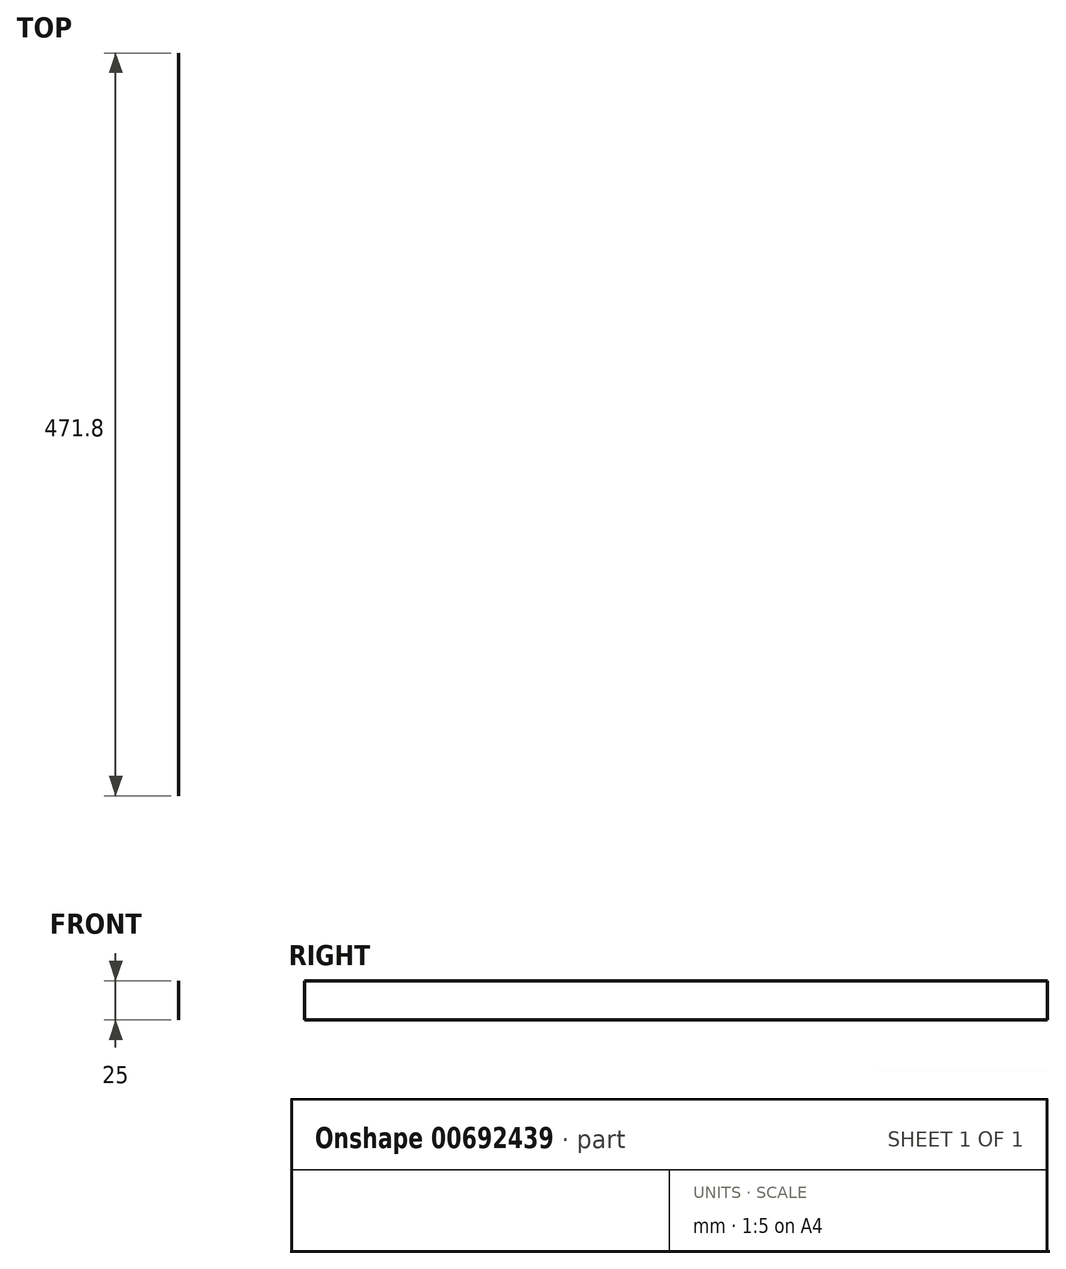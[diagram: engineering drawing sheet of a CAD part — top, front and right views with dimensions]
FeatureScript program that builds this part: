
annotation { "Feature Type Name" : "Feature", "Feature Type Description" : "" }
export const myFeature = defineFeature(function(context is Context, id is Id, definition is map)
    precondition{}
    {
        {
            var Q0;
            Q0=qCreatedBy(makeId("Top.planeOp"),FACE);
            var sketch = newSketch(context, id + "F0", { "sketchPlane" : qUnion([Q0])});
            skArc(sketch, "E0", {"start": v(533.57, 74.78) * mm, "mid": v(533.2, 75.41) * mm, "end": v(532.52, 75.66) * mm});
            skArc(sketch, "E1", {"start": v(533.22, 63.96) * mm, "mid": v(533.99, 69.35) * mm, "end": v(533.57, 74.78) * mm});
            skArc(sketch, "E2", {"start": v(528.74, 75.66) * mm, "mid": v(528, 75.36) * mm, "end": v(527.67, 74.63) * mm});
            skArc(sketch, "E3", {"start": v(532.18, 63.16) * mm, "mid": v(532.84, 63.38) * mm, "end": v(533.22, 63.96) * mm});
            skArc(sketch, "E4", {"start": v(527.25, 64.27) * mm, "mid": v(527.54, 63.49) * mm, "end": v(528.31, 63.16) * mm});
            skArc(sketch, "E5", {"start": v(670.33, -65.37) * mm, "mid": v(670, -64.64) * mm, "end": v(669.26, -64.34) * mm});
            skArc(sketch, "E6", {"start": v(669.69, -76.84) * mm, "mid": v(670.46, -76.51) * mm, "end": v(670.75, -75.73) * mm});
            skArc(sketch, "E7", {"start": v(665.48, -64.34) * mm, "mid": v(664.8, -64.59) * mm, "end": v(664.43, -65.22) * mm});
            skArc(sketch, "E8", {"start": v(664.43, -65.22) * mm, "mid": v(664.01, -70.65) * mm, "end": v(664.78, -76.04) * mm});
            skArc(sketch, "E9", {"start": v(664.78, -76.04) * mm, "mid": v(665.16, -76.62) * mm, "end": v(665.82, -76.84) * mm});
            skArc(sketch, "E10", {"start": v(704.93, -60.77) * mm, "mid": v(705.69, -60.46) * mm, "end": v(706, -59.7) * mm});
            skArc(sketch, "E11", {"start": v(672, -59.7) * mm, "mid": v(672.31, -60.46) * mm, "end": v(673.07, -60.77) * mm});
            skArc(sketch, "E12", {"start": v(706, -51.99) * mm, "mid": v(705.9, -51.55) * mm, "end": v(705.64, -51.19) * mm});
            skArc(sketch, "E13", {"start": v(672.36, -51.19) * mm, "mid": v(672.1, -51.55) * mm, "end": v(672, -51.99) * mm});
            skCircle(sketch, "E14", {"center": v(641.5, 233.4) * mm, "radius": 1.6 * mm});
            skCircle(sketch, "E15", {"center": v(614.5, 218.4) * mm, "radius": 1.6 * mm});
            skCircle(sketch, "E16", {"center": v(645.5, 187.4) * mm, "radius": 1.6 * mm});
            skCircle(sketch, "E17", {"center": v(614.5, 187.4) * mm, "radius": 1.6 * mm});
            skCircle(sketch, "E18", {"center": v(570.5, -185.55) * mm, "radius": 1.6 * mm});
            skCircle(sketch, "E19", {"center": v(570.5, -210.55) * mm, "radius": 1.6 * mm});
            skCircle(sketch, "E20", {"center": v(557.4, -171.86) * mm, "radius": 1.6 * mm});
            skCircle(sketch, "E21", {"center": v(640.6, -171.86) * mm, "radius": 1.6 * mm});
            skCircle(sketch, "E22", {"center": v(640, -195.9) * mm, "radius": 19 * mm});
            skCircle(sketch, "E23", {"center": v(723.7, -171.86) * mm, "radius": 1.6 * mm});
            skCircle(sketch, "E24", {"center": v(746.5, -171.86) * mm, "radius": 1.6 * mm});
            skCircle(sketch, "E25", {"center": v(746.5, -56.79) * mm, "radius": 1.6 * mm});
            skCircle(sketch, "E26", {"center": v(746.5, 58.28) * mm, "radius": 1.6 * mm});
            skCircle(sketch, "E27", {"center": v(746.5, 173.35) * mm, "radius": 1.6 * mm});
            skCircle(sketch, "E28", {"center": v(706.5, 233.4) * mm, "radius": 1.6 * mm});
            skCircle(sketch, "E29", {"center": v(645.5, 218.4) * mm, "radius": 1.6 * mm});
            skCircle(sketch, "E30", {"center": v(630, 202.9) * mm, "radius": 11 * mm});
            skCircle(sketch, "E31", {"center": v(568, 202.9) * mm, "radius": 11 * mm});
            skCircle(sketch, "E32", {"center": v(583.5, 218.4) * mm, "radius": 1.6 * mm});
            skCircle(sketch, "E33", {"center": v(583.5, 187.4) * mm, "radius": 1.6 * mm});
            skCircle(sketch, "E34", {"center": v(552.5, 187.4) * mm, "radius": 1.6 * mm});
            skCircle(sketch, "E35", {"center": v(552.5, 218.4) * mm, "radius": 1.6 * mm});
            skCircle(sketch, "E36", {"center": v(556.5, 233.4) * mm, "radius": 1.6 * mm});
            skCircle(sketch, "E37", {"center": v(491.5, 233.4) * mm, "radius": 1.6 * mm});
            skCircle(sketch, "E38", {"center": v(451.5, 173.35) * mm, "radius": 1.6 * mm});
            skCircle(sketch, "E39", {"center": v(451.5, 58.28) * mm, "radius": 1.6 * mm});
            skCircle(sketch, "E40", {"center": v(451.5, -171.86) * mm, "radius": 1.6 * mm});
            skCircle(sketch, "E41", {"center": v(474.3, -171.86) * mm, "radius": 1.6 * mm});
            skCircle(sketch, "E42", {"center": v(451.5, -56.79) * mm, "radius": 1.6 * mm});
            skCircle(sketch, "E43", {"center": v(704.86, -209.99) * mm, "radius": 1.6 * mm});
            skCircle(sketch, "E44", {"center": v(698.86, -217.99) * mm, "radius": 1.6 * mm});
            skCircle(sketch, "E45", {"center": v(692.86, -209.99) * mm, "radius": 1.6 * mm});
            skCircle(sketch, "E46", {"center": v(504.86, -209.99) * mm, "radius": 1.6 * mm});
            skCircle(sketch, "E47", {"center": v(498.86, -217.99) * mm, "radius": 1.6 * mm});
            skCircle(sketch, "E48", {"center": v(492.86, -209.99) * mm, "radius": 1.6 * mm});
            skCircle(sketch, "E49", {"center": v(690.74, 170.86) * mm, "radius": 1.6 * mm});
            skCircle(sketch, "E50", {"center": v(716, 217.9) * mm, "radius": 1.6 * mm});
            skCircle(sketch, "E51", {"center": v(507.26, 170.86) * mm, "radius": 1.6 * mm});
            skCircle(sketch, "E52", {"center": v(482, 217.9) * mm, "radius": 1.6 * mm});
            skCircle(sketch, "E53", {"center": v(623.6, -161.7) * mm, "radius": 1.6 * mm});
            skCircle(sketch, "E54", {"center": v(623.6, -140.1) * mm, "radius": 1.6 * mm});
            skCircle(sketch, "E55", {"center": v(618.3, -131.9) * mm, "radius": 1.6 * mm});
            skCircle(sketch, "E56", {"center": v(579.7, -131.9) * mm, "radius": 1.6 * mm});
            skCircle(sketch, "E57", {"center": v(574.4, -140.1) * mm, "radius": 1.6 * mm});
            skCircle(sketch, "E58", {"center": v(574.4, -161.7) * mm, "radius": 1.6 * mm});
            skArc(sketch, "E59", {"start": v(574.43, 4.56) * mm, "mid": v(574.01, -0.87) * mm, "end": v(574.78, -6.27) * mm});
            skArc(sketch, "E60", {"start": v(623.22, -6.27) * mm, "mid": v(623.99, -0.87) * mm, "end": v(623.57, 4.56) * mm});
            skArc(sketch, "E61", {"start": v(617.25, -5.96) * mm, "mid": v(617.54, -6.74) * mm, "end": v(618.31, -7.07) * mm});
            skArc(sketch, "E62", {"start": v(574.78, -6.27) * mm, "mid": v(575.16, -6.85) * mm, "end": v(575.82, -7.07) * mm});
            skArc(sketch, "E63", {"start": v(623.57, 4.56) * mm, "mid": v(623.2, 5.18) * mm, "end": v(622.52, 5.43) * mm});
            skArc(sketch, "E64", {"start": v(580.33, 4.4) * mm, "mid": v(580, 5.13) * mm, "end": v(579.26, 5.43) * mm});
            skArc(sketch, "E65", {"start": v(579.69, -7.07) * mm, "mid": v(580.46, -6.74) * mm, "end": v(580.75, -5.96) * mm});
            skArc(sketch, "E66", {"start": v(622.18, -7.07) * mm, "mid": v(622.84, -6.85) * mm, "end": v(623.22, -6.27) * mm});
            skArc(sketch, "E67", {"start": v(618.74, 5.43) * mm, "mid": v(618, 5.13) * mm, "end": v(617.67, 4.4) * mm});
            skArc(sketch, "E68", {"start": v(575.48, 5.43) * mm, "mid": v(574.8, 5.18) * mm, "end": v(574.43, 4.56) * mm});
            skArc(sketch, "E69", {"start": v(582.36, 18.59) * mm, "mid": v(582.1, 18.22) * mm, "end": v(582, 17.79) * mm});
            skArc(sketch, "E70", {"start": v(582, 10.07) * mm, "mid": v(582.31, 9.31) * mm, "end": v(583.07, 9) * mm});
            skArc(sketch, "E71", {"start": v(616, 17.79) * mm, "mid": v(615.9, 18.22) * mm, "end": v(615.64, 18.59) * mm});
            skArc(sketch, "E72", {"start": v(614.93, 9) * mm, "mid": v(615.69, 9.31) * mm, "end": v(616, 10.07) * mm});
            skArc(sketch, "E73", {"start": v(707.25, -75.73) * mm, "mid": v(707.54, -76.51) * mm, "end": v(708.31, -76.84) * mm});
            skArc(sketch, "E74", {"start": v(712.18, -76.84) * mm, "mid": v(712.84, -76.62) * mm, "end": v(713.22, -76.04) * mm});
            skArc(sketch, "E75", {"start": v(708.74, -64.34) * mm, "mid": v(708, -64.64) * mm, "end": v(707.67, -65.37) * mm});
            skArc(sketch, "E76", {"start": v(713.22, -76.04) * mm, "mid": v(713.99, -70.65) * mm, "end": v(713.57, -65.22) * mm});
            skArc(sketch, "E77", {"start": v(713.57, -65.22) * mm, "mid": v(713.2, -64.59) * mm, "end": v(712.52, -64.34) * mm});
            skArc(sketch, "E78", {"start": v(484.78, 63.96) * mm, "mid": v(485.16, 63.38) * mm, "end": v(485.82, 63.16) * mm});
            skArc(sketch, "E79", {"start": v(484.43, 74.78) * mm, "mid": v(484.01, 69.35) * mm, "end": v(484.78, 63.96) * mm});
            skArc(sketch, "E80", {"start": v(485.48, 75.66) * mm, "mid": v(484.8, 75.41) * mm, "end": v(484.43, 74.78) * mm});
            skArc(sketch, "E81", {"start": v(489.69, 63.16) * mm, "mid": v(490.46, 63.49) * mm, "end": v(490.75, 64.27) * mm});
            skArc(sketch, "E82", {"start": v(490.33, 74.63) * mm, "mid": v(490, 75.36) * mm, "end": v(489.26, 75.66) * mm});
            skArc(sketch, "E83", {"start": v(492.36, 88.81) * mm, "mid": v(492.1, 88.45) * mm, "end": v(492, 88.01) * mm});
            skArc(sketch, "E84", {"start": v(526, 88.01) * mm, "mid": v(525.9, 88.45) * mm, "end": v(525.64, 88.81) * mm});
            skArc(sketch, "E85", {"start": v(492, 80.3) * mm, "mid": v(492.31, 79.54) * mm, "end": v(493.07, 79.23) * mm});
            skArc(sketch, "E86", {"start": v(524.93, 79.23) * mm, "mid": v(525.69, 79.54) * mm, "end": v(526, 80.3) * mm});
            skCircle(sketch, "E87", {"center": v(595, -178.9) * mm, "radius": 1.8 * mm});
            skCircle(sketch, "E88", {"center": v(656, -179.9) * mm, "radius": 1.8 * mm});
            skCircle(sketch, "E89", {"center": v(656, -211.9) * mm, "radius": 1.8 * mm});
            skLineSegment(sketch, "E90", {"start": v(526, 88.01) * mm, "end": v(526, 80.3) * mm});
            skLineSegment(sketch, "E91", {"start": v(492, 80.3) * mm, "end": v(492, 88.01) * mm});
            skArc(sketch, "E92", {"start": v(525.64, 88.81) * mm, "mid": v(509, 95.16) * mm, "end": v(492.36, 88.81) * mm});
            skLineSegment(sketch, "E93", {"start": v(490.33, 74.63) * mm, "end": v(490.75, 64.27) * mm});
            skLineSegment(sketch, "E94", {"start": v(485.48, 75.66) * mm, "end": v(489.26, 75.66) * mm});
            skLineSegment(sketch, "E95", {"start": v(489.69, 63.16) * mm, "end": v(485.82, 63.16) * mm});
            skLineSegment(sketch, "E96", {"start": v(708.74, -64.34) * mm, "end": v(712.52, -64.34) * mm});
            skLineSegment(sketch, "E97", {"start": v(707.25, -75.73) * mm, "end": v(707.67, -65.37) * mm});
            skLineSegment(sketch, "E98", {"start": v(712.18, -76.84) * mm, "end": v(708.31, -76.84) * mm});
            skLineSegment(sketch, "E99", {"start": v(616, 17.79) * mm, "end": v(616, 10.07) * mm});
            skArc(sketch, "E100", {"start": v(615.64, 18.59) * mm, "mid": v(599, 24.93) * mm, "end": v(582.36, 18.59) * mm});
            skLineSegment(sketch, "E101", {"start": v(580.33, 4.4) * mm, "end": v(580.75, -5.96) * mm});
            skLineSegment(sketch, "E102", {"start": v(617.25, -5.96) * mm, "end": v(617.67, 4.4) * mm});
            skLineSegment(sketch, "E103", {"start": v(575.48, 5.43) * mm, "end": v(579.26, 5.43) * mm});
            skLineSegment(sketch, "E104", {"start": v(579.69, -7.07) * mm, "end": v(575.82, -7.07) * mm});
            skLineSegment(sketch, "E105", {"start": v(618.74, 5.43) * mm, "end": v(622.52, 5.43) * mm});
            skLineSegment(sketch, "E106", {"start": v(622.18, -7.07) * mm, "end": v(618.31, -7.07) * mm});
            skLineSegment(sketch, "E107", {"start": v(614.93, 9) * mm, "end": v(583.07, 9) * mm});
            skLineSegment(sketch, "E108", {"start": v(582, 10.07) * mm, "end": v(582, 17.79) * mm});
            skLineSegment(sketch, "E109", {"start": v(591.07, 177.78) * mm, "end": v(588.25, 174.96) * mm});
            skLineSegment(sketch, "E110", {"start": v(592.49, 176.37) * mm, "end": v(591.07, 177.78) * mm});
            skLineSegment(sketch, "E111", {"start": v(589.66, 173.54) * mm, "end": v(592.49, 176.37) * mm});
            skLineSegment(sketch, "E112", {"start": v(588.25, 174.96) * mm, "end": v(589.66, 173.54) * mm});
            skLineSegment(sketch, "E113", {"start": v(599.56, 169.3) * mm, "end": v(596.73, 166.47) * mm});
            skLineSegment(sketch, "E114", {"start": v(600.97, 167.88) * mm, "end": v(599.56, 169.3) * mm});
            skLineSegment(sketch, "E115", {"start": v(598.15, 165.06) * mm, "end": v(600.97, 167.88) * mm});
            skLineSegment(sketch, "E116", {"start": v(596.73, 166.47) * mm, "end": v(598.15, 165.06) * mm});
            skLineSegment(sketch, "E117", {"start": v(548.15, 165.06) * mm, "end": v(550.97, 167.88) * mm});
            skLineSegment(sketch, "E118", {"start": v(550.97, 167.88) * mm, "end": v(549.56, 169.3) * mm});
            skLineSegment(sketch, "E119", {"start": v(542.49, 176.37) * mm, "end": v(541.07, 177.78) * mm});
            skLineSegment(sketch, "E120", {"start": v(539.66, 173.54) * mm, "end": v(542.49, 176.37) * mm});
            skLineSegment(sketch, "E121", {"start": v(538.25, 174.96) * mm, "end": v(539.66, 173.54) * mm});
            skLineSegment(sketch, "E122", {"start": v(541.07, 177.78) * mm, "end": v(538.25, 174.96) * mm});
            skLineSegment(sketch, "E123", {"start": v(549.56, 169.3) * mm, "end": v(546.73, 166.47) * mm});
            skLineSegment(sketch, "E124", {"start": v(546.73, 166.47) * mm, "end": v(548.15, 165.06) * mm});
            skLineSegment(sketch, "E125", {"start": v(549.05, -13.73) * mm, "end": v(549.05, -9.73) * mm});
            skLineSegment(sketch, "E126", {"start": v(547.05, -13.73) * mm, "end": v(549.05, -13.73) * mm});
            skLineSegment(sketch, "E127", {"start": v(547.05, -9.73) * mm, "end": v(547.05, -13.73) * mm});
            skLineSegment(sketch, "E128", {"start": v(549.05, -9.73) * mm, "end": v(547.05, -9.73) * mm});
            skLineSegment(sketch, "E129", {"start": v(537.05, -13.73) * mm, "end": v(537.05, -9.73) * mm});
            skLineSegment(sketch, "E130", {"start": v(535.05, -13.73) * mm, "end": v(537.05, -13.73) * mm});
            skLineSegment(sketch, "E131", {"start": v(535.05, -9.73) * mm, "end": v(535.05, -13.73) * mm});
            skLineSegment(sketch, "E132", {"start": v(537.05, -9.73) * mm, "end": v(535.05, -9.73) * mm});
            skLineSegment(sketch, "E133", {"start": v(549.05, -113.73) * mm, "end": v(549.05, -109.73) * mm});
            skLineSegment(sketch, "E134", {"start": v(547.05, -113.73) * mm, "end": v(549.05, -113.73) * mm});
            skLineSegment(sketch, "E135", {"start": v(547.05, -109.73) * mm, "end": v(547.05, -113.73) * mm});
            skLineSegment(sketch, "E136", {"start": v(549.05, -109.73) * mm, "end": v(547.05, -109.73) * mm});
            skLineSegment(sketch, "E137", {"start": v(537.05, -113.73) * mm, "end": v(537.05, -109.73) * mm});
            skLineSegment(sketch, "E138", {"start": v(535.05, -113.73) * mm, "end": v(537.05, -113.73) * mm});
            skLineSegment(sketch, "E139", {"start": v(535.05, -109.73) * mm, "end": v(535.05, -113.73) * mm});
            skLineSegment(sketch, "E140", {"start": v(537.05, -109.73) * mm, "end": v(535.05, -109.73) * mm});
            skLineSegment(sketch, "E141", {"start": v(549.05, 86.27) * mm, "end": v(549.05, 90.27) * mm});
            skLineSegment(sketch, "E142", {"start": v(547.05, 86.27) * mm, "end": v(549.05, 86.27) * mm});
            skLineSegment(sketch, "E143", {"start": v(547.05, 90.27) * mm, "end": v(547.05, 86.27) * mm});
            skLineSegment(sketch, "E144", {"start": v(549.05, 90.27) * mm, "end": v(547.05, 90.27) * mm});
            skLineSegment(sketch, "E145", {"start": v(537.05, 86.27) * mm, "end": v(537.05, 90.27) * mm});
            skLineSegment(sketch, "E146", {"start": v(535.05, 86.27) * mm, "end": v(537.05, 86.27) * mm});
            skLineSegment(sketch, "E147", {"start": v(535.05, 90.27) * mm, "end": v(535.05, 86.27) * mm});
            skLineSegment(sketch, "E148", {"start": v(537.05, 90.27) * mm, "end": v(535.05, 90.27) * mm});
            skLineSegment(sketch, "E149", {"start": v(576.9, -146.4) * mm, "end": v(576.9, -155.4) * mm});
            skLineSegment(sketch, "E150", {"start": v(576.9, -155.4) * mm, "end": v(571.9, -155.4) * mm});
            skLineSegment(sketch, "E151", {"start": v(571.9, -155.4) * mm, "end": v(571.9, -146.4) * mm});
            skLineSegment(sketch, "E152", {"start": v(571.9, -146.4) * mm, "end": v(576.9, -146.4) * mm});
            skLineSegment(sketch, "E153", {"start": v(611.5, -129.4) * mm, "end": v(611.5, -134.4) * mm});
            skLineSegment(sketch, "E154", {"start": v(611.5, -134.4) * mm, "end": v(586.5, -134.4) * mm});
            skLineSegment(sketch, "E155", {"start": v(586.5, -134.4) * mm, "end": v(586.5, -129.4) * mm});
            skLineSegment(sketch, "E156", {"start": v(586.5, -129.4) * mm, "end": v(611.5, -129.4) * mm});
            skLineSegment(sketch, "E157", {"start": v(626.1, -146.4) * mm, "end": v(626.1, -155.4) * mm});
            skLineSegment(sketch, "E158", {"start": v(626.1, -155.4) * mm, "end": v(621.1, -155.4) * mm});
            skLineSegment(sketch, "E159", {"start": v(621.1, -155.4) * mm, "end": v(621.1, -146.4) * mm});
            skLineSegment(sketch, "E160", {"start": v(621.1, -146.4) * mm, "end": v(626.1, -146.4) * mm});
            skLineSegment(sketch, "E161", {"start": v(557.77, -204.9) * mm, "end": v(549.27, -204.9) * mm});
            skLineSegment(sketch, "E162", {"start": v(549.27, -204.9) * mm, "end": v(549.27, -191.5) * mm});
            skLineSegment(sketch, "E163", {"start": v(557.77, -191.5) * mm, "end": v(557.77, -204.9) * mm});
            skLineSegment(sketch, "E164", {"start": v(606.6, 224.42) * mm, "end": v(606.6, 228.42) * mm});
            skLineSegment(sketch, "E165", {"start": v(604.6, 224.42) * mm, "end": v(606.6, 224.42) * mm});
            skLineSegment(sketch, "E166", {"start": v(604.6, 228.42) * mm, "end": v(604.6, 224.42) * mm});
            skLineSegment(sketch, "E167", {"start": v(606.6, 228.42) * mm, "end": v(604.6, 228.42) * mm});
            skLineSegment(sketch, "E168", {"start": v(594.6, 224.42) * mm, "end": v(594.6, 228.42) * mm});
            skLineSegment(sketch, "E169", {"start": v(592.61, 224.42) * mm, "end": v(594.6, 224.42) * mm});
            skLineSegment(sketch, "E170", {"start": v(592.61, 228.42) * mm, "end": v(592.61, 224.42) * mm});
            skLineSegment(sketch, "E171", {"start": v(594.6, 228.42) * mm, "end": v(592.61, 228.42) * mm});
            skArc(sketch, "E172", {"start": v(590.35, 204.2) * mm, "mid": v(591.23, 202.07) * mm, "end": v(593.35, 201.2) * mm});
            skLineSegment(sketch, "E173", {"start": v(593.35, 201.2) * mm, "end": v(604.65, 201.2) * mm});
            skArc(sketch, "E174", {"start": v(604.65, 201.2) * mm, "mid": v(606.77, 202.07) * mm, "end": v(607.65, 204.2) * mm});
            skLineSegment(sketch, "E175", {"start": v(590.35, 217.7) * mm, "end": v(590.35, 204.2) * mm});
            skLineSegment(sketch, "E176", {"start": v(607.65, 204.2) * mm, "end": v(607.65, 217.7) * mm});
            skArc(sketch, "E177", {"start": v(607.65, 217.7) * mm, "mid": v(606.77, 219.81) * mm, "end": v(604.65, 220.7) * mm});
            skLineSegment(sketch, "E178", {"start": v(604.65, 220.7) * mm, "end": v(593.35, 220.7) * mm});
            skArc(sketch, "E179", {"start": v(593.35, 220.7) * mm, "mid": v(591.23, 219.81) * mm, "end": v(590.35, 217.7) * mm});
            skLineSegment(sketch, "E180", {"start": v(549.05, -183.73) * mm, "end": v(547.05, -183.73) * mm});
            skLineSegment(sketch, "E181", {"start": v(547.05, -183.73) * mm, "end": v(547.05, -179.73) * mm});
            skLineSegment(sketch, "E182", {"start": v(549.05, -179.73) * mm, "end": v(549.05, -183.73) * mm});
            skLineSegment(sketch, "E183", {"start": v(547.05, -179.73) * mm, "end": v(549.05, -179.73) * mm});
            skLineSegment(sketch, "E184", {"start": v(749, -235.9) * mm, "end": v(749, 235.9) * mm});
            skLineSegment(sketch, "E185", {"start": v(749, 235.9) * mm, "end": v(449, 235.9) * mm});
            skLineSegment(sketch, "E186", {"start": v(449, 235.9) * mm, "end": v(449, -235.9) * mm});
            skLineSegment(sketch, "E187", {"start": v(524.93, 79.23) * mm, "end": v(493.07, 79.23) * mm});
            skLineSegment(sketch, "E188", {"start": v(607, -214.4) * mm, "end": v(583, -214.4) * mm});
            skLineSegment(sketch, "E189", {"start": v(583, -214.4) * mm, "end": v(583, -183.4) * mm});
            skLineSegment(sketch, "E190", {"start": v(583, -183.4) * mm, "end": v(607, -183.4) * mm});
            skLineSegment(sketch, "E191", {"start": v(607, -183.4) * mm, "end": v(607, -214.4) * mm});
            skLineSegment(sketch, "E192", {"start": v(577, -205.55) * mm, "end": v(564, -205.55) * mm});
            skLineSegment(sketch, "E193", {"start": v(564, -205.55) * mm, "end": v(564, -190.55) * mm});
            skLineSegment(sketch, "E194", {"start": v(564, -190.55) * mm, "end": v(577, -190.55) * mm});
            skLineSegment(sketch, "E195", {"start": v(577, -190.55) * mm, "end": v(577, -205.55) * mm});
            skLineSegment(sketch, "E196", {"start": v(535.05, -179.73) * mm, "end": v(537.05, -179.73) * mm});
            skLineSegment(sketch, "E197", {"start": v(535.05, -183.73) * mm, "end": v(535.05, -179.73) * mm});
            skLineSegment(sketch, "E198", {"start": v(537.05, -179.73) * mm, "end": v(537.05, -183.73) * mm});
            skLineSegment(sketch, "E199", {"start": v(537.05, -183.73) * mm, "end": v(535.05, -183.73) * mm});
            skLineSegment(sketch, "E200", {"start": v(549.27, -191.5) * mm, "end": v(557.77, -191.5) * mm});
            skArc(sketch, "E201", {"start": v(719, -235.9) * mm, "mid": v(599, -227.33) * mm, "end": v(479, -235.9) * mm});
            skLineSegment(sketch, "E202", {"start": v(479, -235.9) * mm, "end": v(449, -235.9) * mm});
            skLineSegment(sketch, "E203", {"start": v(749, -235.9) * mm, "end": v(719, -235.9) * mm});
            skArc(sketch, "E204", {"start": v(705.64, -51.19) * mm, "mid": v(689, -44.84) * mm, "end": v(672.36, -51.19) * mm});
            skLineSegment(sketch, "E205", {"start": v(672, -59.7) * mm, "end": v(672, -51.99) * mm});
            skLineSegment(sketch, "E206", {"start": v(706, -51.99) * mm, "end": v(706, -59.7) * mm});
            skLineSegment(sketch, "E207", {"start": v(704.93, -60.77) * mm, "end": v(673.07, -60.77) * mm});
            skLineSegment(sketch, "E208", {"start": v(669.69, -76.84) * mm, "end": v(665.82, -76.84) * mm});
            skLineSegment(sketch, "E209", {"start": v(665.48, -64.34) * mm, "end": v(669.26, -64.34) * mm});
            skLineSegment(sketch, "E210", {"start": v(670.33, -65.37) * mm, "end": v(670.75, -75.73) * mm});
            skLineSegment(sketch, "E211", {"start": v(532.18, 63.16) * mm, "end": v(528.31, 63.16) * mm});
            skLineSegment(sketch, "E212", {"start": v(527.25, 64.27) * mm, "end": v(527.67, 74.63) * mm});
            skLineSegment(sketch, "E213", {"start": v(528.74, 75.66) * mm, "end": v(532.52, 75.66) * mm});
            skLineSegment(sketch, "E214", {"start": v(897.44, -172.86) * mm, "end": v(915.64, -172.86) * mm});
            skLineSegment(sketch, "E215", {"start": v(885.88, -182.05) * mm, "end": v(884.93, -182.6) * mm});
            skLineSegment(sketch, "E216", {"start": v(881.98, -184.3) * mm, "end": v(881.03, -184.85) * mm});
            skLineSegment(sketch, "E217", {"start": v(880.03, -183.12) * mm, "end": v(880.98, -182.57) * mm});
            skLineSegment(sketch, "E218", {"start": v(883.93, -180.87) * mm, "end": v(884.88, -180.32) * mm});
            skLineSegment(sketch, "E219", {"start": v(883.43, -180) * mm, "end": v(880.48, -181.7) * mm});
            skLineSegment(sketch, "E220", {"start": v(883.93, -180.87) * mm, "end": v(883.43, -180) * mm});
            skLineSegment(sketch, "E221", {"start": v(885.88, -182.05) * mm, "end": v(884.88, -180.32) * mm});
            skLineSegment(sketch, "E222", {"start": v(887.43, -186.93) * mm, "end": v(884.93, -182.6) * mm});
            skLineSegment(sketch, "E223", {"start": v(893.75, -183.28) * mm, "end": v(887.43, -186.93) * mm});
            skLineSegment(sketch, "E224", {"start": v(896.25, -187.61) * mm, "end": v(893.75, -183.28) * mm});
            skLineSegment(sketch, "E225", {"start": v(915.64, -176.42) * mm, "end": v(896.25, -187.61) * mm});
            skLineSegment(sketch, "E226", {"start": v(915.64, -172.86) * mm, "end": v(915.64, -176.42) * mm});
            skLineSegment(sketch, "E227", {"start": v(897.44, -177.86) * mm, "end": v(897.44, -172.86) * mm});
            skLineSegment(sketch, "E228", {"start": v(897.44, -177.86) * mm, "end": v(898.54, -177.86) * mm});
            skLineSegment(sketch, "E229", {"start": v(898.54, -177.86) * mm, "end": v(898.54, -179.86) * mm});
            skLineSegment(sketch, "E230", {"start": v(898.54, -179.86) * mm, "end": v(897.44, -179.86) * mm});
            skLineSegment(sketch, "E231", {"start": v(897.44, -180.86) * mm, "end": v(897.44, -179.86) * mm});
            skLineSegment(sketch, "E232", {"start": v(894.04, -180.86) * mm, "end": v(897.44, -180.86) * mm});
            skLineSegment(sketch, "E233", {"start": v(894.04, -179.86) * mm, "end": v(894.04, -180.86) * mm});
            skLineSegment(sketch, "E234", {"start": v(894.04, -179.86) * mm, "end": v(892.94, -179.86) * mm});
            skLineSegment(sketch, "E235", {"start": v(892.94, -179.86) * mm, "end": v(892.94, -177.86) * mm});
            skLineSegment(sketch, "E236", {"start": v(892.94, -177.86) * mm, "end": v(894.04, -177.86) * mm});
            skLineSegment(sketch, "E237", {"start": v(894.04, -172.86) * mm, "end": v(894.04, -177.86) * mm});
            skLineSegment(sketch, "E238", {"start": v(865.64, -172.86) * mm, "end": v(894.04, -172.86) * mm});
            skLineSegment(sketch, "E239", {"start": v(865.64, -185.06) * mm, "end": v(865.64, -172.86) * mm});
            skLineSegment(sketch, "E240", {"start": v(870.64, -185.06) * mm, "end": v(865.64, -185.06) * mm});
            skLineSegment(sketch, "E241", {"start": v(870.64, -185.06) * mm, "end": v(870.64, -183.96) * mm});
            skLineSegment(sketch, "E242", {"start": v(870.64, -183.96) * mm, "end": v(872.64, -183.96) * mm});
            skLineSegment(sketch, "E243", {"start": v(872.64, -183.96) * mm, "end": v(872.64, -185.06) * mm});
            skLineSegment(sketch, "E244", {"start": v(873.64, -185.06) * mm, "end": v(872.64, -185.06) * mm});
            skLineSegment(sketch, "E245", {"start": v(873.64, -188.46) * mm, "end": v(873.64, -185.06) * mm});
            skLineSegment(sketch, "E246", {"start": v(872.64, -188.46) * mm, "end": v(873.64, -188.46) * mm});
            skLineSegment(sketch, "E247", {"start": v(872.64, -188.46) * mm, "end": v(872.64, -189.56) * mm});
            skLineSegment(sketch, "E248", {"start": v(872.64, -189.56) * mm, "end": v(870.64, -189.56) * mm});
            skLineSegment(sketch, "E249", {"start": v(870.64, -189.56) * mm, "end": v(870.64, -188.46) * mm});
            skLineSegment(sketch, "E250", {"start": v(865.64, -188.46) * mm, "end": v(870.64, -188.46) * mm});
            skLineSegment(sketch, "E251", {"start": v(865.64, -202.86) * mm, "end": v(865.64, -188.46) * mm});
            skLineSegment(sketch, "E252", {"start": v(869.84, -202.86) * mm, "end": v(865.64, -202.86) * mm});
            skLineSegment(sketch, "E253", {"start": v(879.8, -197.11) * mm, "end": v(869.84, -202.86) * mm});
            skLineSegment(sketch, "E254", {"start": v(877.3, -192.78) * mm, "end": v(879.8, -197.11) * mm});
            skLineSegment(sketch, "E255", {"start": v(884.48, -188.63) * mm, "end": v(877.3, -192.78) * mm});
            skLineSegment(sketch, "E256", {"start": v(881.98, -184.3) * mm, "end": v(884.48, -188.63) * mm});
            skLineSegment(sketch, "E257", {"start": v(880.03, -183.12) * mm, "end": v(881.03, -184.85) * mm});
            skLineSegment(sketch, "E258", {"start": v(880.48, -181.7) * mm, "end": v(880.98, -182.57) * mm});
            skCircle(sketch, "E259", {"center": v(-352.5, 101.86) * mm, "radius": 1.6 * mm});
            skCircle(sketch, "E260", {"center": v(-346.5, 88.18) * mm, "radius": 1.6 * mm});
            skCircle(sketch, "E261", {"center": v(-346.5, 138.18) * mm, "radius": 1.6 * mm});
            skCircle(sketch, "E262", {"center": v(-211.5, 110.68) * mm, "radius": 3.5 * mm});
            skCircle(sketch, "E263", {"center": v(-201.5, 88.18) * mm, "radius": 1.6 * mm});
            skCircle(sketch, "E264", {"center": v(-188.3, 101.86) * mm, "radius": 1.6 * mm});
            skCircle(sketch, "E265", {"center": v(-201.5, 138.18) * mm, "radius": 1.6 * mm});
            skLineSegment(sketch, "E266", {"start": v(-190.8, 110.86) * mm, "end": v(-185.8, 110.86) * mm});
            skLineSegment(sketch, "E267", {"start": v(-190.8, 91.86) * mm, "end": v(-185.8, 91.86) * mm});
            skLineSegment(sketch, "E268", {"start": v(-185.8, 91.86) * mm, "end": v(-185.8, 110.86) * mm});
            skLineSegment(sketch, "E269", {"start": v(-190.8, 141.68) * mm, "end": v(-190.8, 110.86) * mm});
            skLineSegment(sketch, "E270", {"start": v(-350, 141.68) * mm, "end": v(-190.8, 141.68) * mm});
            skLineSegment(sketch, "E271", {"start": v(-350, 110.86) * mm, "end": v(-350, 141.68) * mm});
            skLineSegment(sketch, "E272", {"start": v(-350, 110.86) * mm, "end": v(-355, 110.86) * mm});
            skLineSegment(sketch, "E273", {"start": v(-355, 91.86) * mm, "end": v(-355, 110.86) * mm});
            skLineSegment(sketch, "E274", {"start": v(-355, 91.86) * mm, "end": v(-350, 91.86) * mm});
            skLineSegment(sketch, "E275", {"start": v(-350, 69.68) * mm, "end": v(-350, 91.86) * mm});
            skLineSegment(sketch, "E276", {"start": v(-190.8, 69.68) * mm, "end": v(-350, 69.68) * mm});
            skLineSegment(sketch, "E277", {"start": v(-190.8, 91.86) * mm, "end": v(-190.8, 69.68) * mm});
            skLineSegment(sketch, "E278", {"start": v(-237, 128.18) * mm, "end": v(-237, 86.68) * mm});
            skLineSegment(sketch, "E279", {"start": v(-237, 86.68) * mm, "end": v(-335, 86.68) * mm});
            skLineSegment(sketch, "E280", {"start": v(-335, 86.68) * mm, "end": v(-335, 128.18) * mm});
            skLineSegment(sketch, "E281", {"start": v(-335, 128.18) * mm, "end": v(-237, 128.18) * mm});
            skLineSegment(sketch, "E282", {"start": v(-1051, -170.45) * mm, "end": v(-1051, -87.6) * mm});
            skLineSegment(sketch, "E283", {"start": v(-1051, 64.1) * mm, "end": v(-761, 64.1) * mm});
            skLineSegment(sketch, "E284", {"start": v(-1046, -173.85) * mm, "end": v(-1051, -173.85) * mm});
            skLineSegment(sketch, "E285", {"start": v(-1044, -174.95) * mm, "end": v(-1046, -174.95) * mm});
            skLineSegment(sketch, "E286", {"start": v(-1043, -173.85) * mm, "end": v(-1044, -173.85) * mm});
            skLineSegment(sketch, "E287", {"start": v(-1046, -169.35) * mm, "end": v(-1044, -169.35) * mm});
            skLineSegment(sketch, "E288", {"start": v(-1051, -170.45) * mm, "end": v(-1046, -170.45) * mm});
            skLineSegment(sketch, "E289", {"start": v(-1044, -169.35) * mm, "end": v(-1044, -170.45) * mm});
            skLineSegment(sketch, "E290", {"start": v(-1044, -170.45) * mm, "end": v(-1043, -170.45) * mm});
            skLineSegment(sketch, "E291", {"start": v(-1046, -174.95) * mm, "end": v(-1046, -173.85) * mm});
            skLineSegment(sketch, "E292", {"start": v(-1044, -173.85) * mm, "end": v(-1044, -174.95) * mm});
            skLineSegment(sketch, "E293", {"start": v(-1043, -170.45) * mm, "end": v(-1043, -173.85) * mm});
            skLineSegment(sketch, "E294", {"start": v(-1046, -170.45) * mm, "end": v(-1046, -169.35) * mm});
            skLineSegment(sketch, "E295", {"start": v(-761, 64.1) * mm, "end": v(-761, 22.05) * mm});
            skLineSegment(sketch, "E296", {"start": v(-1051, 22.05) * mm, "end": v(-1051, 64.1) * mm});
            skLineSegment(sketch, "E297", {"start": v(-1051, 22.05) * mm, "end": v(-1046, 22.05) * mm});
            skLineSegment(sketch, "E298", {"start": v(-1046, 22.05) * mm, "end": v(-1046, 23.15) * mm});
            skLineSegment(sketch, "E299", {"start": v(-1046, 23.15) * mm, "end": v(-1044, 23.15) * mm});
            skLineSegment(sketch, "E300", {"start": v(-1044, 23.15) * mm, "end": v(-1044, 22.05) * mm});
            skLineSegment(sketch, "E301", {"start": v(-1044, 22.05) * mm, "end": v(-1043, 22.05) * mm});
            skLineSegment(sketch, "E302", {"start": v(-1043, 22.05) * mm, "end": v(-1043, 18.65) * mm});
            skLineSegment(sketch, "E303", {"start": v(-1043, 18.65) * mm, "end": v(-1044, 18.65) * mm});
            skLineSegment(sketch, "E304", {"start": v(-1044, 18.65) * mm, "end": v(-1044, 17.55) * mm});
            skLineSegment(sketch, "E305", {"start": v(-1044, 17.55) * mm, "end": v(-1046, 17.55) * mm});
            skLineSegment(sketch, "E306", {"start": v(-1046, 17.55) * mm, "end": v(-1046, 18.65) * mm});
            skLineSegment(sketch, "E307", {"start": v(-1046, 18.65) * mm, "end": v(-1051, 18.65) * mm});
            skLineSegment(sketch, "E308", {"start": v(-1051, -84.2) * mm, "end": v(-1051, 18.65) * mm});
            skLineSegment(sketch, "E309", {"start": v(-1051, -84.2) * mm, "end": v(-1046, -84.2) * mm});
            skLineSegment(sketch, "E310", {"start": v(-1046, -84.2) * mm, "end": v(-1046, -83.1) * mm});
            skLineSegment(sketch, "E311", {"start": v(-1046, -83.1) * mm, "end": v(-1044, -83.1) * mm});
            skLineSegment(sketch, "E312", {"start": v(-1044, -83.1) * mm, "end": v(-1044, -84.2) * mm});
            skLineSegment(sketch, "E313", {"start": v(-1044, -84.2) * mm, "end": v(-1043, -84.2) * mm});
            skLineSegment(sketch, "E314", {"start": v(-1043, -84.2) * mm, "end": v(-1043, -87.6) * mm});
            skLineSegment(sketch, "E315", {"start": v(-1043, -87.6) * mm, "end": v(-1044, -87.6) * mm});
            skLineSegment(sketch, "E316", {"start": v(-1044, -87.6) * mm, "end": v(-1044, -88.7) * mm});
            skLineSegment(sketch, "E317", {"start": v(-1044, -88.7) * mm, "end": v(-1046, -88.7) * mm});
            skLineSegment(sketch, "E318", {"start": v(-1046, -88.7) * mm, "end": v(-1046, -87.6) * mm});
            skLineSegment(sketch, "E319", {"start": v(-1046, -87.6) * mm, "end": v(-1051, -87.6) * mm});
            skLineSegment(sketch, "E320", {"start": v(-1051, -235.9) * mm, "end": v(-1051, -173.85) * mm});
            skLineSegment(sketch, "E321", {"start": v(-761, -235.9) * mm, "end": v(-1051, -235.9) * mm});
            skLineSegment(sketch, "E322", {"start": v(-761, -193.85) * mm, "end": v(-761, -235.9) * mm});
            skLineSegment(sketch, "E323", {"start": v(-761, -193.85) * mm, "end": v(-766, -193.85) * mm});
            skLineSegment(sketch, "E324", {"start": v(-766, -193.85) * mm, "end": v(-766, -194.9) * mm});
            skLineSegment(sketch, "E325", {"start": v(-766, -194.9) * mm, "end": v(-768, -194.9) * mm});
            skLineSegment(sketch, "E326", {"start": v(-768, -194.9) * mm, "end": v(-768, -193.85) * mm});
            skLineSegment(sketch, "E327", {"start": v(-768, -193.85) * mm, "end": v(-769, -193.85) * mm});
            skLineSegment(sketch, "E328", {"start": v(-769, -193.85) * mm, "end": v(-769, -190.45) * mm});
            skLineSegment(sketch, "E329", {"start": v(-769, -190.45) * mm, "end": v(-768, -190.45) * mm});
            skLineSegment(sketch, "E330", {"start": v(-768, -190.45) * mm, "end": v(-768, -189.35) * mm});
            skLineSegment(sketch, "E331", {"start": v(-768, -189.35) * mm, "end": v(-766, -189.35) * mm});
            skLineSegment(sketch, "E332", {"start": v(-766, -189.35) * mm, "end": v(-766, -190.45) * mm});
            skLineSegment(sketch, "E333", {"start": v(-766, -190.45) * mm, "end": v(-761, -190.45) * mm});
            skLineSegment(sketch, "E334", {"start": v(-761, -87.6) * mm, "end": v(-761, -190.45) * mm});
            skLineSegment(sketch, "E335", {"start": v(-761, -87.6) * mm, "end": v(-766, -87.6) * mm});
            skLineSegment(sketch, "E336", {"start": v(-766, -87.6) * mm, "end": v(-766, -88.7) * mm});
            skLineSegment(sketch, "E337", {"start": v(-766, -88.7) * mm, "end": v(-768, -88.7) * mm});
            skLineSegment(sketch, "E338", {"start": v(-768, -88.7) * mm, "end": v(-768, -87.6) * mm});
            skLineSegment(sketch, "E339", {"start": v(-768, -87.6) * mm, "end": v(-769, -87.6) * mm});
            skLineSegment(sketch, "E340", {"start": v(-769, -87.6) * mm, "end": v(-769, -84.2) * mm});
            skLineSegment(sketch, "E341", {"start": v(-769, -84.2) * mm, "end": v(-768, -84.2) * mm});
            skLineSegment(sketch, "E342", {"start": v(-768, -84.2) * mm, "end": v(-768, -83.1) * mm});
            skLineSegment(sketch, "E343", {"start": v(-768, -83.1) * mm, "end": v(-766, -83.1) * mm});
            skLineSegment(sketch, "E344", {"start": v(-766, -83.1) * mm, "end": v(-766, -84.2) * mm});
            skLineSegment(sketch, "E345", {"start": v(-766, -84.2) * mm, "end": v(-761, -84.2) * mm});
            skLineSegment(sketch, "E346", {"start": v(-761, 18.65) * mm, "end": v(-761, -84.2) * mm});
            skLineSegment(sketch, "E347", {"start": v(-761, 18.65) * mm, "end": v(-766, 18.65) * mm});
            skLineSegment(sketch, "E348", {"start": v(-766, 18.65) * mm, "end": v(-766, 17.55) * mm});
            skLineSegment(sketch, "E349", {"start": v(-766, 17.55) * mm, "end": v(-768, 17.55) * mm});
            skLineSegment(sketch, "E350", {"start": v(-768, 17.55) * mm, "end": v(-768, 18.65) * mm});
            skLineSegment(sketch, "E351", {"start": v(-768, 18.65) * mm, "end": v(-769, 18.65) * mm});
            skLineSegment(sketch, "E352", {"start": v(-769, 18.65) * mm, "end": v(-769, 22.05) * mm});
            skLineSegment(sketch, "E353", {"start": v(-769, 22.05) * mm, "end": v(-768, 22.05) * mm});
            skLineSegment(sketch, "E354", {"start": v(-768, 22.05) * mm, "end": v(-768, 23.15) * mm});
            skLineSegment(sketch, "E355", {"start": v(-768, 23.15) * mm, "end": v(-766, 23.15) * mm});
            skLineSegment(sketch, "E356", {"start": v(-766, 23.15) * mm, "end": v(-766, 22.05) * mm});
            skLineSegment(sketch, "E357", {"start": v(-766, 22.05) * mm, "end": v(-761, 22.05) * mm});
            skLineSegment(sketch, "E358", {"start": v(-875, -165.9) * mm, "end": v(-875, -107.9) * mm});
            skArc(sketch, "E359", {"start": v(-873, -107.9) * mm, "mid": v(-874, -106.9) * mm, "end": v(-875, -107.9) * mm});
            skLineSegment(sketch, "E360", {"start": v(-873, -107.9) * mm, "end": v(-873, -165.9) * mm});
            skArc(sketch, "E361", {"start": v(-875, -165.9) * mm, "mid": v(-874, -166.9) * mm, "end": v(-873, -165.9) * mm});
            skLineSegment(sketch, "E362", {"start": v(-881, -165.9) * mm, "end": v(-881, -107.9) * mm});
            skArc(sketch, "E363", {"start": v(-879, -107.9) * mm, "mid": v(-880, -106.9) * mm, "end": v(-881, -107.9) * mm});
            skLineSegment(sketch, "E364", {"start": v(-879, -107.9) * mm, "end": v(-879, -165.9) * mm});
            skArc(sketch, "E365", {"start": v(-881, -165.9) * mm, "mid": v(-880, -166.9) * mm, "end": v(-879, -165.9) * mm});
            skLineSegment(sketch, "E366", {"start": v(-893, -165.9) * mm, "end": v(-893, -107.9) * mm});
            skArc(sketch, "E367", {"start": v(-891, -107.9) * mm, "mid": v(-892, -106.9) * mm, "end": v(-893, -107.9) * mm});
            skLineSegment(sketch, "E368", {"start": v(-891, -107.9) * mm, "end": v(-891, -165.9) * mm});
            skArc(sketch, "E369", {"start": v(-893, -165.9) * mm, "mid": v(-892, -166.9) * mm, "end": v(-891, -165.9) * mm});
            skLineSegment(sketch, "E370", {"start": v(-887, -165.9) * mm, "end": v(-887, -107.9) * mm});
            skArc(sketch, "E371", {"start": v(-885, -107.9) * mm, "mid": v(-886, -106.9) * mm, "end": v(-887, -107.9) * mm});
            skLineSegment(sketch, "E372", {"start": v(-885, -107.9) * mm, "end": v(-885, -165.9) * mm});
            skArc(sketch, "E373", {"start": v(-887, -165.9) * mm, "mid": v(-886, -166.9) * mm, "end": v(-885, -165.9) * mm});
            skLineSegment(sketch, "E374", {"start": v(-899, -165.9) * mm, "end": v(-899, -107.9) * mm});
            skArc(sketch, "E375", {"start": v(-897, -107.9) * mm, "mid": v(-898, -106.9) * mm, "end": v(-899, -107.9) * mm});
            skLineSegment(sketch, "E376", {"start": v(-897, -107.9) * mm, "end": v(-897, -165.9) * mm});
            skArc(sketch, "E377", {"start": v(-899, -165.9) * mm, "mid": v(-898, -166.9) * mm, "end": v(-897, -165.9) * mm});
            skLineSegment(sketch, "E378", {"start": v(-905, -165.9) * mm, "end": v(-905, -107.9) * mm});
            skArc(sketch, "E379", {"start": v(-903, -107.9) * mm, "mid": v(-904, -106.9) * mm, "end": v(-905, -107.9) * mm});
            skLineSegment(sketch, "E380", {"start": v(-903, -107.9) * mm, "end": v(-903, -165.9) * mm});
            skArc(sketch, "E381", {"start": v(-905, -165.9) * mm, "mid": v(-904, -166.9) * mm, "end": v(-903, -165.9) * mm});
            skLineSegment(sketch, "E382", {"start": v(-917, -165.9) * mm, "end": v(-917, -107.9) * mm});
            skArc(sketch, "E383", {"start": v(-915, -107.9) * mm, "mid": v(-916, -106.9) * mm, "end": v(-917, -107.9) * mm});
            skLineSegment(sketch, "E384", {"start": v(-915, -107.9) * mm, "end": v(-915, -165.9) * mm});
            skArc(sketch, "E385", {"start": v(-917, -165.9) * mm, "mid": v(-916, -166.9) * mm, "end": v(-915, -165.9) * mm});
            skLineSegment(sketch, "E386", {"start": v(-911, -165.9) * mm, "end": v(-911, -107.9) * mm});
            skArc(sketch, "E387", {"start": v(-909, -107.9) * mm, "mid": v(-910, -106.9) * mm, "end": v(-911, -107.9) * mm});
            skLineSegment(sketch, "E388", {"start": v(-909, -107.9) * mm, "end": v(-909, -165.9) * mm});
            skArc(sketch, "E389", {"start": v(-911, -165.9) * mm, "mid": v(-910, -166.9) * mm, "end": v(-909, -165.9) * mm});
            skLineSegment(sketch, "E390", {"start": v(-923, -165.9) * mm, "end": v(-923, -107.9) * mm});
            skArc(sketch, "E391", {"start": v(-921, -107.9) * mm, "mid": v(-922, -106.9) * mm, "end": v(-923, -107.9) * mm});
            skLineSegment(sketch, "E392", {"start": v(-921, -107.9) * mm, "end": v(-921, -165.9) * mm});
            skArc(sketch, "E393", {"start": v(-923, -165.9) * mm, "mid": v(-922, -166.9) * mm, "end": v(-921, -165.9) * mm});
            skLineSegment(sketch, "E394", {"start": v(-929, -165.9) * mm, "end": v(-929, -107.9) * mm});
            skArc(sketch, "E395", {"start": v(-927, -107.9) * mm, "mid": v(-928, -106.9) * mm, "end": v(-929, -107.9) * mm});
            skLineSegment(sketch, "E396", {"start": v(-927, -107.9) * mm, "end": v(-927, -165.9) * mm});
            skArc(sketch, "E397", {"start": v(-929, -165.9) * mm, "mid": v(-928, -166.9) * mm, "end": v(-927, -165.9) * mm});
            skLineSegment(sketch, "E398", {"start": v(-941, -165.9) * mm, "end": v(-941, -107.9) * mm});
            skArc(sketch, "E399", {"start": v(-939, -107.9) * mm, "mid": v(-940, -106.9) * mm, "end": v(-941, -107.9) * mm});
            skLineSegment(sketch, "E400", {"start": v(-939, -107.9) * mm, "end": v(-939, -165.9) * mm});
            skArc(sketch, "E401", {"start": v(-941, -165.9) * mm, "mid": v(-940, -166.9) * mm, "end": v(-939, -165.9) * mm});
            skLineSegment(sketch, "E402", {"start": v(-935, -165.9) * mm, "end": v(-935, -107.9) * mm});
            skArc(sketch, "E403", {"start": v(-933, -107.9) * mm, "mid": v(-934, -106.9) * mm, "end": v(-935, -107.9) * mm});
            skLineSegment(sketch, "E404", {"start": v(-933, -107.9) * mm, "end": v(-933, -165.9) * mm});
            skArc(sketch, "E405", {"start": v(-935, -165.9) * mm, "mid": v(-934, -166.9) * mm, "end": v(-933, -165.9) * mm});
            skLineSegment(sketch, "E406", {"start": v(-953, -165.9) * mm, "end": v(-953, -107.9) * mm});
            skArc(sketch, "E407", {"start": v(-951, -107.9) * mm, "mid": v(-952, -106.9) * mm, "end": v(-953, -107.9) * mm});
            skLineSegment(sketch, "E408", {"start": v(-951, -107.9) * mm, "end": v(-951, -165.9) * mm});
            skArc(sketch, "E409", {"start": v(-953, -165.9) * mm, "mid": v(-952, -166.9) * mm, "end": v(-951, -165.9) * mm});
            skLineSegment(sketch, "E410", {"start": v(-947, -165.9) * mm, "end": v(-947, -107.9) * mm});
            skArc(sketch, "E411", {"start": v(-945, -107.9) * mm, "mid": v(-946, -106.9) * mm, "end": v(-947, -107.9) * mm});
            skLineSegment(sketch, "E412", {"start": v(-945, -107.9) * mm, "end": v(-945, -165.9) * mm});
            skArc(sketch, "E413", {"start": v(-947, -165.9) * mm, "mid": v(-946, -166.9) * mm, "end": v(-945, -165.9) * mm});
            skLineSegment(sketch, "E414", {"start": v(-959, -165.9) * mm, "end": v(-959, -107.9) * mm});
            skArc(sketch, "E415", {"start": v(-957, -107.9) * mm, "mid": v(-958, -106.9) * mm, "end": v(-959, -107.9) * mm});
            skLineSegment(sketch, "E416", {"start": v(-957, -107.9) * mm, "end": v(-957, -165.9) * mm});
            skArc(sketch, "E417", {"start": v(-959, -165.9) * mm, "mid": v(-958, -166.9) * mm, "end": v(-957, -165.9) * mm});
            skLineSegment(sketch, "E418", {"start": v(-965, -165.9) * mm, "end": v(-965, -107.9) * mm});
            skArc(sketch, "E419", {"start": v(-963, -107.9) * mm, "mid": v(-964, -106.9) * mm, "end": v(-965, -107.9) * mm});
            skLineSegment(sketch, "E420", {"start": v(-963, -107.9) * mm, "end": v(-963, -165.9) * mm});
            skArc(sketch, "E421", {"start": v(-965, -165.9) * mm, "mid": v(-964, -166.9) * mm, "end": v(-963, -165.9) * mm});
            skLineSegment(sketch, "E422", {"start": v(-869, -165.9) * mm, "end": v(-869, -107.9) * mm});
            skArc(sketch, "E423", {"start": v(-867, -107.9) * mm, "mid": v(-868, -106.9) * mm, "end": v(-869, -107.9) * mm});
            skLineSegment(sketch, "E424", {"start": v(-867, -107.9) * mm, "end": v(-867, -165.9) * mm});
            skArc(sketch, "E425", {"start": v(-869, -165.9) * mm, "mid": v(-868, -166.9) * mm, "end": v(-867, -165.9) * mm});
            skCircle(sketch, "E426", {"center": v(753.5, 173.4) * mm, "radius": 1.6 * mm});
            skCircle(sketch, "E427", {"center": v(753.5, 58.33) * mm, "radius": 1.6 * mm});
            skCircle(sketch, "E428", {"center": v(753.5, -56.74) * mm, "radius": 1.6 * mm});
            skCircle(sketch, "E429", {"center": v(753.5, -171.81) * mm, "radius": 1.6 * mm});
            skCircle(sketch, "E430", {"center": v(758.5, 217.4) * mm, "radius": 1.5 * mm});
            skCircle(sketch, "E431", {"center": v(793.5, 233.4) * mm, "radius": 1.6 * mm});
            skCircle(sketch, "E432", {"center": v(793.5, -171.81) * mm, "radius": 1.6 * mm});
            skCircle(sketch, "E433", {"center": v(853.5, -171.81) * mm, "radius": 1.6 * mm});
            skCircle(sketch, "E434", {"center": v(858.5, 233.4) * mm, "radius": 1.6 * mm});
            skCircle(sketch, "E435", {"center": v(859.3, -188.3) * mm, "radius": 1.6 * mm});
            skCircle(sketch, "E436", {"center": v(943.5, 233.4) * mm, "radius": 1.6 * mm});
            skCircle(sketch, "E437", {"center": v(1008.5, 233.4) * mm, "radius": 1.6 * mm});
            skCircle(sketch, "E438", {"center": v(1023.5, -188.3) * mm, "radius": 1.6 * mm});
            skCircle(sketch, "E439", {"center": v(1043.5, 217.4) * mm, "radius": 1.6 * mm});
            skCircle(sketch, "E440", {"center": v(1048.5, -56.74) * mm, "radius": 1.6 * mm});
            skCircle(sketch, "E441", {"center": v(1048.5, 58.33) * mm, "radius": 1.6 * mm});
            skCircle(sketch, "E442", {"center": v(1048.5, 173.4) * mm, "radius": 1.6 * mm});
            skCircle(sketch, "E443", {"center": v(1048.5, -171.81) * mm, "radius": 1.6 * mm});
            skLineSegment(sketch, "E444", {"start": v(1051, -235.9) * mm, "end": v(1021, -235.9) * mm});
            skArc(sketch, "E445", {"start": v(1021, -235.9) * mm, "mid": v(901, -227.33) * mm, "end": v(781, -235.9) * mm});
            skLineSegment(sketch, "E446", {"start": v(781, -235.9) * mm, "end": v(751, -235.9) * mm});
            skLineSegment(sketch, "E447", {"start": v(751, -235.9) * mm, "end": v(751, 235.9) * mm});
            skLineSegment(sketch, "E448", {"start": v(751, 235.9) * mm, "end": v(1051, 235.9) * mm});
            skLineSegment(sketch, "E449", {"start": v(1051, 235.9) * mm, "end": v(1051, -235.9) * mm});
            skLineSegment(sketch, "E450", {"start": v(1021, -209.7) * mm, "end": v(1021, 188.9) * mm});
            skArc(sketch, "E451", {"start": v(1021, 188.9) * mm, "mid": v(901, 197.47) * mm, "end": v(781, 188.9) * mm});
            skLineSegment(sketch, "E452", {"start": v(781, 188.9) * mm, "end": v(781, -169.4) * mm});
            skLineSegment(sketch, "E453", {"start": v(781, -169.4) * mm, "end": v(861.8, -169.4) * mm});
            skLineSegment(sketch, "E454", {"start": v(861.8, -169.4) * mm, "end": v(861.8, -209.7) * mm});
            skLineSegment(sketch, "E455", {"start": v(861.8, -209.7) * mm, "end": v(1021, -209.7) * mm});
            skArc(sketch, "E456", {"start": v(-25.63, 86.33) * mm, "mid": v(-30.47, 101.25) * mm, "end": v(-44.8, 107.62) * mm});
            skArc(sketch, "E457", {"start": v(-97.72, 99.4) * mm, "mid": v(-97.17, 97.72) * mm, "end": v(-95.56, 97) * mm});
            skArc(sketch, "E458", {"start": v(-54.23, 28.5) * mm, "mid": v(-37.5, 34.91) * mm, "end": v(-29.37, 50.87) * mm});
            skArc(sketch, "E459", {"start": v(-36.64, 85.84) * mm, "mid": v(-39.18, 93.66) * mm, "end": v(-46.68, 97) * mm});
            skArc(sketch, "E460", {"start": v(-102.12, 39.12) * mm, "mid": v(-103.58, 38.57) * mm, "end": v(-104.28, 37.18) * mm});
            skArc(sketch, "E461", {"start": v(-53.2, 39.12) * mm, "mid": v(-44.56, 42.44) * mm, "end": v(-40.35, 50.7) * mm});
            skEllipticalArc(sketch, "E462", {});
            skEllipticalArc(sketch, "E463", {});
            skEllipticalArc(sketch, "E464", {});
            skEllipticalArc(sketch, "E465", {});
            skEllipticalArc(sketch, "E466", {});
            skArc(sketch, "E467", {"start": v(35.2, 11.3) * mm, "mid": v(34.89, 11.47) * mm, "end": v(34.53, 11.51) * mm});
            skFitSpline(sketch, "E468", {"points": [v(67.13, 28.95) * mm, v(66.64, 29.35) * mm, v(66.36, 30.02) * mm, v(66.45, 30.83) * mm]});
            skFitSpline(sketch, "E469", {"points": [v(68.33, 28.55) * mm, v(67.87, 28.55) * mm, v(67.45, 28.7) * mm, v(67.13, 28.95) * mm]});
            skFitSpline(sketch, "E470", {"points": [v(75.4, 67.94) * mm, v(75.87, 67.94) * mm, v(76.28, 67.8) * mm, v(76.6, 67.53) * mm]});
            skFitSpline(sketch, "E471", {"points": [v(76.6, 67.53) * mm, v(77.1, 67.13) * mm, v(77.38, 66.47) * mm, v(77.3, 65.65) * mm]});
            skArc(sketch, "E472", {"start": v(-4.58, 9.19) * mm, "mid": v(-4.1, 9.28) * mm, "end": v(-3.69, 9.56) * mm});
            skEllipticalArc(sketch, "E473", {});
            skEllipticalArc(sketch, "E474", {});
            skArc(sketch, "E475", {"start": v(-4.84, 13.59) * mm, "mid": v(-4.68, 13.57) * mm, "end": v(-4.51, 13.55) * mm});
            skEllipticalArc(sketch, "E476", {});
            skEllipticalArc(sketch, "E477", {});
            skEllipticalArc(sketch, "E478", {});
            skEllipticalArc(sketch, "E479", {});
            skFitSpline(sketch, "E480", {"points": [v(-5.26, 28.95) * mm, v(-5.75, 29.35) * mm, v(-6.03, 30.02) * mm, v(-5.95, 30.83) * mm]});
            skFitSpline(sketch, "E481", {"points": [v(-4.06, 28.55) * mm, v(-4.52, 28.55) * mm, v(-4.94, 28.7) * mm, v(-5.26, 28.95) * mm]});
            skArc(sketch, "E482", {"start": v(-2.12, 175.46) * mm, "mid": v(-17.12, 160.46) * mm, "end": v(-2.12, 145.46) * mm});
            skCircle(sketch, "E483", {"center": v(101.25, -171.86) * mm, "radius": 1.6 * mm});
            skCircle(sketch, "E484", {"center": v(-5, -171.86) * mm, "radius": 1.6 * mm});
            skCircle(sketch, "E485", {"center": v(-111.25, -171.86) * mm, "radius": 1.6 * mm});
            skCircle(sketch, "E486", {"center": v(112.25, 226.15) * mm, "radius": 1.6 * mm});
            skCircle(sketch, "E487", {"center": v(132.25, 226.15) * mm, "radius": 1.6 * mm});
            skArc(sketch, "E488", {"start": v(57.88, 145.46) * mm, "mid": v(72.88, 160.46) * mm, "end": v(57.88, 175.46) * mm});
            skArc(sketch, "E489", {"start": v(9.4, 8.76) * mm, "mid": v(10, 9.4) * mm, "end": v(10.47, 10.13) * mm});
            skEllipticalArc(sketch, "E490", {});
            skEllipticalArc(sketch, "E491", {});
            skEllipticalArc(sketch, "E492", {});
            skArc(sketch, "E493", {"start": v(25.35, 14.84) * mm, "mid": v(24.98, 14.98) * mm, "end": v(24.6, 15.01) * mm});
            skEllipticalArc(sketch, "E494", {});
            skArc(sketch, "E495", {"start": v(89.92, 11.3) * mm, "mid": v(89.6, 11.47) * mm, "end": v(89.25, 11.51) * mm});
            skArc(sketch, "E496", {"start": v(-92.56, 64.71) * mm, "mid": v(-92.01, 63.03) * mm, "end": v(-90.4, 62.31) * mm});
            skArc(sketch, "E497", {"start": v(-89.76, 72.66) * mm, "mid": v(-91.2, 72.1) * mm, "end": v(-91.91, 70.72) * mm});
            skCircle(sketch, "E498", {"center": v(-5, -225.9) * mm, "radius": 1.6 * mm});
            skCircle(sketch, "E499", {"center": v(101.25, -225.9) * mm, "radius": 1.6 * mm});
            skCircle(sketch, "E500", {"center": v(-111.25, -225.9) * mm, "radius": 1.6 * mm});
            skCircle(sketch, "E501", {"center": v(-149, 201.4) * mm, "radius": 1.6 * mm});
            skArc(sketch, "E502", {"start": v(105, -235.9) * mm, "mid": v(-5, -228.39) * mm, "end": v(-115, -235.9) * mm});
            skLineSegment(sketch, "E503", {"start": v(105, -235.9) * mm, "end": v(145, -235.9) * mm});
            skLineSegment(sketch, "E504", {"start": v(-155, -235.9) * mm, "end": v(-115, -235.9) * mm});
            skLineSegment(sketch, "E505", {"start": v(-89.76, 72.66) * mm, "end": v(-64.65, 72.66) * mm});
            skLineSegment(sketch, "E506", {"start": v(-64.65, 72.66) * mm, "end": v(-65.75, 62.32) * mm});
            skLineSegment(sketch, "E507", {"start": v(-92.56, 64.71) * mm, "end": v(-91.91, 70.72) * mm});
            skLineSegment(sketch, "E508", {"start": v(-65.75, 62.32) * mm, "end": v(-90.4, 62.31) * mm});
            skFitSpline(sketch, "E509", {"points": [v(94.48, 15.93) * mm, v(94.72, 15.52) * mm, v(94.81, 15.02) * mm, v(94.75, 14.43) * mm]});
            skFitSpline(sketch, "E510", {"points": [v(94.75, 14.43) * mm, v(94.7, 13.92) * mm, v(94.54, 13.48) * mm, v(94.29, 13.11) * mm]});
            skFitSpline(sketch, "E511", {"points": [v(93.45, 16.76) * mm, v(93.9, 16.61) * mm, v(94.24, 16.33) * mm, v(94.48, 15.93) * mm]});
            skFitSpline(sketch, "E512", {"points": [v(94.29, 13.11) * mm, v(94.03, 12.74) * mm, v(93.7, 12.44) * mm, v(93.3, 12.21) * mm]});
            skEllipticalArc(sketch, "E513", {});
            skEllipticalArc(sketch, "E514", {});
            skLineSegment(sketch, "E515", {"start": v(86.71, 17) * mm, "end": v(91.45, 17) * mm});
            skEllipticalArc(sketch, "E516", {});
            skLineSegment(sketch, "E517", {"start": v(85.74, 7.78) * mm, "end": v(86.71, 17) * mm});
            skFitSpline(sketch, "E518", {"points": [v(92.96, 11.5) * mm, v(93.06, 11.43) * mm, v(93.2, 11.27) * mm, v(93.37, 11.02) * mm]});
            skLineSegment(sketch, "E519", {"start": v(88.6, 7.78) * mm, "end": v(85.74, 7.78) * mm});
            skEllipticalArc(sketch, "E520", {});
            skLineSegment(sketch, "E521", {"start": v(89, 11.52) * mm, "end": v(88.6, 7.78) * mm});
            skLineSegment(sketch, "E522", {"start": v(93.7, 10.45) * mm, "end": v(94.8, 7.78) * mm});
            skLineSegment(sketch, "E523", {"start": v(89.25, 11.52) * mm, "end": v(89, 11.52) * mm});
            skLineSegment(sketch, "E524", {"start": v(94.8, 7.78) * mm, "end": v(91.59, 7.78) * mm});
            skLineSegment(sketch, "E525", {"start": v(91.59, 7.78) * mm, "end": v(90.36, 10.6) * mm});
            skEllipticalArc(sketch, "E526", {});
            skEllipticalArc(sketch, "E527", {});
            skFitSpline(sketch, "E528", {"points": [v(90.38, 13.26) * mm, v(90.5, 13.26) * mm, v(90.76, 13.3) * mm, v(91.14, 13.39) * mm]});
            skEllipticalArc(sketch, "E529", {});
            skLineSegment(sketch, "E530", {"start": v(89.18, 13.26) * mm, "end": v(90.38, 13.26) * mm});
            skFitSpline(sketch, "E531", {"points": [v(91.87, 14.2) * mm, v(91.9, 14.5) * mm, v(91.83, 14.73) * mm, v(91.66, 14.9) * mm]});
            skLineSegment(sketch, "E532", {"start": v(89.37, 15.13) * mm, "end": v(89.18, 13.26) * mm});
            skFitSpline(sketch, "E533", {"points": [v(91.66, 14.9) * mm, v(91.49, 15.05) * mm, v(91.14, 15.13) * mm, v(90.62, 15.13) * mm]});
            skLineSegment(sketch, "E534", {"start": v(90.62, 15.13) * mm, "end": v(89.37, 15.13) * mm});
            skFitSpline(sketch, "E535", {"points": [v(77.06, 12.37) * mm, v(76.96, 11.44) * mm, v(77.06, 10.77) * mm, v(77.36, 10.36) * mm]});
            skFitSpline(sketch, "E536", {"points": [v(78.71, 9.76) * mm, v(79.32, 9.76) * mm, v(79.82, 9.95) * mm, v(80.2, 10.35) * mm]});
            skFitSpline(sketch, "E537", {"points": [v(80.2, 10.35) * mm, v(80.57, 10.75) * mm, v(80.81, 11.46) * mm, v(80.92, 12.5) * mm]});
            skEllipticalArc(sketch, "E538", {});
            skFitSpline(sketch, "E539", {"points": [v(77.8, 14.38) * mm, v(77.4, 13.98) * mm, v(77.16, 13.3) * mm, v(77.06, 12.37) * mm]});
            skLineSegment(sketch, "E540", {"start": v(68.87, 7.78) * mm, "end": v(66.02, 7.78) * mm});
            skLineSegment(sketch, "E541", {"start": v(69.6, 14.72) * mm, "end": v(68.87, 7.78) * mm});
            skLineSegment(sketch, "E542", {"start": v(66.02, 7.78) * mm, "end": v(66.75, 14.72) * mm});
            skLineSegment(sketch, "E543", {"start": v(72.5, 14.72) * mm, "end": v(69.6, 14.72) * mm});
            skLineSegment(sketch, "E544", {"start": v(66.75, 14.72) * mm, "end": v(63.85, 14.72) * mm});
            skLineSegment(sketch, "E545", {"start": v(72.74, 17) * mm, "end": v(72.5, 14.72) * mm});
            skLineSegment(sketch, "E546", {"start": v(63.85, 14.72) * mm, "end": v(64.09, 17) * mm});
            skLineSegment(sketch, "E547", {"start": v(64.09, 17) * mm, "end": v(72.74, 17) * mm});
            skLineSegment(sketch, "E548", {"start": v(58.82, 11.3) * mm, "end": v(58.15, 14.6) * mm});
            skLineSegment(sketch, "E549", {"start": v(58.15, 14.6) * mm, "end": v(56.8, 11.3) * mm});
            skLineSegment(sketch, "E550", {"start": v(56.8, 11.3) * mm, "end": v(58.82, 11.3) * mm});
            skLineSegment(sketch, "E551", {"start": v(50.23, 11.68) * mm, "end": v(45.8, 11.68) * mm});
            skLineSegment(sketch, "E552", {"start": v(50.42, 13.56) * mm, "end": v(50.23, 11.68) * mm});
            skLineSegment(sketch, "E553", {"start": v(45.8, 11.68) * mm, "end": v(45.6, 9.87) * mm});
            skLineSegment(sketch, "E554", {"start": v(46, 13.56) * mm, "end": v(50.42, 13.56) * mm});
            skLineSegment(sketch, "E555", {"start": v(45.6, 9.87) * mm, "end": v(50.52, 9.87) * mm});
            skLineSegment(sketch, "E556", {"start": v(46.15, 15.03) * mm, "end": v(46, 13.56) * mm});
            skLineSegment(sketch, "E557", {"start": v(50.52, 9.87) * mm, "end": v(50.3, 7.78) * mm});
            skLineSegment(sketch, "E558", {"start": v(50.92, 15.03) * mm, "end": v(46.15, 15.03) * mm});
            skLineSegment(sketch, "E559", {"start": v(50.3, 7.78) * mm, "end": v(42.53, 7.78) * mm});
            skLineSegment(sketch, "E560", {"start": v(51.13, 17) * mm, "end": v(50.92, 15.03) * mm});
            skLineSegment(sketch, "E561", {"start": v(42.53, 7.78) * mm, "end": v(43.5, 17) * mm});
            skLineSegment(sketch, "E562", {"start": v(43.5, 17) * mm, "end": v(51.13, 17) * mm});
            skFitSpline(sketch, "E563", {"points": [v(37.16, 14.2) * mm, v(37.19, 14.5) * mm, v(37.12, 14.73) * mm, v(36.95, 14.9) * mm]});
            skFitSpline(sketch, "E564", {"points": [v(36.95, 14.9) * mm, v(36.77, 15.05) * mm, v(36.43, 15.13) * mm, v(35.9, 15.13) * mm]});
            skLineSegment(sketch, "E565", {"start": v(35.9, 15.13) * mm, "end": v(34.66, 15.13) * mm});
            skLineSegment(sketch, "E566", {"start": v(34.66, 15.13) * mm, "end": v(34.46, 13.26) * mm});
            skLineSegment(sketch, "E567", {"start": v(34.46, 13.26) * mm, "end": v(35.66, 13.26) * mm});
            skFitSpline(sketch, "E568", {"points": [v(35.66, 13.26) * mm, v(35.8, 13.26) * mm, v(36.05, 13.3) * mm, v(36.43, 13.39) * mm]});
            skEllipticalArc(sketch, "E569", {});
            skArc(sketch, "E570", {"start": v(36.92, 13.67) * mm, "mid": v(37.08, 13.92) * mm, "end": v(37.16, 14.2) * mm});
            skFitSpline(sketch, "E571", {"points": [v(23.94, 9.76) * mm, v(24.48, 9.76) * mm, v(24.9, 9.91) * mm, v(25.22, 10.22) * mm]});
            skEllipticalArc(sketch, "E572", {});
            skFitSpline(sketch, "E573", {"points": [v(22.7, 10.33) * mm, v(22.96, 9.95) * mm, v(23.38, 9.76) * mm, v(23.94, 9.76) * mm]});
            skLineSegment(sketch, "E574", {"start": v(25.97, 11.55) * mm, "end": v(28.38, 10.8) * mm});
            skFitSpline(sketch, "E575", {"points": [v(22.45, 12.43) * mm, v(22.34, 11.4) * mm, v(22.42, 10.7) * mm, v(22.7, 10.33) * mm]});
            skEllipticalArc(sketch, "E576", {});
            skEllipticalArc(sketch, "E577", {});
            skEllipticalArc(sketch, "E578", {});
            skFitSpline(sketch, "E579", {"points": [v(25.95, 7.98) * mm, v(25.4, 7.74) * mm, v(24.7, 7.63) * mm, v(23.88, 7.63) * mm]});
            skFitSpline(sketch, "E580", {"points": [v(23.88, 7.63) * mm, v(22.88, 7.63) * mm, v(22.07, 7.77) * mm, v(21.47, 8.06) * mm]});
            skEllipticalArc(sketch, "E581", {});
            skEllipticalArc(sketch, "E582", {});
            skFitSpline(sketch, "E583", {"points": [v(26.09, 13.72) * mm, v(26.03, 14) * mm, v(25.96, 14.21) * mm, v(25.88, 14.34) * mm]});
            skEllipticalArc(sketch, "E584", {});
            skLineSegment(sketch, "E585", {"start": v(28.66, 14.28) * mm, "end": v(26.09, 13.72) * mm});
            skFitSpline(sketch, "E586", {"points": [v(19.6, 12.4) * mm, v(19.75, 13.93) * mm, v(20.28, 15.1) * mm, v(21.18, 15.92) * mm]});
            skEllipticalArc(sketch, "E587", {});
            skFitSpline(sketch, "E588", {"points": [v(24.75, 17.15) * mm, v(25.9, 17.15) * mm, v(26.8, 16.91) * mm, v(27.4, 16.44) * mm]});
            skLineSegment(sketch, "E589", {"start": v(45.04, 28) * mm, "end": v(44.88, 28) * mm});
            skLineSegment(sketch, "E590", {"start": v(33.22, 42.1) * mm, "end": v(34.46, 53.92) * mm});
            skLineSegment(sketch, "E591", {"start": v(60.93, 53.92) * mm, "end": v(59.69, 42.1) * mm});
            skEllipticalArc(sketch, "E592", {});
            skEllipticalArc(sketch, "E593", {});
            skFitSpline(sketch, "E594", {"points": [v(53.76, 53.92) * mm, v(54.22, 58.25) * mm, v(53.42, 61.87) * mm, v(48.54, 61.87) * mm]});
            skLineSegment(sketch, "E595", {"start": v(52.52, 42.1) * mm, "end": v(53.76, 53.92) * mm});
            skFitSpline(sketch, "E596", {"points": [v(48.54, 61.87) * mm, v(43.65, 61.87) * mm, v(42.09, 58.25) * mm, v(41.63, 53.92) * mm]});
            skFitSpline(sketch, "E597", {"points": [v(45.58, 34.61) * mm, v(50.63, 34.61) * mm, v(52.12, 38.32) * mm, v(52.52, 42.1) * mm]});
            skLineSegment(sketch, "E598", {"start": v(41.63, 53.92) * mm, "end": v(40.38, 42.1) * mm});
            skFitSpline(sketch, "E599", {"points": [v(40.38, 42.1) * mm, v(39.99, 38.32) * mm, v(40.7, 34.61) * mm, v(45.58, 34.61) * mm]});
            skEllipticalArc(sketch, "E600", {});
            skEllipticalArc(sketch, "E601", {});
            skEllipticalArc(sketch, "E602", {});
            skEllipticalArc(sketch, "E603", {});
            skEllipticalArc(sketch, "E604", {});
            skFitSpline(sketch, "E605", {"points": [v(8.04, 8.03) * mm, v(7.4, 7.87) * mm, v(6.83, 7.78) * mm, v(6.32, 7.78) * mm]});
            skEllipticalArc(sketch, "E606", {});
            skLineSegment(sketch, "E607", {"start": v(6.32, 7.78) * mm, "end": v(2.1, 7.78) * mm});
            skEllipticalArc(sketch, "E608", {});
            skLineSegment(sketch, "E609", {"start": v(2.1, 7.78) * mm, "end": v(3.06, 17) * mm});
            skLineSegment(sketch, "E610", {"start": v(3.06, 17) * mm, "end": v(7.29, 17) * mm});
            skEllipticalArc(sketch, "E611", {});
            skEllipticalArc(sketch, "E612", {});
            skEllipticalArc(sketch, "E613", {});
            skFitSpline(sketch, "E614", {"points": [v(7.14, 10.07) * mm, v(7.4, 10.2) * mm, v(7.63, 10.43) * mm, v(7.8, 10.76) * mm]});
            skLineSegment(sketch, "E615", {"start": v(6.4, 14.9) * mm, "end": v(5.69, 14.9) * mm});
            skEllipticalArc(sketch, "E616", {});
            skLineSegment(sketch, "E617", {"start": v(5.69, 14.9) * mm, "end": v(5.16, 9.87) * mm});
            skLineSegment(sketch, "E618", {"start": v(5.16, 9.87) * mm, "end": v(5.86, 9.87) * mm});
            skLineSegment(sketch, "E619", {"start": v(-38.33, 14.72) * mm, "end": v(-41.23, 14.72) * mm});
            skLineSegment(sketch, "E620", {"start": v(-38.1, 17) * mm, "end": v(-38.33, 14.72) * mm});
            skLineSegment(sketch, "E621", {"start": v(-41.23, 14.72) * mm, "end": v(-41.96, 7.78) * mm});
            skLineSegment(sketch, "E622", {"start": v(-46.74, 17) * mm, "end": v(-38.1, 17) * mm});
            skLineSegment(sketch, "E623", {"start": v(-41.96, 7.78) * mm, "end": v(-44.8, 7.78) * mm});
            skLineSegment(sketch, "E624", {"start": v(-46.98, 14.72) * mm, "end": v(-46.74, 17) * mm});
            skLineSegment(sketch, "E625", {"start": v(-44.8, 7.78) * mm, "end": v(-44.08, 14.72) * mm});
            skLineSegment(sketch, "E626", {"start": v(-44.08, 14.72) * mm, "end": v(-46.98, 14.72) * mm});
            skLineSegment(sketch, "E627", {"start": v(-17.05, 11.68) * mm, "end": v(-21.48, 11.68) * mm});
            skLineSegment(sketch, "E628", {"start": v(-16.86, 13.56) * mm, "end": v(-17.05, 11.68) * mm});
            skLineSegment(sketch, "E629", {"start": v(-21.48, 11.68) * mm, "end": v(-21.67, 9.87) * mm});
            skLineSegment(sketch, "E630", {"start": v(-21.29, 13.56) * mm, "end": v(-16.86, 13.56) * mm});
            skLineSegment(sketch, "E631", {"start": v(-21.67, 9.87) * mm, "end": v(-16.76, 9.87) * mm});
            skLineSegment(sketch, "E632", {"start": v(-21.13, 15.03) * mm, "end": v(-21.29, 13.56) * mm});
            skLineSegment(sketch, "E633", {"start": v(-16.76, 9.87) * mm, "end": v(-16.98, 7.78) * mm});
            skLineSegment(sketch, "E634", {"start": v(-16.36, 15.03) * mm, "end": v(-21.13, 15.03) * mm});
            skLineSegment(sketch, "E635", {"start": v(-16.98, 7.78) * mm, "end": v(-24.75, 7.78) * mm});
            skLineSegment(sketch, "E636", {"start": v(-16.15, 17) * mm, "end": v(-16.36, 15.03) * mm});
            skLineSegment(sketch, "E637", {"start": v(-24.75, 7.78) * mm, "end": v(-23.78, 17) * mm});
            skLineSegment(sketch, "E638", {"start": v(-23.78, 17) * mm, "end": v(-16.15, 17) * mm});
            skFitSpline(sketch, "E639", {"points": [v(-12.64, 34.61) * mm, v(-8.54, 34.61) * mm, v(-5.3, 38.47) * mm, v(-4.92, 42.1) * mm]});
            skLineSegment(sketch, "E640", {"start": v(-4.92, 42.1) * mm, "end": v(-4.5, 46.04) * mm});
            skLineSegment(sketch, "E641", {"start": v(-4.5, 46.04) * mm, "end": v(-12.98, 44.07) * mm});
            skFitSpline(sketch, "E642", {"points": [v(-12.98, 44.07) * mm, v(-16.2, 43.36) * mm, v(-17, 41.07) * mm, v(-17.15, 39.66) * mm]});
            skFitSpline(sketch, "E643", {"points": [v(-17.15, 39.66) * mm, v(-17.41, 37.13) * mm, v(-15.63, 34.61) * mm, v(-12.64, 34.61) * mm]});
            skLineSegment(sketch, "E644", {"start": v(73.12, -169.4) * mm, "end": v(73.12, -174.4) * mm});
            skLineSegment(sketch, "E645", {"start": v(23.12, -169.4) * mm, "end": v(73.12, -169.4) * mm});
            skLineSegment(sketch, "E646", {"start": v(73.12, -174.4) * mm, "end": v(23.12, -174.4) * mm});
            skLineSegment(sketch, "E647", {"start": v(23.12, -174.4) * mm, "end": v(23.12, -169.4) * mm});
            skLineSegment(sketch, "E648", {"start": v(-33.12, -174.4) * mm, "end": v(-83.12, -174.4) * mm});
            skLineSegment(sketch, "E649", {"start": v(-33.12, -169.4) * mm, "end": v(-33.12, -174.4) * mm});
            skLineSegment(sketch, "E650", {"start": v(-83.12, -174.4) * mm, "end": v(-83.12, -169.4) * mm});
            skLineSegment(sketch, "E651", {"start": v(-83.12, -169.4) * mm, "end": v(-33.12, -169.4) * mm});
            skLineSegment(sketch, "E652", {"start": v(57.88, 175.46) * mm, "end": v(-2.12, 175.46) * mm});
            skLineSegment(sketch, "E653", {"start": v(103.1, 225.9) * mm, "end": v(104.2, 225.9) * mm});
            skLineSegment(sketch, "E654", {"start": v(104.2, 225.9) * mm, "end": v(104.2, 223.9) * mm});
            skLineSegment(sketch, "E655", {"start": v(104.2, 223.9) * mm, "end": v(103.1, 223.9) * mm});
            skLineSegment(sketch, "E656", {"start": v(99.5, 223.9) * mm, "end": v(98.4, 223.9) * mm});
            skLineSegment(sketch, "E657", {"start": v(98.4, 223.9) * mm, "end": v(98.4, 225.9) * mm});
            skLineSegment(sketch, "E658", {"start": v(98.4, 225.9) * mm, "end": v(99.5, 225.9) * mm});
            skLineSegment(sketch, "E659", {"start": v(-3.2, 225.9) * mm, "end": v(-2.1, 225.9) * mm});
            skLineSegment(sketch, "E660", {"start": v(-2.1, 225.9) * mm, "end": v(-2.1, 223.9) * mm});
            skLineSegment(sketch, "E661", {"start": v(-2.1, 223.9) * mm, "end": v(-3.2, 223.9) * mm});
            skLineSegment(sketch, "E662", {"start": v(-6.8, 223.9) * mm, "end": v(-7.9, 223.9) * mm});
            skLineSegment(sketch, "E663", {"start": v(-7.9, 223.9) * mm, "end": v(-7.9, 225.9) * mm});
            skLineSegment(sketch, "E664", {"start": v(-7.9, 225.9) * mm, "end": v(-6.8, 225.9) * mm});
            skLineSegment(sketch, "E665", {"start": v(-109.5, 225.9) * mm, "end": v(-108.4, 225.9) * mm});
            skLineSegment(sketch, "E666", {"start": v(-108.4, 225.9) * mm, "end": v(-108.4, 223.9) * mm});
            skLineSegment(sketch, "E667", {"start": v(-108.4, 223.9) * mm, "end": v(-109.5, 223.9) * mm});
            skLineSegment(sketch, "E668", {"start": v(-113.1, 223.9) * mm, "end": v(-114.2, 223.9) * mm});
            skLineSegment(sketch, "E669", {"start": v(-114.2, 223.9) * mm, "end": v(-114.2, 225.9) * mm});
            skLineSegment(sketch, "E670", {"start": v(-114.2, 225.9) * mm, "end": v(-113.1, 225.9) * mm});
            skLineSegment(sketch, "E671", {"start": v(-148, -58.59) * mm, "end": v(-148, -59.69) * mm});
            skLineSegment(sketch, "E672", {"start": v(-148, -59.69) * mm, "end": v(-150, -59.69) * mm});
            skLineSegment(sketch, "E673", {"start": v(-150, -59.69) * mm, "end": v(-150, -58.59) * mm});
            skLineSegment(sketch, "E674", {"start": v(-150, 175.15) * mm, "end": v(-150, 176.25) * mm});
            skLineSegment(sketch, "E675", {"start": v(-150, 176.25) * mm, "end": v(-148, 176.25) * mm});
            skLineSegment(sketch, "E676", {"start": v(-148, 176.25) * mm, "end": v(-148, 175.15) * mm});
            skLineSegment(sketch, "E677", {"start": v(-148, 171.55) * mm, "end": v(-148, 170.45) * mm});
            skLineSegment(sketch, "E678", {"start": v(-148, 170.45) * mm, "end": v(-150, 170.45) * mm});
            skLineSegment(sketch, "E679", {"start": v(-150, 170.45) * mm, "end": v(-150, 171.55) * mm});
            skLineSegment(sketch, "E680", {"start": v(-150, 60.08) * mm, "end": v(-150, 61.18) * mm});
            skLineSegment(sketch, "E681", {"start": v(-150, 61.18) * mm, "end": v(-148, 61.18) * mm});
            skLineSegment(sketch, "E682", {"start": v(-148, 61.18) * mm, "end": v(-148, 60.08) * mm});
            skLineSegment(sketch, "E683", {"start": v(-148, 56.48) * mm, "end": v(-148, 55.38) * mm});
            skLineSegment(sketch, "E684", {"start": v(-148, 55.38) * mm, "end": v(-150, 55.38) * mm});
            skLineSegment(sketch, "E685", {"start": v(-150, 55.38) * mm, "end": v(-150, 56.48) * mm});
            skLineSegment(sketch, "E686", {"start": v(-150, -54.99) * mm, "end": v(-150, -53.89) * mm});
            skLineSegment(sketch, "E687", {"start": v(-150, -53.89) * mm, "end": v(-148, -53.89) * mm});
            skLineSegment(sketch, "E688", {"start": v(-148, -53.89) * mm, "end": v(-148, -54.99) * mm});
            skLineSegment(sketch, "E689", {"start": v(-150, -170.06) * mm, "end": v(-150, -168.96) * mm});
            skLineSegment(sketch, "E690", {"start": v(-150, -168.96) * mm, "end": v(-148, -168.96) * mm});
            skLineSegment(sketch, "E691", {"start": v(-148, -168.96) * mm, "end": v(-148, -170.06) * mm});
            skLineSegment(sketch, "E692", {"start": v(-148, -173.66) * mm, "end": v(-148, -174.76) * mm});
            skLineSegment(sketch, "E693", {"start": v(-148, -174.76) * mm, "end": v(-150, -174.76) * mm});
            skLineSegment(sketch, "E694", {"start": v(-150, -174.76) * mm, "end": v(-150, -173.66) * mm});
            skLineSegment(sketch, "E695", {"start": v(140, -173.66) * mm, "end": v(140, -174.76) * mm});
            skLineSegment(sketch, "E696", {"start": v(140, -174.76) * mm, "end": v(138, -174.76) * mm});
            skLineSegment(sketch, "E697", {"start": v(138, -174.76) * mm, "end": v(138, -173.66) * mm});
            skLineSegment(sketch, "E698", {"start": v(138, -170.06) * mm, "end": v(138, -168.96) * mm});
            skLineSegment(sketch, "E699", {"start": v(138, -168.96) * mm, "end": v(140, -168.96) * mm});
            skLineSegment(sketch, "E700", {"start": v(140, -168.96) * mm, "end": v(140, -170.06) * mm});
            skLineSegment(sketch, "E701", {"start": v(140, -58.59) * mm, "end": v(140, -59.69) * mm});
            skLineSegment(sketch, "E702", {"start": v(140, -59.69) * mm, "end": v(138, -59.69) * mm});
            skLineSegment(sketch, "E703", {"start": v(138, -59.69) * mm, "end": v(138, -58.59) * mm});
            skLineSegment(sketch, "E704", {"start": v(138, -54.99) * mm, "end": v(138, -53.89) * mm});
            skLineSegment(sketch, "E705", {"start": v(138, -53.89) * mm, "end": v(140, -53.89) * mm});
            skLineSegment(sketch, "E706", {"start": v(140, -53.89) * mm, "end": v(140, -54.99) * mm});
            skLineSegment(sketch, "E707", {"start": v(140, 56.48) * mm, "end": v(140, 55.38) * mm});
            skLineSegment(sketch, "E708", {"start": v(140, 55.38) * mm, "end": v(138, 55.38) * mm});
            skLineSegment(sketch, "E709", {"start": v(138, 55.38) * mm, "end": v(138, 56.48) * mm});
            skLineSegment(sketch, "E710", {"start": v(138, 60.08) * mm, "end": v(138, 61.18) * mm});
            skLineSegment(sketch, "E711", {"start": v(138, 61.18) * mm, "end": v(140, 61.18) * mm});
            skLineSegment(sketch, "E712", {"start": v(140, 61.18) * mm, "end": v(140, 60.08) * mm});
            skLineSegment(sketch, "E713", {"start": v(140, 171.55) * mm, "end": v(140, 170.45) * mm});
            skLineSegment(sketch, "E714", {"start": v(140, 170.45) * mm, "end": v(138, 170.45) * mm});
            skLineSegment(sketch, "E715", {"start": v(138, 170.45) * mm, "end": v(138, 171.55) * mm});
            skLineSegment(sketch, "E716", {"start": v(138, 175.15) * mm, "end": v(138, 176.25) * mm});
            skLineSegment(sketch, "E717", {"start": v(138, 176.25) * mm, "end": v(140, 176.25) * mm});
            skLineSegment(sketch, "E718", {"start": v(140, 176.25) * mm, "end": v(140, 175.15) * mm});
            skLineSegment(sketch, "E719", {"start": v(-150, -54.99) * mm, "end": v(-155, -54.99) * mm});
            skLineSegment(sketch, "E720", {"start": v(-155, -54.99) * mm, "end": v(-155, 56.48) * mm});
            skLineSegment(sketch, "E721", {"start": v(-155, 56.48) * mm, "end": v(-150, 56.48) * mm});
            skLineSegment(sketch, "E722", {"start": v(-148, 56.48) * mm, "end": v(-147, 56.48) * mm});
            skLineSegment(sketch, "E723", {"start": v(-147, 56.48) * mm, "end": v(-147, 60.08) * mm});
            skLineSegment(sketch, "E724", {"start": v(-147, 60.08) * mm, "end": v(-148, 60.08) * mm});
            skLineSegment(sketch, "E725", {"start": v(-150, 60.08) * mm, "end": v(-155, 60.08) * mm});
            skLineSegment(sketch, "E726", {"start": v(-155, 60.08) * mm, "end": v(-155, 171.55) * mm});
            skLineSegment(sketch, "E727", {"start": v(-155, 171.55) * mm, "end": v(-150, 171.55) * mm});
            skLineSegment(sketch, "E728", {"start": v(-148, 171.55) * mm, "end": v(-147, 171.55) * mm});
            skLineSegment(sketch, "E729", {"start": v(-147, 171.55) * mm, "end": v(-147, 175.15) * mm});
            skLineSegment(sketch, "E730", {"start": v(-147, 175.15) * mm, "end": v(-148, 175.15) * mm});
            skLineSegment(sketch, "E731", {"start": v(-150, 175.15) * mm, "end": v(-155, 175.15) * mm});
            skLineSegment(sketch, "E732", {"start": v(-155, 175.15) * mm, "end": v(-155, 230.9) * mm});
            skLineSegment(sketch, "E733", {"start": v(-155, 230.9) * mm, "end": v(-113.1, 230.9) * mm});
            skLineSegment(sketch, "E734", {"start": v(-113.1, 230.9) * mm, "end": v(-113.1, 225.9) * mm});
            skLineSegment(sketch, "E735", {"start": v(-113.1, 223.9) * mm, "end": v(-113.1, 222.9) * mm});
            skLineSegment(sketch, "E736", {"start": v(-113.1, 222.9) * mm, "end": v(-109.5, 222.9) * mm});
            skLineSegment(sketch, "E737", {"start": v(-109.5, 222.9) * mm, "end": v(-109.5, 223.9) * mm});
            skLineSegment(sketch, "E738", {"start": v(-109.5, 225.9) * mm, "end": v(-109.5, 230.9) * mm});
            skLineSegment(sketch, "E739", {"start": v(-109.5, 230.9) * mm, "end": v(-6.8, 230.9) * mm});
            skLineSegment(sketch, "E740", {"start": v(-6.8, 230.9) * mm, "end": v(-6.8, 225.9) * mm});
            skLineSegment(sketch, "E741", {"start": v(-6.8, 223.9) * mm, "end": v(-6.8, 222.9) * mm});
            skLineSegment(sketch, "E742", {"start": v(-6.8, 222.9) * mm, "end": v(-3.2, 222.9) * mm});
            skLineSegment(sketch, "E743", {"start": v(-3.2, 222.9) * mm, "end": v(-3.2, 223.9) * mm});
            skLineSegment(sketch, "E744", {"start": v(-3.2, 225.9) * mm, "end": v(-3.2, 230.9) * mm});
            skLineSegment(sketch, "E745", {"start": v(-3.2, 230.9) * mm, "end": v(99.5, 230.9) * mm});
            skLineSegment(sketch, "E746", {"start": v(99.5, 230.9) * mm, "end": v(99.5, 225.9) * mm});
            skLineSegment(sketch, "E747", {"start": v(99.5, 223.9) * mm, "end": v(99.5, 222.9) * mm});
            skLineSegment(sketch, "E748", {"start": v(99.5, 222.9) * mm, "end": v(103.1, 222.9) * mm});
            skLineSegment(sketch, "E749", {"start": v(103.1, 222.9) * mm, "end": v(103.1, 223.9) * mm});
            skLineSegment(sketch, "E750", {"start": v(103.1, 225.9) * mm, "end": v(103.1, 230.9) * mm});
            skLineSegment(sketch, "E751", {"start": v(103.1, 230.9) * mm, "end": v(145, 230.9) * mm});
            skLineSegment(sketch, "E752", {"start": v(145, 230.9) * mm, "end": v(145, 175.15) * mm});
            skLineSegment(sketch, "E753", {"start": v(145, 175.15) * mm, "end": v(140, 175.15) * mm});
            skLineSegment(sketch, "E754", {"start": v(138, 175.15) * mm, "end": v(137, 175.15) * mm});
            skLineSegment(sketch, "E755", {"start": v(137, 175.15) * mm, "end": v(137, 171.55) * mm});
            skLineSegment(sketch, "E756", {"start": v(137, 171.55) * mm, "end": v(138, 171.55) * mm});
            skLineSegment(sketch, "E757", {"start": v(140, 171.55) * mm, "end": v(145, 171.55) * mm});
            skLineSegment(sketch, "E758", {"start": v(145, 171.55) * mm, "end": v(145, 60.08) * mm});
            skLineSegment(sketch, "E759", {"start": v(145, 60.08) * mm, "end": v(140, 60.08) * mm});
            skLineSegment(sketch, "E760", {"start": v(138, 60.08) * mm, "end": v(137, 60.08) * mm});
            skLineSegment(sketch, "E761", {"start": v(137, 60.08) * mm, "end": v(137, 56.48) * mm});
            skLineSegment(sketch, "E762", {"start": v(137, 56.48) * mm, "end": v(138, 56.48) * mm});
            skLineSegment(sketch, "E763", {"start": v(140, 56.48) * mm, "end": v(145, 56.48) * mm});
            skLineSegment(sketch, "E764", {"start": v(145, 56.48) * mm, "end": v(145, -54.99) * mm});
            skLineSegment(sketch, "E765", {"start": v(145, -54.99) * mm, "end": v(140, -54.99) * mm});
            skLineSegment(sketch, "E766", {"start": v(138, -54.99) * mm, "end": v(137, -54.99) * mm});
            skLineSegment(sketch, "E767", {"start": v(137, -54.99) * mm, "end": v(137, -58.59) * mm});
            skLineSegment(sketch, "E768", {"start": v(137, -58.59) * mm, "end": v(138, -58.59) * mm});
            skLineSegment(sketch, "E769", {"start": v(140, -58.59) * mm, "end": v(145, -58.59) * mm});
            skLineSegment(sketch, "E770", {"start": v(145, -58.59) * mm, "end": v(145, -170.06) * mm});
            skLineSegment(sketch, "E771", {"start": v(145, -170.06) * mm, "end": v(140, -170.06) * mm});
            skLineSegment(sketch, "E772", {"start": v(138, -170.06) * mm, "end": v(137, -170.06) * mm});
            skLineSegment(sketch, "E773", {"start": v(137, -170.06) * mm, "end": v(137, -173.66) * mm});
            skLineSegment(sketch, "E774", {"start": v(137, -173.66) * mm, "end": v(138, -173.66) * mm});
            skLineSegment(sketch, "E775", {"start": v(140, -173.66) * mm, "end": v(145, -173.66) * mm});
            skLineSegment(sketch, "E776", {"start": v(145, -173.66) * mm, "end": v(145, -235.9) * mm});
            skLineSegment(sketch, "E777", {"start": v(-155, -235.9) * mm, "end": v(-155, -173.66) * mm});
            skLineSegment(sketch, "E778", {"start": v(-155, -173.66) * mm, "end": v(-150, -173.66) * mm});
            skLineSegment(sketch, "E779", {"start": v(-148, -173.66) * mm, "end": v(-147, -173.66) * mm});
            skLineSegment(sketch, "E780", {"start": v(-147, -173.66) * mm, "end": v(-147, -170.06) * mm});
            skLineSegment(sketch, "E781", {"start": v(-147, -170.06) * mm, "end": v(-148, -170.06) * mm});
            skLineSegment(sketch, "E782", {"start": v(-150, -170.06) * mm, "end": v(-155, -170.06) * mm});
            skLineSegment(sketch, "E783", {"start": v(-155, -170.06) * mm, "end": v(-155, -58.59) * mm});
            skLineSegment(sketch, "E784", {"start": v(-155, -58.59) * mm, "end": v(-150, -58.59) * mm});
            skLineSegment(sketch, "E785", {"start": v(-148, -58.59) * mm, "end": v(-147, -58.59) * mm});
            skLineSegment(sketch, "E786", {"start": v(-147, -58.59) * mm, "end": v(-147, -54.99) * mm});
            skLineSegment(sketch, "E787", {"start": v(-147, -54.99) * mm, "end": v(-148, -54.99) * mm});
            skLineSegment(sketch, "E788", {"start": v(-2.12, 145.46) * mm, "end": v(57.88, 145.46) * mm});
            skLineSegment(sketch, "E789", {"start": v(-102.12, 39.12) * mm, "end": v(-53.2, 39.12) * mm});
            skLineSegment(sketch, "E790", {"start": v(-40.35, 50.7) * mm, "end": v(-40, 54.04) * mm});
            skLineSegment(sketch, "E791", {"start": v(-40, 54.04) * mm, "end": v(-36.64, 85.84) * mm});
            skLineSegment(sketch, "E792", {"start": v(-46.68, 97) * mm, "end": v(-95.56, 97) * mm});
            skLineSegment(sketch, "E793", {"start": v(-97.72, 99.4) * mm, "end": v(-96.85, 107.62) * mm});
            skLineSegment(sketch, "E794", {"start": v(-96.85, 107.62) * mm, "end": v(-44.8, 107.62) * mm});
            skLineSegment(sketch, "E795", {"start": v(-25.63, 86.33) * mm, "end": v(-27.56, 68.06) * mm});
            skLineSegment(sketch, "E796", {"start": v(-27.56, 68.06) * mm, "end": v(-29.37, 50.87) * mm});
            skLineSegment(sketch, "E797", {"start": v(-54.23, 28.5) * mm, "end": v(-105.2, 28.5) * mm});
            skLineSegment(sketch, "E798", {"start": v(-105.2, 28.5) * mm, "end": v(-104.28, 37.18) * mm});
            skFitSpline(sketch, "E799", {"points": [v(74.21, 12.38) * mm, v(74.37, 13.88) * mm, v(74.91, 15.05) * mm, v(75.84, 15.9) * mm]});
            skEllipticalArc(sketch, "E800", {});
            skEllipticalArc(sketch, "E801", {});
            skEllipticalArc(sketch, "E802", {});
            skFitSpline(sketch, "E803", {"points": [v(82.94, 9.8) * mm, v(82.5, 9.12) * mm, v(81.93, 8.58) * mm, v(81.2, 8.2) * mm]});
            skFitSpline(sketch, "E804", {"points": [v(81.2, 8.2) * mm, v(80.48, 7.82) * mm, v(79.6, 7.63) * mm, v(78.58, 7.63) * mm]});
            skFitSpline(sketch, "E805", {"points": [v(78.58, 7.63) * mm, v(77.54, 7.63) * mm, v(76.7, 7.8) * mm, v(76.06, 8.12) * mm]});
            skFitSpline(sketch, "E806", {"points": [v(76.06, 8.12) * mm, v(75.4, 8.45) * mm, v(74.91, 8.98) * mm, v(74.57, 9.7) * mm]});
            skFitSpline(sketch, "E807", {"points": [v(74.57, 9.7) * mm, v(74.22, 10.4) * mm, v(74.1, 11.3) * mm, v(74.21, 12.38) * mm]});
            skLineSegment(sketch, "E808", {"start": v(52.45, 7.78) * mm, "end": v(56.88, 17) * mm});
            skLineSegment(sketch, "E809", {"start": v(56.88, 17) * mm, "end": v(59.99, 17) * mm});
            skLineSegment(sketch, "E810", {"start": v(59.99, 17) * mm, "end": v(62.48, 7.78) * mm});
            skLineSegment(sketch, "E811", {"start": v(62.48, 7.78) * mm, "end": v(59.5, 7.78) * mm});
            skLineSegment(sketch, "E812", {"start": v(59.5, 7.78) * mm, "end": v(59.2, 9.3) * mm});
            skLineSegment(sketch, "E813", {"start": v(59.2, 9.3) * mm, "end": v(55.97, 9.3) * mm});
            skLineSegment(sketch, "E814", {"start": v(55.97, 9.3) * mm, "end": v(55.36, 7.78) * mm});
            skLineSegment(sketch, "E815", {"start": v(55.36, 7.78) * mm, "end": v(52.45, 7.78) * mm});
            skLineSegment(sketch, "E816", {"start": v(33.89, 7.78) * mm, "end": v(31.03, 7.78) * mm});
            skLineSegment(sketch, "E817", {"start": v(31.03, 7.78) * mm, "end": v(32, 17) * mm});
            skLineSegment(sketch, "E818", {"start": v(32, 17) * mm, "end": v(36.74, 17) * mm});
            skEllipticalArc(sketch, "E819", {});
            skEllipticalArc(sketch, "E820", {});
            skFitSpline(sketch, "E821", {"points": [v(40.04, 14.43) * mm, v(39.98, 13.92) * mm, v(39.83, 13.48) * mm, v(39.57, 13.11) * mm]});
            skFitSpline(sketch, "E822", {"points": [v(39.57, 13.11) * mm, v(39.32, 12.74) * mm, v(38.98, 12.44) * mm, v(38.58, 12.21) * mm]});
            skEllipticalArc(sketch, "E823", {});
            skEllipticalArc(sketch, "E824", {});
            skFitSpline(sketch, "E825", {"points": [v(38.25, 11.5) * mm, v(38.34, 11.43) * mm, v(38.48, 11.27) * mm, v(38.65, 11.02) * mm]});
            skFitSpline(sketch, "E826", {"points": [v(38.65, 11.02) * mm, v(38.82, 10.78) * mm, v(38.94, 10.58) * mm, v(38.99, 10.45) * mm]});
            skLineSegment(sketch, "E827", {"start": v(38.99, 10.45) * mm, "end": v(40.09, 7.78) * mm});
            skLineSegment(sketch, "E828", {"start": v(40.09, 7.78) * mm, "end": v(36.87, 7.78) * mm});
            skLineSegment(sketch, "E829", {"start": v(36.87, 7.78) * mm, "end": v(35.65, 10.6) * mm});
            skEllipticalArc(sketch, "E830", {});
            skLineSegment(sketch, "E831", {"start": v(34.53, 11.52) * mm, "end": v(34.28, 11.52) * mm});
            skLineSegment(sketch, "E832", {"start": v(34.28, 11.52) * mm, "end": v(33.89, 7.78) * mm});
            skFitSpline(sketch, "E833", {"points": [v(77.24, 65.18) * mm, v(79.94, 67.62) * mm, v(81.3, 68.5) * mm, v(85.94, 68.5) * mm]});
            skFitSpline(sketch, "E834", {"points": [v(85.94, 68.5) * mm, v(87.28, 68.5) * mm, v(88.12, 67.54) * mm, v(88, 66.36) * mm]});
            skLineSegment(sketch, "E835", {"start": v(88, 66.36) * mm, "end": v(87.76, 64.08) * mm});
            skFitSpline(sketch, "E836", {"points": [v(87.76, 64.08) * mm, v(87.63, 62.9) * mm, v(86.58, 61.87) * mm, v(85.24, 61.87) * mm]});
            skFitSpline(sketch, "E837", {"points": [v(85.24, 61.87) * mm, v(78.15, 61.87) * mm, v(76.53, 58.4) * mm, v(76.2, 55.26) * mm]});
            skLineSegment(sketch, "E838", {"start": v(76.2, 55.26) * mm, "end": v(73.62, 30.83) * mm});
            skFitSpline(sketch, "E839", {"points": [v(73.62, 30.83) * mm, v(73.47, 29.5) * mm, v(72.43, 28.55) * mm, v(71.25, 28.55) * mm]});
            skLineSegment(sketch, "E840", {"start": v(71.25, 28.55) * mm, "end": v(68.33, 28.55) * mm});
            skLineSegment(sketch, "E841", {"start": v(66.45, 30.83) * mm, "end": v(70.12, 65.65) * mm});
            skFitSpline(sketch, "E842", {"points": [v(70.12, 65.65) * mm, v(70.26, 67) * mm, v(71.3, 67.94) * mm, v(72.49, 67.94) * mm]});
            skLineSegment(sketch, "E843", {"start": v(72.49, 67.94) * mm, "end": v(75.4, 67.94) * mm});
            skLineSegment(sketch, "E844", {"start": v(77.3, 65.65) * mm, "end": v(77.24, 65.18) * mm});
            skLineSegment(sketch, "E845", {"start": v(24.22, 28.55) * mm, "end": v(22.96, 28.55) * mm});
            skFitSpline(sketch, "E846", {"points": [v(22.96, 28.55) * mm, v(14.77, 28.55) * mm, v(10.7, 31.86) * mm, v(11.69, 41.15) * mm]});
            skLineSegment(sketch, "E847", {"start": v(11.69, 41.15) * mm, "end": v(13.74, 60.61) * mm});
            skLineSegment(sketch, "E848", {"start": v(13.74, 60.61) * mm, "end": v(12, 60.61) * mm});
            skLineSegment(sketch, "E849", {"start": v(10.03, 62.82) * mm, "end": v(10.26, 64.95) * mm});
            skLineSegment(sketch, "E850", {"start": v(12.7, 67.23) * mm, "end": v(14.44, 67.23) * mm});
            skLineSegment(sketch, "E851", {"start": v(14.44, 67.23) * mm, "end": v(15.78, 79.91) * mm});
            skLineSegment(sketch, "E852", {"start": v(18.22, 82.12) * mm, "end": v(20.9, 82.12) * mm});
            skLineSegment(sketch, "E853", {"start": v(22.95, 79.91) * mm, "end": v(21.6, 67.23) * mm});
            skLineSegment(sketch, "E854", {"start": v(21.6, 67.23) * mm, "end": v(27.68, 67.23) * mm});
            skLineSegment(sketch, "E855", {"start": v(29.73, 65.02) * mm, "end": v(29.5, 62.9) * mm});
            skLineSegment(sketch, "E856", {"start": v(26.98, 60.61) * mm, "end": v(20.91, 60.61) * mm});
            skLineSegment(sketch, "E857", {"start": v(20.91, 60.61) * mm, "end": v(18.86, 41.15) * mm});
            skFitSpline(sketch, "E858", {"points": [v(18.86, 41.15) * mm, v(18.38, 36.58) * mm, v(20.43, 35.16) * mm, v(23.66, 35.16) * mm]});
            skLineSegment(sketch, "E859", {"start": v(23.66, 35.16) * mm, "end": v(24.92, 35.16) * mm});
            skLineSegment(sketch, "E860", {"start": v(26.9, 33.04) * mm, "end": v(26.67, 30.83) * mm});
            skEllipticalArc(sketch, "E861", {});
            skEllipticalArc(sketch, "E862", {});
            skFitSpline(sketch, "E863", {"points": [v(-1.31, 16.48) * mm, v(-0.82, 16.03) * mm, v(-0.62, 15.46) * mm, v(-0.69, 14.79) * mm]});
            skEllipticalArc(sketch, "E864", {});
            skFitSpline(sketch, "E865", {"points": [v(-1.13, 13.7) * mm, v(-1.38, 13.38) * mm, v(-1.74, 13.1) * mm, v(-2.2, 12.86) * mm]});
            skFitSpline(sketch, "E866", {"points": [v(-2.2, 12.86) * mm, v(-1.86, 12.77) * mm, v(-1.6, 12.67) * mm, v(-1.42, 12.55) * mm]});
            skEllipticalArc(sketch, "E867", {});
            skFitSpline(sketch, "E868", {"points": [v(-0.78, 11.8) * mm, v(-0.65, 11.5) * mm, v(-0.6, 11.13) * mm, v(-0.65, 10.7) * mm]});
            skFitSpline(sketch, "E869", {"points": [v(-0.65, 10.7) * mm, v(-0.7, 10.17) * mm, v(-0.9, 9.65) * mm, v(-1.23, 9.16) * mm]});
            skEllipticalArc(sketch, "E870", {});
            skFitSpline(sketch, "E871", {"points": [v(-4.68, 7.62) * mm, v(-5.52, 7.62) * mm, v(-6.17, 7.72) * mm, v(-6.63, 7.92) * mm]});
            skFitSpline(sketch, "E872", {"points": [v(-6.63, 7.92) * mm, v(-7.1, 8.12) * mm, v(-7.46, 8.4) * mm, v(-7.74, 8.78) * mm]});
            skFitSpline(sketch, "E873", {"points": [v(-7.74, 8.78) * mm, v(-8, 9.16) * mm, v(-8.2, 9.64) * mm, v(-8.3, 10.21) * mm]});
            skLineSegment(sketch, "E874", {"start": v(-8.3, 10.21) * mm, "end": v(-5.71, 10.55) * mm});
            skFitSpline(sketch, "E875", {"points": [v(-5.71, 10.55) * mm, v(-5.67, 10.04) * mm, v(-5.55, 9.68) * mm, v(-5.36, 9.48) * mm]});
            skEllipticalArc(sketch, "E876", {});
            skFitSpline(sketch, "E877", {"points": [v(-3.24, 10.56) * mm, v(-3.2, 11) * mm, v(-3.27, 11.32) * mm, v(-3.46, 11.56) * mm]});
            skFitSpline(sketch, "E878", {"points": [v(-4.32, 11.9) * mm, v(-4.52, 11.9) * mm, v(-4.8, 11.86) * mm, v(-5.16, 11.76) * mm]});
            skLineSegment(sketch, "E879", {"start": v(-5.16, 11.76) * mm, "end": v(-4.84, 13.59) * mm});
            skEllipticalArc(sketch, "E880", {});
            skFitSpline(sketch, "E881", {"points": [v(-3.64, 13.88) * mm, v(-3.4, 14.09) * mm, v(-3.25, 14.34) * mm, v(-3.22, 14.64) * mm]});
            skFitSpline(sketch, "E882", {"points": [v(-3.22, 14.64) * mm, v(-3.2, 14.92) * mm, v(-3.25, 15.14) * mm, v(-3.4, 15.3) * mm]});
            skFitSpline(sketch, "E883", {"points": [v(-4.83, 15.29) * mm, v(-5.04, 15.1) * mm, v(-5.2, 14.78) * mm, v(-5.31, 14.33) * mm]});
            skLineSegment(sketch, "E884", {"start": v(-5.31, 14.33) * mm, "end": v(-7.69, 14.76) * mm});
            skLineSegment(sketch, "E885", {"start": v(-26.95, 17) * mm, "end": v(-27.92, 7.78) * mm});
            skLineSegment(sketch, "E886", {"start": v(-27.92, 7.78) * mm, "end": v(-30.77, 7.78) * mm});
            skLineSegment(sketch, "E887", {"start": v(-30.77, 7.78) * mm, "end": v(-30.38, 11.5) * mm});
            skLineSegment(sketch, "E888", {"start": v(-30.38, 11.5) * mm, "end": v(-33.5, 11.5) * mm});
            skLineSegment(sketch, "E889", {"start": v(-33.5, 11.5) * mm, "end": v(-33.88, 7.78) * mm});
            skLineSegment(sketch, "E890", {"start": v(-33.88, 7.78) * mm, "end": v(-36.73, 7.78) * mm});
            skLineSegment(sketch, "E891", {"start": v(-36.73, 7.78) * mm, "end": v(-35.76, 17) * mm});
            skLineSegment(sketch, "E892", {"start": v(-35.76, 17) * mm, "end": v(-32.92, 17) * mm});
            skLineSegment(sketch, "E893", {"start": v(-32.92, 17) * mm, "end": v(-33.25, 13.77) * mm});
            skLineSegment(sketch, "E894", {"start": v(-33.25, 13.77) * mm, "end": v(-30.14, 13.77) * mm});
            skLineSegment(sketch, "E895", {"start": v(-30.14, 13.77) * mm, "end": v(-29.8, 17) * mm});
            skLineSegment(sketch, "E896", {"start": v(-29.8, 17) * mm, "end": v(-26.95, 17) * mm});
            skLineSegment(sketch, "E897", {"start": v(-16.58, 55.5) * mm, "end": v(-19.5, 55.5) * mm});
            skFitSpline(sketch, "E898", {"points": [v(-19.5, 55.5) * mm, v(-20.68, 55.5) * mm, v(-21.53, 56.36) * mm, v(-21.38, 57.78) * mm]});
            skFitSpline(sketch, "E899", {"points": [v(-21.38, 57.78) * mm, v(-20.7, 64.31) * mm, v(-14.97, 68.5) * mm, v(-7.8, 68.5) * mm]});
            skFitSpline(sketch, "E900", {"points": [v(-7.8, 68.5) * mm, v(-1.03, 68.5) * mm, v(4.57, 64) * mm, v(3.57, 54.55) * mm]});
            skLineSegment(sketch, "E901", {"start": v(3.57, 54.55) * mm, "end": v(1.07, 30.83) * mm});
            skFitSpline(sketch, "E902", {"points": [v(1.07, 30.83) * mm, v(0.92, 29.5) * mm, v(-0.12, 28.55) * mm, v(-1.3, 28.55) * mm]});
            skLineSegment(sketch, "E903", {"start": v(-1.3, 28.55) * mm, "end": v(-4.06, 28.55) * mm});
            skLineSegment(sketch, "E904", {"start": v(-5.95, 30.83) * mm, "end": v(-5.87, 31.54) * mm});
            skFitSpline(sketch, "E905", {"points": [v(-5.87, 31.54) * mm, v(-7.51, 29.41) * mm, v(-11.05, 28) * mm, v(-14.12, 28) * mm]});
            skFitSpline(sketch, "E906", {"points": [v(-14.12, 28) * mm, v(-20.35, 28) * mm, v(-25.02, 32.96) * mm, v(-24.35, 39.34) * mm]});
            skFitSpline(sketch, "E907", {"points": [v(-24.35, 39.34) * mm, v(-23.7, 45.49) * mm, v(-20.98, 48.87) * mm, v(-13.38, 50.69) * mm]});
            skLineSegment(sketch, "E908", {"start": v(-13.38, 50.69) * mm, "end": v(-3.77, 52.97) * mm});
            skLineSegment(sketch, "E909", {"start": v(-3.77, 52.97) * mm, "end": v(-3.42, 56.28) * mm});
            skFitSpline(sketch, "E910", {"points": [v(-3.42, 56.28) * mm, v(-3.07, 59.59) * mm, v(-5.27, 61.87) * mm, v(-8.5, 61.87) * mm]});
            skFitSpline(sketch, "E911", {"points": [v(-8.5, 61.87) * mm, v(-12.12, 61.87) * mm, v(-13.97, 60.06) * mm, v(-14.21, 57.78) * mm]});
            skFitSpline(sketch, "E912", {"points": [v(-14.21, 57.78) * mm, v(-14.36, 56.36) * mm, v(-15.4, 55.5) * mm, v(-16.58, 55.5) * mm]});
            skCircle(sketch, "E913", {"center": v(-593.39, 77.69) * mm, "radius": 1.5 * mm});
            skCircle(sketch, "E914", {"center": v(-506.57, 91.08) * mm, "radius": 1.6 * mm});
            skCircle(sketch, "E915", {"center": v(-660.57, 91.08) * mm, "radius": 1.6 * mm});
            skArc(sketch, "E916", {"start": v(-552.38, 120.2) * mm, "mid": v(-554.5, 118.35) * mm, "end": v(-555.29, 115.66) * mm});
            skArc(sketch, "E917", {"start": v(-611.49, 115.53) * mm, "mid": v(-612.27, 118.23) * mm, "end": v(-614.39, 120.07) * mm});
            skCircle(sketch, "E918", {"center": v(-697.52, 167.08) * mm, "radius": 2.5 * mm});
            skCircle(sketch, "E919", {"center": v(-669.52, 167.08) * mm, "radius": 2.5 * mm});
            skCircle(sketch, "E920", {"center": v(-669.52, 146.08) * mm, "radius": 2.5 * mm});
            skCircle(sketch, "E921", {"center": v(-697.52, 146.08) * mm, "radius": 2.5 * mm});
            skCircle(sketch, "E922", {"center": v(-697.52, 105.08) * mm, "radius": 2.5 * mm});
            skCircle(sketch, "E923", {"center": v(-669.52, 105.08) * mm, "radius": 2.5 * mm});
            skCircle(sketch, "E924", {"center": v(-669.52, 84.08) * mm, "radius": 2.5 * mm});
            skCircle(sketch, "E925", {"center": v(-697.52, 84.08) * mm, "radius": 2.5 * mm});
            skCircle(sketch, "E926", {"center": v(-506.62, 137.28) * mm, "radius": 1.6 * mm});
            skCircle(sketch, "E927", {"center": v(-506.62, 162.88) * mm, "radius": 1.6 * mm});
            skCircle(sketch, "E928", {"center": v(-497.52, 167.08) * mm, "radius": 2.5 * mm});
            skCircle(sketch, "E929", {"center": v(-469.52, 167.08) * mm, "radius": 2.5 * mm});
            skCircle(sketch, "E930", {"center": v(-469.52, 146.08) * mm, "radius": 2.5 * mm});
            skCircle(sketch, "E931", {"center": v(-497.52, 146.08) * mm, "radius": 2.5 * mm});
            skCircle(sketch, "E932", {"center": v(-469.52, 105.08) * mm, "radius": 2.5 * mm});
            skCircle(sketch, "E933", {"center": v(-469.52, 84.08) * mm, "radius": 2.5 * mm});
            skCircle(sketch, "E934", {"center": v(-497.52, 84.08) * mm, "radius": 2.5 * mm});
            skCircle(sketch, "E935", {"center": v(-497.52, 105.08) * mm, "radius": 2.5 * mm});
            skCircle(sketch, "E936", {"center": v(-544.22, 108.58) * mm, "radius": 1.6 * mm});
            skCircle(sketch, "E937", {"center": v(-622.82, 108.58) * mm, "radius": 1.6 * mm});
            skCircle(sketch, "E938", {"center": v(-660.42, 162.88) * mm, "radius": 1.6 * mm});
            skCircle(sketch, "E939", {"center": v(-660.42, 137.28) * mm, "radius": 1.6 * mm});
            skCircle(sketch, "E940", {"center": v(-643.52, 123.58) * mm, "radius": 4 * mm});
            skCircle(sketch, "E941", {"center": v(-593.39, 86.99) * mm, "radius": 1.5 * mm});
            skCircle(sketch, "E942", {"center": v(-573.36, 77.69) * mm, "radius": 1.5 * mm});
            skCircle(sketch, "E943", {"center": v(-573.36, 86.99) * mm, "radius": 1.5 * mm});
            skLineSegment(sketch, "E944", {"start": v(-648.4, 113.72) * mm, "end": v(-648.4, 118.72) * mm});
            skLineSegment(sketch, "E945", {"start": v(-648.4, 118.72) * mm, "end": v(-646.4, 118.72) * mm});
            skLineSegment(sketch, "E946", {"start": v(-646.4, 118.72) * mm, "end": v(-646.4, 113.72) * mm});
            skLineSegment(sketch, "E947", {"start": v(-646.4, 113.72) * mm, "end": v(-648.4, 113.72) * mm});
            skLineSegment(sketch, "E948", {"start": v(-640.4, 113.72) * mm, "end": v(-640.4, 118.72) * mm});
            skLineSegment(sketch, "E949", {"start": v(-640.4, 118.72) * mm, "end": v(-638.4, 118.72) * mm});
            skLineSegment(sketch, "E950", {"start": v(-638.4, 118.72) * mm, "end": v(-638.4, 113.72) * mm});
            skLineSegment(sketch, "E951", {"start": v(-638.4, 113.72) * mm, "end": v(-640.4, 113.72) * mm});
            skLineSegment(sketch, "E952", {"start": v(-658.07, 133.48) * mm, "end": v(-658.07, 105.08) * mm});
            skLineSegment(sketch, "E953", {"start": v(-504.07, 133.48) * mm, "end": v(-504.07, 105.08) * mm});
            skLineSegment(sketch, "E954", {"start": v(-703.52, 72.08) * mm, "end": v(-463.52, 72.08) * mm});
            skLineSegment(sketch, "E955", {"start": v(-703.52, 174.08) * mm, "end": v(-657.92, 174.08) * mm});
            skLineSegment(sketch, "E956", {"start": v(-703.52, 72.08) * mm, "end": v(-703.52, 174.08) * mm});
            skLineSegment(sketch, "E957", {"start": v(-463.52, 174.08) * mm, "end": v(-463.52, 72.08) * mm});
            skLineSegment(sketch, "E958", {"start": v(-509.12, 174.08) * mm, "end": v(-463.52, 174.08) * mm});
            skArc(sketch, "E959", {"start": v(-509.12, 174.08) * mm, "mid": v(-512.66, 172.61) * mm, "end": v(-514.12, 169.08) * mm});
            skLineSegment(sketch, "E960", {"start": v(-514.12, 141.07) * mm, "end": v(-514.12, 169.08) * mm});
            skArc(sketch, "E961", {"start": v(-517.03, 136.54) * mm, "mid": v(-514.91, 138.38) * mm, "end": v(-514.12, 141.07) * mm});
            skLineSegment(sketch, "E962", {"start": v(-552.38, 120.2) * mm, "end": v(-517.03, 136.54) * mm});
            skLineSegment(sketch, "E963", {"start": v(-555.29, 115.66) * mm, "end": v(-555.29, 95.08) * mm});
            skLineSegment(sketch, "E964", {"start": v(-555.29, 95.08) * mm, "end": v(-611.49, 95.08) * mm});
            skLineSegment(sketch, "E965", {"start": v(-611.49, 95.08) * mm, "end": v(-611.49, 115.53) * mm});
            skLineSegment(sketch, "E966", {"start": v(-650.02, 136.54) * mm, "end": v(-614.39, 120.07) * mm});
            skArc(sketch, "E967", {"start": v(-652.92, 141.07) * mm, "mid": v(-652.13, 138.38) * mm, "end": v(-650.02, 136.54) * mm});
            skLineSegment(sketch, "E968", {"start": v(-652.92, 169.08) * mm, "end": v(-652.92, 141.07) * mm});
            skArc(sketch, "E969", {"start": v(-652.92, 169.08) * mm, "mid": v(-654.39, 172.61) * mm, "end": v(-657.92, 174.08) * mm});
            skLineSegment(sketch, "E970", {"start": v(-663.07, 105.08) * mm, "end": v(-658.07, 105.08) * mm});
            skLineSegment(sketch, "E971", {"start": v(-663.07, 133.48) * mm, "end": v(-663.07, 105.08) * mm});
            skLineSegment(sketch, "E972", {"start": v(-658.07, 133.48) * mm, "end": v(-663.07, 133.48) * mm});
            skLineSegment(sketch, "E973", {"start": v(-509.07, 105.08) * mm, "end": v(-504.07, 105.08) * mm});
            skLineSegment(sketch, "E974", {"start": v(-509.07, 133.48) * mm, "end": v(-509.07, 105.08) * mm});
            skLineSegment(sketch, "E975", {"start": v(-504.07, 133.48) * mm, "end": v(-509.07, 133.48) * mm});
            skLineSegment(sketch, "E976", {"start": v(-161.88, 142.3) * mm, "end": v(-161.88, 131.8) * mm});
            skArc(sketch, "E977", {"start": v(-176.88, 116.8) * mm, "mid": v(-166.28, 121.19) * mm, "end": v(-161.88, 131.8) * mm});
            skCircle(sketch, "E978", {"center": v(-217.2, 161.14) * mm, "radius": 5 * mm});
            skLineSegment(sketch, "E979", {"start": v(-370.98, 144.8) * mm, "end": v(-370.98, 149.8) * mm});
            skLineSegment(sketch, "E980", {"start": v(-330.98, 149.8) * mm, "end": v(-330.98, 144.8) * mm});
            skLineSegment(sketch, "E981", {"start": v(-330.98, 144.8) * mm, "end": v(-370.98, 144.8) * mm});
            skLineSegment(sketch, "E982", {"start": v(-381.48, 149.8) * mm, "end": v(-370.98, 149.8) * mm});
            skLineSegment(sketch, "E983", {"start": v(-330.98, 149.8) * mm, "end": v(-320.48, 149.8) * mm});
            skLineSegment(sketch, "E984", {"start": v(-251.98, 149.8) * mm, "end": v(-251.98, 144.8) * mm});
            skLineSegment(sketch, "E985", {"start": v(-251.98, 144.8) * mm, "end": v(-301.98, 144.8) * mm});
            skLineSegment(sketch, "E986", {"start": v(-301.98, 144.8) * mm, "end": v(-301.98, 149.8) * mm});
            skLineSegment(sketch, "E987", {"start": v(-317.08, 149.8) * mm, "end": v(-301.98, 149.8) * mm});
            skLineSegment(sketch, "E988", {"start": v(-251.98, 149.8) * mm, "end": v(-236.88, 149.8) * mm});
            skLineSegment(sketch, "E989", {"start": v(-181.88, 128) * mm, "end": v(-181.88, 129.1) * mm});
            skLineSegment(sketch, "E990", {"start": v(-179.88, 128) * mm, "end": v(-181.88, 128) * mm});
            skLineSegment(sketch, "E991", {"start": v(-179.88, 129.1) * mm, "end": v(-179.88, 128) * mm});
            skLineSegment(sketch, "E992", {"start": v(-179.88, 133.6) * mm, "end": v(-179.88, 132.5) * mm});
            skLineSegment(sketch, "E993", {"start": v(-181.88, 133.6) * mm, "end": v(-179.88, 133.6) * mm});
            skLineSegment(sketch, "E994", {"start": v(-181.88, 132.5) * mm, "end": v(-181.88, 133.6) * mm});
            skLineSegment(sketch, "E995", {"start": v(-196.88, 204.3) * mm, "end": v(-196.88, 205.4) * mm});
            skLineSegment(sketch, "E996", {"start": v(-196.88, 205.4) * mm, "end": v(-198.88, 205.4) * mm});
            skLineSegment(sketch, "E997", {"start": v(-198.88, 205.4) * mm, "end": v(-198.88, 204.3) * mm});
            skLineSegment(sketch, "E998", {"start": v(-198.88, 200.9) * mm, "end": v(-198.88, 199.8) * mm});
            skLineSegment(sketch, "E999", {"start": v(-198.88, 199.8) * mm, "end": v(-196.88, 199.8) * mm});
            skLineSegment(sketch, "E1000", {"start": v(-196.88, 199.8) * mm, "end": v(-196.88, 200.9) * mm});
            skLineSegment(sketch, "E1001", {"start": v(-196.88, 178.7) * mm, "end": v(-196.88, 179.8) * mm});
            skLineSegment(sketch, "E1002", {"start": v(-196.88, 179.8) * mm, "end": v(-198.88, 179.8) * mm});
            skLineSegment(sketch, "E1003", {"start": v(-198.88, 179.8) * mm, "end": v(-198.88, 178.7) * mm});
            skLineSegment(sketch, "E1004", {"start": v(-198.88, 175.3) * mm, "end": v(-198.88, 174.2) * mm});
            skLineSegment(sketch, "E1005", {"start": v(-198.88, 174.2) * mm, "end": v(-196.88, 174.2) * mm});
            skLineSegment(sketch, "E1006", {"start": v(-196.88, 174.2) * mm, "end": v(-196.88, 175.3) * mm});
            skLineSegment(sketch, "E1007", {"start": v(-233.48, 154.8) * mm, "end": v(-232.38, 154.8) * mm});
            skLineSegment(sketch, "E1008", {"start": v(-232.38, 154.8) * mm, "end": v(-232.38, 156.8) * mm});
            skLineSegment(sketch, "E1009", {"start": v(-232.38, 156.8) * mm, "end": v(-233.48, 156.8) * mm});
            skLineSegment(sketch, "E1010", {"start": v(-236.88, 156.8) * mm, "end": v(-237.98, 156.8) * mm});
            skLineSegment(sketch, "E1011", {"start": v(-237.98, 156.8) * mm, "end": v(-237.98, 154.8) * mm});
            skLineSegment(sketch, "E1012", {"start": v(-237.98, 154.8) * mm, "end": v(-236.88, 154.8) * mm});
            skLineSegment(sketch, "E1013", {"start": v(-317.08, 154.8) * mm, "end": v(-315.98, 154.8) * mm});
            skLineSegment(sketch, "E1014", {"start": v(-315.98, 154.8) * mm, "end": v(-315.98, 156.8) * mm});
            skLineSegment(sketch, "E1015", {"start": v(-315.98, 156.8) * mm, "end": v(-317.08, 156.8) * mm});
            skLineSegment(sketch, "E1016", {"start": v(-320.48, 156.8) * mm, "end": v(-321.58, 156.8) * mm});
            skLineSegment(sketch, "E1017", {"start": v(-321.58, 156.8) * mm, "end": v(-321.58, 154.8) * mm});
            skLineSegment(sketch, "E1018", {"start": v(-321.58, 154.8) * mm, "end": v(-320.48, 154.8) * mm});
            skLineSegment(sketch, "E1019", {"start": v(-381.48, 154.8) * mm, "end": v(-380.38, 154.8) * mm});
            skLineSegment(sketch, "E1020", {"start": v(-380.38, 154.8) * mm, "end": v(-380.38, 156.8) * mm});
            skLineSegment(sketch, "E1021", {"start": v(-380.38, 156.8) * mm, "end": v(-381.48, 156.8) * mm});
            skLineSegment(sketch, "E1022", {"start": v(-384.88, 156.8) * mm, "end": v(-385.98, 156.8) * mm});
            skLineSegment(sketch, "E1023", {"start": v(-385.98, 156.8) * mm, "end": v(-385.98, 154.8) * mm});
            skLineSegment(sketch, "E1024", {"start": v(-385.98, 154.8) * mm, "end": v(-384.88, 154.8) * mm});
            skLineSegment(sketch, "E1025", {"start": v(-178.88, 132.5) * mm, "end": v(-178.88, 129.1) * mm});
            skLineSegment(sketch, "E1026", {"start": v(-178.88, 129.1) * mm, "end": v(-179.88, 129.1) * mm});
            skLineSegment(sketch, "E1027", {"start": v(-181.88, 129.1) * mm, "end": v(-186.88, 129.1) * mm});
            skLineSegment(sketch, "E1028", {"start": v(-186.88, 132.5) * mm, "end": v(-181.88, 132.5) * mm});
            skLineSegment(sketch, "E1029", {"start": v(-179.88, 132.5) * mm, "end": v(-178.88, 132.5) * mm});
            skLineSegment(sketch, "E1030", {"start": v(-320.48, 149.8) * mm, "end": v(-320.48, 154.8) * mm});
            skLineSegment(sketch, "E1031", {"start": v(-320.48, 156.8) * mm, "end": v(-320.48, 157.8) * mm});
            skLineSegment(sketch, "E1032", {"start": v(-320.48, 157.8) * mm, "end": v(-317.08, 157.8) * mm});
            skLineSegment(sketch, "E1033", {"start": v(-317.08, 157.8) * mm, "end": v(-317.08, 156.8) * mm});
            skLineSegment(sketch, "E1034", {"start": v(-317.08, 154.8) * mm, "end": v(-317.08, 149.8) * mm});
            skLineSegment(sketch, "E1035", {"start": v(-236.88, 149.8) * mm, "end": v(-236.88, 154.8) * mm});
            skLineSegment(sketch, "E1036", {"start": v(-236.88, 156.8) * mm, "end": v(-236.88, 157.8) * mm});
            skLineSegment(sketch, "E1037", {"start": v(-236.88, 157.8) * mm, "end": v(-233.48, 157.8) * mm});
            skLineSegment(sketch, "E1038", {"start": v(-233.48, 157.8) * mm, "end": v(-233.48, 156.8) * mm});
            skLineSegment(sketch, "E1039", {"start": v(-233.48, 154.8) * mm, "end": v(-233.48, 149.8) * mm});
            skLineSegment(sketch, "E1040", {"start": v(-233.48, 149.8) * mm, "end": v(-228.58, 149.8) * mm});
            skLineSegment(sketch, "E1041", {"start": v(-228.58, 144.8) * mm, "end": v(-228.58, 149.8) * mm});
            skLineSegment(sketch, "E1042", {"start": v(-186.88, 144.8) * mm, "end": v(-228.58, 144.8) * mm});
            skLineSegment(sketch, "E1043", {"start": v(-186.88, 132.5) * mm, "end": v(-186.88, 144.8) * mm});
            skLineSegment(sketch, "E1044", {"start": v(-186.88, 116.8) * mm, "end": v(-186.88, 129.1) * mm});
            skLineSegment(sketch, "E1045", {"start": v(-176.88, 116.8) * mm, "end": v(-186.88, 116.8) * mm});
            skArc(sketch, "E1046", {"start": v(-161.88, 142.3) * mm, "mid": v(-166.77, 157.94) * mm, "end": v(-179.68, 168.03) * mm});
            skLineSegment(sketch, "E1047", {"start": v(-179.68, 168.03) * mm, "end": v(-186.88, 170.8) * mm});
            skLineSegment(sketch, "E1048", {"start": v(-186.88, 170.8) * mm, "end": v(-186.88, 173.2) * mm});
            skLineSegment(sketch, "E1049", {"start": v(-186.88, 173.2) * mm, "end": v(-191.88, 173.2) * mm});
            skLineSegment(sketch, "E1050", {"start": v(-191.88, 173.2) * mm, "end": v(-191.88, 175.3) * mm});
            skLineSegment(sketch, "E1051", {"start": v(-191.88, 175.3) * mm, "end": v(-196.88, 175.3) * mm});
            skLineSegment(sketch, "E1052", {"start": v(-198.88, 175.3) * mm, "end": v(-199.88, 175.3) * mm});
            skLineSegment(sketch, "E1053", {"start": v(-199.88, 175.3) * mm, "end": v(-199.88, 178.7) * mm});
            skLineSegment(sketch, "E1054", {"start": v(-199.88, 178.7) * mm, "end": v(-198.88, 178.7) * mm});
            skLineSegment(sketch, "E1055", {"start": v(-196.88, 178.7) * mm, "end": v(-191.88, 178.7) * mm});
            skLineSegment(sketch, "E1056", {"start": v(-191.88, 178.7) * mm, "end": v(-191.88, 200.9) * mm});
            skLineSegment(sketch, "E1057", {"start": v(-191.88, 200.9) * mm, "end": v(-196.88, 200.9) * mm});
            skLineSegment(sketch, "E1058", {"start": v(-198.88, 200.9) * mm, "end": v(-199.88, 200.9) * mm});
            skLineSegment(sketch, "E1059", {"start": v(-199.88, 200.9) * mm, "end": v(-199.88, 204.3) * mm});
            skLineSegment(sketch, "E1060", {"start": v(-199.88, 204.3) * mm, "end": v(-198.88, 204.3) * mm});
            skLineSegment(sketch, "E1061", {"start": v(-196.88, 204.3) * mm, "end": v(-191.88, 204.3) * mm});
            skLineSegment(sketch, "E1062", {"start": v(-191.88, 204.3) * mm, "end": v(-191.88, 213.8) * mm});
            skLineSegment(sketch, "E1063", {"start": v(-191.88, 213.8) * mm, "end": v(-362.73, 180.28) * mm});
            skArc(sketch, "E1064", {"start": v(-362.73, 180.28) * mm, "mid": v(-376.79, 175.2) * mm, "end": v(-388.68, 166.15) * mm});
            skArc(sketch, "E1065", {"start": v(-388.68, 166.15) * mm, "mid": v(-392.27, 161.3) * mm, "end": v(-394.5, 155.71) * mm});
            skArc(sketch, "E1066", {"start": v(-394.5, 155.71) * mm, "mid": v(-395.12, 152.77) * mm, "end": v(-395.48, 149.8) * mm});
            skLineSegment(sketch, "E1067", {"start": v(-395.48, 149.8) * mm, "end": v(-384.88, 149.8) * mm});
            skLineSegment(sketch, "E1068", {"start": v(-384.88, 149.8) * mm, "end": v(-384.88, 154.8) * mm});
            skLineSegment(sketch, "E1069", {"start": v(-384.88, 156.8) * mm, "end": v(-384.88, 157.8) * mm});
            skLineSegment(sketch, "E1070", {"start": v(-384.88, 157.8) * mm, "end": v(-381.48, 157.8) * mm});
            skLineSegment(sketch, "E1071", {"start": v(-381.48, 157.8) * mm, "end": v(-381.48, 156.8) * mm});
            skLineSegment(sketch, "E1072", {"start": v(-381.48, 154.8) * mm, "end": v(-381.48, 149.8) * mm});
            skLineSegment(sketch, "E1073", {"start": v(962.66, 138.68) * mm, "end": v(999.36, 138.68) * mm});
            skLineSegment(sketch, "E1074", {"start": v(962.66, 143.78) * mm, "end": v(962.66, 138.68) * mm});
            skLineSegment(sketch, "E1075", {"start": v(962.66, 143.78) * mm, "end": v(994.36, 143.78) * mm});
            skLineSegment(sketch, "E1076", {"start": v(994.36, 183.84) * mm, "end": v(994.36, 143.78) * mm});
            skLineSegment(sketch, "E1077", {"start": v(799.87, 176.49) * mm, "end": v(994.36, 183.84) * mm});
            skArc(sketch, "E1078", {"start": v(799.87, 176.49) * mm, "mid": v(791.38, 172.97) * mm, "end": v(787.86, 164.48) * mm});
            skLineSegment(sketch, "E1079", {"start": v(787.86, -36.01) * mm, "end": v(787.86, 164.48) * mm});
            skArc(sketch, "E1080", {"start": v(787.86, -36.01) * mm, "mid": v(791.38, -44.5) * mm, "end": v(799.87, -48.02) * mm});
            skLineSegment(sketch, "E1081", {"start": v(994.36, -55.38) * mm, "end": v(799.87, -48.02) * mm});
            skLineSegment(sketch, "E1082", {"start": v(994.36, -15.22) * mm, "end": v(994.36, -55.38) * mm});
            skLineSegment(sketch, "E1083", {"start": v(962.66, -15.22) * mm, "end": v(994.36, -15.22) * mm});
            skLineSegment(sketch, "E1084", {"start": v(962.66, -10.22) * mm, "end": v(962.66, -15.22) * mm});
            skLineSegment(sketch, "E1085", {"start": v(999.36, -10.22) * mm, "end": v(962.66, -10.22) * mm});
            skLineSegment(sketch, "E1086", {"start": v(999.36, 23.23) * mm, "end": v(999.36, -10.22) * mm});
            skLineSegment(sketch, "E1087", {"start": v(994.36, 23.23) * mm, "end": v(999.36, 23.23) * mm});
            skLineSegment(sketch, "E1088", {"start": v(994.36, 23.23) * mm, "end": v(994.36, 22.13) * mm});
            skLineSegment(sketch, "E1089", {"start": v(994.36, 22.13) * mm, "end": v(992.36, 22.13) * mm});
            skLineSegment(sketch, "E1090", {"start": v(992.36, 22.13) * mm, "end": v(992.36, 23.23) * mm});
            skLineSegment(sketch, "E1091", {"start": v(991.36, 23.23) * mm, "end": v(992.36, 23.23) * mm});
            skLineSegment(sketch, "E1092", {"start": v(991.36, 26.63) * mm, "end": v(991.36, 23.23) * mm});
            skLineSegment(sketch, "E1093", {"start": v(992.36, 26.63) * mm, "end": v(991.36, 26.63) * mm});
            skLineSegment(sketch, "E1094", {"start": v(992.36, 26.63) * mm, "end": v(992.36, 27.73) * mm});
            skLineSegment(sketch, "E1095", {"start": v(992.36, 27.73) * mm, "end": v(994.36, 27.73) * mm});
            skLineSegment(sketch, "E1096", {"start": v(994.36, 27.73) * mm, "end": v(994.36, 26.63) * mm});
            skLineSegment(sketch, "E1097", {"start": v(999.36, 26.63) * mm, "end": v(994.36, 26.63) * mm});
            skLineSegment(sketch, "E1098", {"start": v(999.36, 36) * mm, "end": v(999.36, 26.63) * mm});
            skLineSegment(sketch, "E1099", {"start": v(999.36, 36) * mm, "end": v(996.36, 36) * mm});
            skArc(sketch, "E1100", {"start": v(993.36, 39) * mm, "mid": v(994.24, 36.88) * mm, "end": v(996.36, 36) * mm});
            skLineSegment(sketch, "E1101", {"start": v(993.36, 39) * mm, "end": v(993.36, 89.2) * mm});
            skArc(sketch, "E1102", {"start": v(996.36, 92.2) * mm, "mid": v(994.24, 91.32) * mm, "end": v(993.36, 89.2) * mm});
            skLineSegment(sketch, "E1103", {"start": v(996.36, 92.2) * mm, "end": v(999.36, 92.2) * mm});
            skLineSegment(sketch, "E1104", {"start": v(999.36, 101.83) * mm, "end": v(999.36, 92.2) * mm});
            skLineSegment(sketch, "E1105", {"start": v(994.36, 101.83) * mm, "end": v(999.36, 101.83) * mm});
            skLineSegment(sketch, "E1106", {"start": v(994.36, 101.83) * mm, "end": v(994.36, 100.73) * mm});
            skLineSegment(sketch, "E1107", {"start": v(994.36, 100.73) * mm, "end": v(992.36, 100.73) * mm});
            skLineSegment(sketch, "E1108", {"start": v(992.36, 100.73) * mm, "end": v(992.36, 101.83) * mm});
            skLineSegment(sketch, "E1109", {"start": v(991.36, 101.83) * mm, "end": v(992.36, 101.83) * mm});
            skLineSegment(sketch, "E1110", {"start": v(991.36, 105.23) * mm, "end": v(991.36, 101.83) * mm});
            skLineSegment(sketch, "E1111", {"start": v(992.36, 105.23) * mm, "end": v(991.36, 105.23) * mm});
            skLineSegment(sketch, "E1112", {"start": v(992.36, 105.23) * mm, "end": v(992.36, 106.33) * mm});
            skLineSegment(sketch, "E1113", {"start": v(992.36, 106.33) * mm, "end": v(994.36, 106.33) * mm});
            skLineSegment(sketch, "E1114", {"start": v(994.36, 106.33) * mm, "end": v(994.36, 105.23) * mm});
            skLineSegment(sketch, "E1115", {"start": v(999.36, 105.23) * mm, "end": v(994.36, 105.23) * mm});
            skLineSegment(sketch, "E1116", {"start": v(999.36, 138.68) * mm, "end": v(999.36, 105.23) * mm});
            skLineSegment(sketch, "E1117", {"start": v(820.26, 138.78) * mm, "end": v(820.26, 143.78) * mm});
            skLineSegment(sketch, "E1118", {"start": v(820.26, 143.78) * mm, "end": v(860.26, 143.78) * mm});
            skLineSegment(sketch, "E1119", {"start": v(860.26, 143.78) * mm, "end": v(860.26, 138.78) * mm});
            skLineSegment(sketch, "E1120", {"start": v(860.26, 138.78) * mm, "end": v(820.26, 138.78) * mm});
            skLineSegment(sketch, "E1121", {"start": v(834.05, 60.34) * mm, "end": v(834.05, 24.56) * mm});
            skLineSegment(sketch, "E1122", {"start": v(834.05, 74.75) * mm, "end": v(834.05, 60.34) * mm});
            skLineSegment(sketch, "E1123", {"start": v(834.18, 77.8) * mm, "end": v(834.05, 74.75) * mm});
            skLineSegment(sketch, "E1124", {"start": v(834.56, 80.65) * mm, "end": v(834.18, 77.8) * mm});
            skLineSegment(sketch, "E1125", {"start": v(835.17, 83.24) * mm, "end": v(834.56, 80.65) * mm});
            skLineSegment(sketch, "E1126", {"start": v(836.11, 85.88) * mm, "end": v(835.17, 83.24) * mm});
            skLineSegment(sketch, "E1127", {"start": v(837.3, 88.3) * mm, "end": v(836.11, 85.88) * mm});
            skLineSegment(sketch, "E1128", {"start": v(838.75, 90.5) * mm, "end": v(837.3, 88.3) * mm});
            skLineSegment(sketch, "E1129", {"start": v(840.46, 92.5) * mm, "end": v(838.75, 90.5) * mm});
            skLineSegment(sketch, "E1130", {"start": v(842.42, 94.3) * mm, "end": v(840.46, 92.5) * mm});
            skLineSegment(sketch, "E1131", {"start": v(844.65, 95.91) * mm, "end": v(842.42, 94.3) * mm});
            skLineSegment(sketch, "E1132", {"start": v(847.17, 97.33) * mm, "end": v(844.65, 95.91) * mm});
            skLineSegment(sketch, "E1133", {"start": v(850, 98.55) * mm, "end": v(847.17, 97.33) * mm});
            skLineSegment(sketch, "E1134", {"start": v(853.12, 99.54) * mm, "end": v(850, 98.55) * mm});
            skLineSegment(sketch, "E1135", {"start": v(856.3, 100.25) * mm, "end": v(853.12, 99.54) * mm});
            skLineSegment(sketch, "E1136", {"start": v(859.6, 100.72) * mm, "end": v(856.3, 100.25) * mm});
            skLineSegment(sketch, "E1137", {"start": v(887.63, 103.68) * mm, "end": v(859.6, 100.72) * mm});
            skLineSegment(sketch, "E1138", {"start": v(891.11, 103.9) * mm, "end": v(887.63, 103.68) * mm});
            skLineSegment(sketch, "E1139", {"start": v(894.45, 103.85) * mm, "end": v(891.11, 103.9) * mm});
            skLineSegment(sketch, "E1140", {"start": v(897.32, 103.52) * mm, "end": v(894.45, 103.85) * mm});
            skLineSegment(sketch, "E1141", {"start": v(899.89, 102.95) * mm, "end": v(897.32, 103.52) * mm});
            skLineSegment(sketch, "E1142", {"start": v(902.19, 102.18) * mm, "end": v(899.89, 102.95) * mm});
            skLineSegment(sketch, "E1143", {"start": v(904.23, 101.2) * mm, "end": v(902.19, 102.18) * mm});
            skLineSegment(sketch, "E1144", {"start": v(906.04, 100.05) * mm, "end": v(904.23, 101.2) * mm});
            skLineSegment(sketch, "E1145", {"start": v(907.62, 98.72) * mm, "end": v(906.04, 100.05) * mm});
            skLineSegment(sketch, "E1146", {"start": v(909, 97.2) * mm, "end": v(907.62, 98.72) * mm});
            skLineSegment(sketch, "E1147", {"start": v(910.2, 95.5) * mm, "end": v(909, 97.2) * mm});
            skLineSegment(sketch, "E1148", {"start": v(911.2, 93.6) * mm, "end": v(910.2, 95.5) * mm});
            skLineSegment(sketch, "E1149", {"start": v(912.08, 91.22) * mm, "end": v(911.2, 93.6) * mm});
            skLineSegment(sketch, "E1150", {"start": v(912.72, 88.54) * mm, "end": v(912.08, 91.22) * mm});
            skLineSegment(sketch, "E1151", {"start": v(913.06, 85.94) * mm, "end": v(912.72, 88.54) * mm});
            skLineSegment(sketch, "E1152", {"start": v(913.17, 83.1) * mm, "end": v(913.06, 85.94) * mm});
            skLineSegment(sketch, "E1153", {"start": v(913.17, 32.9) * mm, "end": v(913.17, 83.1) * mm});
            skLineSegment(sketch, "E1154", {"start": v(905.57, 32.1) * mm, "end": v(913.17, 32.9) * mm});
            skLineSegment(sketch, "E1155", {"start": v(904.82, 32.07) * mm, "end": v(905.57, 32.1) * mm});
            skLineSegment(sketch, "E1156", {"start": v(904.2, 32.14) * mm, "end": v(904.82, 32.07) * mm});
            skLineSegment(sketch, "E1157", {"start": v(903.66, 32.31) * mm, "end": v(904.2, 32.14) * mm});
            skLineSegment(sketch, "E1158", {"start": v(903.24, 32.56) * mm, "end": v(903.66, 32.31) * mm});
            skLineSegment(sketch, "E1159", {"start": v(902.94, 32.85) * mm, "end": v(903.24, 32.56) * mm});
            skLineSegment(sketch, "E1160", {"start": v(902.75, 33.16) * mm, "end": v(902.94, 32.85) * mm});
            skLineSegment(sketch, "E1161", {"start": v(902.63, 33.44) * mm, "end": v(902.75, 33.16) * mm});
            skLineSegment(sketch, "E1162", {"start": v(902.56, 33.76) * mm, "end": v(902.63, 33.44) * mm});
            skLineSegment(sketch, "E1163", {"start": v(902.55, 33.89) * mm, "end": v(902.56, 33.76) * mm});
            skLineSegment(sketch, "E1164", {"start": v(902.55, 67.67) * mm, "end": v(902.55, 33.89) * mm});
            skLineSegment(sketch, "E1165", {"start": v(902.55, 81.98) * mm, "end": v(902.55, 67.67) * mm});
            skLineSegment(sketch, "E1166", {"start": v(902.41, 84.13) * mm, "end": v(902.55, 81.98) * mm});
            skLineSegment(sketch, "E1167", {"start": v(902, 86.07) * mm, "end": v(902.41, 84.13) * mm});
            skLineSegment(sketch, "E1168", {"start": v(901.4, 87.62) * mm, "end": v(902, 86.07) * mm});
            skLineSegment(sketch, "E1169", {"start": v(900.61, 88.94) * mm, "end": v(901.4, 87.62) * mm});
            skLineSegment(sketch, "E1170", {"start": v(899.63, 90.06) * mm, "end": v(900.61, 88.94) * mm});
            skLineSegment(sketch, "E1171", {"start": v(898.3, 91.08) * mm, "end": v(899.63, 90.06) * mm});
            skLineSegment(sketch, "E1172", {"start": v(896.72, 91.89) * mm, "end": v(898.3, 91.08) * mm});
            skLineSegment(sketch, "E1173", {"start": v(894.82, 92.47) * mm, "end": v(896.72, 91.89) * mm});
            skLineSegment(sketch, "E1174", {"start": v(892.55, 92.82) * mm, "end": v(894.82, 92.47) * mm});
            skLineSegment(sketch, "E1175", {"start": v(890.22, 92.89) * mm, "end": v(892.55, 92.82) * mm});
            skLineSegment(sketch, "E1176", {"start": v(887.63, 92.72) * mm, "end": v(890.22, 92.89) * mm});
            skLineSegment(sketch, "E1177", {"start": v(859.6, 89.76) * mm, "end": v(887.63, 92.72) * mm});
            skLineSegment(sketch, "E1178", {"start": v(856.73, 89.33) * mm, "end": v(859.6, 89.76) * mm});
            skLineSegment(sketch, "E1179", {"start": v(854.18, 88.67) * mm, "end": v(856.73, 89.33) * mm});
            skLineSegment(sketch, "E1180", {"start": v(852.08, 87.85) * mm, "end": v(854.18, 88.67) * mm});
            skLineSegment(sketch, "E1181", {"start": v(850.3, 86.89) * mm, "end": v(852.08, 87.85) * mm});
            skLineSegment(sketch, "E1182", {"start": v(848.8, 85.77) * mm, "end": v(850.3, 86.89) * mm});
            skLineSegment(sketch, "E1183", {"start": v(847.55, 84.53) * mm, "end": v(848.8, 85.77) * mm});
            skLineSegment(sketch, "E1184", {"start": v(846.44, 82.98) * mm, "end": v(847.55, 84.53) * mm});
            skLineSegment(sketch, "E1185", {"start": v(845.6, 81.24) * mm, "end": v(846.44, 82.98) * mm});
            skLineSegment(sketch, "E1186", {"start": v(845.02, 79.3) * mm, "end": v(845.6, 81.24) * mm});
            skLineSegment(sketch, "E1187", {"start": v(844.76, 77.64) * mm, "end": v(845.02, 79.3) * mm});
            skLineSegment(sketch, "E1188", {"start": v(844.67, 75.88) * mm, "end": v(844.76, 77.64) * mm});
            skLineSegment(sketch, "E1189", {"start": v(844.67, 27.78) * mm, "end": v(844.67, 75.88) * mm});
            skLineSegment(sketch, "E1190", {"start": v(844.61, 27.4) * mm, "end": v(844.67, 27.78) * mm});
            skLineSegment(sketch, "E1191", {"start": v(844.47, 27) * mm, "end": v(844.61, 27.4) * mm});
            skLineSegment(sketch, "E1192", {"start": v(844.28, 26.67) * mm, "end": v(844.47, 27) * mm});
            skLineSegment(sketch, "E1193", {"start": v(844, 26.32) * mm, "end": v(844.28, 26.67) * mm});
            skLineSegment(sketch, "E1194", {"start": v(843.54, 25.96) * mm, "end": v(844, 26.32) * mm});
            skLineSegment(sketch, "E1195", {"start": v(843, 25.68) * mm, "end": v(843.54, 25.96) * mm});
            skLineSegment(sketch, "E1196", {"start": v(842.4, 25.49) * mm, "end": v(843, 25.68) * mm});
            skLineSegment(sketch, "E1197", {"start": v(841.65, 25.36) * mm, "end": v(842.4, 25.49) * mm});
            skLineSegment(sketch, "E1198", {"start": v(834.05, 24.56) * mm, "end": v(841.65, 25.36) * mm});
            skLineSegment(sketch, "E1199", {"start": v(796.16, 161.88) * mm, "end": v(796.16, 167.08) * mm});
            skLineSegment(sketch, "E1200", {"start": v(795.16, 161.88) * mm, "end": v(796.16, 161.88) * mm});
            skLineSegment(sketch, "E1201", {"start": v(795.16, 167.08) * mm, "end": v(795.16, 161.88) * mm});
            skLineSegment(sketch, "E1202", {"start": v(796.16, 167.08) * mm, "end": v(795.16, 167.08) * mm});
            skLineSegment(sketch, "E1203", {"start": v(795.16, -33.41) * mm, "end": v(795.16, -38.61) * mm});
            skLineSegment(sketch, "E1204", {"start": v(796.16, -33.41) * mm, "end": v(795.16, -33.41) * mm});
            skLineSegment(sketch, "E1205", {"start": v(796.16, -38.61) * mm, "end": v(796.16, -33.41) * mm});
            skLineSegment(sketch, "E1206", {"start": v(795.16, -38.61) * mm, "end": v(796.16, -38.61) * mm});
            skLineSegment(sketch, "E1207", {"start": v(804.06, 167.08) * mm, "end": v(804.06, 161.88) * mm});
            skLineSegment(sketch, "E1208", {"start": v(805.06, 167.08) * mm, "end": v(804.06, 167.08) * mm});
            skLineSegment(sketch, "E1209", {"start": v(805.06, 161.88) * mm, "end": v(805.06, 167.08) * mm});
            skLineSegment(sketch, "E1210", {"start": v(804.06, 161.88) * mm, "end": v(805.06, 161.88) * mm});
            skLineSegment(sketch, "E1211", {"start": v(805.06, -38.61) * mm, "end": v(805.06, -33.41) * mm});
            skLineSegment(sketch, "E1212", {"start": v(804.06, -38.61) * mm, "end": v(805.06, -38.61) * mm});
            skLineSegment(sketch, "E1213", {"start": v(804.06, -33.41) * mm, "end": v(804.06, -38.61) * mm});
            skLineSegment(sketch, "E1214", {"start": v(805.06, -33.41) * mm, "end": v(804.06, -33.41) * mm});
            skCircle(sketch, "E1215", {"center": v(808, 141.18) * mm, "radius": 1.6 * mm});
            skCircle(sketch, "E1216", {"center": v(808, -12.72) * mm, "radius": 1.6 * mm});
            skCircle(sketch, "E1217", {"center": v(872.4, 141.18) * mm, "radius": 1.6 * mm});
            skCircle(sketch, "E1218", {"center": v(872.4, -12.72) * mm, "radius": 1.6 * mm});
            skLineSegment(sketch, "E1219", {"start": v(956.76, 161.93) * mm, "end": v(956.76, 167.13) * mm});
            skLineSegment(sketch, "E1220", {"start": v(955.76, 161.93) * mm, "end": v(956.76, 161.93) * mm});
            skLineSegment(sketch, "E1221", {"start": v(955.76, 167.13) * mm, "end": v(955.76, 161.93) * mm});
            skLineSegment(sketch, "E1222", {"start": v(956.76, 167.13) * mm, "end": v(955.76, 167.13) * mm});
            skLineSegment(sketch, "E1223", {"start": v(956.76, -38.67) * mm, "end": v(956.76, -33.47) * mm});
            skLineSegment(sketch, "E1224", {"start": v(955.76, -38.67) * mm, "end": v(956.76, -38.67) * mm});
            skLineSegment(sketch, "E1225", {"start": v(955.76, -33.47) * mm, "end": v(955.76, -38.67) * mm});
            skLineSegment(sketch, "E1226", {"start": v(956.76, -33.47) * mm, "end": v(955.76, -33.47) * mm});
            skCircle(sketch, "E1227", {"center": v(956.06, 141.18) * mm, "radius": 1.6 * mm});
            skCircle(sketch, "E1228", {"center": v(960.46, -36.07) * mm, "radius": 2 * mm});
            skLineSegment(sketch, "E1229", {"start": v(964.66, -33.47) * mm, "end": v(964.66, -38.67) * mm});
            skLineSegment(sketch, "E1230", {"start": v(965.66, -33.47) * mm, "end": v(964.66, -33.47) * mm});
            skLineSegment(sketch, "E1231", {"start": v(965.66, -38.67) * mm, "end": v(965.66, -33.47) * mm});
            skLineSegment(sketch, "E1232", {"start": v(964.66, -38.67) * mm, "end": v(965.66, -38.67) * mm});
            skLineSegment(sketch, "E1233", {"start": v(964.66, 167.13) * mm, "end": v(964.66, 161.93) * mm});
            skLineSegment(sketch, "E1234", {"start": v(965.66, 167.13) * mm, "end": v(964.66, 167.13) * mm});
            skLineSegment(sketch, "E1235", {"start": v(965.66, 161.93) * mm, "end": v(965.66, 167.13) * mm});
            skLineSegment(sketch, "E1236", {"start": v(964.66, 161.93) * mm, "end": v(965.66, 161.93) * mm});
            skCircle(sketch, "E1237", {"center": v(799.86, 164.48) * mm, "radius": 2 * mm});
            skCircle(sketch, "E1238", {"center": v(956.06, -12.72) * mm, "radius": 1.6 * mm});
            skCircle(sketch, "E1239", {"center": v(799.86, -36.01) * mm, "radius": 2 * mm});
            skCircle(sketch, "E1240", {"center": v(960.46, 164.53) * mm, "radius": 2 * mm});
            skLineSegment(sketch, "E1241", {"start": v(867.5, -41.01) * mm, "end": v(871.5, -41.01) * mm});
            skLineSegment(sketch, "E1242", {"start": v(867.5, -39.01) * mm, "end": v(867.5, -41.01) * mm});
            skLineSegment(sketch, "E1243", {"start": v(871.5, -39.01) * mm, "end": v(867.5, -39.01) * mm});
            skLineSegment(sketch, "E1244", {"start": v(871.5, -41.01) * mm, "end": v(871.5, -39.01) * mm});
            skLineSegment(sketch, "E1245", {"start": v(867.5, -33.01) * mm, "end": v(871.5, -33.01) * mm});
            skLineSegment(sketch, "E1246", {"start": v(867.5, -31.01) * mm, "end": v(867.5, -33.01) * mm});
            skLineSegment(sketch, "E1247", {"start": v(871.5, -31.01) * mm, "end": v(867.5, -31.01) * mm});
            skLineSegment(sketch, "E1248", {"start": v(871.5, -33.01) * mm, "end": v(871.5, -31.01) * mm});
            skLineSegment(sketch, "E1249", {"start": v(867.5, 159.48) * mm, "end": v(871.5, 159.48) * mm});
            skLineSegment(sketch, "E1250", {"start": v(867.5, 161.48) * mm, "end": v(867.5, 159.48) * mm});
            skLineSegment(sketch, "E1251", {"start": v(871.5, 161.48) * mm, "end": v(867.5, 161.48) * mm});
            skLineSegment(sketch, "E1252", {"start": v(871.5, 159.48) * mm, "end": v(871.5, 161.48) * mm});
            skLineSegment(sketch, "E1253", {"start": v(934.7, -39.01) * mm, "end": v(938.7, -39.01) * mm});
            skLineSegment(sketch, "E1254", {"start": v(938.7, -39.01) * mm, "end": v(938.7, -41.01) * mm});
            skLineSegment(sketch, "E1255", {"start": v(938.7, -41.01) * mm, "end": v(934.7, -41.01) * mm});
            skLineSegment(sketch, "E1256", {"start": v(934.7, -41.01) * mm, "end": v(934.7, -39.01) * mm});
            skLineSegment(sketch, "E1257", {"start": v(934.7, -31.01) * mm, "end": v(938.7, -31.01) * mm});
            skLineSegment(sketch, "E1258", {"start": v(938.7, -31.01) * mm, "end": v(938.7, -33.01) * mm});
            skLineSegment(sketch, "E1259", {"start": v(938.7, -33.01) * mm, "end": v(934.7, -33.01) * mm});
            skLineSegment(sketch, "E1260", {"start": v(934.7, -33.01) * mm, "end": v(934.7, -31.01) * mm});
            skLineSegment(sketch, "E1261", {"start": v(867.5, 167.48) * mm, "end": v(871.5, 167.48) * mm});
            skLineSegment(sketch, "E1262", {"start": v(867.5, 169.48) * mm, "end": v(867.5, 167.48) * mm});
            skLineSegment(sketch, "E1263", {"start": v(871.5, 169.48) * mm, "end": v(867.5, 169.48) * mm});
            skLineSegment(sketch, "E1264", {"start": v(871.5, 167.48) * mm, "end": v(871.5, 169.48) * mm});
            skLineSegment(sketch, "E1265", {"start": v(934.7, 161.48) * mm, "end": v(938.7, 161.48) * mm});
            skLineSegment(sketch, "E1266", {"start": v(938.7, 161.48) * mm, "end": v(938.7, 159.48) * mm});
            skLineSegment(sketch, "E1267", {"start": v(938.7, 159.48) * mm, "end": v(934.7, 159.48) * mm});
            skLineSegment(sketch, "E1268", {"start": v(934.7, 159.48) * mm, "end": v(934.7, 161.48) * mm});
            skLineSegment(sketch, "E1269", {"start": v(934.7, 169.48) * mm, "end": v(938.7, 169.48) * mm});
            skLineSegment(sketch, "E1270", {"start": v(938.7, 169.48) * mm, "end": v(938.7, 167.48) * mm});
            skLineSegment(sketch, "E1271", {"start": v(938.7, 167.48) * mm, "end": v(934.7, 167.48) * mm});
            skLineSegment(sketch, "E1272", {"start": v(934.7, 167.48) * mm, "end": v(934.7, 169.48) * mm});
            skLineSegment(sketch, "E1273", {"start": v(976.34, 66.23) * mm, "end": v(976.34, 62.23) * mm});
            skLineSegment(sketch, "E1274", {"start": v(976.34, 62.23) * mm, "end": v(974.34, 62.23) * mm});
            skLineSegment(sketch, "E1275", {"start": v(974.34, 62.23) * mm, "end": v(974.34, 66.23) * mm});
            skLineSegment(sketch, "E1276", {"start": v(974.34, 66.23) * mm, "end": v(976.34, 66.23) * mm});
            skLineSegment(sketch, "E1277", {"start": v(982.34, 62.23) * mm, "end": v(982.34, 66.23) * mm});
            skLineSegment(sketch, "E1278", {"start": v(982.34, 66.23) * mm, "end": v(984.34, 66.23) * mm});
            skLineSegment(sketch, "E1279", {"start": v(984.34, 66.23) * mm, "end": v(984.34, 62.23) * mm});
            skLineSegment(sketch, "E1280", {"start": v(984.34, 62.23) * mm, "end": v(982.34, 62.23) * mm});
            skLineSegment(sketch, "E1281", {"start": v(867.86, 64.01) * mm, "end": v(878.21, 65.1) * mm});
            skLineSegment(sketch, "E1282", {"start": v(878.21, 65.1) * mm, "end": v(878.21, 39.4) * mm});
            skArc(sketch, "E1283", {"start": v(876.86, 37.9) * mm, "mid": v(877.82, 38.4) * mm, "end": v(878.21, 39.4) * mm});
            skLineSegment(sketch, "E1284", {"start": v(876.86, 37.9) * mm, "end": v(869.53, 37.13) * mm});
            skArc(sketch, "E1285", {"start": v(867.86, 38.63) * mm, "mid": v(868.36, 37.5) * mm, "end": v(869.53, 37.13) * mm});
            skLineSegment(sketch, "E1286", {"start": v(867.86, 38.63) * mm, "end": v(867.86, 64.01) * mm});
            skLineSegment(sketch, "E1287", {"start": v(820.26, -15.22) * mm, "end": v(820.26, -10.22) * mm});
            skLineSegment(sketch, "E1288", {"start": v(820.26, -10.22) * mm, "end": v(860.26, -10.22) * mm});
            skLineSegment(sketch, "E1289", {"start": v(860.26, -10.22) * mm, "end": v(860.26, -15.22) * mm});
            skLineSegment(sketch, "E1290", {"start": v(860.26, -15.22) * mm, "end": v(820.26, -15.22) * mm});
            skLineSegment(sketch, "E1291", {"start": v(939.26, -15.22) * mm, "end": v(889.26, -15.22) * mm});
            skLineSegment(sketch, "E1292", {"start": v(889.26, -15.22) * mm, "end": v(889.26, -10.22) * mm});
            skLineSegment(sketch, "E1293", {"start": v(889.26, -10.22) * mm, "end": v(939.26, -10.22) * mm});
            skLineSegment(sketch, "E1294", {"start": v(939.26, -10.22) * mm, "end": v(939.26, -15.22) * mm});
            skLineSegment(sketch, "E1295", {"start": v(889.26, 143.78) * mm, "end": v(939.26, 143.78) * mm});
            skLineSegment(sketch, "E1296", {"start": v(939.26, 143.78) * mm, "end": v(939.26, 138.78) * mm});
            skLineSegment(sketch, "E1297", {"start": v(939.26, 138.78) * mm, "end": v(889.26, 138.78) * mm});
            skLineSegment(sketch, "E1298", {"start": v(889.26, 138.78) * mm, "end": v(889.26, 143.78) * mm});
            skCircle(sketch, "E1299", {"center": v(-531.87, -155.93) * mm, "radius": 3.5 * mm});
            skCircle(sketch, "E1300", {"center": v(-531.87, -155.93) * mm, "radius": 1.65 * mm});
            skLineSegment(sketch, "E1301", {"start": v(-626.32, -210.15) * mm, "end": v(-626.32, -205.15) * mm});
            skCircle(sketch, "E1302", {"center": v(-577.36, -207.65) * mm, "radius": 1.6 * mm});
            skCircle(sketch, "E1303", {"center": v(-607.36, -207.65) * mm, "radius": 1.6 * mm});
            skArc(sketch, "E1304", {"start": v(-635.7, -200.51) * mm, "mid": v(-636.96, -201.08) * mm, "end": v(-637.48, -202.37) * mm});
            skArc(sketch, "E1305", {"start": v(-637.48, -212.93) * mm, "mid": v(-636.96, -214.22) * mm, "end": v(-635.7, -214.79) * mm});
            skArc(sketch, "E1306", {"start": v(-607.88, -200.61) * mm, "mid": v(-606.64, -199.91) * mm, "end": v(-607.36, -198.68) * mm});
            skArc(sketch, "E1307", {"start": v(-607.36, -216.62) * mm, "mid": v(-606.64, -215.39) * mm, "end": v(-607.88, -214.69) * mm});
            skArc(sketch, "E1308", {"start": v(-632.95, -232.1) * mm, "mid": v(-631.4, -231.03) * mm, "end": v(-630.8, -229.23) * mm});
            skArc(sketch, "E1309", {"start": v(-638.17, -228.47) * mm, "mid": v(-637.68, -228.27) * mm, "end": v(-637.48, -227.78) * mm});
            skArc(sketch, "E1310", {"start": v(-630.8, -186.07) * mm, "mid": v(-631.4, -184.27) * mm, "end": v(-632.95, -183.19) * mm});
            skArc(sketch, "E1311", {"start": v(-637.48, -187.51) * mm, "mid": v(-637.68, -187.03) * mm, "end": v(-638.17, -186.82) * mm});
            skArc(sketch, "E1312", {"start": v(-630.8, -191.24) * mm, "mid": v(-630.67, -191.53) * mm, "end": v(-630.38, -191.65) * mm});
            skArc(sketch, "E1313", {"start": v(-630.38, -223.65) * mm, "mid": v(-630.67, -223.77) * mm, "end": v(-630.8, -224.06) * mm});
            skArc(sketch, "E1314", {"start": v(-637.48, -193.14) * mm, "mid": v(-635.77, -197.12) * mm, "end": v(-631.7, -198.63) * mm});
            skArc(sketch, "E1315", {"start": v(-631.7, -216.67) * mm, "mid": v(-635.77, -218.17) * mm, "end": v(-637.48, -222.16) * mm});
            skLineSegment(sketch, "E1316", {"start": v(-637.48, -227.78) * mm, "end": v(-637.48, -222.16) * mm});
            skLineSegment(sketch, "E1317", {"start": v(-638.17, -228.47) * mm, "end": v(-645.98, -228.47) * mm});
            skLineSegment(sketch, "E1318", {"start": v(-645.98, -228.47) * mm, "end": v(-645.98, -233.1) * mm});
            skLineSegment(sketch, "E1319", {"start": v(-645.98, -233.1) * mm, "end": v(-642.48, -234.27) * mm});
            skLineSegment(sketch, "E1320", {"start": v(-642.48, -234.27) * mm, "end": v(-642.48, -233.27) * mm});
            skLineSegment(sketch, "E1321", {"start": v(-642.48, -233.27) * mm, "end": v(-636.89, -233.27) * mm});
            skLineSegment(sketch, "E1322", {"start": v(-636.89, -233.27) * mm, "end": v(-632.95, -232.1) * mm});
            skLineSegment(sketch, "E1323", {"start": v(-630.8, -229.23) * mm, "end": v(-630.8, -224.06) * mm});
            skLineSegment(sketch, "E1324", {"start": v(-630.38, -223.65) * mm, "end": v(-619.48, -223.65) * mm});
            skLineSegment(sketch, "E1325", {"start": v(-603.42, -221.9) * mm, "end": v(-619.48, -223.65) * mm});
            skLineSegment(sketch, "E1326", {"start": v(-603.42, -221.9) * mm, "end": v(-561.23, -211.71) * mm});
            skLineSegment(sketch, "E1327", {"start": v(-561.23, -211.71) * mm, "end": v(-561.23, -210.15) * mm});
            skLineSegment(sketch, "E1328", {"start": v(-561.23, -210.15) * mm, "end": v(-565.23, -210.15) * mm});
            skLineSegment(sketch, "E1329", {"start": v(-565.23, -210.15) * mm, "end": v(-565.23, -205.15) * mm});
            skLineSegment(sketch, "E1330", {"start": v(-565.23, -205.15) * mm, "end": v(-561.23, -205.15) * mm});
            skLineSegment(sketch, "E1331", {"start": v(-561.23, -205.15) * mm, "end": v(-561.23, -203.58) * mm});
            skLineSegment(sketch, "E1332", {"start": v(-561.23, -203.58) * mm, "end": v(-603.42, -193.4) * mm});
            skLineSegment(sketch, "E1333", {"start": v(-619.46, -191.65) * mm, "end": v(-603.42, -193.4) * mm});
            skLineSegment(sketch, "E1334", {"start": v(-630.38, -191.65) * mm, "end": v(-619.46, -191.65) * mm});
            skLineSegment(sketch, "E1335", {"start": v(-630.8, -191.24) * mm, "end": v(-630.8, -186.07) * mm});
            skLineSegment(sketch, "E1336", {"start": v(-632.95, -183.19) * mm, "end": v(-636.89, -182.02) * mm});
            skLineSegment(sketch, "E1337", {"start": v(-636.89, -182.02) * mm, "end": v(-642.48, -182.02) * mm});
            skLineSegment(sketch, "E1338", {"start": v(-642.48, -182.02) * mm, "end": v(-642.48, -181.02) * mm});
            skLineSegment(sketch, "E1339", {"start": v(-642.48, -181.02) * mm, "end": v(-645.98, -182.2) * mm});
            skLineSegment(sketch, "E1340", {"start": v(-645.98, -182.2) * mm, "end": v(-645.98, -186.82) * mm});
            skLineSegment(sketch, "E1341", {"start": v(-645.98, -186.82) * mm, "end": v(-638.17, -186.82) * mm});
            skLineSegment(sketch, "E1342", {"start": v(-637.48, -193.14) * mm, "end": v(-637.48, -187.51) * mm});
            skLineSegment(sketch, "E1343", {"start": v(-611.56, -197.6) * mm, "end": v(-631.7, -198.63) * mm});
            skArc(sketch, "E1344", {"start": v(-611.31, -197.65) * mm, "mid": v(-611.43, -197.62) * mm, "end": v(-611.56, -197.6) * mm});
            skLineSegment(sketch, "E1345", {"start": v(-611.31, -197.65) * mm, "end": v(-607.36, -198.68) * mm});
            skLineSegment(sketch, "E1346", {"start": v(-611.49, -199.6) * mm, "end": v(-607.88, -200.61) * mm});
            skLineSegment(sketch, "E1347", {"start": v(-635.7, -200.51) * mm, "end": v(-611.49, -199.6) * mm});
            skLineSegment(sketch, "E1348", {"start": v(-637.48, -202.37) * mm, "end": v(-637.48, -212.93) * mm});
            skLineSegment(sketch, "E1349", {"start": v(-611.49, -215.7) * mm, "end": v(-635.7, -214.79) * mm});
            skLineSegment(sketch, "E1350", {"start": v(-611.49, -215.7) * mm, "end": v(-607.88, -214.69) * mm});
            skLineSegment(sketch, "E1351", {"start": v(-611.31, -217.65) * mm, "end": v(-607.36, -216.62) * mm});
            skArc(sketch, "E1352", {"start": v(-611.56, -217.7) * mm, "mid": v(-611.43, -217.68) * mm, "end": v(-611.31, -217.65) * mm});
            skLineSegment(sketch, "E1353", {"start": v(-631.7, -216.67) * mm, "end": v(-611.56, -217.7) * mm});
            skLineSegment(sketch, "E1354", {"start": v(-616.32, -210.15) * mm, "end": v(-626.32, -210.15) * mm});
            skLineSegment(sketch, "E1355", {"start": v(-626.32, -205.15) * mm, "end": v(-616.32, -205.15) * mm});
            skLineSegment(sketch, "E1356", {"start": v(-616.32, -205.15) * mm, "end": v(-616.32, -210.15) * mm});
            skLineSegment(sketch, "E1357", {"start": v(-598.98, -210.15) * mm, "end": v(-598.98, -205.15) * mm});
            skLineSegment(sketch, "E1358", {"start": v(-583.3, -205.15) * mm, "end": v(-598.98, -205.15) * mm});
            skLineSegment(sketch, "E1359", {"start": v(-583.3, -205.15) * mm, "end": v(-583.3, -210.15) * mm});
            skLineSegment(sketch, "E1360", {"start": v(-598.98, -210.15) * mm, "end": v(-583.3, -210.15) * mm});
            skLineSegment(sketch, "E1361", {"start": v(-516.5, 24.42) * mm, "end": v(-516.5, 23.32) * mm});
            skLineSegment(sketch, "E1362", {"start": v(-516.5, 24.42) * mm, "end": v(-521.5, 24.42) * mm});
            skLineSegment(sketch, "E1363", {"start": v(-521.5, 24.42) * mm, "end": v(-521.5, 18.12) * mm});
            skLineSegment(sketch, "E1364", {"start": v(-521.5, 18.12) * mm, "end": v(-491.5, 18.12) * mm});
            skLineSegment(sketch, "E1365", {"start": v(-491.5, 18.12) * mm, "end": v(-491.5, 48.12) * mm});
            skLineSegment(sketch, "E1366", {"start": v(-491.5, 48.12) * mm, "end": v(-521.5, 48.12) * mm});
            skLineSegment(sketch, "E1367", {"start": v(-521.5, 48.12) * mm, "end": v(-521.5, 41.82) * mm});
            skLineSegment(sketch, "E1368", {"start": v(-521.5, 41.82) * mm, "end": v(-516.5, 41.82) * mm});
            skLineSegment(sketch, "E1369", {"start": v(-516.5, 42.92) * mm, "end": v(-516.5, 41.82) * mm});
            skLineSegment(sketch, "E1370", {"start": v(-514.5, 42.92) * mm, "end": v(-516.5, 42.92) * mm});
            skLineSegment(sketch, "E1371", {"start": v(-514.5, 41.82) * mm, "end": v(-514.5, 42.92) * mm});
            skLineSegment(sketch, "E1372", {"start": v(-514.5, 41.82) * mm, "end": v(-513.5, 41.82) * mm});
            skLineSegment(sketch, "E1373", {"start": v(-513.5, 41.82) * mm, "end": v(-513.5, 38.42) * mm});
            skLineSegment(sketch, "E1374", {"start": v(-513.5, 38.42) * mm, "end": v(-514.5, 38.42) * mm});
            skLineSegment(sketch, "E1375", {"start": v(-514.5, 37.32) * mm, "end": v(-514.5, 38.42) * mm});
            skLineSegment(sketch, "E1376", {"start": v(-516.5, 37.32) * mm, "end": v(-514.5, 37.32) * mm});
            skLineSegment(sketch, "E1377", {"start": v(-516.5, 38.42) * mm, "end": v(-516.5, 37.32) * mm});
            skLineSegment(sketch, "E1378", {"start": v(-516.5, 38.42) * mm, "end": v(-521.5, 38.42) * mm});
            skLineSegment(sketch, "E1379", {"start": v(-521.5, 38.42) * mm, "end": v(-521.5, 27.82) * mm});
            skLineSegment(sketch, "E1380", {"start": v(-521.5, 27.82) * mm, "end": v(-516.5, 27.82) * mm});
            skLineSegment(sketch, "E1381", {"start": v(-516.5, 28.92) * mm, "end": v(-516.5, 27.82) * mm});
            skLineSegment(sketch, "E1382", {"start": v(-514.5, 28.92) * mm, "end": v(-516.5, 28.92) * mm});
            skLineSegment(sketch, "E1383", {"start": v(-514.5, 27.82) * mm, "end": v(-514.5, 28.92) * mm});
            skLineSegment(sketch, "E1384", {"start": v(-514.5, 27.82) * mm, "end": v(-513.5, 27.82) * mm});
            skLineSegment(sketch, "E1385", {"start": v(-513.5, 27.82) * mm, "end": v(-513.5, 24.42) * mm});
            skLineSegment(sketch, "E1386", {"start": v(-513.5, 24.42) * mm, "end": v(-514.5, 24.42) * mm});
            skLineSegment(sketch, "E1387", {"start": v(-514.5, 23.32) * mm, "end": v(-514.5, 24.42) * mm});
            skLineSegment(sketch, "E1388", {"start": v(-516.5, 23.32) * mm, "end": v(-514.5, 23.32) * mm});
            skCircle(sketch, "E1389", {"center": v(-494, 26.12) * mm, "radius": 1.6 * mm});
            skCircle(sketch, "E1390", {"center": v(-494, 40.12) * mm, "radius": 1.6 * mm});
            skLineSegment(sketch, "E1391", {"start": v(925.28, -60.18) * mm, "end": v(925.28, -61.28) * mm});
            skLineSegment(sketch, "E1392", {"start": v(925.28, -61.28) * mm, "end": v(930.28, -61.28) * mm});
            skLineSegment(sketch, "E1393", {"start": v(930.28, -55.98) * mm, "end": v(930.28, -61.28) * mm});
            skLineSegment(sketch, "E1394", {"start": v(895.28, -55.98) * mm, "end": v(930.28, -55.98) * mm});
            skLineSegment(sketch, "E1395", {"start": v(895.28, -61.28) * mm, "end": v(895.28, -55.98) * mm});
            skLineSegment(sketch, "E1396", {"start": v(900.28, -61.28) * mm, "end": v(895.28, -61.28) * mm});
            skLineSegment(sketch, "E1397", {"start": v(900.28, -60.18) * mm, "end": v(900.28, -61.28) * mm});
            skLineSegment(sketch, "E1398", {"start": v(902.28, -60.18) * mm, "end": v(900.28, -60.18) * mm});
            skLineSegment(sketch, "E1399", {"start": v(902.28, -61.28) * mm, "end": v(902.28, -60.18) * mm});
            skLineSegment(sketch, "E1400", {"start": v(903.28, -61.28) * mm, "end": v(902.28, -61.28) * mm});
            skLineSegment(sketch, "E1401", {"start": v(903.28, -64.68) * mm, "end": v(903.28, -61.28) * mm});
            skLineSegment(sketch, "E1402", {"start": v(902.28, -64.68) * mm, "end": v(903.28, -64.68) * mm});
            skLineSegment(sketch, "E1403", {"start": v(902.28, -65.78) * mm, "end": v(902.28, -64.68) * mm});
            skLineSegment(sketch, "E1404", {"start": v(900.28, -65.78) * mm, "end": v(902.28, -65.78) * mm});
            skLineSegment(sketch, "E1405", {"start": v(900.28, -64.68) * mm, "end": v(900.28, -65.78) * mm});
            skLineSegment(sketch, "E1406", {"start": v(895.28, -64.68) * mm, "end": v(900.28, -64.68) * mm});
            skLineSegment(sketch, "E1407", {"start": v(895.28, -68.98) * mm, "end": v(895.28, -64.68) * mm});
            skLineSegment(sketch, "E1408", {"start": v(890.28, -68.98) * mm, "end": v(895.28, -68.98) * mm});
            skLineSegment(sketch, "E1409", {"start": v(890.28, -78.98) * mm, "end": v(890.28, -68.98) * mm});
            skLineSegment(sketch, "E1410", {"start": v(895.28, -78.98) * mm, "end": v(890.28, -78.98) * mm});
            skLineSegment(sketch, "E1411", {"start": v(895.28, -81.98) * mm, "end": v(895.28, -78.98) * mm});
            skLineSegment(sketch, "E1412", {"start": v(895.28, -81.98) * mm, "end": v(900.28, -81.98) * mm});
            skLineSegment(sketch, "E1413", {"start": v(900.28, -81.98) * mm, "end": v(900.28, -80.88) * mm});
            skLineSegment(sketch, "E1414", {"start": v(900.28, -80.88) * mm, "end": v(902.28, -80.88) * mm});
            skLineSegment(sketch, "E1415", {"start": v(902.28, -80.88) * mm, "end": v(902.28, -81.98) * mm});
            skLineSegment(sketch, "E1416", {"start": v(902.28, -81.98) * mm, "end": v(903.28, -81.98) * mm});
            skLineSegment(sketch, "E1417", {"start": v(903.28, -81.98) * mm, "end": v(903.28, -85.38) * mm});
            skLineSegment(sketch, "E1418", {"start": v(903.28, -85.38) * mm, "end": v(902.28, -85.38) * mm});
            skLineSegment(sketch, "E1419", {"start": v(902.28, -85.38) * mm, "end": v(902.28, -86.48) * mm});
            skLineSegment(sketch, "E1420", {"start": v(902.28, -86.48) * mm, "end": v(900.28, -86.48) * mm});
            skLineSegment(sketch, "E1421", {"start": v(900.28, -86.48) * mm, "end": v(900.28, -85.38) * mm});
            skLineSegment(sketch, "E1422", {"start": v(900.28, -85.38) * mm, "end": v(895.28, -85.38) * mm});
            skLineSegment(sketch, "E1423", {"start": v(895.28, -100.98) * mm, "end": v(895.28, -85.38) * mm});
            skLineSegment(sketch, "E1424", {"start": v(899.28, -100.98) * mm, "end": v(895.28, -100.98) * mm});
            skLineSegment(sketch, "E1425", {"start": v(899.28, -95.98) * mm, "end": v(899.28, -100.98) * mm});
            skLineSegment(sketch, "E1426", {"start": v(898.18, -95.98) * mm, "end": v(899.28, -95.98) * mm});
            skLineSegment(sketch, "E1427", {"start": v(898.18, -93.98) * mm, "end": v(898.18, -95.98) * mm});
            skLineSegment(sketch, "E1428", {"start": v(899.28, -93.98) * mm, "end": v(898.18, -93.98) * mm});
            skLineSegment(sketch, "E1429", {"start": v(899.28, -92.98) * mm, "end": v(899.28, -93.98) * mm});
            skLineSegment(sketch, "E1430", {"start": v(902.68, -92.98) * mm, "end": v(899.28, -92.98) * mm});
            skLineSegment(sketch, "E1431", {"start": v(902.68, -93.98) * mm, "end": v(902.68, -92.98) * mm});
            skLineSegment(sketch, "E1432", {"start": v(903.78, -93.98) * mm, "end": v(902.68, -93.98) * mm});
            skLineSegment(sketch, "E1433", {"start": v(903.78, -95.98) * mm, "end": v(903.78, -93.98) * mm});
            skLineSegment(sketch, "E1434", {"start": v(902.68, -95.98) * mm, "end": v(903.78, -95.98) * mm});
            skLineSegment(sketch, "E1435", {"start": v(902.68, -100.98) * mm, "end": v(902.68, -95.98) * mm});
            skLineSegment(sketch, "E1436", {"start": v(907.28, -100.98) * mm, "end": v(902.68, -100.98) * mm});
            skLineSegment(sketch, "E1437", {"start": v(907.28, -105.98) * mm, "end": v(907.28, -100.98) * mm});
            skLineSegment(sketch, "E1438", {"start": v(916.28, -105.98) * mm, "end": v(907.28, -105.98) * mm});
            skLineSegment(sketch, "E1439", {"start": v(916.28, -100.98) * mm, "end": v(916.28, -105.98) * mm});
            skLineSegment(sketch, "E1440", {"start": v(920.88, -100.98) * mm, "end": v(916.28, -100.98) * mm});
            skLineSegment(sketch, "E1441", {"start": v(920.88, -95.98) * mm, "end": v(920.88, -100.98) * mm});
            skLineSegment(sketch, "E1442", {"start": v(919.78, -95.98) * mm, "end": v(920.88, -95.98) * mm});
            skLineSegment(sketch, "E1443", {"start": v(919.78, -93.98) * mm, "end": v(919.78, -95.98) * mm});
            skLineSegment(sketch, "E1444", {"start": v(920.88, -93.98) * mm, "end": v(919.78, -93.98) * mm});
            skLineSegment(sketch, "E1445", {"start": v(920.88, -92.98) * mm, "end": v(920.88, -93.98) * mm});
            skLineSegment(sketch, "E1446", {"start": v(924.28, -92.98) * mm, "end": v(920.88, -92.98) * mm});
            skLineSegment(sketch, "E1447", {"start": v(924.28, -93.98) * mm, "end": v(924.28, -92.98) * mm});
            skLineSegment(sketch, "E1448", {"start": v(925.38, -93.98) * mm, "end": v(924.28, -93.98) * mm});
            skLineSegment(sketch, "E1449", {"start": v(925.38, -95.98) * mm, "end": v(925.38, -93.98) * mm});
            skLineSegment(sketch, "E1450", {"start": v(924.28, -95.98) * mm, "end": v(925.38, -95.98) * mm});
            skLineSegment(sketch, "E1451", {"start": v(924.28, -100.98) * mm, "end": v(924.28, -95.98) * mm});
            skLineSegment(sketch, "E1452", {"start": v(930.28, -100.98) * mm, "end": v(924.28, -100.98) * mm});
            skLineSegment(sketch, "E1453", {"start": v(930.28, -87.48) * mm, "end": v(930.28, -100.98) * mm});
            skLineSegment(sketch, "E1454", {"start": v(930.28, -87.48) * mm, "end": v(935.28, -87.48) * mm});
            skLineSegment(sketch, "E1455", {"start": v(935.28, -87.48) * mm, "end": v(935.28, -69.48) * mm});
            skLineSegment(sketch, "E1456", {"start": v(930.28, -69.48) * mm, "end": v(935.28, -69.48) * mm});
            skLineSegment(sketch, "E1457", {"start": v(930.28, -64.68) * mm, "end": v(930.28, -69.48) * mm});
            skLineSegment(sketch, "E1458", {"start": v(930.28, -64.68) * mm, "end": v(925.28, -64.68) * mm});
            skLineSegment(sketch, "E1459", {"start": v(925.28, -64.68) * mm, "end": v(925.28, -65.78) * mm});
            skLineSegment(sketch, "E1460", {"start": v(925.28, -65.78) * mm, "end": v(923.28, -65.78) * mm});
            skLineSegment(sketch, "E1461", {"start": v(923.28, -65.78) * mm, "end": v(923.28, -64.68) * mm});
            skLineSegment(sketch, "E1462", {"start": v(923.28, -64.68) * mm, "end": v(922.28, -64.68) * mm});
            skLineSegment(sketch, "E1463", {"start": v(922.28, -64.68) * mm, "end": v(922.28, -61.28) * mm});
            skLineSegment(sketch, "E1464", {"start": v(922.28, -61.28) * mm, "end": v(923.28, -61.28) * mm});
            skLineSegment(sketch, "E1465", {"start": v(923.28, -61.28) * mm, "end": v(923.28, -60.18) * mm});
            skLineSegment(sketch, "E1466", {"start": v(923.28, -60.18) * mm, "end": v(925.28, -60.18) * mm});
            skLineSegment(sketch, "E1467", {"start": v(795.21, -53.7) * mm, "end": v(830.66, -53.7) * mm});
            skCircle(sketch, "E1468", {"center": v(836.54, -65.1) * mm, "radius": 1.6 * mm});
            skCircle(sketch, "E1469", {"center": v(828.44, -91.1) * mm, "radius": 1.6 * mm});
            skCircle(sketch, "E1470", {"center": v(828.44, -60.1) * mm, "radius": 1.6 * mm});
            skCircle(sketch, "E1471", {"center": v(797.44, -60.1) * mm, "radius": 1.6 * mm});
            skCircle(sketch, "E1472", {"center": v(812.94, -75.6) * mm, "radius": 12.5 * mm});
            skCircle(sketch, "E1473", {"center": v(789.34, -65.1) * mm, "radius": 1.6 * mm});
            skCircle(sketch, "E1474", {"center": v(797.44, -91.1) * mm, "radius": 1.6 * mm});
            skCircle(sketch, "E1475", {"center": v(837.54, -85.8) * mm, "radius": 1.6 * mm});
            skCircle(sketch, "E1476", {"center": v(788.34, -85.8) * mm, "radius": 1.6 * mm});
            skLineSegment(sketch, "E1477", {"start": v(790.8, -58.1) * mm, "end": v(795.21, -53.7) * mm});
            skLineSegment(sketch, "E1478", {"start": v(830.66, -53.7) * mm, "end": v(835.07, -58.1) * mm});
            skLineSegment(sketch, "E1479", {"start": v(835.07, -58.1) * mm, "end": v(840.04, -58.1) * mm});
            skLineSegment(sketch, "E1480", {"start": v(785.84, -58.1) * mm, "end": v(790.8, -58.1) * mm});
            skLineSegment(sketch, "E1481", {"start": v(785.84, -71.1) * mm, "end": v(785.84, -58.1) * mm});
            skLineSegment(sketch, "E1482", {"start": v(790.84, -71.1) * mm, "end": v(785.84, -71.1) * mm});
            skLineSegment(sketch, "E1483", {"start": v(790.84, -81.1) * mm, "end": v(790.84, -71.1) * mm});
            skLineSegment(sketch, "E1484", {"start": v(785.84, -81.1) * mm, "end": v(790.84, -81.1) * mm});
            skLineSegment(sketch, "E1485", {"start": v(785.84, -103.1) * mm, "end": v(785.84, -81.1) * mm});
            skLineSegment(sketch, "E1486", {"start": v(791.84, -103.1) * mm, "end": v(785.84, -103.1) * mm});
            skLineSegment(sketch, "E1487", {"start": v(791.84, -103.1) * mm, "end": v(791.84, -99.1) * mm});
            skLineSegment(sketch, "E1488", {"start": v(791.84, -99.1) * mm, "end": v(790.74, -99.1) * mm});
            skLineSegment(sketch, "E1489", {"start": v(790.74, -99.1) * mm, "end": v(790.74, -97.1) * mm});
            skLineSegment(sketch, "E1490", {"start": v(790.74, -97.1) * mm, "end": v(791.84, -97.1) * mm});
            skLineSegment(sketch, "E1491", {"start": v(791.84, -97.1) * mm, "end": v(791.84, -95.1) * mm});
            skLineSegment(sketch, "E1492", {"start": v(791.84, -95.1) * mm, "end": v(795.44, -95.1) * mm});
            skLineSegment(sketch, "E1493", {"start": v(795.44, -95.1) * mm, "end": v(795.44, -97.1) * mm});
            skLineSegment(sketch, "E1494", {"start": v(795.44, -97.1) * mm, "end": v(796.54, -97.1) * mm});
            skLineSegment(sketch, "E1495", {"start": v(796.54, -97.1) * mm, "end": v(796.54, -99.1) * mm});
            skLineSegment(sketch, "E1496", {"start": v(796.54, -99.1) * mm, "end": v(795.44, -99.1) * mm});
            skLineSegment(sketch, "E1497", {"start": v(795.44, -99.1) * mm, "end": v(795.44, -103.1) * mm});
            skLineSegment(sketch, "E1498", {"start": v(800.44, -103.1) * mm, "end": v(795.44, -103.1) * mm});
            skLineSegment(sketch, "E1499", {"start": v(800.44, -103.1) * mm, "end": v(800.44, -108.1) * mm});
            skLineSegment(sketch, "E1500", {"start": v(800.44, -108.1) * mm, "end": v(825.44, -108.1) * mm});
            skLineSegment(sketch, "E1501", {"start": v(825.44, -108.1) * mm, "end": v(825.44, -103.1) * mm});
            skLineSegment(sketch, "E1502", {"start": v(830.44, -103.1) * mm, "end": v(825.44, -103.1) * mm});
            skLineSegment(sketch, "E1503", {"start": v(830.44, -99.1) * mm, "end": v(830.44, -103.1) * mm});
            skLineSegment(sketch, "E1504", {"start": v(830.44, -99.1) * mm, "end": v(829.34, -99.1) * mm});
            skLineSegment(sketch, "E1505", {"start": v(829.34, -99.1) * mm, "end": v(829.34, -97.1) * mm});
            skLineSegment(sketch, "E1506", {"start": v(829.34, -97.1) * mm, "end": v(830.44, -97.1) * mm});
            skLineSegment(sketch, "E1507", {"start": v(830.44, -95.1) * mm, "end": v(830.44, -97.1) * mm});
            skLineSegment(sketch, "E1508", {"start": v(834.04, -95.1) * mm, "end": v(830.44, -95.1) * mm});
            skLineSegment(sketch, "E1509", {"start": v(834.04, -97.1) * mm, "end": v(834.04, -95.1) * mm});
            skLineSegment(sketch, "E1510", {"start": v(834.04, -97.1) * mm, "end": v(835.14, -97.1) * mm});
            skLineSegment(sketch, "E1511", {"start": v(835.14, -97.1) * mm, "end": v(835.14, -99.1) * mm});
            skLineSegment(sketch, "E1512", {"start": v(835.14, -99.1) * mm, "end": v(834.04, -99.1) * mm});
            skLineSegment(sketch, "E1513", {"start": v(834.04, -103.1) * mm, "end": v(834.04, -99.1) * mm});
            skLineSegment(sketch, "E1514", {"start": v(840.04, -103.1) * mm, "end": v(834.04, -103.1) * mm});
            skLineSegment(sketch, "E1515", {"start": v(840.04, -81.1) * mm, "end": v(840.04, -103.1) * mm});
            skLineSegment(sketch, "E1516", {"start": v(835.04, -81.1) * mm, "end": v(840.04, -81.1) * mm});
            skLineSegment(sketch, "E1517", {"start": v(835.04, -71.1) * mm, "end": v(835.04, -81.1) * mm});
            skLineSegment(sketch, "E1518", {"start": v(840.04, -71.1) * mm, "end": v(835.04, -71.1) * mm});
            skLineSegment(sketch, "E1519", {"start": v(840.04, -58.1) * mm, "end": v(840.04, -71.1) * mm});
            skLineSegment(sketch, "E1520", {"start": v(-294.93, 104.28) * mm, "end": v(-294.93, 94.42) * mm});
            skArc(sketch, "E1521", {"start": v(-314.73, 114.9) * mm, "mid": v(-313.13, 113.3) * mm, "end": v(-311.53, 114.9) * mm});
            skCircle(sketch, "E1522", {"center": v(-313.13, 107.4) * mm, "radius": 5.3 * mm});
            skArc(sketch, "E1523", {"start": v(-311.53, 99.9) * mm, "mid": v(-313.13, 101.5) * mm, "end": v(-314.73, 99.9) * mm});
            skArc(sketch, "E1524", {"start": v(-323.63, 109) * mm, "mid": v(-325.23, 107.4) * mm, "end": v(-323.63, 105.8) * mm});
            skArc(sketch, "E1525", {"start": v(-302.63, 105.8) * mm, "mid": v(-301.03, 107.4) * mm, "end": v(-302.63, 109) * mm});
            skLineSegment(sketch, "E1526", {"start": v(-305.63, 109) * mm, "end": v(-302.63, 109) * mm});
            skLineSegment(sketch, "E1527", {"start": v(-302.63, 105.8) * mm, "end": v(-305.63, 105.8) * mm});
            skArc(sketch, "E1528", {"start": v(-314.73, 96.9) * mm, "mid": v(-313.13, 95.3) * mm, "end": v(-311.53, 96.9) * mm});
            skLineSegment(sketch, "E1529", {"start": v(-311.53, 99.9) * mm, "end": v(-311.53, 96.9) * mm});
            skLineSegment(sketch, "E1530", {"start": v(-314.73, 96.9) * mm, "end": v(-314.73, 99.9) * mm});
            skArc(sketch, "E1531", {"start": v(-311.53, 117.9) * mm, "mid": v(-313.13, 119.5) * mm, "end": v(-314.73, 117.9) * mm});
            skLineSegment(sketch, "E1532", {"start": v(-314.73, 114.9) * mm, "end": v(-314.73, 117.9) * mm});
            skLineSegment(sketch, "E1533", {"start": v(-311.53, 117.9) * mm, "end": v(-311.53, 114.9) * mm});
            skLineSegment(sketch, "E1534", {"start": v(-320.63, 105.8) * mm, "end": v(-323.63, 105.8) * mm});
            skLineSegment(sketch, "E1535", {"start": v(-323.63, 109) * mm, "end": v(-320.63, 109) * mm});
            skArc(sketch, "E1536", {"start": v(-305.63, 109) * mm, "mid": v(-307.23, 107.4) * mm, "end": v(-305.63, 105.8) * mm});
            skArc(sketch, "E1537", {"start": v(-294.93, 104.28) * mm, "mid": v(-313.13, 122.48) * mm, "end": v(-331.33, 104.28) * mm});
            skLineSegment(sketch, "E1538", {"start": v(-331.33, 94.42) * mm, "end": v(-331.33, 104.28) * mm});
            skLineSegment(sketch, "E1539", {"start": v(-324.83, 94.42) * mm, "end": v(-331.33, 94.42) * mm});
            skLineSegment(sketch, "E1540", {"start": v(-324.83, 94.42) * mm, "end": v(-324.83, 99.42) * mm});
            skLineSegment(sketch, "E1541", {"start": v(-324.83, 99.42) * mm, "end": v(-325.93, 99.42) * mm});
            skLineSegment(sketch, "E1542", {"start": v(-325.93, 99.42) * mm, "end": v(-325.93, 101.42) * mm});
            skLineSegment(sketch, "E1543", {"start": v(-325.93, 101.42) * mm, "end": v(-324.83, 101.42) * mm});
            skLineSegment(sketch, "E1544", {"start": v(-324.83, 101.42) * mm, "end": v(-324.83, 102.42) * mm});
            skLineSegment(sketch, "E1545", {"start": v(-324.83, 102.42) * mm, "end": v(-321.43, 102.42) * mm});
            skLineSegment(sketch, "E1546", {"start": v(-321.43, 102.42) * mm, "end": v(-321.43, 101.42) * mm});
            skLineSegment(sketch, "E1547", {"start": v(-321.43, 101.42) * mm, "end": v(-320.33, 101.42) * mm});
            skLineSegment(sketch, "E1548", {"start": v(-320.33, 101.42) * mm, "end": v(-320.33, 99.42) * mm});
            skLineSegment(sketch, "E1549", {"start": v(-320.33, 99.42) * mm, "end": v(-321.43, 99.42) * mm});
            skLineSegment(sketch, "E1550", {"start": v(-321.43, 99.42) * mm, "end": v(-321.43, 94.42) * mm});
            skLineSegment(sketch, "E1551", {"start": v(-304.83, 94.42) * mm, "end": v(-321.43, 94.42) * mm});
            skLineSegment(sketch, "E1552", {"start": v(-304.83, 94.42) * mm, "end": v(-304.83, 99.42) * mm});
            skLineSegment(sketch, "E1553", {"start": v(-304.83, 99.42) * mm, "end": v(-305.93, 99.42) * mm});
            skLineSegment(sketch, "E1554", {"start": v(-305.93, 99.42) * mm, "end": v(-305.93, 101.42) * mm});
            skLineSegment(sketch, "E1555", {"start": v(-305.93, 101.42) * mm, "end": v(-304.83, 101.42) * mm});
            skLineSegment(sketch, "E1556", {"start": v(-304.83, 101.42) * mm, "end": v(-304.83, 102.42) * mm});
            skLineSegment(sketch, "E1557", {"start": v(-304.83, 102.42) * mm, "end": v(-301.43, 102.42) * mm});
            skLineSegment(sketch, "E1558", {"start": v(-301.43, 102.42) * mm, "end": v(-301.43, 101.42) * mm});
            skLineSegment(sketch, "E1559", {"start": v(-301.43, 101.42) * mm, "end": v(-300.33, 101.42) * mm});
            skLineSegment(sketch, "E1560", {"start": v(-300.33, 101.42) * mm, "end": v(-300.33, 99.42) * mm});
            skLineSegment(sketch, "E1561", {"start": v(-300.33, 99.42) * mm, "end": v(-301.43, 99.42) * mm});
            skLineSegment(sketch, "E1562", {"start": v(-301.43, 99.42) * mm, "end": v(-301.43, 94.42) * mm});
            skLineSegment(sketch, "E1563", {"start": v(-294.93, 94.42) * mm, "end": v(-301.43, 94.42) * mm});
            skArc(sketch, "E1564", {"start": v(-320.63, 105.8) * mm, "mid": v(-319.03, 107.4) * mm, "end": v(-320.63, 109) * mm});
            skArc(sketch, "E1565", {"start": v(276.37, 86.33) * mm, "mid": v(271.53, 101.25) * mm, "end": v(257.2, 107.62) * mm});
            skArc(sketch, "E1566", {"start": v(204.28, 99.4) * mm, "mid": v(204.83, 97.72) * mm, "end": v(206.44, 97) * mm});
            skArc(sketch, "E1567", {"start": v(247.77, 28.5) * mm, "mid": v(264.5, 34.91) * mm, "end": v(272.63, 50.87) * mm});
            skArc(sketch, "E1568", {"start": v(265.36, 85.84) * mm, "mid": v(262.82, 93.66) * mm, "end": v(255.32, 97) * mm});
            skArc(sketch, "E1569", {"start": v(199.88, 39.12) * mm, "mid": v(198.42, 38.57) * mm, "end": v(197.72, 37.18) * mm});
            skArc(sketch, "E1570", {"start": v(248.8, 39.12) * mm, "mid": v(257.44, 42.44) * mm, "end": v(261.65, 50.7) * mm});
            skCircle(sketch, "E1571", {"center": v(159.75, 226.15) * mm, "radius": 1.6 * mm});
            skCircle(sketch, "E1572", {"center": v(179.75, 226.15) * mm, "radius": 1.6 * mm});
            skCircle(sketch, "E1573", {"center": v(403.25, -171.86) * mm, "radius": 1.6 * mm});
            skCircle(sketch, "E1574", {"center": v(297, -171.86) * mm, "radius": 1.6 * mm});
            skCircle(sketch, "E1575", {"center": v(190.75, -171.86) * mm, "radius": 1.6 * mm});
            skCircle(sketch, "E1576", {"center": v(404.25, -198.3) * mm, "radius": 22 * mm});
            skArc(sketch, "E1577", {"start": v(234.12, 175.46) * mm, "mid": v(219.12, 160.46) * mm, "end": v(234.12, 145.46) * mm});
            skArc(sketch, "E1578", {"start": v(294.12, 145.46) * mm, "mid": v(309.12, 160.46) * mm, "end": v(294.12, 175.46) * mm});
            skEllipticalArc(sketch, "E1579", {});
            skEllipticalArc(sketch, "E1580", {});
            skEllipticalArc(sketch, "E1581", {});
            skEllipticalArc(sketch, "E1582", {});
            skEllipticalArc(sketch, "E1583", {});
            skArc(sketch, "E1584", {"start": v(383.2, 8.2) * mm, "mid": v(384.18, 8.89) * mm, "end": v(384.94, 9.8) * mm});
            skEllipticalArc(sketch, "E1585", {});
            skEllipticalArc(sketch, "E1586", {});
            skEllipticalArc(sketch, "E1587", {});
            skArc(sketch, "E1588", {"start": v(341.58, 13.1) * mm, "mid": v(341.89, 13.74) * mm, "end": v(342.03, 14.43) * mm});
            skArc(sketch, "E1589", {"start": v(340.58, 12.21) * mm, "mid": v(341.13, 12.6) * mm, "end": v(341.57, 13.11) * mm});
            skArc(sketch, "E1590", {"start": v(341, 10.45) * mm, "mid": v(340.83, 10.74) * mm, "end": v(340.65, 11.02) * mm});
            skArc(sketch, "E1591", {"start": v(337.2, 11.3) * mm, "mid": v(336.89, 11.47) * mm, "end": v(336.53, 11.51) * mm});
            skEllipticalArc(sketch, "E1592", {});
            skEllipticalArc(sketch, "E1593", {});
            skArc(sketch, "E1594", {"start": v(327.35, 14.84) * mm, "mid": v(326.98, 14.98) * mm, "end": v(326.6, 15.01) * mm});
            skEllipticalArc(sketch, "E1595", {});
            skEllipticalArc(sketch, "E1596", {});
            skEllipticalArc(sketch, "E1597", {});
            skEllipticalArc(sketch, "E1598", {});
            skEllipticalArc(sketch, "E1599", {});
            skEllipticalArc(sketch, "E1600", {});
            skArc(sketch, "E1601", {"start": v(300.76, 9.17) * mm, "mid": v(301.16, 9.9) * mm, "end": v(301.36, 10.7) * mm});
            skEllipticalArc(sketch, "E1602", {});
            skArc(sketch, "E1603", {"start": v(294.26, 8.78) * mm, "mid": v(294.76, 8.28) * mm, "end": v(295.37, 7.92) * mm});
            skEllipticalArc(sketch, "E1604", {});
            skArc(sketch, "E1605", {"start": v(297.42, 9.19) * mm, "mid": v(297.9, 9.28) * mm, "end": v(298.31, 9.56) * mm});
            skEllipticalArc(sketch, "E1606", {});
            skEllipticalArc(sketch, "E1607", {});
            skArc(sketch, "E1608", {"start": v(297.16, 13.59) * mm, "mid": v(297.32, 13.57) * mm, "end": v(297.49, 13.55) * mm});
            skEllipticalArc(sketch, "E1609", {});
            skArc(sketch, "E1610", {"start": v(298.36, 13.88) * mm, "mid": v(298.64, 14.22) * mm, "end": v(298.78, 14.63) * mm});
            skEllipticalArc(sketch, "E1611", {});
            skEllipticalArc(sketch, "E1612", {});
            skEllipticalArc(sketch, "E1613", {});
            skEllipticalArc(sketch, "E1614", {});
            skEllipticalArc(sketch, "E1615", {});
            skArc(sketch, "E1616", {"start": v(311.4, 8.76) * mm, "mid": v(312, 9.4) * mm, "end": v(312.47, 10.13) * mm});
            skEllipticalArc(sketch, "E1617", {});
            skEllipticalArc(sketch, "E1618", {});
            skArc(sketch, "E1619", {"start": v(391.92, 11.3) * mm, "mid": v(391.6, 11.47) * mm, "end": v(391.25, 11.51) * mm});
            skArc(sketch, "E1620", {"start": v(396.48, 15.92) * mm, "mid": v(396.04, 16.44) * mm, "end": v(395.45, 16.76) * mm});
            skArc(sketch, "E1621", {"start": v(396.3, 13.1) * mm, "mid": v(396.6, 13.74) * mm, "end": v(396.75, 14.43) * mm});
            skArc(sketch, "E1622", {"start": v(395.3, 12.21) * mm, "mid": v(395.84, 12.6) * mm, "end": v(396.29, 13.11) * mm});
            skArc(sketch, "E1623", {"start": v(209.44, 64.71) * mm, "mid": v(209.99, 63.03) * mm, "end": v(211.6, 62.31) * mm});
            skArc(sketch, "E1624", {"start": v(212.24, 72.66) * mm, "mid": v(210.8, 72.1) * mm, "end": v(210.09, 70.72) * mm});
            skCircle(sketch, "E1625", {"center": v(297, -225.9) * mm, "radius": 1.6 * mm});
            skCircle(sketch, "E1626", {"center": v(190.75, -225.9) * mm, "radius": 1.6 * mm});
            skCircle(sketch, "E1627", {"center": v(383.25, -225.9) * mm, "radius": 1.6 * mm});
            skCircle(sketch, "E1628", {"center": v(441, 201.4) * mm, "radius": 1.6 * mm});
            skLineSegment(sketch, "E1629", {"start": v(439.87, 118.66) * mm, "end": v(439.87, 114.66) * mm});
            skLineSegment(sketch, "E1630", {"start": v(441.87, 118.66) * mm, "end": v(439.87, 118.66) * mm});
            skLineSegment(sketch, "E1631", {"start": v(441.87, 114.66) * mm, "end": v(441.87, 118.66) * mm});
            skLineSegment(sketch, "E1632", {"start": v(439.87, 114.66) * mm, "end": v(441.87, 114.66) * mm});
            skLineSegment(sketch, "E1633", {"start": v(427.87, 118.66) * mm, "end": v(427.87, 114.66) * mm});
            skLineSegment(sketch, "E1634", {"start": v(429.87, 118.66) * mm, "end": v(427.87, 118.66) * mm});
            skLineSegment(sketch, "E1635", {"start": v(429.87, 114.66) * mm, "end": v(429.87, 118.66) * mm});
            skLineSegment(sketch, "E1636", {"start": v(427.87, 114.66) * mm, "end": v(429.87, 114.66) * mm});
            skLineSegment(sketch, "E1637", {"start": v(439.87, 2.64) * mm, "end": v(439.87, -1.36) * mm});
            skLineSegment(sketch, "E1638", {"start": v(441.87, 2.64) * mm, "end": v(439.87, 2.64) * mm});
            skLineSegment(sketch, "E1639", {"start": v(441.87, -1.36) * mm, "end": v(441.87, 2.64) * mm});
            skLineSegment(sketch, "E1640", {"start": v(439.87, -1.36) * mm, "end": v(441.87, -1.36) * mm});
            skLineSegment(sketch, "E1641", {"start": v(427.87, 2.64) * mm, "end": v(427.87, -1.36) * mm});
            skLineSegment(sketch, "E1642", {"start": v(429.87, 2.64) * mm, "end": v(427.87, 2.64) * mm});
            skLineSegment(sketch, "E1643", {"start": v(429.87, -1.36) * mm, "end": v(429.87, 2.64) * mm});
            skLineSegment(sketch, "E1644", {"start": v(427.87, -1.36) * mm, "end": v(429.87, -1.36) * mm});
            skLineSegment(sketch, "E1645", {"start": v(439.87, -107.44) * mm, "end": v(439.87, -111.44) * mm});
            skLineSegment(sketch, "E1646", {"start": v(441.87, -107.44) * mm, "end": v(439.87, -107.44) * mm});
            skLineSegment(sketch, "E1647", {"start": v(441.87, -111.44) * mm, "end": v(441.87, -107.44) * mm});
            skLineSegment(sketch, "E1648", {"start": v(439.87, -111.44) * mm, "end": v(441.87, -111.44) * mm});
            skLineSegment(sketch, "E1649", {"start": v(427.87, -107.44) * mm, "end": v(427.87, -111.44) * mm});
            skLineSegment(sketch, "E1650", {"start": v(429.87, -107.44) * mm, "end": v(427.87, -107.44) * mm});
            skLineSegment(sketch, "E1651", {"start": v(429.87, -111.44) * mm, "end": v(429.87, -107.44) * mm});
            skLineSegment(sketch, "E1652", {"start": v(427.87, -111.44) * mm, "end": v(429.87, -111.44) * mm});
            skLineSegment(sketch, "E1653", {"start": v(447, -235.9) * mm, "end": v(407, -235.9) * mm});
            skLineSegment(sketch, "E1654", {"start": v(447, -235.9) * mm, "end": v(447, -173.66) * mm});
            skLineSegment(sketch, "E1655", {"start": v(442, -173.66) * mm, "end": v(447, -173.66) * mm});
            skLineSegment(sketch, "E1656", {"start": v(442, -174.76) * mm, "end": v(442, -173.66) * mm});
            skLineSegment(sketch, "E1657", {"start": v(440, -174.76) * mm, "end": v(442, -174.76) * mm});
            skLineSegment(sketch, "E1658", {"start": v(440, -173.66) * mm, "end": v(440, -174.76) * mm});
            skLineSegment(sketch, "E1659", {"start": v(439, -173.66) * mm, "end": v(440, -173.66) * mm});
            skLineSegment(sketch, "E1660", {"start": v(439, -170.06) * mm, "end": v(439, -173.66) * mm});
            skLineSegment(sketch, "E1661", {"start": v(440, -170.06) * mm, "end": v(439, -170.06) * mm});
            skLineSegment(sketch, "E1662", {"start": v(440, -168.96) * mm, "end": v(440, -170.06) * mm});
            skLineSegment(sketch, "E1663", {"start": v(442, -168.96) * mm, "end": v(440, -168.96) * mm});
            skLineSegment(sketch, "E1664", {"start": v(442, -170.06) * mm, "end": v(442, -168.96) * mm});
            skLineSegment(sketch, "E1665", {"start": v(447, -170.06) * mm, "end": v(442, -170.06) * mm});
            skLineSegment(sketch, "E1666", {"start": v(447, -170.06) * mm, "end": v(447, -58.59) * mm});
            skLineSegment(sketch, "E1667", {"start": v(442, -58.59) * mm, "end": v(447, -58.59) * mm});
            skLineSegment(sketch, "E1668", {"start": v(442, -59.69) * mm, "end": v(442, -58.59) * mm});
            skLineSegment(sketch, "E1669", {"start": v(440, -59.69) * mm, "end": v(442, -59.69) * mm});
            skLineSegment(sketch, "E1670", {"start": v(440, -58.59) * mm, "end": v(440, -59.69) * mm});
            skLineSegment(sketch, "E1671", {"start": v(439, -58.59) * mm, "end": v(440, -58.59) * mm});
            skLineSegment(sketch, "E1672", {"start": v(439, -54.99) * mm, "end": v(439, -58.59) * mm});
            skLineSegment(sketch, "E1673", {"start": v(440, -54.99) * mm, "end": v(439, -54.99) * mm});
            skLineSegment(sketch, "E1674", {"start": v(440, -53.89) * mm, "end": v(440, -54.99) * mm});
            skLineSegment(sketch, "E1675", {"start": v(442, -53.89) * mm, "end": v(440, -53.89) * mm});
            skLineSegment(sketch, "E1676", {"start": v(442, -54.99) * mm, "end": v(442, -53.89) * mm});
            skLineSegment(sketch, "E1677", {"start": v(447, -54.99) * mm, "end": v(442, -54.99) * mm});
            skLineSegment(sketch, "E1678", {"start": v(447, 56.48) * mm, "end": v(447, -54.99) * mm});
            skLineSegment(sketch, "E1679", {"start": v(442, 56.48) * mm, "end": v(447, 56.48) * mm});
            skLineSegment(sketch, "E1680", {"start": v(442, 55.38) * mm, "end": v(442, 56.48) * mm});
            skLineSegment(sketch, "E1681", {"start": v(440, 55.38) * mm, "end": v(442, 55.38) * mm});
            skLineSegment(sketch, "E1682", {"start": v(440, 56.48) * mm, "end": v(440, 55.38) * mm});
            skLineSegment(sketch, "E1683", {"start": v(439, 56.48) * mm, "end": v(440, 56.48) * mm});
            skLineSegment(sketch, "E1684", {"start": v(439, 60.08) * mm, "end": v(439, 56.48) * mm});
            skLineSegment(sketch, "E1685", {"start": v(440, 60.08) * mm, "end": v(439, 60.08) * mm});
            skLineSegment(sketch, "E1686", {"start": v(440, 61.18) * mm, "end": v(440, 60.08) * mm});
            skLineSegment(sketch, "E1687", {"start": v(442, 61.18) * mm, "end": v(440, 61.18) * mm});
            skLineSegment(sketch, "E1688", {"start": v(442, 60.08) * mm, "end": v(442, 61.18) * mm});
            skLineSegment(sketch, "E1689", {"start": v(447, 60.08) * mm, "end": v(442, 60.08) * mm});
            skLineSegment(sketch, "E1690", {"start": v(447, 171.55) * mm, "end": v(447, 60.08) * mm});
            skLineSegment(sketch, "E1691", {"start": v(442, 171.55) * mm, "end": v(447, 171.55) * mm});
            skLineSegment(sketch, "E1692", {"start": v(442, 170.45) * mm, "end": v(442, 171.55) * mm});
            skLineSegment(sketch, "E1693", {"start": v(440, 170.45) * mm, "end": v(442, 170.45) * mm});
            skLineSegment(sketch, "E1694", {"start": v(440, 171.55) * mm, "end": v(440, 170.45) * mm});
            skLineSegment(sketch, "E1695", {"start": v(439, 171.55) * mm, "end": v(440, 171.55) * mm});
            skLineSegment(sketch, "E1696", {"start": v(439, 175.15) * mm, "end": v(439, 171.55) * mm});
            skLineSegment(sketch, "E1697", {"start": v(440, 175.15) * mm, "end": v(439, 175.15) * mm});
            skLineSegment(sketch, "E1698", {"start": v(440, 176.25) * mm, "end": v(440, 175.15) * mm});
            skLineSegment(sketch, "E1699", {"start": v(442, 176.25) * mm, "end": v(440, 176.25) * mm});
            skLineSegment(sketch, "E1700", {"start": v(442, 175.15) * mm, "end": v(442, 176.25) * mm});
            skLineSegment(sketch, "E1701", {"start": v(447, 175.15) * mm, "end": v(442, 175.15) * mm});
            skLineSegment(sketch, "E1702", {"start": v(447, 230.9) * mm, "end": v(447, 175.15) * mm});
            skLineSegment(sketch, "E1703", {"start": v(447, 230.9) * mm, "end": v(405.1, 230.9) * mm});
            skLineSegment(sketch, "E1704", {"start": v(405.1, 225.9) * mm, "end": v(405.1, 230.9) * mm});
            skLineSegment(sketch, "E1705", {"start": v(406.2, 225.9) * mm, "end": v(405.1, 225.9) * mm});
            skLineSegment(sketch, "E1706", {"start": v(406.2, 223.9) * mm, "end": v(406.2, 225.9) * mm});
            skLineSegment(sketch, "E1707", {"start": v(405.1, 223.9) * mm, "end": v(406.2, 223.9) * mm});
            skLineSegment(sketch, "E1708", {"start": v(405.1, 222.9) * mm, "end": v(405.1, 223.9) * mm});
            skLineSegment(sketch, "E1709", {"start": v(401.5, 222.9) * mm, "end": v(405.1, 222.9) * mm});
            skLineSegment(sketch, "E1710", {"start": v(401.5, 223.9) * mm, "end": v(401.5, 222.9) * mm});
            skLineSegment(sketch, "E1711", {"start": v(400.4, 223.9) * mm, "end": v(401.5, 223.9) * mm});
            skLineSegment(sketch, "E1712", {"start": v(400.4, 225.9) * mm, "end": v(400.4, 223.9) * mm});
            skLineSegment(sketch, "E1713", {"start": v(401.5, 225.9) * mm, "end": v(400.4, 225.9) * mm});
            skLineSegment(sketch, "E1714", {"start": v(401.5, 230.9) * mm, "end": v(401.5, 225.9) * mm});
            skLineSegment(sketch, "E1715", {"start": v(401.5, 230.9) * mm, "end": v(298.8, 230.9) * mm});
            skLineSegment(sketch, "E1716", {"start": v(298.8, 225.9) * mm, "end": v(298.8, 230.9) * mm});
            skLineSegment(sketch, "E1717", {"start": v(299.9, 225.9) * mm, "end": v(298.8, 225.9) * mm});
            skLineSegment(sketch, "E1718", {"start": v(299.9, 223.9) * mm, "end": v(299.9, 225.9) * mm});
            skLineSegment(sketch, "E1719", {"start": v(298.8, 223.9) * mm, "end": v(299.9, 223.9) * mm});
            skLineSegment(sketch, "E1720", {"start": v(298.8, 222.9) * mm, "end": v(298.8, 223.9) * mm});
            skLineSegment(sketch, "E1721", {"start": v(295.2, 222.9) * mm, "end": v(298.8, 222.9) * mm});
            skLineSegment(sketch, "E1722", {"start": v(295.2, 223.9) * mm, "end": v(295.2, 222.9) * mm});
            skLineSegment(sketch, "E1723", {"start": v(294.1, 223.9) * mm, "end": v(295.2, 223.9) * mm});
            skLineSegment(sketch, "E1724", {"start": v(294.1, 225.9) * mm, "end": v(294.1, 223.9) * mm});
            skLineSegment(sketch, "E1725", {"start": v(295.2, 225.9) * mm, "end": v(294.1, 225.9) * mm});
            skLineSegment(sketch, "E1726", {"start": v(295.2, 230.9) * mm, "end": v(295.2, 225.9) * mm});
            skLineSegment(sketch, "E1727", {"start": v(295.2, 230.9) * mm, "end": v(192.5, 230.9) * mm});
            skLineSegment(sketch, "E1728", {"start": v(192.5, 225.9) * mm, "end": v(192.5, 230.9) * mm});
            skLineSegment(sketch, "E1729", {"start": v(193.6, 225.9) * mm, "end": v(192.5, 225.9) * mm});
            skLineSegment(sketch, "E1730", {"start": v(193.6, 223.9) * mm, "end": v(193.6, 225.9) * mm});
            skLineSegment(sketch, "E1731", {"start": v(192.5, 223.9) * mm, "end": v(193.6, 223.9) * mm});
            skLineSegment(sketch, "E1732", {"start": v(192.5, 222.9) * mm, "end": v(192.5, 223.9) * mm});
            skLineSegment(sketch, "E1733", {"start": v(188.9, 222.9) * mm, "end": v(192.5, 222.9) * mm});
            skLineSegment(sketch, "E1734", {"start": v(188.9, 223.9) * mm, "end": v(188.9, 222.9) * mm});
            skLineSegment(sketch, "E1735", {"start": v(187.8, 223.9) * mm, "end": v(188.9, 223.9) * mm});
            skLineSegment(sketch, "E1736", {"start": v(187.8, 225.9) * mm, "end": v(187.8, 223.9) * mm});
            skLineSegment(sketch, "E1737", {"start": v(188.9, 225.9) * mm, "end": v(187.8, 225.9) * mm});
            skLineSegment(sketch, "E1738", {"start": v(188.9, 230.9) * mm, "end": v(188.9, 225.9) * mm});
            skLineSegment(sketch, "E1739", {"start": v(188.9, 230.9) * mm, "end": v(147, 230.9) * mm});
            skLineSegment(sketch, "E1740", {"start": v(147, 230.9) * mm, "end": v(147, 175.15) * mm});
            skLineSegment(sketch, "E1741", {"start": v(147, 175.15) * mm, "end": v(152, 175.15) * mm});
            skLineSegment(sketch, "E1742", {"start": v(152, 176.25) * mm, "end": v(152, 175.15) * mm});
            skLineSegment(sketch, "E1743", {"start": v(154, 176.25) * mm, "end": v(152, 176.25) * mm});
            skLineSegment(sketch, "E1744", {"start": v(154, 175.15) * mm, "end": v(154, 176.25) * mm});
            skLineSegment(sketch, "E1745", {"start": v(154, 175.15) * mm, "end": v(155, 175.15) * mm});
            skLineSegment(sketch, "E1746", {"start": v(155, 175.15) * mm, "end": v(155, 171.55) * mm});
            skLineSegment(sketch, "E1747", {"start": v(155, 171.55) * mm, "end": v(154, 171.55) * mm});
            skLineSegment(sketch, "E1748", {"start": v(154, 170.45) * mm, "end": v(154, 171.55) * mm});
            skLineSegment(sketch, "E1749", {"start": v(152, 170.45) * mm, "end": v(154, 170.45) * mm});
            skLineSegment(sketch, "E1750", {"start": v(152, 171.55) * mm, "end": v(152, 170.45) * mm});
            skLineSegment(sketch, "E1751", {"start": v(152, 171.55) * mm, "end": v(147, 171.55) * mm});
            skLineSegment(sketch, "E1752", {"start": v(147, 171.55) * mm, "end": v(147, 60.08) * mm});
            skLineSegment(sketch, "E1753", {"start": v(147, 60.08) * mm, "end": v(152, 60.08) * mm});
            skLineSegment(sketch, "E1754", {"start": v(152, 61.18) * mm, "end": v(152, 60.08) * mm});
            skLineSegment(sketch, "E1755", {"start": v(154, 61.18) * mm, "end": v(152, 61.18) * mm});
            skLineSegment(sketch, "E1756", {"start": v(154, 60.08) * mm, "end": v(154, 61.18) * mm});
            skLineSegment(sketch, "E1757", {"start": v(154, 60.08) * mm, "end": v(155, 60.08) * mm});
            skLineSegment(sketch, "E1758", {"start": v(155, 60.08) * mm, "end": v(155, 56.48) * mm});
            skLineSegment(sketch, "E1759", {"start": v(155, 56.48) * mm, "end": v(154, 56.48) * mm});
            skLineSegment(sketch, "E1760", {"start": v(154, 55.38) * mm, "end": v(154, 56.48) * mm});
            skLineSegment(sketch, "E1761", {"start": v(152, 55.38) * mm, "end": v(154, 55.38) * mm});
            skLineSegment(sketch, "E1762", {"start": v(152, 56.48) * mm, "end": v(152, 55.38) * mm});
            skLineSegment(sketch, "E1763", {"start": v(152, 56.48) * mm, "end": v(147, 56.48) * mm});
            skLineSegment(sketch, "E1764", {"start": v(147, 56.48) * mm, "end": v(147, -54.99) * mm});
            skLineSegment(sketch, "E1765", {"start": v(152, -54.99) * mm, "end": v(147, -54.99) * mm});
            skLineSegment(sketch, "E1766", {"start": v(152, -53.89) * mm, "end": v(152, -54.99) * mm});
            skLineSegment(sketch, "E1767", {"start": v(154, -53.89) * mm, "end": v(152, -53.89) * mm});
            skLineSegment(sketch, "E1768", {"start": v(154, -54.99) * mm, "end": v(154, -53.89) * mm});
            skLineSegment(sketch, "E1769", {"start": v(155, -54.99) * mm, "end": v(154, -54.99) * mm});
            skLineSegment(sketch, "E1770", {"start": v(155, -58.59) * mm, "end": v(155, -54.99) * mm});
            skLineSegment(sketch, "E1771", {"start": v(154, -58.59) * mm, "end": v(155, -58.59) * mm});
            skLineSegment(sketch, "E1772", {"start": v(154, -59.69) * mm, "end": v(154, -58.59) * mm});
            skLineSegment(sketch, "E1773", {"start": v(152, -59.69) * mm, "end": v(154, -59.69) * mm});
            skLineSegment(sketch, "E1774", {"start": v(152, -58.59) * mm, "end": v(152, -59.69) * mm});
            skLineSegment(sketch, "E1775", {"start": v(147, -58.59) * mm, "end": v(152, -58.59) * mm});
            skLineSegment(sketch, "E1776", {"start": v(147, -58.59) * mm, "end": v(147, -170.06) * mm});
            skLineSegment(sketch, "E1777", {"start": v(147, -170.06) * mm, "end": v(152, -170.06) * mm});
            skLineSegment(sketch, "E1778", {"start": v(152, -168.96) * mm, "end": v(152, -170.06) * mm});
            skLineSegment(sketch, "E1779", {"start": v(154, -168.96) * mm, "end": v(152, -168.96) * mm});
            skLineSegment(sketch, "E1780", {"start": v(154, -170.06) * mm, "end": v(154, -168.96) * mm});
            skLineSegment(sketch, "E1781", {"start": v(154, -170.06) * mm, "end": v(155, -170.06) * mm});
            skLineSegment(sketch, "E1782", {"start": v(155, -170.06) * mm, "end": v(155, -173.66) * mm});
            skLineSegment(sketch, "E1783", {"start": v(155, -173.66) * mm, "end": v(154, -173.66) * mm});
            skLineSegment(sketch, "E1784", {"start": v(154, -174.76) * mm, "end": v(154, -173.66) * mm});
            skLineSegment(sketch, "E1785", {"start": v(152, -174.76) * mm, "end": v(154, -174.76) * mm});
            skLineSegment(sketch, "E1786", {"start": v(152, -173.66) * mm, "end": v(152, -174.76) * mm});
            skLineSegment(sketch, "E1787", {"start": v(152, -173.66) * mm, "end": v(147, -173.66) * mm});
            skLineSegment(sketch, "E1788", {"start": v(147, -173.66) * mm, "end": v(147, -235.9) * mm});
            skLineSegment(sketch, "E1789", {"start": v(187, -235.9) * mm, "end": v(147, -235.9) * mm});
            skArc(sketch, "E1790", {"start": v(407, -235.9) * mm, "mid": v(297, -228.39) * mm, "end": v(187, -235.9) * mm});
            skLineSegment(sketch, "E1791", {"start": v(327, -174.4) * mm, "end": v(327, -169.4) * mm});
            skLineSegment(sketch, "E1792", {"start": v(327, -169.4) * mm, "end": v(375, -169.4) * mm});
            skLineSegment(sketch, "E1793", {"start": v(375, -169.4) * mm, "end": v(375, -174.4) * mm});
            skLineSegment(sketch, "E1794", {"start": v(375, -174.4) * mm, "end": v(327, -174.4) * mm});
            skLineSegment(sketch, "E1795", {"start": v(236.25, 62.32) * mm, "end": v(211.6, 62.31) * mm});
            skLineSegment(sketch, "E1796", {"start": v(209.44, 64.71) * mm, "end": v(210.09, 70.72) * mm});
            skLineSegment(sketch, "E1797", {"start": v(212.24, 72.66) * mm, "end": v(237.35, 72.66) * mm});
            skLineSegment(sketch, "E1798", {"start": v(237.35, 72.66) * mm, "end": v(236.25, 62.32) * mm});
            skLineSegment(sketch, "E1799", {"start": v(199.88, 39.12) * mm, "end": v(248.8, 39.12) * mm});
            skLineSegment(sketch, "E1800", {"start": v(261.65, 50.7) * mm, "end": v(262, 54.04) * mm});
            skLineSegment(sketch, "E1801", {"start": v(262, 54.04) * mm, "end": v(265.36, 85.84) * mm});
            skLineSegment(sketch, "E1802", {"start": v(255.32, 97) * mm, "end": v(206.44, 97) * mm});
            skLineSegment(sketch, "E1803", {"start": v(204.28, 99.4) * mm, "end": v(205.15, 107.62) * mm});
            skLineSegment(sketch, "E1804", {"start": v(205.15, 107.62) * mm, "end": v(257.2, 107.62) * mm});
            skLineSegment(sketch, "E1805", {"start": v(276.37, 86.33) * mm, "end": v(274.44, 68.06) * mm});
            skLineSegment(sketch, "E1806", {"start": v(274.44, 68.06) * mm, "end": v(272.63, 50.87) * mm});
            skLineSegment(sketch, "E1807", {"start": v(247.77, 28.5) * mm, "end": v(196.8, 28.5) * mm});
            skLineSegment(sketch, "E1808", {"start": v(196.8, 28.5) * mm, "end": v(197.72, 37.18) * mm});
            skLineSegment(sketch, "E1809", {"start": v(393.59, 7.78) * mm, "end": v(392.36, 10.6) * mm});
            skEllipticalArc(sketch, "E1810", {});
            skLineSegment(sketch, "E1811", {"start": v(391.25, 11.52) * mm, "end": v(391, 11.52) * mm});
            skLineSegment(sketch, "E1812", {"start": v(391, 11.52) * mm, "end": v(390.6, 7.78) * mm});
            skLineSegment(sketch, "E1813", {"start": v(390.6, 7.78) * mm, "end": v(387.74, 7.78) * mm});
            skLineSegment(sketch, "E1814", {"start": v(387.74, 7.78) * mm, "end": v(388.71, 17) * mm});
            skLineSegment(sketch, "E1815", {"start": v(388.71, 17) * mm, "end": v(393.45, 17) * mm});
            skEllipticalArc(sketch, "E1816", {});
            skFitSpline(sketch, "E1817", {"points": [v(396.48, 15.93) * mm, v(396.72, 15.52) * mm, v(396.81, 15.02) * mm, v(396.75, 14.43) * mm]});
            skEllipticalArc(sketch, "E1818", {});
            skEllipticalArc(sketch, "E1819", {});
            skFitSpline(sketch, "E1820", {"points": [v(394.96, 11.5) * mm, v(395.06, 11.43) * mm, v(395.2, 11.27) * mm, v(395.37, 11.02) * mm]});
            skEllipticalArc(sketch, "E1821", {});
            skLineSegment(sketch, "E1822", {"start": v(395.7, 10.45) * mm, "end": v(396.8, 7.78) * mm});
            skLineSegment(sketch, "E1823", {"start": v(396.8, 7.78) * mm, "end": v(393.59, 7.78) * mm});
            skFitSpline(sketch, "E1824", {"points": [v(377.4, 67.94) * mm, v(378.59, 67.94) * mm, v(379.43, 67) * mm, v(379.3, 65.65) * mm]});
            skLineSegment(sketch, "E1825", {"start": v(379.3, 65.65) * mm, "end": v(379.24, 65.18) * mm});
            skFitSpline(sketch, "E1826", {"points": [v(379.24, 65.18) * mm, v(381.94, 67.62) * mm, v(383.3, 68.5) * mm, v(387.94, 68.5) * mm]});
            skFitSpline(sketch, "E1827", {"points": [v(387.94, 68.5) * mm, v(389.28, 68.5) * mm, v(390.12, 67.54) * mm, v(390, 66.36) * mm]});
            skLineSegment(sketch, "E1828", {"start": v(390, 66.36) * mm, "end": v(389.76, 64.08) * mm});
            skFitSpline(sketch, "E1829", {"points": [v(389.76, 64.08) * mm, v(389.63, 62.9) * mm, v(388.58, 61.87) * mm, v(387.24, 61.87) * mm]});
            skFitSpline(sketch, "E1830", {"points": [v(387.24, 61.87) * mm, v(380.15, 61.87) * mm, v(378.53, 58.4) * mm, v(378.2, 55.26) * mm]});
            skLineSegment(sketch, "E1831", {"start": v(378.2, 55.26) * mm, "end": v(375.62, 30.83) * mm});
            skFitSpline(sketch, "E1832", {"points": [v(375.62, 30.83) * mm, v(375.47, 29.5) * mm, v(374.43, 28.55) * mm, v(373.25, 28.55) * mm]});
            skLineSegment(sketch, "E1833", {"start": v(373.25, 28.55) * mm, "end": v(370.33, 28.55) * mm});
            skFitSpline(sketch, "E1834", {"points": [v(370.33, 28.55) * mm, v(369.15, 28.55) * mm, v(368.3, 29.5) * mm, v(368.45, 30.83) * mm]});
            skLineSegment(sketch, "E1835", {"start": v(368.45, 30.83) * mm, "end": v(372.12, 65.65) * mm});
            skFitSpline(sketch, "E1836", {"points": [v(372.12, 65.65) * mm, v(372.26, 67) * mm, v(373.3, 67.94) * mm, v(374.49, 67.94) * mm]});
            skLineSegment(sketch, "E1837", {"start": v(374.49, 67.94) * mm, "end": v(377.4, 67.94) * mm});
            skLineSegment(sketch, "E1838", {"start": v(357.97, 9.3) * mm, "end": v(357.36, 7.78) * mm});
            skLineSegment(sketch, "E1839", {"start": v(357.36, 7.78) * mm, "end": v(354.45, 7.78) * mm});
            skLineSegment(sketch, "E1840", {"start": v(354.45, 7.78) * mm, "end": v(358.88, 17) * mm});
            skLineSegment(sketch, "E1841", {"start": v(358.88, 17) * mm, "end": v(361.99, 17) * mm});
            skLineSegment(sketch, "E1842", {"start": v(361.99, 17) * mm, "end": v(364.48, 7.78) * mm});
            skLineSegment(sketch, "E1843", {"start": v(364.48, 7.78) * mm, "end": v(361.5, 7.78) * mm});
            skLineSegment(sketch, "E1844", {"start": v(361.5, 7.78) * mm, "end": v(361.2, 9.3) * mm});
            skLineSegment(sketch, "E1845", {"start": v(361.2, 9.3) * mm, "end": v(357.97, 9.3) * mm});
            skLineSegment(sketch, "E1846", {"start": v(352.52, 9.87) * mm, "end": v(352.3, 7.78) * mm});
            skLineSegment(sketch, "E1847", {"start": v(352.3, 7.78) * mm, "end": v(344.53, 7.78) * mm});
            skLineSegment(sketch, "E1848", {"start": v(344.53, 7.78) * mm, "end": v(345.5, 17) * mm});
            skLineSegment(sketch, "E1849", {"start": v(345.5, 17) * mm, "end": v(353.13, 17) * mm});
            skLineSegment(sketch, "E1850", {"start": v(353.13, 17) * mm, "end": v(352.92, 15.03) * mm});
            skLineSegment(sketch, "E1851", {"start": v(352.92, 15.03) * mm, "end": v(348.15, 15.03) * mm});
            skLineSegment(sketch, "E1852", {"start": v(348.15, 15.03) * mm, "end": v(348, 13.56) * mm});
            skLineSegment(sketch, "E1853", {"start": v(348, 13.56) * mm, "end": v(352.42, 13.56) * mm});
            skLineSegment(sketch, "E1854", {"start": v(352.42, 13.56) * mm, "end": v(352.23, 11.68) * mm});
            skLineSegment(sketch, "E1855", {"start": v(352.23, 11.68) * mm, "end": v(347.8, 11.68) * mm});
            skLineSegment(sketch, "E1856", {"start": v(347.8, 11.68) * mm, "end": v(347.6, 9.87) * mm});
            skLineSegment(sketch, "E1857", {"start": v(347.6, 9.87) * mm, "end": v(352.52, 9.87) * mm});
            skLineSegment(sketch, "E1858", {"start": v(326.22, 28.55) * mm, "end": v(324.96, 28.55) * mm});
            skFitSpline(sketch, "E1859", {"points": [v(324.96, 28.55) * mm, v(316.77, 28.55) * mm, v(312.7, 31.86) * mm, v(313.69, 41.15) * mm]});
            skLineSegment(sketch, "E1860", {"start": v(313.69, 41.15) * mm, "end": v(315.74, 60.61) * mm});
            skLineSegment(sketch, "E1861", {"start": v(315.74, 60.61) * mm, "end": v(314, 60.61) * mm});
            skLineSegment(sketch, "E1862", {"start": v(312.03, 62.82) * mm, "end": v(312.26, 64.95) * mm});
            skLineSegment(sketch, "E1863", {"start": v(314.7, 67.23) * mm, "end": v(316.44, 67.23) * mm});
            skLineSegment(sketch, "E1864", {"start": v(316.44, 67.23) * mm, "end": v(317.78, 79.91) * mm});
            skLineSegment(sketch, "E1865", {"start": v(320.22, 82.12) * mm, "end": v(322.9, 82.12) * mm});
            skLineSegment(sketch, "E1866", {"start": v(324.95, 79.91) * mm, "end": v(323.6, 67.23) * mm});
            skLineSegment(sketch, "E1867", {"start": v(323.6, 67.23) * mm, "end": v(329.68, 67.23) * mm});
            skLineSegment(sketch, "E1868", {"start": v(331.73, 65.02) * mm, "end": v(331.5, 62.9) * mm});
            skLineSegment(sketch, "E1869", {"start": v(328.98, 60.61) * mm, "end": v(322.91, 60.61) * mm});
            skLineSegment(sketch, "E1870", {"start": v(322.91, 60.61) * mm, "end": v(320.86, 41.15) * mm});
            skFitSpline(sketch, "E1871", {"points": [v(320.86, 41.15) * mm, v(320.38, 36.58) * mm, v(322.43, 35.16) * mm, v(325.66, 35.16) * mm]});
            skLineSegment(sketch, "E1872", {"start": v(325.66, 35.16) * mm, "end": v(326.92, 35.16) * mm});
            skLineSegment(sketch, "E1873", {"start": v(328.9, 33.04) * mm, "end": v(328.67, 30.83) * mm});
            skFitSpline(sketch, "E1874", {"points": [v(310.04, 8.03) * mm, v(309.4, 7.87) * mm, v(308.83, 7.78) * mm, v(308.32, 7.78) * mm]});
            skLineSegment(sketch, "E1875", {"start": v(308.32, 7.78) * mm, "end": v(304.1, 7.78) * mm});
            skLineSegment(sketch, "E1876", {"start": v(304.1, 7.78) * mm, "end": v(305.06, 17) * mm});
            skLineSegment(sketch, "E1877", {"start": v(305.06, 17) * mm, "end": v(309.29, 17) * mm});
            skEllipticalArc(sketch, "E1878", {});
            skEllipticalArc(sketch, "E1879", {});
            skEllipticalArc(sketch, "E1880", {});
            skEllipticalArc(sketch, "E1881", {});
            skEllipticalArc(sketch, "E1882", {});
            skLineSegment(sketch, "E1883", {"start": v(285.42, 55.5) * mm, "end": v(282.5, 55.5) * mm});
            skFitSpline(sketch, "E1884", {"points": [v(282.5, 55.5) * mm, v(281.32, 55.5) * mm, v(280.47, 56.36) * mm, v(280.62, 57.78) * mm]});
            skFitSpline(sketch, "E1885", {"points": [v(280.62, 57.78) * mm, v(281.3, 64.31) * mm, v(287.03, 68.5) * mm, v(294.2, 68.5) * mm]});
            skFitSpline(sketch, "E1886", {"points": [v(294.2, 68.5) * mm, v(300.97, 68.5) * mm, v(306.57, 64) * mm, v(305.57, 54.55) * mm]});
            skLineSegment(sketch, "E1887", {"start": v(305.57, 54.55) * mm, "end": v(303.07, 30.83) * mm});
            skFitSpline(sketch, "E1888", {"points": [v(303.07, 30.83) * mm, v(302.92, 29.5) * mm, v(301.88, 28.55) * mm, v(300.7, 28.55) * mm]});
            skLineSegment(sketch, "E1889", {"start": v(300.7, 28.55) * mm, "end": v(297.94, 28.55) * mm});
            skFitSpline(sketch, "E1890", {"points": [v(297.94, 28.55) * mm, v(296.76, 28.55) * mm, v(295.91, 29.5) * mm, v(296.05, 30.83) * mm]});
            skLineSegment(sketch, "E1891", {"start": v(296.05, 30.83) * mm, "end": v(296.13, 31.54) * mm});
            skFitSpline(sketch, "E1892", {"points": [v(296.13, 31.54) * mm, v(294.49, 29.41) * mm, v(290.95, 28) * mm, v(287.88, 28) * mm]});
            skFitSpline(sketch, "E1893", {"points": [v(287.88, 28) * mm, v(281.65, 28) * mm, v(276.98, 32.96) * mm, v(277.65, 39.34) * mm]});
            skFitSpline(sketch, "E1894", {"points": [v(277.65, 39.34) * mm, v(278.3, 45.49) * mm, v(281.02, 48.87) * mm, v(288.62, 50.69) * mm]});
            skLineSegment(sketch, "E1895", {"start": v(288.62, 50.69) * mm, "end": v(298.23, 52.97) * mm});
            skLineSegment(sketch, "E1896", {"start": v(298.23, 52.97) * mm, "end": v(298.58, 56.28) * mm});
            skFitSpline(sketch, "E1897", {"points": [v(298.58, 56.28) * mm, v(298.93, 59.59) * mm, v(296.73, 61.87) * mm, v(293.5, 61.87) * mm]});
            skFitSpline(sketch, "E1898", {"points": [v(293.5, 61.87) * mm, v(289.88, 61.87) * mm, v(288.03, 60.06) * mm, v(287.79, 57.78) * mm]});
            skFitSpline(sketch, "E1899", {"points": [v(287.79, 57.78) * mm, v(287.64, 56.36) * mm, v(286.6, 55.5) * mm, v(285.42, 55.5) * mm]});
            skLineSegment(sketch, "E1900", {"start": v(271.86, 13.77) * mm, "end": v(272.2, 17) * mm});
            skLineSegment(sketch, "E1901", {"start": v(272.2, 17) * mm, "end": v(275.05, 17) * mm});
            skLineSegment(sketch, "E1902", {"start": v(275.05, 17) * mm, "end": v(274.08, 7.78) * mm});
            skLineSegment(sketch, "E1903", {"start": v(274.08, 7.78) * mm, "end": v(271.23, 7.78) * mm});
            skLineSegment(sketch, "E1904", {"start": v(271.23, 7.78) * mm, "end": v(271.62, 11.5) * mm});
            skLineSegment(sketch, "E1905", {"start": v(271.62, 11.5) * mm, "end": v(268.5, 11.5) * mm});
            skLineSegment(sketch, "E1906", {"start": v(268.5, 11.5) * mm, "end": v(268.12, 7.78) * mm});
            skLineSegment(sketch, "E1907", {"start": v(268.12, 7.78) * mm, "end": v(265.27, 7.78) * mm});
            skLineSegment(sketch, "E1908", {"start": v(265.27, 7.78) * mm, "end": v(266.24, 17) * mm});
            skLineSegment(sketch, "E1909", {"start": v(266.24, 17) * mm, "end": v(269.08, 17) * mm});
            skLineSegment(sketch, "E1910", {"start": v(269.08, 17) * mm, "end": v(268.75, 13.77) * mm});
            skLineSegment(sketch, "E1911", {"start": v(268.75, 13.77) * mm, "end": v(271.86, 13.77) * mm});
            skLineSegment(sketch, "E1912", {"start": v(260.77, 14.72) * mm, "end": v(260.04, 7.78) * mm});
            skLineSegment(sketch, "E1913", {"start": v(260.04, 7.78) * mm, "end": v(257.2, 7.78) * mm});
            skLineSegment(sketch, "E1914", {"start": v(257.2, 7.78) * mm, "end": v(257.92, 14.72) * mm});
            skLineSegment(sketch, "E1915", {"start": v(257.92, 14.72) * mm, "end": v(255.02, 14.72) * mm});
            skLineSegment(sketch, "E1916", {"start": v(255.02, 14.72) * mm, "end": v(255.26, 17) * mm});
            skLineSegment(sketch, "E1917", {"start": v(255.26, 17) * mm, "end": v(263.9, 17) * mm});
            skLineSegment(sketch, "E1918", {"start": v(263.9, 17) * mm, "end": v(263.67, 14.72) * mm});
            skLineSegment(sketch, "E1919", {"start": v(263.67, 14.72) * mm, "end": v(260.77, 14.72) * mm});
            skLineSegment(sketch, "E1920", {"start": v(285.24, 9.87) * mm, "end": v(285.02, 7.78) * mm});
            skLineSegment(sketch, "E1921", {"start": v(285.02, 7.78) * mm, "end": v(277.25, 7.78) * mm});
            skLineSegment(sketch, "E1922", {"start": v(277.25, 7.78) * mm, "end": v(278.22, 17) * mm});
            skLineSegment(sketch, "E1923", {"start": v(278.22, 17) * mm, "end": v(285.85, 17) * mm});
            skLineSegment(sketch, "E1924", {"start": v(285.85, 17) * mm, "end": v(285.64, 15.03) * mm});
            skLineSegment(sketch, "E1925", {"start": v(285.64, 15.03) * mm, "end": v(280.87, 15.03) * mm});
            skLineSegment(sketch, "E1926", {"start": v(280.87, 15.03) * mm, "end": v(280.71, 13.56) * mm});
            skLineSegment(sketch, "E1927", {"start": v(280.71, 13.56) * mm, "end": v(285.14, 13.56) * mm});
            skLineSegment(sketch, "E1928", {"start": v(285.14, 13.56) * mm, "end": v(284.95, 11.68) * mm});
            skLineSegment(sketch, "E1929", {"start": v(284.95, 11.68) * mm, "end": v(280.52, 11.68) * mm});
            skLineSegment(sketch, "E1930", {"start": v(280.52, 11.68) * mm, "end": v(280.33, 9.87) * mm});
            skLineSegment(sketch, "E1931", {"start": v(280.33, 9.87) * mm, "end": v(285.24, 9.87) * mm});
            skEllipticalArc(sketch, "E1932", {});
            skEllipticalArc(sketch, "E1933", {});
            skFitSpline(sketch, "E1934", {"points": [v(300.69, 16.48) * mm, v(301.18, 16.03) * mm, v(301.38, 15.46) * mm, v(301.31, 14.79) * mm]});
            skFitSpline(sketch, "E1935", {"points": [v(300.87, 13.7) * mm, v(300.62, 13.38) * mm, v(300.26, 13.1) * mm, v(299.8, 12.86) * mm]});
            skFitSpline(sketch, "E1936", {"points": [v(299.8, 12.86) * mm, v(300.14, 12.77) * mm, v(300.4, 12.67) * mm, v(300.58, 12.55) * mm]});
            skFitSpline(sketch, "E1937", {"points": [v(301.22, 11.8) * mm, v(301.35, 11.5) * mm, v(301.4, 11.13) * mm, v(301.35, 10.7) * mm]});
            skEllipticalArc(sketch, "E1938", {});
            skFitSpline(sketch, "E1939", {"points": [v(297.32, 7.62) * mm, v(296.48, 7.62) * mm, v(295.83, 7.72) * mm, v(295.37, 7.92) * mm]});
            skFitSpline(sketch, "E1940", {"points": [v(294.26, 8.78) * mm, v(294, 9.16) * mm, v(293.8, 9.64) * mm, v(293.7, 10.21) * mm]});
            skLineSegment(sketch, "E1941", {"start": v(293.7, 10.21) * mm, "end": v(296.29, 10.55) * mm});
            skFitSpline(sketch, "E1942", {"points": [v(296.29, 10.55) * mm, v(296.33, 10.04) * mm, v(296.45, 9.68) * mm, v(296.64, 9.48) * mm]});
            skFitSpline(sketch, "E1943", {"points": [v(298.76, 10.56) * mm, v(298.8, 11) * mm, v(298.73, 11.32) * mm, v(298.54, 11.56) * mm]});
            skFitSpline(sketch, "E1944", {"points": [v(297.68, 11.9) * mm, v(297.48, 11.9) * mm, v(297.2, 11.86) * mm, v(296.84, 11.76) * mm]});
            skLineSegment(sketch, "E1945", {"start": v(296.84, 11.76) * mm, "end": v(297.16, 13.59) * mm});
            skFitSpline(sketch, "E1946", {"points": [v(298.78, 14.64) * mm, v(298.8, 14.92) * mm, v(298.75, 15.14) * mm, v(298.6, 15.3) * mm]});
            skFitSpline(sketch, "E1947", {"points": [v(297.17, 15.29) * mm, v(296.96, 15.1) * mm, v(296.8, 14.78) * mm, v(296.69, 14.33) * mm]});
            skLineSegment(sketch, "E1948", {"start": v(296.69, 14.33) * mm, "end": v(294.31, 14.76) * mm});
            skFitSpline(sketch, "E1949", {"points": [v(326.75, 17.15) * mm, v(327.9, 17.15) * mm, v(328.8, 16.91) * mm, v(329.4, 16.44) * mm]});
            skLineSegment(sketch, "E1950", {"start": v(330.66, 14.28) * mm, "end": v(328.09, 13.72) * mm});
            skFitSpline(sketch, "E1951", {"points": [v(328.09, 13.72) * mm, v(328.03, 14) * mm, v(327.96, 14.21) * mm, v(327.88, 14.34) * mm]});
            skEllipticalArc(sketch, "E1952", {});
            skFitSpline(sketch, "E1953", {"points": [v(324.45, 12.43) * mm, v(324.34, 11.4) * mm, v(324.42, 10.7) * mm, v(324.7, 10.33) * mm]});
            skFitSpline(sketch, "E1954", {"points": [v(324.7, 10.33) * mm, v(324.96, 9.95) * mm, v(325.38, 9.76) * mm, v(325.94, 9.76) * mm]});
            skFitSpline(sketch, "E1955", {"points": [v(325.94, 9.76) * mm, v(326.48, 9.76) * mm, v(326.9, 9.91) * mm, v(327.22, 10.22) * mm]});
            skEllipticalArc(sketch, "E1956", {});
            skLineSegment(sketch, "E1957", {"start": v(327.97, 11.55) * mm, "end": v(330.38, 10.8) * mm});
            skEllipticalArc(sketch, "E1958", {});
            skFitSpline(sketch, "E1959", {"points": [v(327.95, 7.98) * mm, v(327.4, 7.74) * mm, v(326.7, 7.63) * mm, v(325.88, 7.63) * mm]});
            skFitSpline(sketch, "E1960", {"points": [v(325.88, 7.63) * mm, v(324.88, 7.63) * mm, v(324.07, 7.77) * mm, v(323.47, 8.06) * mm]});
            skEllipticalArc(sketch, "E1961", {});
            skFitSpline(sketch, "E1962", {"points": [v(321.6, 12.4) * mm, v(321.75, 13.93) * mm, v(322.28, 15.1) * mm, v(323.18, 15.92) * mm]});
            skLineSegment(sketch, "E1963", {"start": v(335.89, 7.78) * mm, "end": v(333.03, 7.78) * mm});
            skLineSegment(sketch, "E1964", {"start": v(333.03, 7.78) * mm, "end": v(334, 17) * mm});
            skLineSegment(sketch, "E1965", {"start": v(334, 17) * mm, "end": v(338.74, 17) * mm});
            skEllipticalArc(sketch, "E1966", {});
            skEllipticalArc(sketch, "E1967", {});
            skEllipticalArc(sketch, "E1968", {});
            skFitSpline(sketch, "E1969", {"points": [v(340.25, 11.5) * mm, v(340.34, 11.43) * mm, v(340.48, 11.27) * mm, v(340.65, 11.02) * mm]});
            skLineSegment(sketch, "E1970", {"start": v(340.99, 10.45) * mm, "end": v(342.09, 7.78) * mm});
            skLineSegment(sketch, "E1971", {"start": v(342.09, 7.78) * mm, "end": v(338.87, 7.78) * mm});
            skLineSegment(sketch, "E1972", {"start": v(338.87, 7.78) * mm, "end": v(337.65, 10.6) * mm});
            skEllipticalArc(sketch, "E1973", {});
            skLineSegment(sketch, "E1974", {"start": v(336.53, 11.52) * mm, "end": v(336.28, 11.52) * mm});
            skLineSegment(sketch, "E1975", {"start": v(336.28, 11.52) * mm, "end": v(335.89, 7.78) * mm});
            skEllipticalArc(sketch, "E1976", {});
            skLineSegment(sketch, "E1977", {"start": v(335.22, 42.1) * mm, "end": v(336.46, 53.92) * mm});
            skEllipticalArc(sketch, "E1978", {});
            skEllipticalArc(sketch, "E1979", {});
            skLineSegment(sketch, "E1980", {"start": v(362.93, 53.92) * mm, "end": v(361.69, 42.1) * mm});
            skEllipticalArc(sketch, "E1981", {});
            skLineSegment(sketch, "E1982", {"start": v(347.04, 28) * mm, "end": v(346.88, 28) * mm});
            skLineSegment(sketch, "E1983", {"start": v(368.02, 7.78) * mm, "end": v(368.75, 14.72) * mm});
            skLineSegment(sketch, "E1984", {"start": v(368.75, 14.72) * mm, "end": v(365.85, 14.72) * mm});
            skLineSegment(sketch, "E1985", {"start": v(365.85, 14.72) * mm, "end": v(366.09, 17) * mm});
            skLineSegment(sketch, "E1986", {"start": v(366.09, 17) * mm, "end": v(374.74, 17) * mm});
            skLineSegment(sketch, "E1987", {"start": v(374.74, 17) * mm, "end": v(374.5, 14.72) * mm});
            skLineSegment(sketch, "E1988", {"start": v(374.5, 14.72) * mm, "end": v(371.6, 14.72) * mm});
            skLineSegment(sketch, "E1989", {"start": v(371.6, 14.72) * mm, "end": v(370.87, 7.78) * mm});
            skLineSegment(sketch, "E1990", {"start": v(370.87, 7.78) * mm, "end": v(368.02, 7.78) * mm});
            skFitSpline(sketch, "E1991", {"points": [v(378.06, 8.12) * mm, v(377.4, 8.45) * mm, v(376.91, 8.98) * mm, v(376.57, 9.7) * mm]});
            skFitSpline(sketch, "E1992", {"points": [v(376.57, 9.7) * mm, v(376.22, 10.4) * mm, v(376.1, 11.3) * mm, v(376.21, 12.38) * mm]});
            skFitSpline(sketch, "E1993", {"points": [v(376.21, 12.38) * mm, v(376.37, 13.88) * mm, v(376.91, 15.05) * mm, v(377.84, 15.9) * mm]});
            skEllipticalArc(sketch, "E1994", {});
            skFitSpline(sketch, "E1995", {"points": [v(383.2, 8.2) * mm, v(382.48, 7.82) * mm, v(381.6, 7.63) * mm, v(380.58, 7.63) * mm]});
            skFitSpline(sketch, "E1996", {"points": [v(380.58, 7.63) * mm, v(379.54, 7.63) * mm, v(378.7, 7.8) * mm, v(378.06, 8.12) * mm]});
            skLineSegment(sketch, "E1997", {"start": v(294.12, 145.46) * mm, "end": v(234.12, 145.46) * mm});
            skLineSegment(sketch, "E1998", {"start": v(234.12, 175.46) * mm, "end": v(294.12, 175.46) * mm});
            skLineSegment(sketch, "E1999", {"start": v(219, -169.4) * mm, "end": v(269, -169.4) * mm});
            skLineSegment(sketch, "E2000", {"start": v(269, -169.4) * mm, "end": v(269, -174.4) * mm});
            skLineSegment(sketch, "E2001", {"start": v(269, -174.4) * mm, "end": v(219, -174.4) * mm});
            skLineSegment(sketch, "E2002", {"start": v(219, -174.4) * mm, "end": v(219, -169.4) * mm});
            skLineSegment(sketch, "E2003", {"start": v(392.62, 15.13) * mm, "end": v(391.37, 15.13) * mm});
            skFitSpline(sketch, "E2004", {"points": [v(393.66, 14.9) * mm, v(393.49, 15.05) * mm, v(393.14, 15.13) * mm, v(392.62, 15.13) * mm]});
            skFitSpline(sketch, "E2005", {"points": [v(393.87, 14.2) * mm, v(393.9, 14.5) * mm, v(393.83, 14.73) * mm, v(393.66, 14.9) * mm]});
            skFitSpline(sketch, "E2006", {"points": [v(392.38, 13.26) * mm, v(392.5, 13.26) * mm, v(392.76, 13.3) * mm, v(393.14, 13.39) * mm]});
            skLineSegment(sketch, "E2007", {"start": v(391.18, 13.26) * mm, "end": v(392.38, 13.26) * mm});
            skLineSegment(sketch, "E2008", {"start": v(391.37, 15.13) * mm, "end": v(391.18, 13.26) * mm});
            skLineSegment(sketch, "E2009", {"start": v(358.8, 11.3) * mm, "end": v(360.82, 11.3) * mm});
            skLineSegment(sketch, "E2010", {"start": v(360.15, 14.6) * mm, "end": v(358.8, 11.3) * mm});
            skLineSegment(sketch, "E2011", {"start": v(360.82, 11.3) * mm, "end": v(360.15, 14.6) * mm});
            skLineSegment(sketch, "E2012", {"start": v(308.4, 14.9) * mm, "end": v(307.69, 14.9) * mm});
            skEllipticalArc(sketch, "E2013", {});
            skEllipticalArc(sketch, "E2014", {});
            skFitSpline(sketch, "E2015", {"points": [v(309.14, 10.07) * mm, v(309.4, 10.2) * mm, v(309.63, 10.43) * mm, v(309.8, 10.76) * mm]});
            skEllipticalArc(sketch, "E2016", {});
            skLineSegment(sketch, "E2017", {"start": v(307.16, 9.87) * mm, "end": v(307.86, 9.87) * mm});
            skLineSegment(sketch, "E2018", {"start": v(307.69, 14.9) * mm, "end": v(307.16, 9.87) * mm});
            skLineSegment(sketch, "E2019", {"start": v(297.08, 42.1) * mm, "end": v(297.5, 46.04) * mm});
            skFitSpline(sketch, "E2020", {"points": [v(289.36, 34.61) * mm, v(293.46, 34.61) * mm, v(296.7, 38.47) * mm, v(297.08, 42.1) * mm]});
            skFitSpline(sketch, "E2021", {"points": [v(284.85, 39.66) * mm, v(284.59, 37.13) * mm, v(286.37, 34.61) * mm, v(289.36, 34.61) * mm]});
            skFitSpline(sketch, "E2022", {"points": [v(289.02, 44.07) * mm, v(285.8, 43.36) * mm, v(285, 41.07) * mm, v(284.85, 39.66) * mm]});
            skLineSegment(sketch, "E2023", {"start": v(297.5, 46.04) * mm, "end": v(289.02, 44.07) * mm});
            skFitSpline(sketch, "E2024", {"points": [v(338.95, 14.9) * mm, v(338.77, 15.05) * mm, v(338.43, 15.13) * mm, v(337.9, 15.13) * mm]});
            skFitSpline(sketch, "E2025", {"points": [v(339.16, 14.2) * mm, v(339.19, 14.5) * mm, v(339.12, 14.73) * mm, v(338.95, 14.9) * mm]});
            skArc(sketch, "E2026", {"start": v(338.92, 13.67) * mm, "mid": v(339.08, 13.92) * mm, "end": v(339.16, 14.2) * mm});
            skFitSpline(sketch, "E2027", {"points": [v(337.66, 13.26) * mm, v(337.8, 13.26) * mm, v(338.05, 13.3) * mm, v(338.43, 13.39) * mm]});
            skLineSegment(sketch, "E2028", {"start": v(336.46, 13.26) * mm, "end": v(337.66, 13.26) * mm});
            skLineSegment(sketch, "E2029", {"start": v(336.66, 15.13) * mm, "end": v(336.46, 13.26) * mm});
            skLineSegment(sketch, "E2030", {"start": v(337.9, 15.13) * mm, "end": v(336.66, 15.13) * mm});
            skFitSpline(sketch, "E2031", {"points": [v(350.54, 61.87) * mm, v(345.65, 61.87) * mm, v(344.09, 58.25) * mm, v(343.63, 53.92) * mm]});
            skFitSpline(sketch, "E2032", {"points": [v(355.76, 53.92) * mm, v(356.22, 58.25) * mm, v(355.42, 61.87) * mm, v(350.54, 61.87) * mm]});
            skLineSegment(sketch, "E2033", {"start": v(354.52, 42.1) * mm, "end": v(355.76, 53.92) * mm});
            skFitSpline(sketch, "E2034", {"points": [v(347.58, 34.61) * mm, v(352.63, 34.61) * mm, v(354.12, 38.32) * mm, v(354.52, 42.1) * mm]});
            skFitSpline(sketch, "E2035", {"points": [v(342.38, 42.1) * mm, v(341.99, 38.32) * mm, v(342.7, 34.61) * mm, v(347.58, 34.61) * mm]});
            skLineSegment(sketch, "E2036", {"start": v(343.63, 53.92) * mm, "end": v(342.38, 42.1) * mm});
            skFitSpline(sketch, "E2037", {"points": [v(379.8, 14.38) * mm, v(379.4, 13.98) * mm, v(379.16, 13.3) * mm, v(379.06, 12.37) * mm]});
            skEllipticalArc(sketch, "E2038", {});
            skFitSpline(sketch, "E2039", {"points": [v(382.2, 10.35) * mm, v(382.57, 10.75) * mm, v(382.81, 11.46) * mm, v(382.92, 12.5) * mm]});
            skFitSpline(sketch, "E2040", {"points": [v(380.71, 9.76) * mm, v(381.32, 9.76) * mm, v(381.82, 9.95) * mm, v(382.2, 10.35) * mm]});
            skEllipticalArc(sketch, "E2041", {});
            skFitSpline(sketch, "E2042", {"points": [v(379.06, 12.37) * mm, v(378.96, 11.44) * mm, v(379.06, 10.77) * mm, v(379.36, 10.36) * mm]});
            skArc(sketch, "E2043", {"start": v(-673.95, 50.09) * mm, "mid": v(-666.45, 47.72) * mm, "end": v(-658.95, 50.09) * mm});
            skLineSegment(sketch, "E2044", {"start": v(-673.95, 64.1) * mm, "end": v(-673.95, 50.09) * mm});
            skLineSegment(sketch, "E2045", {"start": v(-732, 64.1) * mm, "end": v(-673.95, 64.1) * mm});
            skLineSegment(sketch, "E2046", {"start": v(-732, 59.1) * mm, "end": v(-732, 64.1) * mm});
            skLineSegment(sketch, "E2047", {"start": v(-730.9, 59.1) * mm, "end": v(-732, 59.1) * mm});
            skLineSegment(sketch, "E2048", {"start": v(-730.9, 57.1) * mm, "end": v(-730.9, 59.1) * mm});
            skLineSegment(sketch, "E2049", {"start": v(-732, 57.1) * mm, "end": v(-730.9, 57.1) * mm});
            skLineSegment(sketch, "E2050", {"start": v(-732, 56.1) * mm, "end": v(-732, 57.1) * mm});
            skLineSegment(sketch, "E2051", {"start": v(-735.4, 56.1) * mm, "end": v(-732, 56.1) * mm});
            skLineSegment(sketch, "E2052", {"start": v(-735.4, 57.1) * mm, "end": v(-735.4, 56.1) * mm});
            skLineSegment(sketch, "E2053", {"start": v(-736.5, 57.1) * mm, "end": v(-735.4, 57.1) * mm});
            skLineSegment(sketch, "E2054", {"start": v(-736.5, 59.1) * mm, "end": v(-736.5, 57.1) * mm});
            skLineSegment(sketch, "E2055", {"start": v(-735.4, 59.1) * mm, "end": v(-736.5, 59.1) * mm});
            skLineSegment(sketch, "E2056", {"start": v(-735.4, 64.1) * mm, "end": v(-735.4, 59.1) * mm});
            skLineSegment(sketch, "E2057", {"start": v(-754, 64.1) * mm, "end": v(-735.4, 64.1) * mm});
            skLineSegment(sketch, "E2058", {"start": v(-754, 60.1) * mm, "end": v(-754, 64.1) * mm});
            skLineSegment(sketch, "E2059", {"start": v(-754, 60.1) * mm, "end": v(-753, 60.1) * mm});
            skLineSegment(sketch, "E2060", {"start": v(-753, 60.1) * mm, "end": v(-753, 56.1) * mm});
            skLineSegment(sketch, "E2061", {"start": v(-753, 56.1) * mm, "end": v(-754, 56.1) * mm});
            skLineSegment(sketch, "E2062", {"start": v(-754, 22.05) * mm, "end": v(-754, 56.1) * mm});
            skLineSegment(sketch, "E2063", {"start": v(-749, 22.05) * mm, "end": v(-754, 22.05) * mm});
            skLineSegment(sketch, "E2064", {"start": v(-749, 23.15) * mm, "end": v(-749, 22.05) * mm});
            skLineSegment(sketch, "E2065", {"start": v(-747, 23.15) * mm, "end": v(-749, 23.15) * mm});
            skLineSegment(sketch, "E2066", {"start": v(-747, 22.05) * mm, "end": v(-747, 23.15) * mm});
            skLineSegment(sketch, "E2067", {"start": v(-746, 22.05) * mm, "end": v(-747, 22.05) * mm});
            skLineSegment(sketch, "E2068", {"start": v(-746, 18.65) * mm, "end": v(-746, 22.05) * mm});
            skLineSegment(sketch, "E2069", {"start": v(-747, 18.65) * mm, "end": v(-746, 18.65) * mm});
            skLineSegment(sketch, "E2070", {"start": v(-747, 17.55) * mm, "end": v(-747, 18.65) * mm});
            skLineSegment(sketch, "E2071", {"start": v(-749, 17.55) * mm, "end": v(-747, 17.55) * mm});
            skLineSegment(sketch, "E2072", {"start": v(-749, 18.65) * mm, "end": v(-749, 17.55) * mm});
            skLineSegment(sketch, "E2073", {"start": v(-754, 18.65) * mm, "end": v(-749, 18.65) * mm});
            skLineSegment(sketch, "E2074", {"start": v(-754, -7.78) * mm, "end": v(-754, 18.65) * mm});
            skLineSegment(sketch, "E2075", {"start": v(-759, -7.78) * mm, "end": v(-754, -7.78) * mm});
            skLineSegment(sketch, "E2076", {"start": v(-759, -7.78) * mm, "end": v(-759, -57.77) * mm});
            skLineSegment(sketch, "E2077", {"start": v(-754, -57.77) * mm, "end": v(-759, -57.77) * mm});
            skLineSegment(sketch, "E2078", {"start": v(-754, -84.2) * mm, "end": v(-754, -57.77) * mm});
            skLineSegment(sketch, "E2079", {"start": v(-749, -84.2) * mm, "end": v(-754, -84.2) * mm});
            skLineSegment(sketch, "E2080", {"start": v(-749, -83.1) * mm, "end": v(-749, -84.2) * mm});
            skLineSegment(sketch, "E2081", {"start": v(-747, -83.1) * mm, "end": v(-749, -83.1) * mm});
            skLineSegment(sketch, "E2082", {"start": v(-747, -84.2) * mm, "end": v(-747, -83.1) * mm});
            skLineSegment(sketch, "E2083", {"start": v(-746, -84.2) * mm, "end": v(-747, -84.2) * mm});
            skLineSegment(sketch, "E2084", {"start": v(-746, -87.6) * mm, "end": v(-746, -84.2) * mm});
            skLineSegment(sketch, "E2085", {"start": v(-747, -87.6) * mm, "end": v(-746, -87.6) * mm});
            skLineSegment(sketch, "E2086", {"start": v(-747, -88.7) * mm, "end": v(-747, -87.6) * mm});
            skLineSegment(sketch, "E2087", {"start": v(-749, -88.7) * mm, "end": v(-747, -88.7) * mm});
            skLineSegment(sketch, "E2088", {"start": v(-749, -87.6) * mm, "end": v(-749, -88.7) * mm});
            skLineSegment(sketch, "E2089", {"start": v(-754, -87.6) * mm, "end": v(-749, -87.6) * mm});
            skLineSegment(sketch, "E2090", {"start": v(-754, -114.02) * mm, "end": v(-754, -87.6) * mm});
            skLineSegment(sketch, "E2091", {"start": v(-759, -114.02) * mm, "end": v(-754, -114.02) * mm});
            skLineSegment(sketch, "E2092", {"start": v(-759, -114.02) * mm, "end": v(-759, -164.03) * mm});
            skLineSegment(sketch, "E2093", {"start": v(-754, -164.03) * mm, "end": v(-759, -164.03) * mm});
            skLineSegment(sketch, "E2094", {"start": v(-754, -190.45) * mm, "end": v(-754, -164.03) * mm});
            skLineSegment(sketch, "E2095", {"start": v(-749, -190.45) * mm, "end": v(-754, -190.45) * mm});
            skLineSegment(sketch, "E2096", {"start": v(-749, -189.35) * mm, "end": v(-749, -190.45) * mm});
            skLineSegment(sketch, "E2097", {"start": v(-747, -189.35) * mm, "end": v(-749, -189.35) * mm});
            skLineSegment(sketch, "E2098", {"start": v(-747, -190.45) * mm, "end": v(-747, -189.35) * mm});
            skLineSegment(sketch, "E2099", {"start": v(-746, -190.45) * mm, "end": v(-747, -190.45) * mm});
            skLineSegment(sketch, "E2100", {"start": v(-746, -193.85) * mm, "end": v(-746, -190.45) * mm});
            skLineSegment(sketch, "E2101", {"start": v(-747, -193.85) * mm, "end": v(-746, -193.85) * mm});
            skLineSegment(sketch, "E2102", {"start": v(-747, -194.9) * mm, "end": v(-747, -193.85) * mm});
            skLineSegment(sketch, "E2103", {"start": v(-749, -194.9) * mm, "end": v(-747, -194.9) * mm});
            skLineSegment(sketch, "E2104", {"start": v(-749, -193.85) * mm, "end": v(-749, -194.9) * mm});
            skLineSegment(sketch, "E2105", {"start": v(-754, -193.85) * mm, "end": v(-749, -193.85) * mm});
            skLineSegment(sketch, "E2106", {"start": v(-754, -219.9) * mm, "end": v(-754, -193.85) * mm});
            skArc(sketch, "E2107", {"start": v(-738, -235.9) * mm, "mid": v(-742.69, -224.59) * mm, "end": v(-754, -219.9) * mm});
            skLineSegment(sketch, "E2108", {"start": v(-718.2, -235.9) * mm, "end": v(-738, -235.9) * mm});
            skLineSegment(sketch, "E2109", {"start": v(-718.2, -230.9) * mm, "end": v(-718.2, -235.9) * mm});
            skLineSegment(sketch, "E2110", {"start": v(-719.3, -230.9) * mm, "end": v(-718.2, -230.9) * mm});
            skLineSegment(sketch, "E2111", {"start": v(-719.3, -228.9) * mm, "end": v(-719.3, -230.9) * mm});
            skLineSegment(sketch, "E2112", {"start": v(-718.2, -228.9) * mm, "end": v(-719.3, -228.9) * mm});
            skLineSegment(sketch, "E2113", {"start": v(-718.2, -227.9) * mm, "end": v(-718.2, -228.9) * mm});
            skLineSegment(sketch, "E2114", {"start": v(-714.8, -227.9) * mm, "end": v(-718.2, -227.9) * mm});
            skLineSegment(sketch, "E2115", {"start": v(-714.8, -228.9) * mm, "end": v(-714.8, -227.9) * mm});
            skLineSegment(sketch, "E2116", {"start": v(-713.7, -228.9) * mm, "end": v(-714.8, -228.9) * mm});
            skLineSegment(sketch, "E2117", {"start": v(-713.7, -230.9) * mm, "end": v(-713.7, -228.9) * mm});
            skLineSegment(sketch, "E2118", {"start": v(-714.8, -230.9) * mm, "end": v(-713.7, -230.9) * mm});
            skLineSegment(sketch, "E2119", {"start": v(-714.8, -235.9) * mm, "end": v(-714.8, -230.9) * mm});
            skLineSegment(sketch, "E2120", {"start": v(-658.2, -235.9) * mm, "end": v(-714.8, -235.9) * mm});
            skLineSegment(sketch, "E2121", {"start": v(-658.2, -230.9) * mm, "end": v(-658.2, -235.9) * mm});
            skLineSegment(sketch, "E2122", {"start": v(-659.3, -230.9) * mm, "end": v(-658.2, -230.9) * mm});
            skLineSegment(sketch, "E2123", {"start": v(-659.3, -228.9) * mm, "end": v(-659.3, -230.9) * mm});
            skLineSegment(sketch, "E2124", {"start": v(-658.2, -228.9) * mm, "end": v(-659.3, -228.9) * mm});
            skLineSegment(sketch, "E2125", {"start": v(-658.2, -227.9) * mm, "end": v(-658.2, -228.9) * mm});
            skLineSegment(sketch, "E2126", {"start": v(-654.8, -227.9) * mm, "end": v(-658.2, -227.9) * mm});
            skLineSegment(sketch, "E2127", {"start": v(-654.8, -228.9) * mm, "end": v(-654.8, -227.9) * mm});
            skLineSegment(sketch, "E2128", {"start": v(-653.7, -228.9) * mm, "end": v(-654.8, -228.9) * mm});
            skLineSegment(sketch, "E2129", {"start": v(-653.7, -230.9) * mm, "end": v(-653.7, -228.9) * mm});
            skLineSegment(sketch, "E2130", {"start": v(-654.8, -230.9) * mm, "end": v(-653.7, -230.9) * mm});
            skLineSegment(sketch, "E2131", {"start": v(-654.8, -235.9) * mm, "end": v(-654.8, -230.9) * mm});
            skLineSegment(sketch, "E2132", {"start": v(-648.2, -235.9) * mm, "end": v(-654.8, -235.9) * mm});
            skLineSegment(sketch, "E2133", {"start": v(-648.2, -178.55) * mm, "end": v(-648.2, -235.9) * mm});
            skLineSegment(sketch, "E2134", {"start": v(-489, -178.55) * mm, "end": v(-648.2, -178.55) * mm});
            skLineSegment(sketch, "E2135", {"start": v(-489, -235.9) * mm, "end": v(-489, -178.55) * mm});
            skLineSegment(sketch, "E2136", {"start": v(-480, -235.9) * mm, "end": v(-489, -235.9) * mm});
            skArc(sketch, "E2137", {"start": v(-464, -219.9) * mm, "mid": v(-475.31, -224.59) * mm, "end": v(-480, -235.9) * mm});
            skLineSegment(sketch, "E2138", {"start": v(-464, -193.85) * mm, "end": v(-464, -219.9) * mm});
            skLineSegment(sketch, "E2139", {"start": v(-469, -193.85) * mm, "end": v(-464, -193.85) * mm});
            skLineSegment(sketch, "E2140", {"start": v(-469, -194.95) * mm, "end": v(-469, -193.85) * mm});
            skLineSegment(sketch, "E2141", {"start": v(-471, -194.95) * mm, "end": v(-469, -194.95) * mm});
            skLineSegment(sketch, "E2142", {"start": v(-471, -193.85) * mm, "end": v(-471, -194.95) * mm});
            skLineSegment(sketch, "E2143", {"start": v(-472, -193.85) * mm, "end": v(-471, -193.85) * mm});
            skLineSegment(sketch, "E2144", {"start": v(-472, -190.45) * mm, "end": v(-472, -193.85) * mm});
            skLineSegment(sketch, "E2145", {"start": v(-471, -190.45) * mm, "end": v(-472, -190.45) * mm});
            skLineSegment(sketch, "E2146", {"start": v(-471, -189.35) * mm, "end": v(-471, -190.45) * mm});
            skLineSegment(sketch, "E2147", {"start": v(-469, -189.35) * mm, "end": v(-471, -189.35) * mm});
            skLineSegment(sketch, "E2148", {"start": v(-469, -190.45) * mm, "end": v(-469, -189.35) * mm});
            skLineSegment(sketch, "E2149", {"start": v(-464, -190.45) * mm, "end": v(-469, -190.45) * mm});
            skLineSegment(sketch, "E2150", {"start": v(-464, -163.9) * mm, "end": v(-464, -190.45) * mm});
            skLineSegment(sketch, "E2151", {"start": v(-459, -163.9) * mm, "end": v(-464, -163.9) * mm});
            skLineSegment(sketch, "E2152", {"start": v(-459, -115.9) * mm, "end": v(-459, -163.9) * mm});
            skLineSegment(sketch, "E2153", {"start": v(-464, -115.9) * mm, "end": v(-459, -115.9) * mm});
            skLineSegment(sketch, "E2154", {"start": v(-464, -87.6) * mm, "end": v(-464, -115.9) * mm});
            skLineSegment(sketch, "E2155", {"start": v(-469, -87.6) * mm, "end": v(-464, -87.6) * mm});
            skLineSegment(sketch, "E2156", {"start": v(-469, -88.7) * mm, "end": v(-469, -87.6) * mm});
            skLineSegment(sketch, "E2157", {"start": v(-471, -88.7) * mm, "end": v(-469, -88.7) * mm});
            skLineSegment(sketch, "E2158", {"start": v(-471, -87.6) * mm, "end": v(-471, -88.7) * mm});
            skLineSegment(sketch, "E2159", {"start": v(-472, -87.6) * mm, "end": v(-471, -87.6) * mm});
            skLineSegment(sketch, "E2160", {"start": v(-472, -84.2) * mm, "end": v(-472, -87.6) * mm});
            skLineSegment(sketch, "E2161", {"start": v(-471, -84.2) * mm, "end": v(-472, -84.2) * mm});
            skLineSegment(sketch, "E2162", {"start": v(-471, -83.1) * mm, "end": v(-471, -84.2) * mm});
            skLineSegment(sketch, "E2163", {"start": v(-469, -83.1) * mm, "end": v(-471, -83.1) * mm});
            skLineSegment(sketch, "E2164", {"start": v(-469, -84.2) * mm, "end": v(-469, -83.1) * mm});
            skLineSegment(sketch, "E2165", {"start": v(-464, -84.2) * mm, "end": v(-469, -84.2) * mm});
            skLineSegment(sketch, "E2166", {"start": v(-464, -57.9) * mm, "end": v(-464, -84.2) * mm});
            skLineSegment(sketch, "E2167", {"start": v(-459, -57.9) * mm, "end": v(-464, -57.9) * mm});
            skLineSegment(sketch, "E2168", {"start": v(-459, -7.9) * mm, "end": v(-459, -57.9) * mm});
            skLineSegment(sketch, "E2169", {"start": v(-464, -7.9) * mm, "end": v(-459, -7.9) * mm});
            skLineSegment(sketch, "E2170", {"start": v(-464, 18.65) * mm, "end": v(-464, -7.9) * mm});
            skLineSegment(sketch, "E2171", {"start": v(-469, 18.65) * mm, "end": v(-464, 18.65) * mm});
            skLineSegment(sketch, "E2172", {"start": v(-469, 17.55) * mm, "end": v(-469, 18.65) * mm});
            skLineSegment(sketch, "E2173", {"start": v(-471, 17.55) * mm, "end": v(-469, 17.55) * mm});
            skLineSegment(sketch, "E2174", {"start": v(-471, 18.65) * mm, "end": v(-471, 17.55) * mm});
            skLineSegment(sketch, "E2175", {"start": v(-472, 18.65) * mm, "end": v(-471, 18.65) * mm});
            skLineSegment(sketch, "E2176", {"start": v(-472, 22.05) * mm, "end": v(-472, 18.65) * mm});
            skLineSegment(sketch, "E2177", {"start": v(-471, 22.05) * mm, "end": v(-472, 22.05) * mm});
            skLineSegment(sketch, "E2178", {"start": v(-471, 23.15) * mm, "end": v(-471, 22.05) * mm});
            skLineSegment(sketch, "E2179", {"start": v(-469, 23.15) * mm, "end": v(-471, 23.15) * mm});
            skLineSegment(sketch, "E2180", {"start": v(-469, 22.05) * mm, "end": v(-469, 23.15) * mm});
            skLineSegment(sketch, "E2181", {"start": v(-464, 22.05) * mm, "end": v(-469, 22.05) * mm});
            skLineSegment(sketch, "E2182", {"start": v(-464, 56.1) * mm, "end": v(-464, 22.05) * mm});
            skLineSegment(sketch, "E2183", {"start": v(-465, 56.1) * mm, "end": v(-464, 56.1) * mm});
            skLineSegment(sketch, "E2184", {"start": v(-465, 60.1) * mm, "end": v(-465, 56.1) * mm});
            skLineSegment(sketch, "E2185", {"start": v(-464, 60.1) * mm, "end": v(-465, 60.1) * mm});
            skLineSegment(sketch, "E2186", {"start": v(-464, 64.1) * mm, "end": v(-464, 60.1) * mm});
            skLineSegment(sketch, "E2187", {"start": v(-482.6, 64.1) * mm, "end": v(-464, 64.1) * mm});
            skLineSegment(sketch, "E2188", {"start": v(-482.6, 59.1) * mm, "end": v(-482.6, 64.1) * mm});
            skLineSegment(sketch, "E2189", {"start": v(-481.5, 59.1) * mm, "end": v(-482.6, 59.1) * mm});
            skLineSegment(sketch, "E2190", {"start": v(-481.5, 57.1) * mm, "end": v(-481.5, 59.1) * mm});
            skLineSegment(sketch, "E2191", {"start": v(-482.6, 57.1) * mm, "end": v(-481.5, 57.1) * mm});
            skLineSegment(sketch, "E2192", {"start": v(-482.6, 56.1) * mm, "end": v(-482.6, 57.1) * mm});
            skLineSegment(sketch, "E2193", {"start": v(-486, 56.1) * mm, "end": v(-482.6, 56.1) * mm});
            skLineSegment(sketch, "E2194", {"start": v(-486, 57.1) * mm, "end": v(-486, 56.1) * mm});
            skLineSegment(sketch, "E2195", {"start": v(-487.1, 57.1) * mm, "end": v(-486, 57.1) * mm});
            skLineSegment(sketch, "E2196", {"start": v(-487.1, 59.1) * mm, "end": v(-487.1, 57.1) * mm});
            skLineSegment(sketch, "E2197", {"start": v(-486, 59.1) * mm, "end": v(-487.1, 59.1) * mm});
            skLineSegment(sketch, "E2198", {"start": v(-486, 64.1) * mm, "end": v(-486, 59.1) * mm});
            skLineSegment(sketch, "E2199", {"start": v(-565.7, 64.1) * mm, "end": v(-486, 64.1) * mm});
            skLineSegment(sketch, "E2200", {"start": v(-565.7, 59.1) * mm, "end": v(-565.7, 64.1) * mm});
            skLineSegment(sketch, "E2201", {"start": v(-564.6, 59.1) * mm, "end": v(-565.7, 59.1) * mm});
            skLineSegment(sketch, "E2202", {"start": v(-564.6, 57.1) * mm, "end": v(-564.6, 59.1) * mm});
            skLineSegment(sketch, "E2203", {"start": v(-565.7, 57.1) * mm, "end": v(-564.6, 57.1) * mm});
            skLineSegment(sketch, "E2204", {"start": v(-565.7, 56.1) * mm, "end": v(-565.7, 57.1) * mm});
            skLineSegment(sketch, "E2205", {"start": v(-569.1, 56.1) * mm, "end": v(-565.7, 56.1) * mm});
            skLineSegment(sketch, "E2206", {"start": v(-569.1, 57.1) * mm, "end": v(-569.1, 56.1) * mm});
            skLineSegment(sketch, "E2207", {"start": v(-570.2, 57.1) * mm, "end": v(-569.1, 57.1) * mm});
            skLineSegment(sketch, "E2208", {"start": v(-570.2, 59.1) * mm, "end": v(-570.2, 57.1) * mm});
            skLineSegment(sketch, "E2209", {"start": v(-569.1, 59.1) * mm, "end": v(-570.2, 59.1) * mm});
            skLineSegment(sketch, "E2210", {"start": v(-569.1, 64.1) * mm, "end": v(-569.1, 59.1) * mm});
            skLineSegment(sketch, "E2211", {"start": v(-648.9, 64.1) * mm, "end": v(-569.1, 64.1) * mm});
            skLineSegment(sketch, "E2212", {"start": v(-648.9, 59.1) * mm, "end": v(-648.9, 64.1) * mm});
            skLineSegment(sketch, "E2213", {"start": v(-647.8, 59.1) * mm, "end": v(-648.9, 59.1) * mm});
            skLineSegment(sketch, "E2214", {"start": v(-647.8, 57.1) * mm, "end": v(-647.8, 59.1) * mm});
            skLineSegment(sketch, "E2215", {"start": v(-648.9, 57.1) * mm, "end": v(-647.8, 57.1) * mm});
            skLineSegment(sketch, "E2216", {"start": v(-648.9, 56.1) * mm, "end": v(-648.9, 57.1) * mm});
            skLineSegment(sketch, "E2217", {"start": v(-652.3, 56.1) * mm, "end": v(-648.9, 56.1) * mm});
            skLineSegment(sketch, "E2218", {"start": v(-652.3, 57.1) * mm, "end": v(-652.3, 56.1) * mm});
            skLineSegment(sketch, "E2219", {"start": v(-653.4, 57.1) * mm, "end": v(-652.3, 57.1) * mm});
            skLineSegment(sketch, "E2220", {"start": v(-653.4, 59.1) * mm, "end": v(-653.4, 57.1) * mm});
            skLineSegment(sketch, "E2221", {"start": v(-652.3, 59.1) * mm, "end": v(-653.4, 59.1) * mm});
            skLineSegment(sketch, "E2222", {"start": v(-652.3, 64.1) * mm, "end": v(-652.3, 59.1) * mm});
            skLineSegment(sketch, "E2223", {"start": v(-658.95, 64.1) * mm, "end": v(-652.3, 64.1) * mm});
            skLineSegment(sketch, "E2224", {"start": v(-658.95, 50.09) * mm, "end": v(-658.95, 64.1) * mm});
            skCircle(sketch, "E2225", {"center": v(-508.6, -101.23) * mm, "radius": 1.5 * mm});
            skLineSegment(sketch, "E2226", {"start": v(-731, -45.9) * mm, "end": v(-729, -45.9) * mm});
            skLineSegment(sketch, "E2227", {"start": v(-729, -45.9) * mm, "end": v(-729, -49.9) * mm});
            skLineSegment(sketch, "E2228", {"start": v(-729, -49.9) * mm, "end": v(-731, -49.9) * mm});
            skLineSegment(sketch, "E2229", {"start": v(-731, -49.9) * mm, "end": v(-731, -45.9) * mm});
            skLineSegment(sketch, "E2230", {"start": v(-713, -45.9) * mm, "end": v(-711, -45.9) * mm});
            skLineSegment(sketch, "E2231", {"start": v(-711, -45.9) * mm, "end": v(-711, -49.9) * mm});
            skLineSegment(sketch, "E2232", {"start": v(-711, -49.9) * mm, "end": v(-713, -49.9) * mm});
            skLineSegment(sketch, "E2233", {"start": v(-713, -49.9) * mm, "end": v(-713, -45.9) * mm});
            skLineSegment(sketch, "E2234", {"start": v(-570.4, -98.66) * mm, "end": v(-571.82, -100.08) * mm});
            skLineSegment(sketch, "E2235", {"start": v(-567.58, -101.49) * mm, "end": v(-570.4, -98.66) * mm});
            skLineSegment(sketch, "E2236", {"start": v(-569, -102.9) * mm, "end": v(-567.58, -101.49) * mm});
            skLineSegment(sketch, "E2237", {"start": v(-571.82, -100.08) * mm, "end": v(-569, -102.9) * mm});
            skLineSegment(sketch, "E2238", {"start": v(-619.85, -98.66) * mm, "end": v(-621.26, -100.08) * mm});
            skLineSegment(sketch, "E2239", {"start": v(-617.02, -101.49) * mm, "end": v(-619.85, -98.66) * mm});
            skLineSegment(sketch, "E2240", {"start": v(-618.44, -102.9) * mm, "end": v(-617.02, -101.49) * mm});
            skLineSegment(sketch, "E2241", {"start": v(-621.26, -100.08) * mm, "end": v(-618.44, -102.9) * mm});
            skLineSegment(sketch, "E2242", {"start": v(-649.46, -117.02) * mm, "end": v(-647.46, -117.02) * mm});
            skLineSegment(sketch, "E2243", {"start": v(-649.46, -113.02) * mm, "end": v(-649.46, -117.02) * mm});
            skLineSegment(sketch, "E2244", {"start": v(-647.46, -113.02) * mm, "end": v(-649.46, -113.02) * mm});
            skLineSegment(sketch, "E2245", {"start": v(-647.46, -117.02) * mm, "end": v(-647.46, -113.02) * mm});
            skLineSegment(sketch, "E2246", {"start": v(-649.46, -49.29) * mm, "end": v(-647.46, -49.29) * mm});
            skLineSegment(sketch, "E2247", {"start": v(-649.46, -45.29) * mm, "end": v(-649.46, -49.29) * mm});
            skLineSegment(sketch, "E2248", {"start": v(-647.46, -45.29) * mm, "end": v(-649.46, -45.29) * mm});
            skLineSegment(sketch, "E2249", {"start": v(-647.46, -49.29) * mm, "end": v(-647.46, -45.29) * mm});
            skLineSegment(sketch, "E2250", {"start": v(-561.92, -90.18) * mm, "end": v(-563.34, -91.6) * mm});
            skLineSegment(sketch, "E2251", {"start": v(-559.1, -93) * mm, "end": v(-561.92, -90.18) * mm});
            skLineSegment(sketch, "E2252", {"start": v(-560.51, -94.42) * mm, "end": v(-559.1, -93) * mm});
            skLineSegment(sketch, "E2253", {"start": v(-563.34, -91.6) * mm, "end": v(-560.51, -94.42) * mm});
            skLineSegment(sketch, "E2254", {"start": v(-611.36, -90.18) * mm, "end": v(-612.78, -91.6) * mm});
            skLineSegment(sketch, "E2255", {"start": v(-608.54, -93) * mm, "end": v(-611.36, -90.18) * mm});
            skLineSegment(sketch, "E2256", {"start": v(-609.95, -94.42) * mm, "end": v(-608.54, -93) * mm});
            skLineSegment(sketch, "E2257", {"start": v(-612.78, -91.6) * mm, "end": v(-609.95, -94.42) * mm});
            skLineSegment(sketch, "E2258", {"start": v(-661.46, -117.02) * mm, "end": v(-659.46, -117.02) * mm});
            skLineSegment(sketch, "E2259", {"start": v(-661.46, -113.02) * mm, "end": v(-661.46, -117.02) * mm});
            skLineSegment(sketch, "E2260", {"start": v(-659.46, -113.02) * mm, "end": v(-661.46, -113.02) * mm});
            skLineSegment(sketch, "E2261", {"start": v(-659.46, -117.02) * mm, "end": v(-659.46, -113.02) * mm});
            skLineSegment(sketch, "E2262", {"start": v(-661.46, -49.29) * mm, "end": v(-659.46, -49.29) * mm});
            skLineSegment(sketch, "E2263", {"start": v(-661.46, -45.29) * mm, "end": v(-661.46, -49.29) * mm});
            skLineSegment(sketch, "E2264", {"start": v(-659.46, -45.29) * mm, "end": v(-661.46, -45.29) * mm});
            skLineSegment(sketch, "E2265", {"start": v(-659.46, -49.29) * mm, "end": v(-659.46, -45.29) * mm});
            skLineSegment(sketch, "E2266", {"start": v(-631, 6.1) * mm, "end": v(-600.5, 6.1) * mm});
            skLineSegment(sketch, "E2267", {"start": v(-631, 32.6) * mm, "end": v(-631, 6.1) * mm});
            skLineSegment(sketch, "E2268", {"start": v(-631, 32.6) * mm, "end": v(-636.1, 32.6) * mm});
            skLineSegment(sketch, "E2269", {"start": v(-636.1, 32.6) * mm, "end": v(-636.1, 50.6) * mm});
            skLineSegment(sketch, "E2270", {"start": v(-636.1, 50.6) * mm, "end": v(-631, 50.6) * mm});
            skLineSegment(sketch, "E2271", {"start": v(-631, 59.1) * mm, "end": v(-631, 50.6) * mm});
            skLineSegment(sketch, "E2272", {"start": v(-587, 59.1) * mm, "end": v(-631, 59.1) * mm});
            skLineSegment(sketch, "E2273", {"start": v(-587, 50.6) * mm, "end": v(-587, 59.1) * mm});
            skLineSegment(sketch, "E2274", {"start": v(-587, 50.6) * mm, "end": v(-581.9, 50.6) * mm});
            skLineSegment(sketch, "E2275", {"start": v(-581.9, 50.6) * mm, "end": v(-581.9, 32.6) * mm});
            skLineSegment(sketch, "E2276", {"start": v(-581.9, 32.6) * mm, "end": v(-587, 32.6) * mm});
            skLineSegment(sketch, "E2277", {"start": v(-587, 14.1) * mm, "end": v(-587, 32.6) * mm});
            skLineSegment(sketch, "E2278", {"start": v(-600.5, 14.1) * mm, "end": v(-587, 14.1) * mm});
            skLineSegment(sketch, "E2279", {"start": v(-600.5, 6.1) * mm, "end": v(-600.5, 14.1) * mm});
            skLineSegment(sketch, "E2280", {"start": v(-659.46, 33.1) * mm, "end": v(-661.46, 33.1) * mm});
            skLineSegment(sketch, "E2281", {"start": v(-659.46, 29.1) * mm, "end": v(-659.46, 33.1) * mm});
            skLineSegment(sketch, "E2282", {"start": v(-661.46, 29.1) * mm, "end": v(-659.46, 29.1) * mm});
            skLineSegment(sketch, "E2283", {"start": v(-661.46, 33.1) * mm, "end": v(-661.46, 29.1) * mm});
            skLineSegment(sketch, "E2284", {"start": v(-649.46, 29.1) * mm, "end": v(-647.46, 29.1) * mm});
            skLineSegment(sketch, "E2285", {"start": v(-649.46, 33.1) * mm, "end": v(-649.46, 29.1) * mm});
            skLineSegment(sketch, "E2286", {"start": v(-647.46, 33.1) * mm, "end": v(-649.46, 33.1) * mm});
            skLineSegment(sketch, "E2287", {"start": v(-647.46, 29.1) * mm, "end": v(-647.46, 33.1) * mm});
            skCircle(sketch, "E2288", {"center": v(-616, -80.89) * mm, "radius": 1.6 * mm});
            skCircle(sketch, "E2289", {"center": v(-486.5, -205.8) * mm, "radius": 1.6 * mm});
            skCircle(sketch, "E2290", {"center": v(-545.15, -157.85) * mm, "radius": 1.6 * mm});
            skCircle(sketch, "E2291", {"center": v(-626.46, -109.6) * mm, "radius": 1.6 * mm});
            skCircle(sketch, "E2292", {"center": v(-558, -80.89) * mm, "radius": 1.6 * mm});
            skCircle(sketch, "E2293", {"center": v(-650.7, -205.8) * mm, "radius": 1.6 * mm});
            skCircle(sketch, "E2294", {"center": v(-627.43, -157.85) * mm, "radius": 1.6 * mm});
            skLineSegment(sketch, "E2295", {"start": v(-538, -163.9) * mm, "end": v(-527, -163.9) * mm});
            skLineSegment(sketch, "E2296", {"start": v(-538, 16.6) * mm, "end": v(-538, -163.9) * mm});
            skLineSegment(sketch, "E2297", {"start": v(-544, 16.6) * mm, "end": v(-538, 16.6) * mm});
            skLineSegment(sketch, "E2298", {"start": v(-544, 26.6) * mm, "end": v(-544, 16.6) * mm});
            skLineSegment(sketch, "E2299", {"start": v(-531, 26.6) * mm, "end": v(-544, 26.6) * mm});
            skLineSegment(sketch, "E2300", {"start": v(-531, 52.1) * mm, "end": v(-531, 26.6) * mm});
            skLineSegment(sketch, "E2301", {"start": v(-487, 52.1) * mm, "end": v(-531, 52.1) * mm});
            skLineSegment(sketch, "E2302", {"start": v(-487, 10.6) * mm, "end": v(-487, 52.1) * mm});
            skLineSegment(sketch, "E2303", {"start": v(-527, 10.6) * mm, "end": v(-487, 10.6) * mm});
            skLineSegment(sketch, "E2304", {"start": v(-527, -163.9) * mm, "end": v(-527, 10.6) * mm});
            skLineSegment(sketch, "E2305", {"start": v(-691, -163.9) * mm, "end": v(-680, -163.9) * mm});
            skLineSegment(sketch, "E2306", {"start": v(-691, 10.6) * mm, "end": v(-691, -163.9) * mm});
            skLineSegment(sketch, "E2307", {"start": v(-731, 10.6) * mm, "end": v(-691, 10.6) * mm});
            skLineSegment(sketch, "E2308", {"start": v(-731, 52.1) * mm, "end": v(-731, 10.6) * mm});
            skLineSegment(sketch, "E2309", {"start": v(-687, 52.1) * mm, "end": v(-731, 52.1) * mm});
            skLineSegment(sketch, "E2310", {"start": v(-687, 26.6) * mm, "end": v(-687, 52.1) * mm});
            skLineSegment(sketch, "E2311", {"start": v(-674, 26.6) * mm, "end": v(-687, 26.6) * mm});
            skLineSegment(sketch, "E2312", {"start": v(-674, 16.6) * mm, "end": v(-674, 26.6) * mm});
            skLineSegment(sketch, "E2313", {"start": v(-680, 16.6) * mm, "end": v(-674, 16.6) * mm});
            skLineSegment(sketch, "E2314", {"start": v(-680, -163.9) * mm, "end": v(-680, 16.6) * mm});
            skCircle(sketch, "E2315", {"center": v(-584.4, 26.1) * mm, "radius": 1.6 * mm});
            skCircle(sketch, "E2316", {"center": v(-633.6, 26.1) * mm, "radius": 1.6 * mm});
            skCircle(sketch, "E2317", {"center": v(-481.93, -100.92) * mm, "radius": 1.6 * mm});
            skCircle(sketch, "E2318", {"center": v(-508.76, -132.98) * mm, "radius": 1.6 * mm});
            skLineSegment(sketch, "E2319", {"start": v(-477.96, -207.8) * mm, "end": v(-479.96, -207.8) * mm});
            skLineSegment(sketch, "E2320", {"start": v(-479.96, -207.8) * mm, "end": v(-479.96, -203.81) * mm});
            skLineSegment(sketch, "E2321", {"start": v(-479.96, -203.81) * mm, "end": v(-477.96, -203.81) * mm});
            skLineSegment(sketch, "E2322", {"start": v(-477.96, -203.81) * mm, "end": v(-477.96, -207.8) * mm});
            skLineSegment(sketch, "E2323", {"start": v(-469.8, -207.8) * mm, "end": v(-471.8, -207.8) * mm});
            skLineSegment(sketch, "E2324", {"start": v(-471.8, -207.8) * mm, "end": v(-471.8, -203.81) * mm});
            skLineSegment(sketch, "E2325", {"start": v(-471.8, -203.81) * mm, "end": v(-469.8, -203.81) * mm});
            skLineSegment(sketch, "E2326", {"start": v(-469.8, -203.81) * mm, "end": v(-469.8, -207.8) * mm});
            skLineSegment(sketch, "E2327", {"start": v(1017.14, -168.58) * mm, "end": v(1017.14, -179.08) * mm});
            skArc(sketch, "E2328", {"start": v(1002.14, -194.08) * mm, "mid": v(1012.75, -189.68) * mm, "end": v(1017.14, -179.08) * mm});
            skCircle(sketch, "E2329", {"center": v(961.82, -149.73) * mm, "radius": 5 * mm});
            skLineSegment(sketch, "E2330", {"start": v(808.04, -166.08) * mm, "end": v(808.04, -161.08) * mm});
            skLineSegment(sketch, "E2331", {"start": v(848.04, -161.08) * mm, "end": v(848.04, -166.08) * mm});
            skLineSegment(sketch, "E2332", {"start": v(848.04, -166.08) * mm, "end": v(808.04, -166.08) * mm});
            skLineSegment(sketch, "E2333", {"start": v(797.54, -161.08) * mm, "end": v(808.04, -161.08) * mm});
            skLineSegment(sketch, "E2334", {"start": v(848.04, -161.08) * mm, "end": v(858.54, -161.08) * mm});
            skLineSegment(sketch, "E2335", {"start": v(927.04, -161.08) * mm, "end": v(927.04, -166.08) * mm});
            skLineSegment(sketch, "E2336", {"start": v(927.04, -166.08) * mm, "end": v(877.04, -166.08) * mm});
            skLineSegment(sketch, "E2337", {"start": v(877.04, -166.08) * mm, "end": v(877.04, -161.08) * mm});
            skLineSegment(sketch, "E2338", {"start": v(861.94, -161.08) * mm, "end": v(877.04, -161.08) * mm});
            skLineSegment(sketch, "E2339", {"start": v(927.04, -161.08) * mm, "end": v(942.14, -161.08) * mm});
            skLineSegment(sketch, "E2340", {"start": v(997.14, -182.88) * mm, "end": v(997.14, -181.78) * mm});
            skLineSegment(sketch, "E2341", {"start": v(999.14, -182.88) * mm, "end": v(997.14, -182.88) * mm});
            skLineSegment(sketch, "E2342", {"start": v(999.14, -181.78) * mm, "end": v(999.14, -182.88) * mm});
            skLineSegment(sketch, "E2343", {"start": v(999.14, -177.28) * mm, "end": v(999.14, -178.38) * mm});
            skLineSegment(sketch, "E2344", {"start": v(997.14, -177.28) * mm, "end": v(999.14, -177.28) * mm});
            skLineSegment(sketch, "E2345", {"start": v(997.14, -178.38) * mm, "end": v(997.14, -177.28) * mm});
            skLineSegment(sketch, "E2346", {"start": v(982.14, -106.58) * mm, "end": v(982.14, -105.48) * mm});
            skLineSegment(sketch, "E2347", {"start": v(982.14, -105.48) * mm, "end": v(980.14, -105.48) * mm});
            skLineSegment(sketch, "E2348", {"start": v(980.14, -105.48) * mm, "end": v(980.14, -106.58) * mm});
            skLineSegment(sketch, "E2349", {"start": v(980.14, -109.98) * mm, "end": v(980.14, -111.08) * mm});
            skLineSegment(sketch, "E2350", {"start": v(980.14, -111.08) * mm, "end": v(982.14, -111.08) * mm});
            skLineSegment(sketch, "E2351", {"start": v(982.14, -111.08) * mm, "end": v(982.14, -109.98) * mm});
            skLineSegment(sketch, "E2352", {"start": v(982.14, -132.18) * mm, "end": v(982.14, -131.08) * mm});
            skLineSegment(sketch, "E2353", {"start": v(982.14, -131.08) * mm, "end": v(980.14, -131.08) * mm});
            skLineSegment(sketch, "E2354", {"start": v(980.14, -131.08) * mm, "end": v(980.14, -132.18) * mm});
            skLineSegment(sketch, "E2355", {"start": v(980.14, -135.58) * mm, "end": v(980.14, -136.68) * mm});
            skLineSegment(sketch, "E2356", {"start": v(980.14, -136.68) * mm, "end": v(982.14, -136.68) * mm});
            skLineSegment(sketch, "E2357", {"start": v(982.14, -136.68) * mm, "end": v(982.14, -135.58) * mm});
            skLineSegment(sketch, "E2358", {"start": v(945.54, -156.08) * mm, "end": v(946.64, -156.08) * mm});
            skLineSegment(sketch, "E2359", {"start": v(946.64, -156.08) * mm, "end": v(946.64, -154.08) * mm});
            skLineSegment(sketch, "E2360", {"start": v(946.64, -154.08) * mm, "end": v(945.54, -154.08) * mm});
            skLineSegment(sketch, "E2361", {"start": v(942.14, -154.08) * mm, "end": v(941.04, -154.08) * mm});
            skLineSegment(sketch, "E2362", {"start": v(941.04, -154.08) * mm, "end": v(941.04, -156.08) * mm});
            skLineSegment(sketch, "E2363", {"start": v(941.04, -156.08) * mm, "end": v(942.14, -156.08) * mm});
            skLineSegment(sketch, "E2364", {"start": v(861.94, -156.08) * mm, "end": v(863.04, -156.08) * mm});
            skLineSegment(sketch, "E2365", {"start": v(863.04, -156.08) * mm, "end": v(863.04, -154.08) * mm});
            skLineSegment(sketch, "E2366", {"start": v(863.04, -154.08) * mm, "end": v(861.94, -154.08) * mm});
            skLineSegment(sketch, "E2367", {"start": v(858.54, -154.08) * mm, "end": v(857.44, -154.08) * mm});
            skLineSegment(sketch, "E2368", {"start": v(857.44, -154.08) * mm, "end": v(857.44, -156.08) * mm});
            skLineSegment(sketch, "E2369", {"start": v(857.44, -156.08) * mm, "end": v(858.54, -156.08) * mm});
            skLineSegment(sketch, "E2370", {"start": v(797.54, -156.08) * mm, "end": v(798.64, -156.08) * mm});
            skLineSegment(sketch, "E2371", {"start": v(798.64, -156.08) * mm, "end": v(798.64, -154.08) * mm});
            skLineSegment(sketch, "E2372", {"start": v(798.64, -154.08) * mm, "end": v(797.54, -154.08) * mm});
            skLineSegment(sketch, "E2373", {"start": v(794.14, -154.08) * mm, "end": v(793.04, -154.08) * mm});
            skLineSegment(sketch, "E2374", {"start": v(793.04, -154.08) * mm, "end": v(793.04, -156.08) * mm});
            skLineSegment(sketch, "E2375", {"start": v(793.04, -156.08) * mm, "end": v(794.14, -156.08) * mm});
            skLineSegment(sketch, "E2376", {"start": v(1000.14, -178.38) * mm, "end": v(1000.14, -181.78) * mm});
            skLineSegment(sketch, "E2377", {"start": v(1000.14, -181.78) * mm, "end": v(999.14, -181.78) * mm});
            skLineSegment(sketch, "E2378", {"start": v(997.14, -181.78) * mm, "end": v(992.14, -181.78) * mm});
            skLineSegment(sketch, "E2379", {"start": v(992.14, -178.38) * mm, "end": v(997.14, -178.38) * mm});
            skLineSegment(sketch, "E2380", {"start": v(999.14, -178.38) * mm, "end": v(1000.14, -178.38) * mm});
            skLineSegment(sketch, "E2381", {"start": v(858.54, -161.08) * mm, "end": v(858.54, -156.08) * mm});
            skLineSegment(sketch, "E2382", {"start": v(858.54, -154.08) * mm, "end": v(858.54, -153.08) * mm});
            skLineSegment(sketch, "E2383", {"start": v(858.54, -153.08) * mm, "end": v(861.94, -153.08) * mm});
            skLineSegment(sketch, "E2384", {"start": v(861.94, -153.08) * mm, "end": v(861.94, -154.08) * mm});
            skLineSegment(sketch, "E2385", {"start": v(861.94, -156.08) * mm, "end": v(861.94, -161.08) * mm});
            skLineSegment(sketch, "E2386", {"start": v(942.14, -161.08) * mm, "end": v(942.14, -156.08) * mm});
            skLineSegment(sketch, "E2387", {"start": v(942.14, -154.08) * mm, "end": v(942.14, -153.08) * mm});
            skLineSegment(sketch, "E2388", {"start": v(942.14, -153.08) * mm, "end": v(945.54, -153.08) * mm});
            skLineSegment(sketch, "E2389", {"start": v(945.54, -153.08) * mm, "end": v(945.54, -154.08) * mm});
            skLineSegment(sketch, "E2390", {"start": v(945.54, -156.08) * mm, "end": v(945.54, -161.08) * mm});
            skLineSegment(sketch, "E2391", {"start": v(945.54, -161.08) * mm, "end": v(950.44, -161.08) * mm});
            skLineSegment(sketch, "E2392", {"start": v(950.44, -166.08) * mm, "end": v(950.44, -161.08) * mm});
            skLineSegment(sketch, "E2393", {"start": v(992.14, -166.08) * mm, "end": v(950.44, -166.08) * mm});
            skLineSegment(sketch, "E2394", {"start": v(992.14, -178.38) * mm, "end": v(992.14, -166.08) * mm});
            skLineSegment(sketch, "E2395", {"start": v(992.14, -194.08) * mm, "end": v(992.14, -181.78) * mm});
            skLineSegment(sketch, "E2396", {"start": v(1002.14, -194.08) * mm, "end": v(992.14, -194.08) * mm});
            skArc(sketch, "E2397", {"start": v(1017.14, -168.58) * mm, "mid": v(1012.26, -152.93) * mm, "end": v(999.34, -142.84) * mm});
            skLineSegment(sketch, "E2398", {"start": v(999.34, -142.84) * mm, "end": v(992.14, -140.08) * mm});
            skLineSegment(sketch, "E2399", {"start": v(992.14, -140.08) * mm, "end": v(992.14, -137.68) * mm});
            skLineSegment(sketch, "E2400", {"start": v(992.14, -137.68) * mm, "end": v(987.14, -137.68) * mm});
            skLineSegment(sketch, "E2401", {"start": v(987.14, -137.68) * mm, "end": v(987.14, -135.58) * mm});
            skLineSegment(sketch, "E2402", {"start": v(987.14, -135.58) * mm, "end": v(982.14, -135.58) * mm});
            skLineSegment(sketch, "E2403", {"start": v(980.14, -135.58) * mm, "end": v(979.14, -135.58) * mm});
            skLineSegment(sketch, "E2404", {"start": v(979.14, -135.58) * mm, "end": v(979.14, -132.18) * mm});
            skLineSegment(sketch, "E2405", {"start": v(979.14, -132.18) * mm, "end": v(980.14, -132.18) * mm});
            skLineSegment(sketch, "E2406", {"start": v(982.14, -132.18) * mm, "end": v(987.14, -132.18) * mm});
            skLineSegment(sketch, "E2407", {"start": v(987.14, -132.18) * mm, "end": v(987.14, -109.98) * mm});
            skLineSegment(sketch, "E2408", {"start": v(987.14, -109.98) * mm, "end": v(982.14, -109.98) * mm});
            skLineSegment(sketch, "E2409", {"start": v(980.14, -109.98) * mm, "end": v(979.14, -109.98) * mm});
            skLineSegment(sketch, "E2410", {"start": v(979.14, -109.98) * mm, "end": v(979.14, -106.58) * mm});
            skLineSegment(sketch, "E2411", {"start": v(979.14, -106.58) * mm, "end": v(980.14, -106.58) * mm});
            skLineSegment(sketch, "E2412", {"start": v(982.14, -106.58) * mm, "end": v(987.14, -106.58) * mm});
            skLineSegment(sketch, "E2413", {"start": v(987.14, -106.58) * mm, "end": v(987.14, -97.08) * mm});
            skLineSegment(sketch, "E2414", {"start": v(987.14, -97.08) * mm, "end": v(816.3, -130.6) * mm});
            skArc(sketch, "E2415", {"start": v(816.3, -130.6) * mm, "mid": v(802.23, -135.66) * mm, "end": v(790.34, -144.72) * mm});
            skArc(sketch, "E2416", {"start": v(790.34, -144.72) * mm, "mid": v(786.75, -149.56) * mm, "end": v(784.52, -155.16) * mm});
            skArc(sketch, "E2417", {"start": v(784.52, -155.16) * mm, "mid": v(783.9, -158.1) * mm, "end": v(783.54, -161.08) * mm});
            skLineSegment(sketch, "E2418", {"start": v(783.54, -161.08) * mm, "end": v(794.14, -161.08) * mm});
            skLineSegment(sketch, "E2419", {"start": v(794.14, -161.08) * mm, "end": v(794.14, -156.08) * mm});
            skLineSegment(sketch, "E2420", {"start": v(794.14, -154.08) * mm, "end": v(794.14, -153.08) * mm});
            skLineSegment(sketch, "E2421", {"start": v(794.14, -153.08) * mm, "end": v(797.54, -153.08) * mm});
            skLineSegment(sketch, "E2422", {"start": v(797.54, -153.08) * mm, "end": v(797.54, -154.08) * mm});
            skLineSegment(sketch, "E2423", {"start": v(797.54, -156.08) * mm, "end": v(797.54, -161.08) * mm});
            skLineSegment(sketch, "E2424", {"start": v(877.26, -60.2) * mm, "end": v(877.26, -61.3) * mm});
            skLineSegment(sketch, "E2425", {"start": v(877.26, -61.3) * mm, "end": v(882.26, -61.3) * mm});
            skLineSegment(sketch, "E2426", {"start": v(882.26, -56) * mm, "end": v(882.26, -61.3) * mm});
            skLineSegment(sketch, "E2427", {"start": v(847.26, -56) * mm, "end": v(882.26, -56) * mm});
            skLineSegment(sketch, "E2428", {"start": v(847.26, -61.3) * mm, "end": v(847.26, -56) * mm});
            skLineSegment(sketch, "E2429", {"start": v(852.26, -61.3) * mm, "end": v(847.26, -61.3) * mm});
            skLineSegment(sketch, "E2430", {"start": v(852.26, -60.2) * mm, "end": v(852.26, -61.3) * mm});
            skLineSegment(sketch, "E2431", {"start": v(854.26, -60.2) * mm, "end": v(852.26, -60.2) * mm});
            skLineSegment(sketch, "E2432", {"start": v(854.26, -61.3) * mm, "end": v(854.26, -60.2) * mm});
            skLineSegment(sketch, "E2433", {"start": v(855.26, -61.3) * mm, "end": v(854.26, -61.3) * mm});
            skLineSegment(sketch, "E2434", {"start": v(855.26, -64.7) * mm, "end": v(855.26, -61.3) * mm});
            skLineSegment(sketch, "E2435", {"start": v(854.26, -64.7) * mm, "end": v(855.26, -64.7) * mm});
            skLineSegment(sketch, "E2436", {"start": v(854.26, -65.8) * mm, "end": v(854.26, -64.7) * mm});
            skLineSegment(sketch, "E2437", {"start": v(852.26, -65.8) * mm, "end": v(854.26, -65.8) * mm});
            skLineSegment(sketch, "E2438", {"start": v(852.26, -64.7) * mm, "end": v(852.26, -65.8) * mm});
            skLineSegment(sketch, "E2439", {"start": v(847.26, -64.7) * mm, "end": v(852.26, -64.7) * mm});
            skLineSegment(sketch, "E2440", {"start": v(847.26, -69) * mm, "end": v(847.26, -64.7) * mm});
            skLineSegment(sketch, "E2441", {"start": v(842.26, -69) * mm, "end": v(847.26, -69) * mm});
            skLineSegment(sketch, "E2442", {"start": v(842.26, -79) * mm, "end": v(842.26, -69) * mm});
            skLineSegment(sketch, "E2443", {"start": v(847.26, -79) * mm, "end": v(842.26, -79) * mm});
            skLineSegment(sketch, "E2444", {"start": v(847.26, -82) * mm, "end": v(847.26, -79) * mm});
            skLineSegment(sketch, "E2445", {"start": v(847.26, -82) * mm, "end": v(852.26, -82) * mm});
            skLineSegment(sketch, "E2446", {"start": v(852.26, -82) * mm, "end": v(852.26, -80.9) * mm});
            skLineSegment(sketch, "E2447", {"start": v(852.26, -80.9) * mm, "end": v(854.26, -80.9) * mm});
            skLineSegment(sketch, "E2448", {"start": v(854.26, -80.9) * mm, "end": v(854.26, -82) * mm});
            skLineSegment(sketch, "E2449", {"start": v(854.26, -82) * mm, "end": v(855.26, -82) * mm});
            skLineSegment(sketch, "E2450", {"start": v(855.26, -82) * mm, "end": v(855.26, -85.4) * mm});
            skLineSegment(sketch, "E2451", {"start": v(855.26, -85.4) * mm, "end": v(854.26, -85.4) * mm});
            skLineSegment(sketch, "E2452", {"start": v(854.26, -85.4) * mm, "end": v(854.26, -86.5) * mm});
            skLineSegment(sketch, "E2453", {"start": v(854.26, -86.5) * mm, "end": v(852.26, -86.5) * mm});
            skLineSegment(sketch, "E2454", {"start": v(852.26, -86.5) * mm, "end": v(852.26, -85.4) * mm});
            skLineSegment(sketch, "E2455", {"start": v(852.26, -85.4) * mm, "end": v(847.26, -85.4) * mm});
            skLineSegment(sketch, "E2456", {"start": v(847.26, -101) * mm, "end": v(847.26, -85.4) * mm});
            skLineSegment(sketch, "E2457", {"start": v(851.26, -101) * mm, "end": v(847.26, -101) * mm});
            skLineSegment(sketch, "E2458", {"start": v(851.26, -96) * mm, "end": v(851.26, -101) * mm});
            skLineSegment(sketch, "E2459", {"start": v(850.16, -96) * mm, "end": v(851.26, -96) * mm});
            skLineSegment(sketch, "E2460", {"start": v(850.16, -94) * mm, "end": v(850.16, -96) * mm});
            skLineSegment(sketch, "E2461", {"start": v(851.26, -94) * mm, "end": v(850.16, -94) * mm});
            skLineSegment(sketch, "E2462", {"start": v(851.26, -93) * mm, "end": v(851.26, -94) * mm});
            skLineSegment(sketch, "E2463", {"start": v(854.66, -93) * mm, "end": v(851.26, -93) * mm});
            skLineSegment(sketch, "E2464", {"start": v(854.66, -94) * mm, "end": v(854.66, -93) * mm});
            skLineSegment(sketch, "E2465", {"start": v(855.76, -94) * mm, "end": v(854.66, -94) * mm});
            skLineSegment(sketch, "E2466", {"start": v(855.76, -96) * mm, "end": v(855.76, -94) * mm});
            skLineSegment(sketch, "E2467", {"start": v(854.66, -96) * mm, "end": v(855.76, -96) * mm});
            skLineSegment(sketch, "E2468", {"start": v(854.66, -101) * mm, "end": v(854.66, -96) * mm});
            skLineSegment(sketch, "E2469", {"start": v(859.26, -101) * mm, "end": v(854.66, -101) * mm});
            skLineSegment(sketch, "E2470", {"start": v(859.26, -106) * mm, "end": v(859.26, -101) * mm});
            skLineSegment(sketch, "E2471", {"start": v(868.26, -106) * mm, "end": v(859.26, -106) * mm});
            skLineSegment(sketch, "E2472", {"start": v(868.26, -101) * mm, "end": v(868.26, -106) * mm});
            skLineSegment(sketch, "E2473", {"start": v(872.86, -101) * mm, "end": v(868.26, -101) * mm});
            skLineSegment(sketch, "E2474", {"start": v(872.86, -96) * mm, "end": v(872.86, -101) * mm});
            skLineSegment(sketch, "E2475", {"start": v(871.76, -96) * mm, "end": v(872.86, -96) * mm});
            skLineSegment(sketch, "E2476", {"start": v(871.76, -94) * mm, "end": v(871.76, -96) * mm});
            skLineSegment(sketch, "E2477", {"start": v(872.86, -94) * mm, "end": v(871.76, -94) * mm});
            skLineSegment(sketch, "E2478", {"start": v(872.86, -93) * mm, "end": v(872.86, -94) * mm});
            skLineSegment(sketch, "E2479", {"start": v(876.26, -93) * mm, "end": v(872.86, -93) * mm});
            skLineSegment(sketch, "E2480", {"start": v(876.26, -94) * mm, "end": v(876.26, -93) * mm});
            skLineSegment(sketch, "E2481", {"start": v(877.36, -94) * mm, "end": v(876.26, -94) * mm});
            skLineSegment(sketch, "E2482", {"start": v(877.36, -96) * mm, "end": v(877.36, -94) * mm});
            skLineSegment(sketch, "E2483", {"start": v(876.26, -96) * mm, "end": v(877.36, -96) * mm});
            skLineSegment(sketch, "E2484", {"start": v(876.26, -101) * mm, "end": v(876.26, -96) * mm});
            skLineSegment(sketch, "E2485", {"start": v(882.26, -101) * mm, "end": v(876.26, -101) * mm});
            skLineSegment(sketch, "E2486", {"start": v(882.26, -87.5) * mm, "end": v(882.26, -101) * mm});
            skLineSegment(sketch, "E2487", {"start": v(882.26, -87.5) * mm, "end": v(887.26, -87.5) * mm});
            skLineSegment(sketch, "E2488", {"start": v(887.26, -87.5) * mm, "end": v(887.26, -69.5) * mm});
            skLineSegment(sketch, "E2489", {"start": v(882.26, -69.5) * mm, "end": v(887.26, -69.5) * mm});
            skLineSegment(sketch, "E2490", {"start": v(882.26, -64.7) * mm, "end": v(882.26, -69.5) * mm});
            skLineSegment(sketch, "E2491", {"start": v(882.26, -64.7) * mm, "end": v(877.26, -64.7) * mm});
            skLineSegment(sketch, "E2492", {"start": v(877.26, -64.7) * mm, "end": v(877.26, -65.8) * mm});
            skLineSegment(sketch, "E2493", {"start": v(877.26, -65.8) * mm, "end": v(875.26, -65.8) * mm});
            skLineSegment(sketch, "E2494", {"start": v(875.26, -65.8) * mm, "end": v(875.26, -64.7) * mm});
            skLineSegment(sketch, "E2495", {"start": v(875.26, -64.7) * mm, "end": v(874.26, -64.7) * mm});
            skLineSegment(sketch, "E2496", {"start": v(874.26, -64.7) * mm, "end": v(874.26, -61.3) * mm});
            skLineSegment(sketch, "E2497", {"start": v(874.26, -61.3) * mm, "end": v(875.26, -61.3) * mm});
            skLineSegment(sketch, "E2498", {"start": v(875.26, -61.3) * mm, "end": v(875.26, -60.2) * mm});
            skLineSegment(sketch, "E2499", {"start": v(875.26, -60.2) * mm, "end": v(877.26, -60.2) * mm});
            skCircle(sketch, "E2500", {"center": v(-159.5, -192.15) * mm, "radius": 1.6 * mm});
            skCircle(sketch, "E2501", {"center": v(-454.5, -85.9) * mm, "radius": 1.6 * mm});
            skCircle(sketch, "E2502", {"center": v(-454.5, -192.15) * mm, "radius": 1.6 * mm});
            skCircle(sketch, "E2503", {"center": v(-159.5, -85.9) * mm, "radius": 1.6 * mm});
            skCircle(sketch, "E2504", {"center": v(-454.5, 20.35) * mm, "radius": 1.6 * mm});
            skCircle(sketch, "E2505", {"center": v(-159.5, 20.35) * mm, "radius": 1.6 * mm});
            skCircle(sketch, "E2506", {"center": v(-444.5, -227.9) * mm, "radius": 1.6 * mm});
            skCircle(sketch, "E2507", {"center": v(-169.5, -227.9) * mm, "radius": 1.6 * mm});
            skCircle(sketch, "E2508", {"center": v(-422.07, 40.35) * mm, "radius": 1.6 * mm});
            skCircle(sketch, "E2509", {"center": v(-191.93, 40.35) * mm, "radius": 1.6 * mm});
            skLineSegment(sketch, "E2510", {"start": v(-413.54, 17.1) * mm, "end": v(-421.98, 8.66) * mm});
            skLineSegment(sketch, "E2511", {"start": v(-200.44, 17.1) * mm, "end": v(-413.54, 17.1) * mm});
            skLineSegment(sketch, "E2512", {"start": v(-192, 8.66) * mm, "end": v(-200.44, 17.1) * mm});
            skLineSegment(sketch, "E2513", {"start": v(-192, -202.46) * mm, "end": v(-192, 8.66) * mm});
            skLineSegment(sketch, "E2514", {"start": v(-200.44, -210.9) * mm, "end": v(-192, -202.46) * mm});
            skLineSegment(sketch, "E2515", {"start": v(-413.54, -210.9) * mm, "end": v(-200.44, -210.9) * mm});
            skLineSegment(sketch, "E2516", {"start": v(-421.98, -202.46) * mm, "end": v(-413.54, -210.9) * mm});
            skLineSegment(sketch, "E2517", {"start": v(-421.98, 8.66) * mm, "end": v(-421.98, -202.46) * mm});
            skLineSegment(sketch, "E2518", {"start": v(-197.8, 59.1) * mm, "end": v(-196.7, 59.1) * mm});
            skLineSegment(sketch, "E2519", {"start": v(-196.7, 59.1) * mm, "end": v(-196.7, 57.1) * mm});
            skLineSegment(sketch, "E2520", {"start": v(-196.7, 57.1) * mm, "end": v(-197.8, 57.1) * mm});
            skLineSegment(sketch, "E2521", {"start": v(-201.2, 57.1) * mm, "end": v(-202.3, 57.1) * mm});
            skLineSegment(sketch, "E2522", {"start": v(-202.3, 57.1) * mm, "end": v(-202.3, 59.1) * mm});
            skLineSegment(sketch, "E2523", {"start": v(-202.3, 59.1) * mm, "end": v(-201.2, 59.1) * mm});
            skLineSegment(sketch, "E2524", {"start": v(-262.8, 59.1) * mm, "end": v(-261.7, 59.1) * mm});
            skLineSegment(sketch, "E2525", {"start": v(-261.7, 59.1) * mm, "end": v(-261.7, 57.1) * mm});
            skLineSegment(sketch, "E2526", {"start": v(-261.7, 57.1) * mm, "end": v(-262.8, 57.1) * mm});
            skLineSegment(sketch, "E2527", {"start": v(-266.2, 57.1) * mm, "end": v(-267.3, 57.1) * mm});
            skLineSegment(sketch, "E2528", {"start": v(-267.3, 57.1) * mm, "end": v(-267.3, 59.1) * mm});
            skLineSegment(sketch, "E2529", {"start": v(-267.3, 59.1) * mm, "end": v(-266.2, 59.1) * mm});
            skLineSegment(sketch, "E2530", {"start": v(-347.8, 59.1) * mm, "end": v(-346.7, 59.1) * mm});
            skLineSegment(sketch, "E2531", {"start": v(-346.7, 59.1) * mm, "end": v(-346.7, 57.1) * mm});
            skLineSegment(sketch, "E2532", {"start": v(-346.7, 57.1) * mm, "end": v(-347.8, 57.1) * mm});
            skLineSegment(sketch, "E2533", {"start": v(-351.2, 57.1) * mm, "end": v(-352.3, 57.1) * mm});
            skLineSegment(sketch, "E2534", {"start": v(-352.3, 57.1) * mm, "end": v(-352.3, 59.1) * mm});
            skLineSegment(sketch, "E2535", {"start": v(-352.3, 59.1) * mm, "end": v(-351.2, 59.1) * mm});
            skLineSegment(sketch, "E2536", {"start": v(-412.8, 59.1) * mm, "end": v(-411.7, 59.1) * mm});
            skLineSegment(sketch, "E2537", {"start": v(-411.7, 59.1) * mm, "end": v(-411.7, 57.1) * mm});
            skLineSegment(sketch, "E2538", {"start": v(-411.7, 57.1) * mm, "end": v(-412.8, 57.1) * mm});
            skLineSegment(sketch, "E2539", {"start": v(-416.2, 57.1) * mm, "end": v(-417.3, 57.1) * mm});
            skLineSegment(sketch, "E2540", {"start": v(-417.3, 57.1) * mm, "end": v(-417.3, 59.1) * mm});
            skLineSegment(sketch, "E2541", {"start": v(-417.3, 59.1) * mm, "end": v(-416.2, 59.1) * mm});
            skLineSegment(sketch, "E2542", {"start": v(-416.2, -230.9) * mm, "end": v(-417.3, -230.9) * mm});
            skLineSegment(sketch, "E2543", {"start": v(-417.3, -230.9) * mm, "end": v(-417.3, -228.9) * mm});
            skLineSegment(sketch, "E2544", {"start": v(-417.3, -228.9) * mm, "end": v(-416.2, -228.9) * mm});
            skLineSegment(sketch, "E2545", {"start": v(-412.8, -228.9) * mm, "end": v(-411.7, -228.9) * mm});
            skLineSegment(sketch, "E2546", {"start": v(-411.7, -228.9) * mm, "end": v(-411.7, -230.9) * mm});
            skLineSegment(sketch, "E2547", {"start": v(-411.7, -230.9) * mm, "end": v(-412.8, -230.9) * mm});
            skLineSegment(sketch, "E2548", {"start": v(-351.2, -230.9) * mm, "end": v(-352.3, -230.9) * mm});
            skLineSegment(sketch, "E2549", {"start": v(-352.3, -230.9) * mm, "end": v(-352.3, -228.9) * mm});
            skLineSegment(sketch, "E2550", {"start": v(-352.3, -228.9) * mm, "end": v(-351.2, -228.9) * mm});
            skLineSegment(sketch, "E2551", {"start": v(-347.8, -228.9) * mm, "end": v(-346.7, -228.9) * mm});
            skLineSegment(sketch, "E2552", {"start": v(-346.7, -228.9) * mm, "end": v(-346.7, -230.9) * mm});
            skLineSegment(sketch, "E2553", {"start": v(-346.7, -230.9) * mm, "end": v(-347.8, -230.9) * mm});
            skLineSegment(sketch, "E2554", {"start": v(-266.2, -230.9) * mm, "end": v(-267.3, -230.9) * mm});
            skLineSegment(sketch, "E2555", {"start": v(-267.3, -230.9) * mm, "end": v(-267.3, -228.9) * mm});
            skLineSegment(sketch, "E2556", {"start": v(-267.3, -228.9) * mm, "end": v(-266.2, -228.9) * mm});
            skLineSegment(sketch, "E2557", {"start": v(-262.8, -228.9) * mm, "end": v(-261.7, -228.9) * mm});
            skLineSegment(sketch, "E2558", {"start": v(-261.7, -228.9) * mm, "end": v(-261.7, -230.9) * mm});
            skLineSegment(sketch, "E2559", {"start": v(-261.7, -230.9) * mm, "end": v(-262.8, -230.9) * mm});
            skLineSegment(sketch, "E2560", {"start": v(-201.2, -230.9) * mm, "end": v(-202.3, -230.9) * mm});
            skLineSegment(sketch, "E2561", {"start": v(-202.3, -230.9) * mm, "end": v(-202.3, -228.9) * mm});
            skLineSegment(sketch, "E2562", {"start": v(-202.3, -228.9) * mm, "end": v(-201.2, -228.9) * mm});
            skLineSegment(sketch, "E2563", {"start": v(-197.8, -228.9) * mm, "end": v(-196.7, -228.9) * mm});
            skLineSegment(sketch, "E2564", {"start": v(-196.7, -228.9) * mm, "end": v(-196.7, -230.9) * mm});
            skLineSegment(sketch, "E2565", {"start": v(-196.7, -230.9) * mm, "end": v(-197.8, -230.9) * mm});
            skLineSegment(sketch, "E2566", {"start": v(-416.2, 64.1) * mm, "end": v(-416.2, 59.1) * mm});
            skLineSegment(sketch, "E2567", {"start": v(-416.2, 57.1) * mm, "end": v(-416.2, 56.1) * mm});
            skLineSegment(sketch, "E2568", {"start": v(-416.2, 56.1) * mm, "end": v(-412.8, 56.1) * mm});
            skLineSegment(sketch, "E2569", {"start": v(-412.8, 56.1) * mm, "end": v(-412.8, 57.1) * mm});
            skLineSegment(sketch, "E2570", {"start": v(-412.8, 59.1) * mm, "end": v(-412.8, 64.1) * mm});
            skLineSegment(sketch, "E2571", {"start": v(-412.8, 64.1) * mm, "end": v(-351.2, 64.1) * mm});
            skLineSegment(sketch, "E2572", {"start": v(-351.2, 64.1) * mm, "end": v(-351.2, 59.1) * mm});
            skLineSegment(sketch, "E2573", {"start": v(-351.2, 57.1) * mm, "end": v(-351.2, 56.1) * mm});
            skLineSegment(sketch, "E2574", {"start": v(-351.2, 56.1) * mm, "end": v(-347.8, 56.1) * mm});
            skLineSegment(sketch, "E2575", {"start": v(-347.8, 56.1) * mm, "end": v(-347.8, 57.1) * mm});
            skLineSegment(sketch, "E2576", {"start": v(-347.8, 59.1) * mm, "end": v(-347.8, 64.1) * mm});
            skLineSegment(sketch, "E2577", {"start": v(-347.8, 64.1) * mm, "end": v(-266.2, 64.1) * mm});
            skLineSegment(sketch, "E2578", {"start": v(-266.2, 64.1) * mm, "end": v(-266.2, 59.1) * mm});
            skLineSegment(sketch, "E2579", {"start": v(-266.2, 57.1) * mm, "end": v(-266.2, 56.1) * mm});
            skLineSegment(sketch, "E2580", {"start": v(-266.2, 56.1) * mm, "end": v(-262.8, 56.1) * mm});
            skLineSegment(sketch, "E2581", {"start": v(-262.8, 56.1) * mm, "end": v(-262.8, 57.1) * mm});
            skLineSegment(sketch, "E2582", {"start": v(-262.8, 59.1) * mm, "end": v(-262.8, 64.1) * mm});
            skLineSegment(sketch, "E2583", {"start": v(-262.8, 64.1) * mm, "end": v(-201.2, 64.1) * mm});
            skLineSegment(sketch, "E2584", {"start": v(-201.2, 64.1) * mm, "end": v(-201.2, 59.1) * mm});
            skLineSegment(sketch, "E2585", {"start": v(-201.2, 57.1) * mm, "end": v(-201.2, 56.1) * mm});
            skLineSegment(sketch, "E2586", {"start": v(-201.2, 56.1) * mm, "end": v(-197.8, 56.1) * mm});
            skLineSegment(sketch, "E2587", {"start": v(-197.8, 56.1) * mm, "end": v(-197.8, 57.1) * mm});
            skLineSegment(sketch, "E2588", {"start": v(-197.8, 59.1) * mm, "end": v(-197.8, 64.1) * mm});
            skLineSegment(sketch, "E2589", {"start": v(-197.8, 64.1) * mm, "end": v(-157, 64.1) * mm});
            skLineSegment(sketch, "E2590", {"start": v(-157, 64.1) * mm, "end": v(-157, -235.9) * mm});
            skLineSegment(sketch, "E2591", {"start": v(-157, -235.9) * mm, "end": v(-197.8, -235.9) * mm});
            skLineSegment(sketch, "E2592", {"start": v(-197.8, -235.9) * mm, "end": v(-197.8, -230.9) * mm});
            skLineSegment(sketch, "E2593", {"start": v(-197.8, -228.9) * mm, "end": v(-197.8, -227.9) * mm});
            skLineSegment(sketch, "E2594", {"start": v(-197.8, -227.9) * mm, "end": v(-201.2, -227.9) * mm});
            skLineSegment(sketch, "E2595", {"start": v(-201.2, -227.9) * mm, "end": v(-201.2, -228.9) * mm});
            skLineSegment(sketch, "E2596", {"start": v(-201.2, -230.9) * mm, "end": v(-201.2, -235.9) * mm});
            skLineSegment(sketch, "E2597", {"start": v(-201.2, -235.9) * mm, "end": v(-262.8, -235.9) * mm});
            skLineSegment(sketch, "E2598", {"start": v(-262.8, -235.9) * mm, "end": v(-262.8, -230.9) * mm});
            skLineSegment(sketch, "E2599", {"start": v(-262.8, -228.9) * mm, "end": v(-262.8, -227.9) * mm});
            skLineSegment(sketch, "E2600", {"start": v(-262.8, -227.9) * mm, "end": v(-266.2, -227.9) * mm});
            skLineSegment(sketch, "E2601", {"start": v(-266.2, -227.9) * mm, "end": v(-266.2, -228.9) * mm});
            skLineSegment(sketch, "E2602", {"start": v(-266.2, -230.9) * mm, "end": v(-266.2, -235.9) * mm});
            skLineSegment(sketch, "E2603", {"start": v(-266.2, -235.9) * mm, "end": v(-347.8, -235.9) * mm});
            skLineSegment(sketch, "E2604", {"start": v(-347.8, -235.9) * mm, "end": v(-347.8, -230.9) * mm});
            skLineSegment(sketch, "E2605", {"start": v(-347.8, -228.9) * mm, "end": v(-347.8, -227.9) * mm});
            skLineSegment(sketch, "E2606", {"start": v(-347.8, -227.9) * mm, "end": v(-351.2, -227.9) * mm});
            skLineSegment(sketch, "E2607", {"start": v(-351.2, -227.9) * mm, "end": v(-351.2, -228.9) * mm});
            skLineSegment(sketch, "E2608", {"start": v(-351.2, -230.9) * mm, "end": v(-351.2, -235.9) * mm});
            skLineSegment(sketch, "E2609", {"start": v(-351.2, -235.9) * mm, "end": v(-412.8, -235.9) * mm});
            skLineSegment(sketch, "E2610", {"start": v(-412.8, -235.9) * mm, "end": v(-412.8, -230.9) * mm});
            skLineSegment(sketch, "E2611", {"start": v(-412.8, -228.9) * mm, "end": v(-412.8, -227.9) * mm});
            skLineSegment(sketch, "E2612", {"start": v(-412.8, -227.9) * mm, "end": v(-416.2, -227.9) * mm});
            skLineSegment(sketch, "E2613", {"start": v(-416.2, -227.9) * mm, "end": v(-416.2, -228.9) * mm});
            skLineSegment(sketch, "E2614", {"start": v(-416.2, -230.9) * mm, "end": v(-416.2, -235.9) * mm});
            skLineSegment(sketch, "E2615", {"start": v(-416.2, -235.9) * mm, "end": v(-457, -235.9) * mm});
            skLineSegment(sketch, "E2616", {"start": v(-457, -235.9) * mm, "end": v(-457, 64.1) * mm});
            skLineSegment(sketch, "E2617", {"start": v(-457, 64.1) * mm, "end": v(-416.2, 64.1) * mm});
            skCircle(sketch, "E2618", {"center": v(-307.19, 7.36) * mm, "radius": 1.2 * mm});
            skCircle(sketch, "E2619", {"center": v(-202.9, 7.36) * mm, "radius": 1.2 * mm});
            skCircle(sketch, "E2620", {"center": v(-411.49, 7.36) * mm, "radius": 1.2 * mm});
            skCircle(sketch, "E2621", {"center": v(-411.49, -201.24) * mm, "radius": 1.2 * mm});
            skCircle(sketch, "E2622", {"center": v(-202.9, -201.24) * mm, "radius": 1.2 * mm});
            skCircle(sketch, "E2623", {"center": v(-407.43, -16.39) * mm, "radius": 2 * mm});
            skCircle(sketch, "E2624", {"center": v(-407.49, -176.99) * mm, "radius": 2 * mm});
            skCircle(sketch, "E2625", {"center": v(-206.89, -176.99) * mm, "radius": 2 * mm});
            skCircle(sketch, "E2626", {"center": v(-206.94, -16.39) * mm, "radius": 2 * mm});
            skArc(sketch, "E2627", {"start": v(-334.35, -107.31) * mm, "mid": v(-333.97, -108.48) * mm, "end": v(-332.85, -108.98) * mm});
            skArc(sketch, "E2628", {"start": v(-332.07, -98.63) * mm, "mid": v(-333.08, -99.02) * mm, "end": v(-333.57, -99.99) * mm});
            skArc(sketch, "E2629", {"start": v(-203.98, -209.12) * mm, "mid": v(-307.19, -202.04) * mm, "end": v(-410.39, -209.16) * mm});
            skArc(sketch, "E2630", {"start": v(-203.98, -209.12) * mm, "mid": v(-197.66, -207.23) * mm, "end": v(-194.93, -201.24) * mm});
            skLineSegment(sketch, "E2631", {"start": v(-194.93, 7.36) * mm, "end": v(-194.93, -201.24) * mm});
            skArc(sketch, "E2632", {"start": v(-194.93, 7.36) * mm, "mid": v(-197.26, 12.99) * mm, "end": v(-202.89, 15.32) * mm});
            skLineSegment(sketch, "E2633", {"start": v(-411.49, 15.36) * mm, "end": v(-202.89, 15.32) * mm});
            skArc(sketch, "E2634", {"start": v(-411.49, 15.36) * mm, "mid": v(-417.15, 13.02) * mm, "end": v(-419.49, 7.36) * mm});
            skLineSegment(sketch, "E2635", {"start": v(-419.49, -201.24) * mm, "end": v(-419.49, 7.36) * mm});
            skArc(sketch, "E2636", {"start": v(-419.49, -201.24) * mm, "mid": v(-416.74, -207.27) * mm, "end": v(-410.39, -209.16) * mm});
            skLineSegment(sketch, "E2637", {"start": v(-311.13, -142.8) * mm, "end": v(-296.72, -142.8) * mm});
            skLineSegment(sketch, "E2638", {"start": v(-346.92, -142.8) * mm, "end": v(-311.13, -142.8) * mm});
            skLineSegment(sketch, "E2639", {"start": v(-346.12, -135.2) * mm, "end": v(-346.92, -142.8) * mm});
            skLineSegment(sketch, "E2640", {"start": v(-346, -134.45) * mm, "end": v(-346.12, -135.2) * mm});
            skLineSegment(sketch, "E2641", {"start": v(-345.8, -133.84) * mm, "end": v(-346, -134.45) * mm});
            skLineSegment(sketch, "E2642", {"start": v(-345.52, -133.3) * mm, "end": v(-345.8, -133.84) * mm});
            skLineSegment(sketch, "E2643", {"start": v(-345.15, -132.85) * mm, "end": v(-345.52, -133.3) * mm});
            skLineSegment(sketch, "E2644", {"start": v(-344.8, -132.57) * mm, "end": v(-345.15, -132.85) * mm});
            skLineSegment(sketch, "E2645", {"start": v(-344.47, -132.38) * mm, "end": v(-344.8, -132.57) * mm});
            skLineSegment(sketch, "E2646", {"start": v(-344.08, -132.23) * mm, "end": v(-344.47, -132.38) * mm});
            skLineSegment(sketch, "E2647", {"start": v(-343.7, -132.18) * mm, "end": v(-344.08, -132.23) * mm});
            skLineSegment(sketch, "E2648", {"start": v(-295.6, -132.18) * mm, "end": v(-343.7, -132.18) * mm});
            skLineSegment(sketch, "E2649", {"start": v(-293.84, -132.09) * mm, "end": v(-295.6, -132.18) * mm});
            skLineSegment(sketch, "E2650", {"start": v(-292.18, -131.83) * mm, "end": v(-293.84, -132.09) * mm});
            skLineSegment(sketch, "E2651", {"start": v(-290.24, -131.25) * mm, "end": v(-292.18, -131.83) * mm});
            skLineSegment(sketch, "E2652", {"start": v(-288.5, -130.4) * mm, "end": v(-290.24, -131.25) * mm});
            skLineSegment(sketch, "E2653", {"start": v(-286.95, -129.3) * mm, "end": v(-288.5, -130.4) * mm});
            skLineSegment(sketch, "E2654", {"start": v(-285.7, -128.05) * mm, "end": v(-286.95, -129.3) * mm});
            skLineSegment(sketch, "E2655", {"start": v(-284.6, -126.55) * mm, "end": v(-285.7, -128.05) * mm});
            skLineSegment(sketch, "E2656", {"start": v(-283.62, -124.76) * mm, "end": v(-284.6, -126.55) * mm});
            skLineSegment(sketch, "E2657", {"start": v(-282.8, -122.66) * mm, "end": v(-283.62, -124.76) * mm});
            skLineSegment(sketch, "E2658", {"start": v(-282.15, -120.12) * mm, "end": v(-282.8, -122.66) * mm});
            skLineSegment(sketch, "E2659", {"start": v(-281.71, -117.25) * mm, "end": v(-282.15, -120.12) * mm});
            skLineSegment(sketch, "E2660", {"start": v(-278.76, -89.22) * mm, "end": v(-281.71, -117.25) * mm});
            skLineSegment(sketch, "E2661", {"start": v(-278.59, -86.63) * mm, "end": v(-278.76, -89.22) * mm});
            skLineSegment(sketch, "E2662", {"start": v(-278.66, -84.3) * mm, "end": v(-278.59, -86.63) * mm});
            skLineSegment(sketch, "E2663", {"start": v(-279, -82.03) * mm, "end": v(-278.66, -84.3) * mm});
            skLineSegment(sketch, "E2664", {"start": v(-279.59, -80.13) * mm, "end": v(-279, -82.03) * mm});
            skLineSegment(sketch, "E2665", {"start": v(-280.4, -78.54) * mm, "end": v(-279.59, -80.13) * mm});
            skLineSegment(sketch, "E2666", {"start": v(-281.42, -77.22) * mm, "end": v(-280.4, -78.54) * mm});
            skLineSegment(sketch, "E2667", {"start": v(-282.53, -76.23) * mm, "end": v(-281.42, -77.22) * mm});
            skLineSegment(sketch, "E2668", {"start": v(-283.85, -75.44) * mm, "end": v(-282.53, -76.23) * mm});
            skLineSegment(sketch, "E2669", {"start": v(-285.4, -74.84) * mm, "end": v(-283.85, -75.44) * mm});
            skLineSegment(sketch, "E2670", {"start": v(-287.34, -74.43) * mm, "end": v(-285.4, -74.84) * mm});
            skLineSegment(sketch, "E2671", {"start": v(-289.5, -74.3) * mm, "end": v(-287.34, -74.43) * mm});
            skLineSegment(sketch, "E2672", {"start": v(-303.8, -74.3) * mm, "end": v(-289.5, -74.3) * mm});
            skLineSegment(sketch, "E2673", {"start": v(-337.6, -74.3) * mm, "end": v(-303.8, -74.3) * mm});
            skLineSegment(sketch, "E2674", {"start": v(-337.72, -74.29) * mm, "end": v(-337.6, -74.3) * mm});
            skLineSegment(sketch, "E2675", {"start": v(-338.03, -74.22) * mm, "end": v(-337.72, -74.29) * mm});
            skLineSegment(sketch, "E2676", {"start": v(-338.32, -74.1) * mm, "end": v(-338.03, -74.22) * mm});
            skLineSegment(sketch, "E2677", {"start": v(-338.63, -73.9) * mm, "end": v(-338.32, -74.1) * mm});
            skLineSegment(sketch, "E2678", {"start": v(-338.92, -73.6) * mm, "end": v(-338.63, -73.9) * mm});
            skLineSegment(sketch, "E2679", {"start": v(-339.17, -73.18) * mm, "end": v(-338.92, -73.6) * mm});
            skLineSegment(sketch, "E2680", {"start": v(-339.33, -72.64) * mm, "end": v(-339.17, -73.18) * mm});
            skLineSegment(sketch, "E2681", {"start": v(-339.4, -72.03) * mm, "end": v(-339.33, -72.64) * mm});
            skLineSegment(sketch, "E2682", {"start": v(-339.37, -71.28) * mm, "end": v(-339.4, -72.03) * mm});
            skLineSegment(sketch, "E2683", {"start": v(-338.57, -63.67) * mm, "end": v(-339.37, -71.28) * mm});
            skLineSegment(sketch, "E2684", {"start": v(-288.37, -63.67) * mm, "end": v(-338.57, -63.67) * mm});
            skLineSegment(sketch, "E2685", {"start": v(-285.54, -63.79) * mm, "end": v(-288.37, -63.67) * mm});
            skLineSegment(sketch, "E2686", {"start": v(-282.93, -64.12) * mm, "end": v(-285.54, -63.79) * mm});
            skLineSegment(sketch, "E2687", {"start": v(-280.26, -64.76) * mm, "end": v(-282.93, -64.12) * mm});
            skLineSegment(sketch, "E2688", {"start": v(-277.88, -65.65) * mm, "end": v(-280.26, -64.76) * mm});
            skLineSegment(sketch, "E2689", {"start": v(-275.98, -66.65) * mm, "end": v(-277.88, -65.65) * mm});
            skLineSegment(sketch, "E2690", {"start": v(-274.27, -67.84) * mm, "end": v(-275.98, -66.65) * mm});
            skLineSegment(sketch, "E2691", {"start": v(-272.76, -69.22) * mm, "end": v(-274.27, -67.84) * mm});
            skLineSegment(sketch, "E2692", {"start": v(-271.42, -70.8) * mm, "end": v(-272.76, -69.22) * mm});
            skLineSegment(sketch, "E2693", {"start": v(-270.27, -72.62) * mm, "end": v(-271.42, -70.8) * mm});
            skLineSegment(sketch, "E2694", {"start": v(-269.3, -74.66) * mm, "end": v(-270.27, -72.62) * mm});
            skLineSegment(sketch, "E2695", {"start": v(-268.52, -76.96) * mm, "end": v(-269.3, -74.66) * mm});
            skLineSegment(sketch, "E2696", {"start": v(-267.96, -79.53) * mm, "end": v(-268.52, -76.96) * mm});
            skLineSegment(sketch, "E2697", {"start": v(-267.63, -82.4) * mm, "end": v(-267.96, -79.53) * mm});
            skLineSegment(sketch, "E2698", {"start": v(-267.57, -85.73) * mm, "end": v(-267.63, -82.4) * mm});
            skLineSegment(sketch, "E2699", {"start": v(-267.8, -89.22) * mm, "end": v(-267.57, -85.73) * mm});
            skLineSegment(sketch, "E2700", {"start": v(-270.76, -117.25) * mm, "end": v(-267.8, -89.22) * mm});
            skLineSegment(sketch, "E2701", {"start": v(-271.23, -120.56) * mm, "end": v(-270.76, -117.25) * mm});
            skLineSegment(sketch, "E2702", {"start": v(-271.93, -123.72) * mm, "end": v(-271.23, -120.56) * mm});
            skLineSegment(sketch, "E2703", {"start": v(-272.93, -126.85) * mm, "end": v(-271.93, -123.72) * mm});
            skLineSegment(sketch, "E2704", {"start": v(-274.15, -129.67) * mm, "end": v(-272.93, -126.85) * mm});
            skLineSegment(sketch, "E2705", {"start": v(-275.57, -132.2) * mm, "end": v(-274.15, -129.67) * mm});
            skLineSegment(sketch, "E2706", {"start": v(-277.18, -134.43) * mm, "end": v(-275.57, -132.2) * mm});
            skLineSegment(sketch, "E2707", {"start": v(-278.99, -136.39) * mm, "end": v(-277.18, -134.43) * mm});
            skLineSegment(sketch, "E2708", {"start": v(-280.98, -138.1) * mm, "end": v(-278.99, -136.39) * mm});
            skLineSegment(sketch, "E2709", {"start": v(-283.18, -139.54) * mm, "end": v(-280.98, -138.1) * mm});
            skLineSegment(sketch, "E2710", {"start": v(-285.6, -140.74) * mm, "end": v(-283.18, -139.54) * mm});
            skLineSegment(sketch, "E2711", {"start": v(-288.24, -141.67) * mm, "end": v(-285.6, -140.74) * mm});
            skLineSegment(sketch, "E2712", {"start": v(-290.83, -142.29) * mm, "end": v(-288.24, -141.67) * mm});
            skLineSegment(sketch, "E2713", {"start": v(-293.67, -142.67) * mm, "end": v(-290.83, -142.29) * mm});
            skLineSegment(sketch, "E2714", {"start": v(-296.72, -142.8) * mm, "end": v(-293.67, -142.67) * mm});
            skLineSegment(sketch, "E2715", {"start": v(-306.37, -98.63) * mm, "end": v(-332.07, -98.63) * mm});
            skLineSegment(sketch, "E2716", {"start": v(-307.47, -108.98) * mm, "end": v(-306.37, -98.63) * mm});
            skLineSegment(sketch, "E2717", {"start": v(-332.85, -108.98) * mm, "end": v(-307.47, -108.98) * mm});
            skLineSegment(sketch, "E2718", {"start": v(-333.57, -99.99) * mm, "end": v(-334.35, -107.31) * mm});
            skLineSegment(sketch, "E2719", {"start": v(-404.89, -181.19) * mm, "end": v(-410.09, -181.19) * mm});
            skLineSegment(sketch, "E2720", {"start": v(-404.89, -182.19) * mm, "end": v(-404.89, -181.19) * mm});
            skLineSegment(sketch, "E2721", {"start": v(-410.09, -182.19) * mm, "end": v(-404.89, -182.19) * mm});
            skLineSegment(sketch, "E2722", {"start": v(-410.09, -181.19) * mm, "end": v(-410.09, -182.19) * mm});
            skLineSegment(sketch, "E2723", {"start": v(-410.09, -173.29) * mm, "end": v(-404.89, -173.29) * mm});
            skLineSegment(sketch, "E2724", {"start": v(-410.09, -172.29) * mm, "end": v(-410.09, -173.29) * mm});
            skLineSegment(sketch, "E2725", {"start": v(-404.89, -172.29) * mm, "end": v(-410.09, -172.29) * mm});
            skLineSegment(sketch, "E2726", {"start": v(-404.89, -173.29) * mm, "end": v(-404.89, -172.29) * mm});
            skLineSegment(sketch, "E2727", {"start": v(-410.03, -20.59) * mm, "end": v(-410.03, -21.59) * mm});
            skLineSegment(sketch, "E2728", {"start": v(-404.83, -20.59) * mm, "end": v(-410.03, -20.59) * mm});
            skLineSegment(sketch, "E2729", {"start": v(-404.83, -21.59) * mm, "end": v(-404.83, -20.59) * mm});
            skLineSegment(sketch, "E2730", {"start": v(-410.03, -21.59) * mm, "end": v(-404.83, -21.59) * mm});
            skLineSegment(sketch, "E2731", {"start": v(-410.03, -11.69) * mm, "end": v(-410.03, -12.69) * mm});
            skLineSegment(sketch, "E2732", {"start": v(-404.83, -11.69) * mm, "end": v(-410.03, -11.69) * mm});
            skLineSegment(sketch, "E2733", {"start": v(-404.83, -12.69) * mm, "end": v(-404.83, -11.69) * mm});
            skLineSegment(sketch, "E2734", {"start": v(-410.03, -12.69) * mm, "end": v(-404.83, -12.69) * mm});
            skLineSegment(sketch, "E2735", {"start": v(-204.34, -11.69) * mm, "end": v(-209.54, -11.69) * mm});
            skLineSegment(sketch, "E2736", {"start": v(-204.34, -12.69) * mm, "end": v(-204.34, -11.69) * mm});
            skLineSegment(sketch, "E2737", {"start": v(-209.54, -12.69) * mm, "end": v(-204.34, -12.69) * mm});
            skLineSegment(sketch, "E2738", {"start": v(-209.54, -11.69) * mm, "end": v(-209.54, -12.69) * mm});
            skLineSegment(sketch, "E2739", {"start": v(-209.54, -21.59) * mm, "end": v(-204.34, -21.59) * mm});
            skLineSegment(sketch, "E2740", {"start": v(-209.54, -20.59) * mm, "end": v(-209.54, -21.59) * mm});
            skLineSegment(sketch, "E2741", {"start": v(-204.34, -20.59) * mm, "end": v(-209.54, -20.59) * mm});
            skLineSegment(sketch, "E2742", {"start": v(-204.34, -21.59) * mm, "end": v(-204.34, -20.59) * mm});
            skLineSegment(sketch, "E2743", {"start": v(-209.49, -173.29) * mm, "end": v(-204.29, -173.29) * mm});
            skLineSegment(sketch, "E2744", {"start": v(-209.49, -172.29) * mm, "end": v(-209.49, -173.29) * mm});
            skLineSegment(sketch, "E2745", {"start": v(-204.29, -172.29) * mm, "end": v(-209.49, -172.29) * mm});
            skLineSegment(sketch, "E2746", {"start": v(-204.29, -173.29) * mm, "end": v(-204.29, -172.29) * mm});
            skLineSegment(sketch, "E2747", {"start": v(-204.29, -181.19) * mm, "end": v(-209.49, -181.19) * mm});
            skLineSegment(sketch, "E2748", {"start": v(-204.29, -182.19) * mm, "end": v(-204.29, -181.19) * mm});
            skLineSegment(sketch, "E2749", {"start": v(-209.49, -182.19) * mm, "end": v(-204.29, -182.19) * mm});
            skLineSegment(sketch, "E2750", {"start": v(-209.49, -181.19) * mm, "end": v(-209.49, -182.19) * mm});
            skLineSegment(sketch, "E2751", {"start": v(-254.93, 104.28) * mm, "end": v(-254.93, 94.42) * mm});
            skArc(sketch, "E2752", {"start": v(-274.73, 114.9) * mm, "mid": v(-273.13, 113.3) * mm, "end": v(-271.53, 114.9) * mm});
            skCircle(sketch, "E2753", {"center": v(-273.13, 107.4) * mm, "radius": 5.3 * mm});
            skArc(sketch, "E2754", {"start": v(-271.53, 99.9) * mm, "mid": v(-273.13, 101.5) * mm, "end": v(-274.73, 99.9) * mm});
            skArc(sketch, "E2755", {"start": v(-283.63, 109) * mm, "mid": v(-285.23, 107.4) * mm, "end": v(-283.63, 105.8) * mm});
            skArc(sketch, "E2756", {"start": v(-262.63, 105.8) * mm, "mid": v(-261.03, 107.4) * mm, "end": v(-262.63, 109) * mm});
            skLineSegment(sketch, "E2757", {"start": v(-265.63, 109) * mm, "end": v(-262.63, 109) * mm});
            skLineSegment(sketch, "E2758", {"start": v(-262.63, 105.8) * mm, "end": v(-265.63, 105.8) * mm});
            skArc(sketch, "E2759", {"start": v(-274.73, 96.9) * mm, "mid": v(-273.13, 95.3) * mm, "end": v(-271.53, 96.9) * mm});
            skLineSegment(sketch, "E2760", {"start": v(-271.53, 99.9) * mm, "end": v(-271.53, 96.9) * mm});
            skLineSegment(sketch, "E2761", {"start": v(-274.73, 96.9) * mm, "end": v(-274.73, 99.9) * mm});
            skArc(sketch, "E2762", {"start": v(-271.53, 117.9) * mm, "mid": v(-273.13, 119.5) * mm, "end": v(-274.73, 117.9) * mm});
            skLineSegment(sketch, "E2763", {"start": v(-274.73, 114.9) * mm, "end": v(-274.73, 117.9) * mm});
            skLineSegment(sketch, "E2764", {"start": v(-271.53, 117.9) * mm, "end": v(-271.53, 114.9) * mm});
            skLineSegment(sketch, "E2765", {"start": v(-280.63, 105.8) * mm, "end": v(-283.63, 105.8) * mm});
            skLineSegment(sketch, "E2766", {"start": v(-283.63, 109) * mm, "end": v(-280.63, 109) * mm});
            skArc(sketch, "E2767", {"start": v(-265.63, 109) * mm, "mid": v(-267.23, 107.4) * mm, "end": v(-265.63, 105.8) * mm});
            skArc(sketch, "E2768", {"start": v(-254.93, 104.28) * mm, "mid": v(-273.13, 122.48) * mm, "end": v(-291.33, 104.28) * mm});
            skLineSegment(sketch, "E2769", {"start": v(-291.33, 94.42) * mm, "end": v(-291.33, 104.28) * mm});
            skLineSegment(sketch, "E2770", {"start": v(-284.83, 94.42) * mm, "end": v(-291.33, 94.42) * mm});
            skLineSegment(sketch, "E2771", {"start": v(-284.83, 94.42) * mm, "end": v(-284.83, 99.42) * mm});
            skLineSegment(sketch, "E2772", {"start": v(-284.83, 99.42) * mm, "end": v(-285.93, 99.42) * mm});
            skLineSegment(sketch, "E2773", {"start": v(-285.93, 99.42) * mm, "end": v(-285.93, 101.42) * mm});
            skLineSegment(sketch, "E2774", {"start": v(-285.93, 101.42) * mm, "end": v(-284.83, 101.42) * mm});
            skLineSegment(sketch, "E2775", {"start": v(-284.83, 101.42) * mm, "end": v(-284.83, 102.42) * mm});
            skLineSegment(sketch, "E2776", {"start": v(-284.83, 102.42) * mm, "end": v(-281.43, 102.42) * mm});
            skLineSegment(sketch, "E2777", {"start": v(-281.43, 102.42) * mm, "end": v(-281.43, 101.42) * mm});
            skLineSegment(sketch, "E2778", {"start": v(-281.43, 101.42) * mm, "end": v(-280.33, 101.42) * mm});
            skLineSegment(sketch, "E2779", {"start": v(-280.33, 101.42) * mm, "end": v(-280.33, 99.42) * mm});
            skLineSegment(sketch, "E2780", {"start": v(-280.33, 99.42) * mm, "end": v(-281.43, 99.42) * mm});
            skLineSegment(sketch, "E2781", {"start": v(-281.43, 99.42) * mm, "end": v(-281.43, 94.42) * mm});
            skLineSegment(sketch, "E2782", {"start": v(-264.83, 94.42) * mm, "end": v(-281.43, 94.42) * mm});
            skLineSegment(sketch, "E2783", {"start": v(-264.83, 94.42) * mm, "end": v(-264.83, 99.42) * mm});
            skLineSegment(sketch, "E2784", {"start": v(-264.83, 99.42) * mm, "end": v(-265.93, 99.42) * mm});
            skLineSegment(sketch, "E2785", {"start": v(-265.93, 99.42) * mm, "end": v(-265.93, 101.42) * mm});
            skLineSegment(sketch, "E2786", {"start": v(-265.93, 101.42) * mm, "end": v(-264.83, 101.42) * mm});
            skLineSegment(sketch, "E2787", {"start": v(-264.83, 101.42) * mm, "end": v(-264.83, 102.42) * mm});
            skLineSegment(sketch, "E2788", {"start": v(-264.83, 102.42) * mm, "end": v(-261.43, 102.42) * mm});
            skLineSegment(sketch, "E2789", {"start": v(-261.43, 102.42) * mm, "end": v(-261.43, 101.42) * mm});
            skLineSegment(sketch, "E2790", {"start": v(-261.43, 101.42) * mm, "end": v(-260.33, 101.42) * mm});
            skLineSegment(sketch, "E2791", {"start": v(-260.33, 101.42) * mm, "end": v(-260.33, 99.42) * mm});
            skLineSegment(sketch, "E2792", {"start": v(-260.33, 99.42) * mm, "end": v(-261.43, 99.42) * mm});
            skLineSegment(sketch, "E2793", {"start": v(-261.43, 99.42) * mm, "end": v(-261.43, 94.42) * mm});
            skLineSegment(sketch, "E2794", {"start": v(-254.93, 94.42) * mm, "end": v(-261.43, 94.42) * mm});
            skArc(sketch, "E2795", {"start": v(-280.63, 105.8) * mm, "mid": v(-279.03, 107.4) * mm, "end": v(-280.63, 109) * mm});
            skLineSegment(sketch, "E2796", {"start": v(-517.01, -208.22) * mm, "end": v(-515.72, -213.05) * mm});
            skCircle(sketch, "E2797", {"center": v(-563.66, -223.3) * mm, "radius": 1.6 * mm});
            skCircle(sketch, "E2798", {"center": v(-534.68, -215.54) * mm, "radius": 1.6 * mm});
            skArc(sketch, "E2799", {"start": v(-505.47, -215.1) * mm, "mid": v(-504.39, -214.22) * mm, "end": v(-504.22, -212.84) * mm});
            skArc(sketch, "E2800", {"start": v(-506.95, -202.65) * mm, "mid": v(-507.79, -201.54) * mm, "end": v(-509.16, -201.32) * mm});
            skArc(sketch, "E2801", {"start": v(-532.36, -222.2) * mm, "mid": v(-533.37, -223.2) * mm, "end": v(-532.36, -224.2) * mm});
            skArc(sketch, "E2802", {"start": v(-537, -206.88) * mm, "mid": v(-537.38, -208.25) * mm, "end": v(-536, -208.6) * mm});
            skArc(sketch, "E2803", {"start": v(-516.3, -185.3) * mm, "mid": v(-517.52, -186.74) * mm, "end": v(-517.63, -188.63) * mm});
            skArc(sketch, "E2804", {"start": v(-510.3, -187.45) * mm, "mid": v(-510.73, -187.77) * mm, "end": v(-510.8, -188.3) * mm});
            skArc(sketch, "E2805", {"start": v(-506.46, -230.32) * mm, "mid": v(-505.42, -231.9) * mm, "end": v(-503.64, -232.55) * mm});
            skArc(sketch, "E2806", {"start": v(-500.37, -227.2) * mm, "mid": v(-500.05, -227.61) * mm, "end": v(-499.53, -227.68) * mm});
            skArc(sketch, "E2807", {"start": v(-507.8, -225.32) * mm, "mid": v(-507.99, -225.07) * mm, "end": v(-508.3, -225.03) * mm});
            skArc(sketch, "E2808", {"start": v(-516.58, -194.13) * mm, "mid": v(-516.33, -193.94) * mm, "end": v(-516.3, -193.63) * mm});
            skArc(sketch, "E2809", {"start": v(-501.83, -221.76) * mm, "mid": v(-504.51, -218.35) * mm, "end": v(-508.83, -217.95) * mm});
            skArc(sketch, "E2810", {"start": v(-513.5, -200.53) * mm, "mid": v(-509.96, -198.02) * mm, "end": v(-509.34, -193.73) * mm});
            skLineSegment(sketch, "E2811", {"start": v(-510.8, -188.3) * mm, "end": v(-509.34, -193.73) * mm});
            skLineSegment(sketch, "E2812", {"start": v(-510.3, -187.45) * mm, "end": v(-502.76, -185.43) * mm});
            skLineSegment(sketch, "E2813", {"start": v(-502.76, -185.43) * mm, "end": v(-503.96, -180.96) * mm});
            skLineSegment(sketch, "E2814", {"start": v(-503.96, -180.96) * mm, "end": v(-507.65, -180.73) * mm});
            skLineSegment(sketch, "E2815", {"start": v(-507.65, -180.73) * mm, "end": v(-507.39, -181.7) * mm});
            skLineSegment(sketch, "E2816", {"start": v(-507.39, -181.7) * mm, "end": v(-512.8, -183.15) * mm});
            skLineSegment(sketch, "E2817", {"start": v(-512.8, -183.15) * mm, "end": v(-516.3, -185.3) * mm});
            skLineSegment(sketch, "E2818", {"start": v(-517.63, -188.63) * mm, "end": v(-516.3, -193.63) * mm});
            skLineSegment(sketch, "E2819", {"start": v(-516.58, -194.13) * mm, "end": v(-527.11, -196.95) * mm});
            skLineSegment(sketch, "E2820", {"start": v(-542.17, -202.8) * mm, "end": v(-527.11, -196.95) * mm});
            skLineSegment(sketch, "E2821", {"start": v(-542.17, -202.8) * mm, "end": v(-580.29, -223.55) * mm});
            skLineSegment(sketch, "E2822", {"start": v(-580.29, -223.55) * mm, "end": v(-579.88, -225.07) * mm});
            skLineSegment(sketch, "E2823", {"start": v(-579.88, -225.07) * mm, "end": v(-576.02, -224.03) * mm});
            skLineSegment(sketch, "E2824", {"start": v(-576.02, -224.03) * mm, "end": v(-574.72, -228.86) * mm});
            skLineSegment(sketch, "E2825", {"start": v(-574.72, -228.86) * mm, "end": v(-578.59, -229.9) * mm});
            skLineSegment(sketch, "E2826", {"start": v(-578.59, -229.9) * mm, "end": v(-578.18, -231.41) * mm});
            skLineSegment(sketch, "E2827", {"start": v(-578.18, -231.41) * mm, "end": v(-534.8, -230.33) * mm});
            skLineSegment(sketch, "E2828", {"start": v(-518.85, -227.86) * mm, "end": v(-534.8, -230.33) * mm});
            skLineSegment(sketch, "E2829", {"start": v(-508.3, -225.03) * mm, "end": v(-518.85, -227.86) * mm});
            skLineSegment(sketch, "E2830", {"start": v(-507.8, -225.32) * mm, "end": v(-506.46, -230.32) * mm});
            skLineSegment(sketch, "E2831", {"start": v(-503.64, -232.55) * mm, "end": v(-499.53, -232.65) * mm});
            skLineSegment(sketch, "E2832", {"start": v(-499.53, -232.65) * mm, "end": v(-494.12, -231.2) * mm});
            skLineSegment(sketch, "E2833", {"start": v(-494.12, -231.2) * mm, "end": v(-493.86, -232.17) * mm});
            skLineSegment(sketch, "E2834", {"start": v(-493.86, -232.17) * mm, "end": v(-490.79, -230.14) * mm});
            skLineSegment(sketch, "E2835", {"start": v(-490.79, -230.14) * mm, "end": v(-491.99, -225.66) * mm});
            skLineSegment(sketch, "E2836", {"start": v(-491.99, -225.66) * mm, "end": v(-499.53, -227.68) * mm});
            skLineSegment(sketch, "E2837", {"start": v(-501.83, -221.76) * mm, "end": v(-500.37, -227.2) * mm});
            skLineSegment(sketch, "E2838", {"start": v(-528.02, -224.16) * mm, "end": v(-508.83, -217.95) * mm});
            skArc(sketch, "E2839", {"start": v(-528.28, -224.18) * mm, "mid": v(-528.15, -224.18) * mm, "end": v(-528.02, -224.16) * mm});
            skLineSegment(sketch, "E2840", {"start": v(-528.28, -224.18) * mm, "end": v(-532.36, -224.2) * mm});
            skLineSegment(sketch, "E2841", {"start": v(-528.61, -222.25) * mm, "end": v(-532.36, -222.2) * mm});
            skLineSegment(sketch, "E2842", {"start": v(-505.47, -215.1) * mm, "end": v(-528.61, -222.25) * mm});
            skLineSegment(sketch, "E2843", {"start": v(-504.22, -212.84) * mm, "end": v(-506.95, -202.65) * mm});
            skLineSegment(sketch, "E2844", {"start": v(-532.78, -206.7) * mm, "end": v(-509.16, -201.32) * mm});
            skLineSegment(sketch, "E2845", {"start": v(-532.78, -206.7) * mm, "end": v(-536, -208.6) * mm});
            skLineSegment(sketch, "E2846", {"start": v(-533.45, -204.86) * mm, "end": v(-537, -206.88) * mm});
            skArc(sketch, "E2847", {"start": v(-533.22, -204.75) * mm, "mid": v(-533.34, -204.8) * mm, "end": v(-533.45, -204.86) * mm});
            skLineSegment(sketch, "E2848", {"start": v(-513.5, -200.53) * mm, "end": v(-533.22, -204.75) * mm});
            skLineSegment(sketch, "E2849", {"start": v(-526.67, -210.8) * mm, "end": v(-517.01, -208.22) * mm});
            skLineSegment(sketch, "E2850", {"start": v(-515.72, -213.05) * mm, "end": v(-525.38, -215.64) * mm});
            skLineSegment(sketch, "E2851", {"start": v(-525.38, -215.64) * mm, "end": v(-526.67, -210.8) * mm});
            skLineSegment(sketch, "E2852", {"start": v(-543.42, -215.3) * mm, "end": v(-542.13, -220.12) * mm});
            skLineSegment(sketch, "E2853", {"start": v(-557.27, -224.18) * mm, "end": v(-542.13, -220.12) * mm});
            skLineSegment(sketch, "E2854", {"start": v(-557.27, -224.18) * mm, "end": v(-558.56, -219.35) * mm});
            skLineSegment(sketch, "E2855", {"start": v(-543.42, -215.3) * mm, "end": v(-558.56, -219.35) * mm});
            skLineSegment(sketch, "E2856", {"start": v(893.87, -205.8) * mm, "end": v(875.67, -205.8) * mm});
            skLineSegment(sketch, "E2857", {"start": v(905.43, -196.62) * mm, "end": v(906.38, -196.07) * mm});
            skLineSegment(sketch, "E2858", {"start": v(909.33, -194.37) * mm, "end": v(910.28, -193.82) * mm});
            skLineSegment(sketch, "E2859", {"start": v(911.28, -195.55) * mm, "end": v(910.33, -196.1) * mm});
            skLineSegment(sketch, "E2860", {"start": v(907.38, -197.8) * mm, "end": v(906.43, -198.35) * mm});
            skLineSegment(sketch, "E2861", {"start": v(907.88, -198.67) * mm, "end": v(910.83, -196.97) * mm});
            skLineSegment(sketch, "E2862", {"start": v(907.38, -197.8) * mm, "end": v(907.88, -198.67) * mm});
            skLineSegment(sketch, "E2863", {"start": v(905.43, -196.62) * mm, "end": v(906.43, -198.35) * mm});
            skLineSegment(sketch, "E2864", {"start": v(903.88, -191.74) * mm, "end": v(906.38, -196.07) * mm});
            skLineSegment(sketch, "E2865", {"start": v(897.56, -195.39) * mm, "end": v(903.88, -191.74) * mm});
            skLineSegment(sketch, "E2866", {"start": v(895.06, -191.06) * mm, "end": v(897.56, -195.39) * mm});
            skLineSegment(sketch, "E2867", {"start": v(875.67, -202.25) * mm, "end": v(895.06, -191.06) * mm});
            skLineSegment(sketch, "E2868", {"start": v(875.67, -205.8) * mm, "end": v(875.67, -202.25) * mm});
            skLineSegment(sketch, "E2869", {"start": v(893.87, -200.8) * mm, "end": v(893.87, -205.8) * mm});
            skLineSegment(sketch, "E2870", {"start": v(893.87, -200.8) * mm, "end": v(892.77, -200.8) * mm});
            skLineSegment(sketch, "E2871", {"start": v(892.77, -200.8) * mm, "end": v(892.77, -198.8) * mm});
            skLineSegment(sketch, "E2872", {"start": v(892.77, -198.8) * mm, "end": v(893.87, -198.8) * mm});
            skLineSegment(sketch, "E2873", {"start": v(893.87, -197.8) * mm, "end": v(893.87, -198.8) * mm});
            skLineSegment(sketch, "E2874", {"start": v(897.27, -197.8) * mm, "end": v(893.87, -197.8) * mm});
            skLineSegment(sketch, "E2875", {"start": v(897.27, -198.8) * mm, "end": v(897.27, -197.8) * mm});
            skLineSegment(sketch, "E2876", {"start": v(897.27, -198.8) * mm, "end": v(898.37, -198.8) * mm});
            skLineSegment(sketch, "E2877", {"start": v(898.37, -198.8) * mm, "end": v(898.37, -200.8) * mm});
            skLineSegment(sketch, "E2878", {"start": v(898.37, -200.8) * mm, "end": v(897.27, -200.8) * mm});
            skLineSegment(sketch, "E2879", {"start": v(897.27, -205.8) * mm, "end": v(897.27, -200.8) * mm});
            skLineSegment(sketch, "E2880", {"start": v(925.67, -205.8) * mm, "end": v(897.27, -205.8) * mm});
            skLineSegment(sketch, "E2881", {"start": v(925.67, -193.6) * mm, "end": v(925.67, -205.8) * mm});
            skLineSegment(sketch, "E2882", {"start": v(920.67, -193.6) * mm, "end": v(925.67, -193.6) * mm});
            skLineSegment(sketch, "E2883", {"start": v(920.67, -193.6) * mm, "end": v(920.67, -194.7) * mm});
            skLineSegment(sketch, "E2884", {"start": v(920.67, -194.7) * mm, "end": v(918.67, -194.7) * mm});
            skLineSegment(sketch, "E2885", {"start": v(918.67, -194.7) * mm, "end": v(918.67, -193.6) * mm});
            skLineSegment(sketch, "E2886", {"start": v(917.67, -193.6) * mm, "end": v(918.67, -193.6) * mm});
            skLineSegment(sketch, "E2887", {"start": v(917.67, -190.2) * mm, "end": v(917.67, -193.6) * mm});
            skLineSegment(sketch, "E2888", {"start": v(918.67, -190.2) * mm, "end": v(917.67, -190.2) * mm});
            skLineSegment(sketch, "E2889", {"start": v(918.67, -190.2) * mm, "end": v(918.67, -189.1) * mm});
            skLineSegment(sketch, "E2890", {"start": v(918.67, -189.1) * mm, "end": v(920.67, -189.1) * mm});
            skLineSegment(sketch, "E2891", {"start": v(920.67, -189.1) * mm, "end": v(920.67, -190.2) * mm});
            skLineSegment(sketch, "E2892", {"start": v(925.67, -190.2) * mm, "end": v(920.67, -190.2) * mm});
            skLineSegment(sketch, "E2893", {"start": v(925.67, -175.8) * mm, "end": v(925.67, -190.2) * mm});
            skLineSegment(sketch, "E2894", {"start": v(921.47, -175.8) * mm, "end": v(925.67, -175.8) * mm});
            skLineSegment(sketch, "E2895", {"start": v(911.51, -181.56) * mm, "end": v(921.47, -175.8) * mm});
            skLineSegment(sketch, "E2896", {"start": v(914.01, -185.89) * mm, "end": v(911.51, -181.56) * mm});
            skLineSegment(sketch, "E2897", {"start": v(906.83, -190.04) * mm, "end": v(914.01, -185.89) * mm});
            skLineSegment(sketch, "E2898", {"start": v(909.33, -194.37) * mm, "end": v(906.83, -190.04) * mm});
            skLineSegment(sketch, "E2899", {"start": v(911.28, -195.55) * mm, "end": v(910.28, -193.82) * mm});
            skLineSegment(sketch, "E2900", {"start": v(910.83, -196.97) * mm, "end": v(910.33, -196.1) * mm});
            skCircle(sketch, "E2901", {"center": v(-531.87, -146.93) * mm, "radius": 3.5 * mm});
            skCircle(sketch, "E2902", {"center": v(-531.87, -146.93) * mm, "radius": 1.65 * mm});
            skCircle(sketch, "E2903", {"center": v(-531.87, -138.93) * mm, "radius": 3.5 * mm});
            skCircle(sketch, "E2904", {"center": v(-531.87, -138.93) * mm, "radius": 1.65 * mm});
            skCircle(sketch, "E2905", {"center": v(-531.87, -129.93) * mm, "radius": 3.5 * mm});
            skCircle(sketch, "E2906", {"center": v(-531.87, -129.93) * mm, "radius": 1.65 * mm});
            skCircle(sketch, "E2907", {"center": v(-531.87, -121.93) * mm, "radius": 3.5 * mm});
            skCircle(sketch, "E2908", {"center": v(-531.87, -121.93) * mm, "radius": 1.65 * mm});
            skCircle(sketch, "E2909", {"center": v(-531.87, -113.93) * mm, "radius": 3.5 * mm});
            skCircle(sketch, "E2910", {"center": v(-531.87, -113.93) * mm, "radius": 1.65 * mm});
            skCircle(sketch, "E2911", {"center": v(-531.87, -104.93) * mm, "radius": 3.5 * mm});
            skCircle(sketch, "E2912", {"center": v(-531.87, -104.93) * mm, "radius": 1.65 * mm});
            skCircle(sketch, "E2913", {"center": v(-531.87, -96.93) * mm, "radius": 3.5 * mm});
            skCircle(sketch, "E2914", {"center": v(-531.87, -96.93) * mm, "radius": 1.65 * mm});
            skCircle(sketch, "E2915", {"center": v(-531.87, -71.93) * mm, "radius": 3.5 * mm});
            skCircle(sketch, "E2916", {"center": v(-531.87, -71.93) * mm, "radius": 1.65 * mm});
            skCircle(sketch, "E2917", {"center": v(-531.87, -54.93) * mm, "radius": 3.5 * mm});
            skCircle(sketch, "E2918", {"center": v(-531.87, -54.93) * mm, "radius": 1.65 * mm});
            skCircle(sketch, "E2919", {"center": v(-531.87, -63.93) * mm, "radius": 3.5 * mm});
            skCircle(sketch, "E2920", {"center": v(-531.87, -63.93) * mm, "radius": 1.65 * mm});
            skCircle(sketch, "E2921", {"center": v(-531.87, -88.93) * mm, "radius": 3.5 * mm});
            skCircle(sketch, "E2922", {"center": v(-531.87, -88.93) * mm, "radius": 1.65 * mm});
            skCircle(sketch, "E2923", {"center": v(-531.87, -79.93) * mm, "radius": 3.5 * mm});
            skCircle(sketch, "E2924", {"center": v(-531.87, -79.93) * mm, "radius": 1.65 * mm});
            skCircle(sketch, "E2925", {"center": v(-531.87, -46.93) * mm, "radius": 3.5 * mm});
            skCircle(sketch, "E2926", {"center": v(-531.87, -46.93) * mm, "radius": 1.65 * mm});
            skCircle(sketch, "E2927", {"center": v(-531.87, -38.93) * mm, "radius": 3.5 * mm});
            skCircle(sketch, "E2928", {"center": v(-531.87, -38.93) * mm, "radius": 1.65 * mm});
            skCircle(sketch, "E2929", {"center": v(-531.87, -30.93) * mm, "radius": 3.5 * mm});
            skCircle(sketch, "E2930", {"center": v(-531.87, -30.93) * mm, "radius": 1.65 * mm});
            skCircle(sketch, "E2931", {"center": v(-531.87, -22.93) * mm, "radius": 3.5 * mm});
            skCircle(sketch, "E2932", {"center": v(-531.87, -22.93) * mm, "radius": 1.65 * mm});
            skLineSegment(sketch, "E2933", {"start": v(-616.5, 24.42) * mm, "end": v(-616.5, 23.32) * mm});
            skLineSegment(sketch, "E2934", {"start": v(-616.5, 24.42) * mm, "end": v(-621.5, 24.42) * mm});
            skLineSegment(sketch, "E2935", {"start": v(-621.5, 24.42) * mm, "end": v(-621.5, 18.12) * mm});
            skLineSegment(sketch, "E2936", {"start": v(-621.5, 18.12) * mm, "end": v(-591.5, 18.12) * mm});
            skLineSegment(sketch, "E2937", {"start": v(-591.5, 18.12) * mm, "end": v(-591.5, 48.12) * mm});
            skLineSegment(sketch, "E2938", {"start": v(-591.5, 48.12) * mm, "end": v(-621.5, 48.12) * mm});
            skLineSegment(sketch, "E2939", {"start": v(-621.5, 48.12) * mm, "end": v(-621.5, 41.82) * mm});
            skLineSegment(sketch, "E2940", {"start": v(-621.5, 41.82) * mm, "end": v(-616.5, 41.82) * mm});
            skLineSegment(sketch, "E2941", {"start": v(-616.5, 42.92) * mm, "end": v(-616.5, 41.82) * mm});
            skLineSegment(sketch, "E2942", {"start": v(-614.5, 42.92) * mm, "end": v(-616.5, 42.92) * mm});
            skLineSegment(sketch, "E2943", {"start": v(-614.5, 41.82) * mm, "end": v(-614.5, 42.92) * mm});
            skLineSegment(sketch, "E2944", {"start": v(-614.5, 41.82) * mm, "end": v(-613.5, 41.82) * mm});
            skLineSegment(sketch, "E2945", {"start": v(-613.5, 41.82) * mm, "end": v(-613.5, 38.42) * mm});
            skLineSegment(sketch, "E2946", {"start": v(-613.5, 38.42) * mm, "end": v(-614.5, 38.42) * mm});
            skLineSegment(sketch, "E2947", {"start": v(-614.5, 37.32) * mm, "end": v(-614.5, 38.42) * mm});
            skLineSegment(sketch, "E2948", {"start": v(-616.5, 37.32) * mm, "end": v(-614.5, 37.32) * mm});
            skLineSegment(sketch, "E2949", {"start": v(-616.5, 38.42) * mm, "end": v(-616.5, 37.32) * mm});
            skLineSegment(sketch, "E2950", {"start": v(-616.5, 38.42) * mm, "end": v(-621.5, 38.42) * mm});
            skLineSegment(sketch, "E2951", {"start": v(-621.5, 38.42) * mm, "end": v(-621.5, 27.82) * mm});
            skLineSegment(sketch, "E2952", {"start": v(-621.5, 27.82) * mm, "end": v(-616.5, 27.82) * mm});
            skLineSegment(sketch, "E2953", {"start": v(-616.5, 28.92) * mm, "end": v(-616.5, 27.82) * mm});
            skLineSegment(sketch, "E2954", {"start": v(-614.5, 28.92) * mm, "end": v(-616.5, 28.92) * mm});
            skLineSegment(sketch, "E2955", {"start": v(-614.5, 27.82) * mm, "end": v(-614.5, 28.92) * mm});
            skLineSegment(sketch, "E2956", {"start": v(-614.5, 27.82) * mm, "end": v(-613.5, 27.82) * mm});
            skLineSegment(sketch, "E2957", {"start": v(-613.5, 27.82) * mm, "end": v(-613.5, 24.42) * mm});
            skLineSegment(sketch, "E2958", {"start": v(-613.5, 24.42) * mm, "end": v(-614.5, 24.42) * mm});
            skLineSegment(sketch, "E2959", {"start": v(-614.5, 23.32) * mm, "end": v(-614.5, 24.42) * mm});
            skLineSegment(sketch, "E2960", {"start": v(-616.5, 23.32) * mm, "end": v(-614.5, 23.32) * mm});
            skCircle(sketch, "E2961", {"center": v(-594, 26.12) * mm, "radius": 1.6 * mm});
            skCircle(sketch, "E2962", {"center": v(-594, 40.12) * mm, "radius": 1.6 * mm});
            skLineSegment(sketch, "E2963", {"start": v(-716.5, 24.42) * mm, "end": v(-716.5, 23.32) * mm});
            skLineSegment(sketch, "E2964", {"start": v(-716.5, 24.42) * mm, "end": v(-721.5, 24.42) * mm});
            skLineSegment(sketch, "E2965", {"start": v(-721.5, 24.42) * mm, "end": v(-721.5, 18.12) * mm});
            skLineSegment(sketch, "E2966", {"start": v(-721.5, 18.12) * mm, "end": v(-691.5, 18.12) * mm});
            skLineSegment(sketch, "E2967", {"start": v(-691.5, 18.12) * mm, "end": v(-691.5, 48.12) * mm});
            skLineSegment(sketch, "E2968", {"start": v(-691.5, 48.12) * mm, "end": v(-721.5, 48.12) * mm});
            skLineSegment(sketch, "E2969", {"start": v(-721.5, 48.12) * mm, "end": v(-721.5, 41.82) * mm});
            skLineSegment(sketch, "E2970", {"start": v(-721.5, 41.82) * mm, "end": v(-716.5, 41.82) * mm});
            skLineSegment(sketch, "E2971", {"start": v(-716.5, 42.92) * mm, "end": v(-716.5, 41.82) * mm});
            skLineSegment(sketch, "E2972", {"start": v(-714.5, 42.92) * mm, "end": v(-716.5, 42.92) * mm});
            skLineSegment(sketch, "E2973", {"start": v(-714.5, 41.82) * mm, "end": v(-714.5, 42.92) * mm});
            skLineSegment(sketch, "E2974", {"start": v(-714.5, 41.82) * mm, "end": v(-713.5, 41.82) * mm});
            skLineSegment(sketch, "E2975", {"start": v(-713.5, 41.82) * mm, "end": v(-713.5, 38.42) * mm});
            skLineSegment(sketch, "E2976", {"start": v(-713.5, 38.42) * mm, "end": v(-714.5, 38.42) * mm});
            skLineSegment(sketch, "E2977", {"start": v(-714.5, 37.32) * mm, "end": v(-714.5, 38.42) * mm});
            skLineSegment(sketch, "E2978", {"start": v(-716.5, 37.32) * mm, "end": v(-714.5, 37.32) * mm});
            skLineSegment(sketch, "E2979", {"start": v(-716.5, 38.42) * mm, "end": v(-716.5, 37.32) * mm});
            skLineSegment(sketch, "E2980", {"start": v(-716.5, 38.42) * mm, "end": v(-721.5, 38.42) * mm});
            skLineSegment(sketch, "E2981", {"start": v(-721.5, 38.42) * mm, "end": v(-721.5, 27.82) * mm});
            skLineSegment(sketch, "E2982", {"start": v(-721.5, 27.82) * mm, "end": v(-716.5, 27.82) * mm});
            skLineSegment(sketch, "E2983", {"start": v(-716.5, 28.92) * mm, "end": v(-716.5, 27.82) * mm});
            skLineSegment(sketch, "E2984", {"start": v(-714.5, 28.92) * mm, "end": v(-716.5, 28.92) * mm});
            skLineSegment(sketch, "E2985", {"start": v(-714.5, 27.82) * mm, "end": v(-714.5, 28.92) * mm});
            skLineSegment(sketch, "E2986", {"start": v(-714.5, 27.82) * mm, "end": v(-713.5, 27.82) * mm});
            skLineSegment(sketch, "E2987", {"start": v(-713.5, 27.82) * mm, "end": v(-713.5, 24.42) * mm});
            skLineSegment(sketch, "E2988", {"start": v(-713.5, 24.42) * mm, "end": v(-714.5, 24.42) * mm});
            skLineSegment(sketch, "E2989", {"start": v(-714.5, 23.32) * mm, "end": v(-714.5, 24.42) * mm});
            skLineSegment(sketch, "E2990", {"start": v(-716.5, 23.32) * mm, "end": v(-714.5, 23.32) * mm});
            skCircle(sketch, "E2991", {"center": v(-694, 26.12) * mm, "radius": 1.6 * mm});
            skCircle(sketch, "E2992", {"center": v(-694, 40.12) * mm, "radius": 1.6 * mm});
            skLineSegment(sketch, "E2993", {"start": v(-184.5, 184.42) * mm, "end": v(-184.5, 183.32) * mm});
            skLineSegment(sketch, "E2994", {"start": v(-184.5, 184.42) * mm, "end": v(-189.5, 184.42) * mm});
            skLineSegment(sketch, "E2995", {"start": v(-189.5, 184.42) * mm, "end": v(-189.5, 178.12) * mm});
            skLineSegment(sketch, "E2996", {"start": v(-189.5, 178.12) * mm, "end": v(-159.5, 178.12) * mm});
            skLineSegment(sketch, "E2997", {"start": v(-159.5, 178.12) * mm, "end": v(-159.5, 208.12) * mm});
            skLineSegment(sketch, "E2998", {"start": v(-159.5, 208.12) * mm, "end": v(-189.5, 208.12) * mm});
            skLineSegment(sketch, "E2999", {"start": v(-189.5, 208.12) * mm, "end": v(-189.5, 201.82) * mm});
            skLineSegment(sketch, "E3000", {"start": v(-189.5, 201.82) * mm, "end": v(-184.5, 201.82) * mm});
            skLineSegment(sketch, "E3001", {"start": v(-184.5, 202.92) * mm, "end": v(-184.5, 201.82) * mm});
            skLineSegment(sketch, "E3002", {"start": v(-182.5, 202.92) * mm, "end": v(-184.5, 202.92) * mm});
            skLineSegment(sketch, "E3003", {"start": v(-182.5, 201.82) * mm, "end": v(-182.5, 202.92) * mm});
            skLineSegment(sketch, "E3004", {"start": v(-182.5, 201.82) * mm, "end": v(-181.5, 201.82) * mm});
            skLineSegment(sketch, "E3005", {"start": v(-181.5, 201.82) * mm, "end": v(-181.5, 198.42) * mm});
            skLineSegment(sketch, "E3006", {"start": v(-181.5, 198.42) * mm, "end": v(-182.5, 198.42) * mm});
            skLineSegment(sketch, "E3007", {"start": v(-182.5, 197.32) * mm, "end": v(-182.5, 198.42) * mm});
            skLineSegment(sketch, "E3008", {"start": v(-184.5, 197.32) * mm, "end": v(-182.5, 197.32) * mm});
            skLineSegment(sketch, "E3009", {"start": v(-184.5, 198.42) * mm, "end": v(-184.5, 197.32) * mm});
            skLineSegment(sketch, "E3010", {"start": v(-184.5, 198.42) * mm, "end": v(-189.5, 198.42) * mm});
            skLineSegment(sketch, "E3011", {"start": v(-189.5, 198.42) * mm, "end": v(-189.5, 187.82) * mm});
            skLineSegment(sketch, "E3012", {"start": v(-189.5, 187.82) * mm, "end": v(-184.5, 187.82) * mm});
            skLineSegment(sketch, "E3013", {"start": v(-184.5, 188.92) * mm, "end": v(-184.5, 187.82) * mm});
            skLineSegment(sketch, "E3014", {"start": v(-182.5, 188.92) * mm, "end": v(-184.5, 188.92) * mm});
            skLineSegment(sketch, "E3015", {"start": v(-182.5, 187.82) * mm, "end": v(-182.5, 188.92) * mm});
            skLineSegment(sketch, "E3016", {"start": v(-182.5, 187.82) * mm, "end": v(-181.5, 187.82) * mm});
            skLineSegment(sketch, "E3017", {"start": v(-181.5, 187.82) * mm, "end": v(-181.5, 184.42) * mm});
            skLineSegment(sketch, "E3018", {"start": v(-181.5, 184.42) * mm, "end": v(-182.5, 184.42) * mm});
            skLineSegment(sketch, "E3019", {"start": v(-182.5, 183.32) * mm, "end": v(-182.5, 184.42) * mm});
            skLineSegment(sketch, "E3020", {"start": v(-184.5, 183.32) * mm, "end": v(-182.5, 183.32) * mm});
            skCircle(sketch, "E3021", {"center": v(-162, 186.12) * mm, "radius": 1.6 * mm});
            skCircle(sketch, "E3022", {"center": v(-162, 200.12) * mm, "radius": 1.6 * mm});
            skLineSegment(sketch, "E3023", {"start": v(-595.87, 126.92) * mm, "end": v(-589.3, 126.92) * mm});
            skLineSegment(sketch, "E3024", {"start": v(-595.87, 131.92) * mm, "end": v(-595.87, 126.92) * mm});
            skLineSegment(sketch, "E3025", {"start": v(-594.77, 131.92) * mm, "end": v(-595.87, 131.92) * mm});
            skLineSegment(sketch, "E3026", {"start": v(-594.77, 133.92) * mm, "end": v(-594.77, 131.92) * mm});
            skLineSegment(sketch, "E3027", {"start": v(-595.87, 133.92) * mm, "end": v(-594.77, 133.92) * mm});
            skLineSegment(sketch, "E3028", {"start": v(-595.87, 134.92) * mm, "end": v(-595.87, 133.92) * mm});
            skLineSegment(sketch, "E3029", {"start": v(-599.47, 134.92) * mm, "end": v(-595.87, 134.92) * mm});
            skLineSegment(sketch, "E3030", {"start": v(-599.47, 133.92) * mm, "end": v(-599.47, 134.92) * mm});
            skLineSegment(sketch, "E3031", {"start": v(-600.57, 133.92) * mm, "end": v(-599.47, 133.92) * mm});
            skLineSegment(sketch, "E3032", {"start": v(-600.57, 131.92) * mm, "end": v(-600.57, 133.92) * mm});
            skLineSegment(sketch, "E3033", {"start": v(-599.47, 131.92) * mm, "end": v(-600.57, 131.92) * mm});
            skLineSegment(sketch, "E3034", {"start": v(-599.47, 126.92) * mm, "end": v(-599.47, 131.92) * mm});
            skLineSegment(sketch, "E3035", {"start": v(-606.63, 126.92) * mm, "end": v(-599.47, 126.92) * mm});
            skLineSegment(sketch, "E3036", {"start": v(-606.63, 121.92) * mm, "end": v(-606.63, 126.92) * mm});
            skLineSegment(sketch, "E3037", {"start": v(-616.63, 121.92) * mm, "end": v(-606.63, 121.92) * mm});
            skLineSegment(sketch, "E3038", {"start": v(-616.63, 126.92) * mm, "end": v(-616.63, 121.92) * mm});
            skLineSegment(sketch, "E3039", {"start": v(-627.8, 126.92) * mm, "end": v(-616.63, 126.92) * mm});
            skLineSegment(sketch, "E3040", {"start": v(-627.8, 131.56) * mm, "end": v(-627.8, 126.92) * mm});
            skArc(sketch, "E3041", {"start": v(-639.48, 144.94) * mm, "mid": v(-636.28, 135.94) * mm, "end": v(-627.8, 131.56) * mm});
            skLineSegment(sketch, "E3042", {"start": v(-639.3, 150.36) * mm, "end": v(-639.48, 144.94) * mm});
            skArc(sketch, "E3043", {"start": v(-637.86, 151.74) * mm, "mid": v(-638.86, 151.34) * mm, "end": v(-639.3, 150.36) * mm});
            skLineSegment(sketch, "E3044", {"start": v(-634.22, 151.74) * mm, "end": v(-637.86, 151.74) * mm});
            skArc(sketch, "E3045", {"start": v(-632.8, 150.31) * mm, "mid": v(-633.21, 151.32) * mm, "end": v(-634.22, 151.74) * mm});
            skLineSegment(sketch, "E3046", {"start": v(-632.8, 146.53) * mm, "end": v(-632.8, 150.31) * mm});
            skArc(sketch, "E3047", {"start": v(-632.8, 146.53) * mm, "mid": v(-632.7, 146.33) * mm, "end": v(-632.5, 146.24) * mm});
            skLineSegment(sketch, "E3048", {"start": v(-624.81, 146.24) * mm, "end": v(-632.5, 146.24) * mm});
            skArc(sketch, "E3049", {"start": v(-623.8, 145.67) * mm, "mid": v(-624.23, 146.09) * mm, "end": v(-624.81, 146.24) * mm});
            skLineSegment(sketch, "E3050", {"start": v(-621.45, 141.8) * mm, "end": v(-623.8, 145.67) * mm});
            skArc(sketch, "E3051", {"start": v(-621.45, 141.8) * mm, "mid": v(-621.02, 141.4) * mm, "end": v(-620.44, 141.24) * mm});
            skLineSegment(sketch, "E3052", {"start": v(-542.45, 141.24) * mm, "end": v(-620.44, 141.24) * mm});
            skArc(sketch, "E3053", {"start": v(-542.45, 141.24) * mm, "mid": v(-541.9, 141.44) * mm, "end": v(-541.59, 141.95) * mm});
            skLineSegment(sketch, "E3054", {"start": v(-540.14, 149.49) * mm, "end": v(-541.59, 141.95) * mm});
            skArc(sketch, "E3055", {"start": v(-539.83, 149.74) * mm, "mid": v(-540.03, 149.67) * mm, "end": v(-540.14, 149.49) * mm});
            skLineSegment(sketch, "E3056", {"start": v(-537.32, 149.74) * mm, "end": v(-539.83, 149.74) * mm});
            skArc(sketch, "E3057", {"start": v(-537.02, 149.43) * mm, "mid": v(-537.1, 149.65) * mm, "end": v(-537.32, 149.74) * mm});
            skLineSegment(sketch, "E3058", {"start": v(-537.3, 138.18) * mm, "end": v(-537.02, 149.43) * mm});
            skArc(sketch, "E3059", {"start": v(-555.55, 121.92) * mm, "mid": v(-542.9, 126.1) * mm, "end": v(-537.3, 138.18) * mm});
            skLineSegment(sketch, "E3060", {"start": v(-555.55, 126.92) * mm, "end": v(-555.55, 121.92) * mm});
            skLineSegment(sketch, "E3061", {"start": v(-565.87, 126.92) * mm, "end": v(-555.55, 126.92) * mm});
            skLineSegment(sketch, "E3062", {"start": v(-565.87, 131.92) * mm, "end": v(-565.87, 126.92) * mm});
            skLineSegment(sketch, "E3063", {"start": v(-564.77, 131.92) * mm, "end": v(-565.87, 131.92) * mm});
            skLineSegment(sketch, "E3064", {"start": v(-564.77, 133.92) * mm, "end": v(-564.77, 131.92) * mm});
            skLineSegment(sketch, "E3065", {"start": v(-565.87, 133.92) * mm, "end": v(-564.77, 133.92) * mm});
            skLineSegment(sketch, "E3066", {"start": v(-565.87, 134.92) * mm, "end": v(-565.87, 133.92) * mm});
            skLineSegment(sketch, "E3067", {"start": v(-569.47, 134.92) * mm, "end": v(-565.87, 134.92) * mm});
            skLineSegment(sketch, "E3068", {"start": v(-569.47, 133.92) * mm, "end": v(-569.47, 134.92) * mm});
            skLineSegment(sketch, "E3069", {"start": v(-570.57, 133.92) * mm, "end": v(-569.47, 133.92) * mm});
            skLineSegment(sketch, "E3070", {"start": v(-570.57, 131.92) * mm, "end": v(-570.57, 133.92) * mm});
            skLineSegment(sketch, "E3071", {"start": v(-569.47, 131.92) * mm, "end": v(-570.57, 131.92) * mm});
            skLineSegment(sketch, "E3072", {"start": v(-569.47, 126.92) * mm, "end": v(-569.47, 131.92) * mm});
            skLineSegment(sketch, "E3073", {"start": v(-573.62, 126.92) * mm, "end": v(-569.47, 126.92) * mm});
            skLineSegment(sketch, "E3074", {"start": v(-573.62, 121.92) * mm, "end": v(-573.62, 126.92) * mm});
            skLineSegment(sketch, "E3075", {"start": v(-589.3, 121.92) * mm, "end": v(-573.62, 121.92) * mm});
            skLineSegment(sketch, "E3076", {"start": v(-589.3, 126.92) * mm, "end": v(-589.3, 121.92) * mm});
            skLineSegment(sketch, "E3077", {"start": v(-595.87, 147.92) * mm, "end": v(-589.3, 147.92) * mm});
            skLineSegment(sketch, "E3078", {"start": v(-595.87, 152.92) * mm, "end": v(-595.87, 147.92) * mm});
            skLineSegment(sketch, "E3079", {"start": v(-594.77, 152.92) * mm, "end": v(-595.87, 152.92) * mm});
            skLineSegment(sketch, "E3080", {"start": v(-594.77, 154.92) * mm, "end": v(-594.77, 152.92) * mm});
            skLineSegment(sketch, "E3081", {"start": v(-595.87, 154.92) * mm, "end": v(-594.77, 154.92) * mm});
            skLineSegment(sketch, "E3082", {"start": v(-595.87, 155.92) * mm, "end": v(-595.87, 154.92) * mm});
            skLineSegment(sketch, "E3083", {"start": v(-599.47, 155.92) * mm, "end": v(-595.87, 155.92) * mm});
            skLineSegment(sketch, "E3084", {"start": v(-599.47, 154.92) * mm, "end": v(-599.47, 155.92) * mm});
            skLineSegment(sketch, "E3085", {"start": v(-600.57, 154.92) * mm, "end": v(-599.47, 154.92) * mm});
            skLineSegment(sketch, "E3086", {"start": v(-600.57, 152.92) * mm, "end": v(-600.57, 154.92) * mm});
            skLineSegment(sketch, "E3087", {"start": v(-599.47, 152.92) * mm, "end": v(-600.57, 152.92) * mm});
            skLineSegment(sketch, "E3088", {"start": v(-599.47, 147.92) * mm, "end": v(-599.47, 152.92) * mm});
            skLineSegment(sketch, "E3089", {"start": v(-606.63, 147.92) * mm, "end": v(-599.47, 147.92) * mm});
            skLineSegment(sketch, "E3090", {"start": v(-606.63, 142.92) * mm, "end": v(-606.63, 147.92) * mm});
            skLineSegment(sketch, "E3091", {"start": v(-616.63, 142.92) * mm, "end": v(-606.63, 142.92) * mm});
            skLineSegment(sketch, "E3092", {"start": v(-616.63, 147.92) * mm, "end": v(-616.63, 142.92) * mm});
            skLineSegment(sketch, "E3093", {"start": v(-627.8, 147.92) * mm, "end": v(-616.63, 147.92) * mm});
            skLineSegment(sketch, "E3094", {"start": v(-627.8, 152.56) * mm, "end": v(-627.8, 147.92) * mm});
            skArc(sketch, "E3095", {"start": v(-639.48, 165.94) * mm, "mid": v(-636.28, 156.94) * mm, "end": v(-627.8, 152.56) * mm});
            skLineSegment(sketch, "E3096", {"start": v(-639.3, 171.36) * mm, "end": v(-639.48, 165.94) * mm});
            skArc(sketch, "E3097", {"start": v(-637.86, 172.74) * mm, "mid": v(-638.86, 172.34) * mm, "end": v(-639.3, 171.36) * mm});
            skLineSegment(sketch, "E3098", {"start": v(-634.22, 172.74) * mm, "end": v(-637.86, 172.74) * mm});
            skArc(sketch, "E3099", {"start": v(-632.8, 171.31) * mm, "mid": v(-633.21, 172.32) * mm, "end": v(-634.22, 172.74) * mm});
            skLineSegment(sketch, "E3100", {"start": v(-632.8, 167.53) * mm, "end": v(-632.8, 171.31) * mm});
            skArc(sketch, "E3101", {"start": v(-632.8, 167.53) * mm, "mid": v(-632.7, 167.33) * mm, "end": v(-632.5, 167.24) * mm});
            skLineSegment(sketch, "E3102", {"start": v(-624.81, 167.24) * mm, "end": v(-632.5, 167.24) * mm});
            skArc(sketch, "E3103", {"start": v(-623.8, 166.67) * mm, "mid": v(-624.23, 167.09) * mm, "end": v(-624.81, 167.24) * mm});
            skLineSegment(sketch, "E3104", {"start": v(-621.45, 162.8) * mm, "end": v(-623.8, 166.67) * mm});
            skArc(sketch, "E3105", {"start": v(-621.45, 162.8) * mm, "mid": v(-621.02, 162.4) * mm, "end": v(-620.44, 162.24) * mm});
            skLineSegment(sketch, "E3106", {"start": v(-542.45, 162.24) * mm, "end": v(-620.44, 162.24) * mm});
            skArc(sketch, "E3107", {"start": v(-542.45, 162.24) * mm, "mid": v(-541.9, 162.44) * mm, "end": v(-541.59, 162.95) * mm});
            skLineSegment(sketch, "E3108", {"start": v(-540.14, 170.49) * mm, "end": v(-541.59, 162.95) * mm});
            skArc(sketch, "E3109", {"start": v(-539.83, 170.74) * mm, "mid": v(-540.03, 170.67) * mm, "end": v(-540.14, 170.49) * mm});
            skLineSegment(sketch, "E3110", {"start": v(-537.32, 170.74) * mm, "end": v(-539.83, 170.74) * mm});
            skArc(sketch, "E3111", {"start": v(-537.02, 170.43) * mm, "mid": v(-537.1, 170.65) * mm, "end": v(-537.32, 170.74) * mm});
            skLineSegment(sketch, "E3112", {"start": v(-537.3, 159.18) * mm, "end": v(-537.02, 170.43) * mm});
            skArc(sketch, "E3113", {"start": v(-555.55, 142.92) * mm, "mid": v(-542.9, 147.1) * mm, "end": v(-537.3, 159.18) * mm});
            skLineSegment(sketch, "E3114", {"start": v(-555.55, 147.92) * mm, "end": v(-555.55, 142.92) * mm});
            skLineSegment(sketch, "E3115", {"start": v(-565.87, 147.92) * mm, "end": v(-555.55, 147.92) * mm});
            skLineSegment(sketch, "E3116", {"start": v(-565.87, 152.92) * mm, "end": v(-565.87, 147.92) * mm});
            skLineSegment(sketch, "E3117", {"start": v(-564.77, 152.92) * mm, "end": v(-565.87, 152.92) * mm});
            skLineSegment(sketch, "E3118", {"start": v(-564.77, 154.92) * mm, "end": v(-564.77, 152.92) * mm});
            skLineSegment(sketch, "E3119", {"start": v(-565.87, 154.92) * mm, "end": v(-564.77, 154.92) * mm});
            skLineSegment(sketch, "E3120", {"start": v(-565.87, 155.92) * mm, "end": v(-565.87, 154.92) * mm});
            skLineSegment(sketch, "E3121", {"start": v(-569.47, 155.92) * mm, "end": v(-565.87, 155.92) * mm});
            skLineSegment(sketch, "E3122", {"start": v(-569.47, 154.92) * mm, "end": v(-569.47, 155.92) * mm});
            skLineSegment(sketch, "E3123", {"start": v(-570.57, 154.92) * mm, "end": v(-569.47, 154.92) * mm});
            skLineSegment(sketch, "E3124", {"start": v(-570.57, 152.92) * mm, "end": v(-570.57, 154.92) * mm});
            skLineSegment(sketch, "E3125", {"start": v(-569.47, 152.92) * mm, "end": v(-570.57, 152.92) * mm});
            skLineSegment(sketch, "E3126", {"start": v(-569.47, 147.92) * mm, "end": v(-569.47, 152.92) * mm});
            skLineSegment(sketch, "E3127", {"start": v(-573.62, 147.92) * mm, "end": v(-569.47, 147.92) * mm});
            skLineSegment(sketch, "E3128", {"start": v(-573.62, 142.92) * mm, "end": v(-573.62, 147.92) * mm});
            skLineSegment(sketch, "E3129", {"start": v(-589.3, 142.92) * mm, "end": v(-573.62, 142.92) * mm});
            skLineSegment(sketch, "E3130", {"start": v(-589.3, 147.92) * mm, "end": v(-589.3, 142.92) * mm});
            skArc(sketch, "E3131", {"start": v(10.44, 15.68) * mm, "mid": v(9.92, 16.25) * mm, "end": v(9.27, 16.65) * mm});
            const initialGuessF0  = {"E462": [1.3256302780000002, -1.819407476, 1249.297366, -1835.68936, 2.220472773, 0.100284257, 3.135331, 3.172319], "E463": [-0.19371243100000002, -0.360973371, 274.008891, 375.661636, 0.464975846, 0.025713425999999998, 6.266996, 6.3235], "E464": [0.273542915, -0.413097991, -195.147828, 427.917903, 0.47031522000000003, 0.029399032, 6.254686, 6.308034], "E465": [5.471984658999999, 7.5295958789999995, 5394.300446, 7519.547961, 9.254300558999999, 0.113839802, 3.13769, 3.150417], "E466": [-0.13886124000000002, -0.087464569, 178.637584, 103.37686, 0.20639322100000002, 0.020016120999999998, 6.282364, 6.353728], "E473": [0.039642515, 0.074042712, 44.859051, 64.681588, 0.07871494300000001, 0.008427206, 3.119806, 3.215707], "E474": [-0.504099533, -0.6359253659999999, 500.495203, 647.62164, 0.818479833, 0.027151196, 6.275866, 6.308816], "E476": [-0.14883820300000003, 0.156077857, 147.21145, -147.400404, 0.208322083, 0.025821148000000002, 6.259048, 6.326685], "E477": [-0.04549617699999999, -0.033461003, 42.029538, 48.831151, 0.064427971, 0.006595265, 6.269734, 6.371066], "E478": [0.02064247499999999, -0.032974590000000005, -25.260338, 48.407349, 0.054601796, 0.007571332, 6.210952, 6.317104], "E479": [0.18803007400000002, -0.194764738, 194.778643, -210.977915, 0.287141777, 0.030613656, 3.086842, 3.158418], "E490": [0.035387490000000014, 0.055436627000000016, -18.45394, 24.699423, 0.030831954, 0.019976320000000002, 2.529246, 3.591689], "E491": [0.060319103999999985, 0.055425342, 24.023922, 24.343674, 0.034201802999999996, 0.0179959, 2.663394, 3.726078], "E492": [-0.28268848500000004, -0.378630631, -310.126541, -395.051678, 0.502239285, 0.037569053, 3.140566, 3.20234], "E494": [0.12250989100000004, -0.19266687400000002, -98.765999, 207.50473, 0.229810652, 0.020187107000000003, 6.241399, 6.327988], "E513": [-0.05504477600000002, -0.03518546499999999, 149.166162, 51.423383, 0.157781203, 0.00934319, 6.113074, 6.206253], "E514": [0.02964813300000003, 0.030034862000000006, 64.187299, -17.220486, 0.066457163, 0.0069013090000000004, 0.105088, 0.196133], "E516": [0.083344919, 0.011537202000000009, 9.785458, -0.299294, 0.009790034000000001, 0.001392107, 5.852936, 6.092617], "E520": [0.065213505, 0.036913596000000014, 28.503501, -26.68359, 0.03904438, 0.001682575, 6.080593, 6.192753], "E526": [0.09266680500000002, -0.03140526699999998, -2.934897, 42.781386, 0.042881938, 0.002948644, 6.087133, 6.221106], "E527": [-0.01694365399999998, 0.238700875, -108.294205, 225.247329, 0.249927978, 0.014372199, 3.126553, 3.166124], "E529": [0.07644685800000002, 0.02010065800000001, 15.361466, -6.14731, 0.016545817, 0.003916375, 6.20051, 6.349698], "E538": [-0.004456919999999968, -0.085924816, 84.87477, 100.506478, 0.13154953, 0.012487018, 6.144085, 6.262522], "E569": [0.02930717500000003, 0.028746414000000015, -7.327506, 15.293309, 0.016958115, 0.003750645, 3.084252, 3.236032], "E572": [-0.06895164299999999, 0.221117256, -93.653923, 211.25472, 0.231083564, 0.019490760000000003, 3.173317, 3.236119], "E576": [-0.085806666, 0.16450093300000004, 112.543255, -156.066711, 0.192413104, 0.027292542000000003, 6.183501, 6.250238], "E577": [0.082477982, -0.108182399, -58.985331, 122.809517, 0.13624040099999998, 0.012677691, 0.046337, 0.150003], "E578": [-0.07588033799999999, 0.16918902400000002, 102.407029, -160.903398, 0.190727824, 0.027284848, 6.241085, 6.306886], "E581": [0.008095749000000011, -0.00630029399999998, 17.480527, 20.987789, 0.027314028, 0.006132647000000001, 6.20928, 6.328359], "E582": [0.16760337200000003, 0.30151095200000005, -146.166233, -293.433798, 0.327823064, 0.029928695999999998, 6.281998, 6.34919], "E584": [0.436356501, 0.34839680900000003, 416.0265, 339.318777, 0.536856854, 0.040336125, 3.1569, 3.217202], "E587": [0.857065511, -1.14949587, 835.488425, -1165.740535, 1.4342217069999998, 0.078817676, 3.135079, 3.180959], "E592": [0.12783909600000004, -0.045541127999999986, -87.899616, 111.181219, 0.141730752, 0.040852501, 5.996093, 6.506846], "E593": [-0.05356138900000002, -0.04567007899999999, 111.669443, 111.138637, 0.157549551, 0.036812697, 6.052982, 6.56344], "E600": [-0.188963133, -0.177158399, 199.109973, 193.197441, 0.277434736, 0.027579562, 6.266361, 6.321252], "E601": [-0.28223727600000004, 0.739204223, 291.820539, -729.974142, 0.7861434190000001, 0.032540366, 6.204784, 6.247436], "E602": [-0.114477936, -0.039584945, 125.101521, 55.118007, 0.136705469, 0.026958591, 0.05105, 0.11239], "E603": [0.0008427849999999922, 0.062764838, 6.836225, -54.801008, 0.055225759, 0.012478224000000001, 6.137809, 6.253575], "E604": [-0.08057629500000002, -0.04835444399999999, 90.993534, 64.068474, 0.11128608400000001, 0.019106283, 0.002251, 0.082804], "E606": [-0.188963133, -0.177158399, 199.109973, 193.197441, 0.277434736, 0.027579562, 6.245119, 6.30001], "E608": [-1.132292238, -0.732732843, 1142.334333, 748.752059, 1.365854082, 0.045627656, 6.232264, 6.262322], "E611": [-1.050432739, -1.689574531, 1058.14597, 1704.130332, 2.005924495, 0.038957936, 6.243079, 6.276042], "E612": [-0.187968032, 0.8097826330000001, -195.357608, 799.407263, 0.822931691, 0.019210695, 3.167547, 3.206623], "E613": [-0.471278845, -0.362415739, 479.198119, 376.78558, 0.6095885590000001, 0.025571745, 6.282971, 6.336486], "E616": [-0.123244623, 0.062050538000000016, 130.680007, -51.696369, 0.14053390600000001, 0.007592996, 6.147447, 6.234495], "E800": [-2.381141413, -2.550131262, -2463.862548, -2566.211324, 3.557535553, 0.106948336, 3.112737, 3.143756], "E801": [-0.469747843, -0.391032127, 552.838401, 406.690701, 0.6863145230000001, 0.047401584999999996, 6.276245, 6.346057], "E802": [-0.05249275799999998, 0.174610138, 134.631703, -165.714348, 0.21351098500000001, 0.027521419000000002, 6.155465, 6.239634], "E819": [-0.20644730100000003, -0.06939076899999999, 245.856499, 85.627429, 0.260341074, 0.012062294, 6.15093, 6.223337], "E820": [-0.047988315999999996, -0.09180082299999999, -87.314329, -108.244552, 0.139070755, 0.015773667, 3.09948, 3.184005], "E823": [-0.00559189600000002, 0.024271134000000017, 44.702627, -11.463893, 0.046149168000000004, 0.005646541000000001, 0.126148, 0.236222], "E824": [0.02857412199999999, 0.011538028999999995, 9.838619, -0.297395, 0.009843113, 0.00139206, 5.854765, 6.094506], "E830": [0.041783334000000026, -0.10593517999999999, -6.765609, 117.311424, 0.11750635599999999, 0.004946471, 6.165324, 6.246122], "E861": [0.540839297, -0.503337269, 547.64172, -519.483823, 0.75483435, 0.04448661, 3.155005, 3.203643], "E862": [-15.136021877, -9.498274941, 15134.965724, 9514.442125, 17.877130543, 0.161390881, 6.268825, 6.28072], "E864": [-0.127765851, 0.059833089, 126.968219, -45.534241, 0.134886233, 0.016570440999999998, 6.253254, 6.323631], "E867": [-0.05385811899999999, -0.029371319, 52.855063, 41.541243, 0.067225981, 0.010574234, 6.23061, 6.323088], "E870": [-0.161178337, 0.146814882, 159.468658, -138.155121, 0.210990735, 0.022414767000000002, 0.046328, 0.122016], "E876": [-0.04402567599999998, 0.042272032999999994, 40.4503, -32.592475, 0.051947051, 0.008536953, 6.264301, 6.389059], "E880": [-0.044905169, 0.11457486, -40.901686, 100.925094, 0.108898221, 0.011665905, 3.098205, 3.177896], "E1579": [0.10828756899999996, -0.360973371, 274.008891, 375.661636, 0.464975846, 0.025713425999999998, 6.266996, 6.3235], "E1580": [0.575542915, -0.413097991, -195.147828, 427.917903, 0.47031522000000003, 0.029399032, 6.254686, 6.308034], "E1581": [1.627630278, -1.819407476, 1249.297366, -1835.68936, 2.220472773, 0.100284257, 3.135331, 3.172319], "E1582": [-2.079141413, -2.550131262, -2463.862548, -2566.211324, 3.557535553, 0.106948336, 3.112737, 3.143756], "E1583": [-0.16774784299999998, -0.391032127, 552.838401, 406.690701, 0.6863145230000001, 0.047401584999999996, 6.276245, 6.346057], "E1585": [0.331307175, 0.028746414000000015, -7.327506, 15.293309, 0.016958115, 0.003750645, 3.084252, 3.236032], "E1586": [0.25401168400000007, -0.09180082299999999, -87.314329, -108.244552, 0.139070755, 0.015773667, 3.09948, 3.184005], "E1587": [0.16313876000000005, -0.087464569, 178.637584, 103.37686, 0.20639322100000002, 0.020016120999999998, 6.282364, 6.353728], "E1592": [0.019311514999999987, -0.378630631, -310.126541, -395.051678, 0.502239285, 0.037569053, 3.140566, 3.20234], "E1593": [0.310095749, -0.00630029399999998, 17.480527, 20.987789, 0.027314028, 0.006132647000000001, 6.20928, 6.328359], "E1595": [0.42450989100000003, -0.19266687400000002, -98.765999, 207.50473, 0.229810652, 0.020187107000000003, 6.241399, 6.327988], "E1596": [0.22611966199999994, 0.16918902400000002, 102.407029, -160.903398, 0.190727824, 0.027284848, 6.241085, 6.306886], "E1597": [0.469603372, 0.30151095200000005, -146.166233, -293.433798, 0.327823064, 0.029928695999999998, 6.281998, 6.34919], "E1598": [1.1590655109999999, -1.14949587, 835.488425, -1165.740535, 1.4342217069999998, 0.078817676, 3.135079, 3.180959], "E1599": [0.174234149, 0.059833089, 126.968219, -45.534241, 0.134886233, 0.016570440999999998, 6.253254, 6.323631], "E1600": [0.248141881, -0.029371319, 52.855063, 41.541243, 0.067225981, 0.010574234, 6.23061, 6.323088], "E1602": [0.153161797, 0.156077857, 147.21145, -147.400404, 0.208322083, 0.025821148000000002, 6.259048, 6.326685], "E1604": [0.34164251500000004, 0.074042712, 44.859051, 64.681588, 0.07871494300000001, 0.008427206, 3.119806, 3.215707], "E1606": [0.25797432400000003, 0.042272032999999994, 40.4503, -32.592475, 0.051947051, 0.008536953, 6.264301, 6.389059], "E1607": [-0.20209953300000003, -0.6359253659999999, 500.495203, 647.62164, 0.818479833, 0.027151196, 6.275866, 6.308816], "E1609": [0.257094831, 0.11457486, -40.901686, 100.925094, 0.108898221, 0.011665905, 3.098205, 3.177896], "E1611": [0.256503823, -0.033461003, 42.029538, 48.831151, 0.064427971, 0.006595265, 6.269734, 6.371066], "E1612": [0.322642475, -0.032974590000000005, -25.260338, 48.407349, 0.054601796, 0.007571332, 6.210952, 6.317104], "E1613": [0.49003007400000004, -0.194764738, 194.778643, -210.977915, 0.287141777, 0.030613656, 3.086842, 3.158418], "E1614": [-0.169278843, -0.36241573699999996, 479.198118, 376.785579, 0.609588557, 0.025571745, 6.282971, 6.336486], "E1615": [0.11303686700000003, -0.177158399, 199.109973, 193.197441, 0.277434736, 0.027579562, 6.245119, 6.30001], "E1617": [0.28505634599999996, 0.238700875, -108.294205, 225.247329, 0.249927978, 0.014372199, 3.126553, 3.166124], "E1618": [0.37844685800000005, 0.02010065800000001, 15.361466, -6.14731, 0.016545817, 0.003916375, 6.20051, 6.349698], "E1810": [0.39466680499999995, -0.03140526699999998, -2.934897, 42.781386, 0.042881938, 0.002948644, 6.087133, 6.221106], "E1816": [0.24695522400000006, -0.03518546499999999, 149.166162, 51.423383, 0.157781203, 0.00934319, 6.113074, 6.206253], "E1818": [0.331648133, 0.030034862000000006, 64.187299, -17.220486, 0.066457163, 0.0069013090000000004, 0.105089, 0.196133], "E1819": [0.385344919, 0.011537202000000009, 9.785458, -0.299294, 0.009790034000000001, 0.001392107, 5.852936, 6.092617], "E1821": [0.36721350500000005, 0.036913596000000014, 28.503501, -26.68359, 0.03904438, 0.001682575, 6.080593, 6.192753], "E1878": [-0.830292238, -0.732732843, 1142.334333, 748.752059, 1.365854082, 0.045627656, 6.232264, 6.262322], "E1879": [0.22142370500000005, -0.04835444399999999, 90.993534, 64.068474, 0.11128608400000001, 0.019106283, 0.002251, 0.082804], "E1880": [0.18752206400000002, -0.039584945, 125.101521, 55.118007, 0.136705469, 0.026958591, 0.05105, 0.11239], "E1881": [0.019762723999999992, 0.739204223, 291.820539, -729.974142, 0.7861434190000001, 0.032540366, 6.204784, 6.247435], "E1882": [0.30284278500000006, 0.062764838, 6.836225, -54.801008, 0.055225759, 0.012478224000000001, 6.137809, 6.253575], "E1932": [0.8428392970000002, -0.503337269, 547.64172, -519.483823, 0.75483435, 0.04448661, 3.155005, 3.203643], "E1933": [-14.834021877, -9.498274941, 15134.965724, 9514.442125, 17.877130543, 0.161390881, 6.268825, 6.28072], "E1938": [0.14082166300000007, 0.146814882, 159.468658, -138.155121, 0.210990735, 0.022414767000000002, 0.046328, 0.122016], "E1952": [0.384477982, -0.108182399, -58.985331, 122.809517, 0.13624040099999998, 0.012677691, 0.046337, 0.150003], "E1956": [0.233048357, 0.221117256, -93.653923, 211.25472, 0.231083564, 0.019490760000000003, 3.173317, 3.236119], "E1958": [0.21619333400000004, 0.16450093300000004, 112.543255, -156.066711, 0.192413104, 0.027292542000000003, 6.183501, 6.250238], "E1961": [0.738356501, 0.34839680900000003, 416.0265, 339.318777, 0.536856854, 0.040336125, 3.1569, 3.217202], "E1966": [0.09555269899999996, -0.06939076899999999, 245.856499, 85.627429, 0.260341074, 0.012062294, 6.15093, 6.223337], "E1967": [0.296408104, 0.024271134000000017, 44.702627, -11.463893, 0.046149168000000004, 0.005646541000000001, 0.126149, 0.236222], "E1968": [0.33057412199999997, 0.011538028999999995, 9.838619, -0.297395, 0.009843113, 0.00139206, 5.854765, 6.094506], "E1973": [0.343783334, -0.10593517999999999, -6.765609, 117.311424, 0.11750635599999999, 0.004946471, 6.165324, 6.246122], "E1976": [0.36231910400000006, 0.055425342, 24.023922, 24.343674, 0.034201802999999996, 0.0179959, 2.663394, 3.726078], "E1978": [0.42983909600000003, -0.04554112699999999, -87.899616, 111.181219, 0.141730752, 0.040852501, 5.996093, 6.506846], "E1979": [0.24843861100000003, -0.04567008, 111.669443, 111.138637, 0.157549552, 0.036812697, 6.052982, 6.56344], "E1981": [0.33738748999999996, 0.055436627000000016, -18.45394, 24.699423, 0.030831954, 0.019976320000000002, 2.529246, 3.591689], "E1994": [0.24950724200000002, 0.174610138, 134.631703, -165.714348, 0.21351098500000001, 0.027521419000000002, 6.155465, 6.239634], "E2013": [-0.748432739, -1.689574531, 1058.14597, 1704.130332, 2.005924495, 0.038957936, 6.243079, 6.276042], "E2014": [0.11403196800000001, 0.8097826330000001, -195.357608, 799.407263, 0.822931691, 0.019210695, 3.167547, 3.206623], "E2016": [0.17875537699999997, 0.062050538000000016, 130.680007, -51.696369, 0.14053390600000001, 0.007592996, 6.147447, 6.234495], "E2038": [0.29754308, -0.085924816, 84.87477, 100.506478, 0.13154953, 0.012487018, 6.144085, 6.262522], "E2041": [5.773984659, 7.5295958789999995, 5394.300446, 7519.547961, 9.254300558999999, 0.113839802, 3.13769, 3.150417]};
            skSetInitialGuess(sketch, initialGuessF0);
            skSolve(sketch);
        }
        {
            var Q0;
            Q0 = qSketchRegion(id + "F0", true);
            var Q1;
            Q1=makeQuery(id+"F0.imprint","IMPRINT",FACE,{"disambiguationData":[TD([[makeQuery(id+"F0.imprint","IMPRINT",EDGE,{"derivedFrom":sQuery(id+"F0.wireOp",EDGE,"E1073")}),-1.0]])]});
            var Q2;
            Q2=sQuery(id+"F0.wireOp",EDGE,"E447");
            extrude(context, id + "F1", {"entities" : qUnion([Q0, Q1]), "bodyType" : ToolBodyType.SURFACE, "surfaceEntities" : qUnion([Q2]), "depth" : 25 * mm, "offsetDistance" : 25 * mm});
        }
    });
